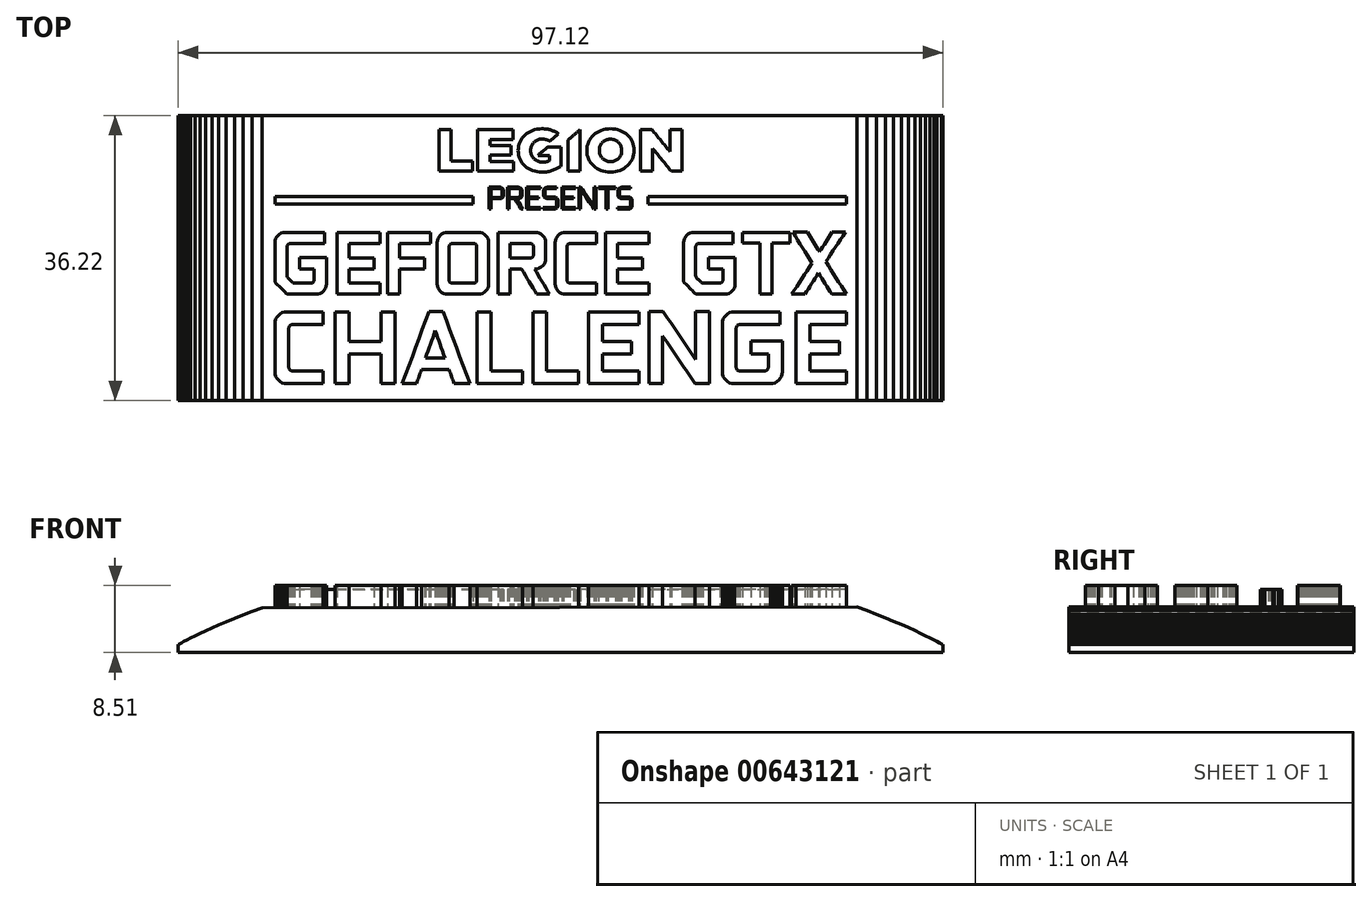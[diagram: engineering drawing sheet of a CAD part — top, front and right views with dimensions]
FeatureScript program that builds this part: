
annotation { "Feature Type Name" : "Feature", "Feature Type Description" : "" }
export const myFeature = defineFeature(function(context is Context, id is Id, definition is map)
    precondition{}
    {
        {
            var Q0;
            Q0=qCreatedBy(makeId("Front.planeOp"),FACE);
            var sketch = newSketch(context, id + "F0", { "sketchPlane" : qUnion([Q0])});
            skLineSegment(sketch, "E0", {"start": v(48.56, -5) * mm, "end": v(48.52, -4.97) * mm});
            skLineSegment(sketch, "E1", {"start": v(48.52, -4.97) * mm, "end": v(48.41, -4.86) * mm});
            skLineSegment(sketch, "E2", {"start": v(48.41, -4.86) * mm, "end": v(48.22, -4.68) * mm});
            skLineSegment(sketch, "E3", {"start": v(48.22, -4.68) * mm, "end": v(47.95, -4.43) * mm});
            skLineSegment(sketch, "E4", {"start": v(47.95, -4.43) * mm, "end": v(47.6, -4.12) * mm});
            skLineSegment(sketch, "E5", {"start": v(47.6, -4.12) * mm, "end": v(47.17, -3.75) * mm});
            skLineSegment(sketch, "E6", {"start": v(47.17, -3.75) * mm, "end": v(46.64, -3.33) * mm});
            skLineSegment(sketch, "E7", {"start": v(46.64, -3.33) * mm, "end": v(46.03, -2.86) * mm});
            skLineSegment(sketch, "E8", {"start": v(46.03, -2.86) * mm, "end": v(45.32, -2.34) * mm});
            skLineSegment(sketch, "E9", {"start": v(45.32, -2.34) * mm, "end": v(44.51, -1.78) * mm});
            skLineSegment(sketch, "E10", {"start": v(44.51, -1.78) * mm, "end": v(43.6, -1.18) * mm});
            skLineSegment(sketch, "E11", {"start": v(43.6, -1.18) * mm, "end": v(42.6, -0.55) * mm});
            skLineSegment(sketch, "E12", {"start": v(42.6, -0.55) * mm, "end": v(41.5, 0.11) * mm});
            skLineSegment(sketch, "E13", {"start": v(41.5, 0.11) * mm, "end": v(40.28, 0.8) * mm});
            skLineSegment(sketch, "E14", {"start": v(40.28, 0.8) * mm, "end": v(38.95, 1.51) * mm});
            skLineSegment(sketch, "E15", {"start": v(38.95, 1.51) * mm, "end": v(37.52, 2.24) * mm});
            skLineSegment(sketch, "E16", {"start": v(37.52, 2.24) * mm, "end": v(36.56, 2.61) * mm});
            skLineSegment(sketch, "E17", {"start": v(36.56, 2.61) * mm, "end": v(35.3, 2.96) * mm});
            skLineSegment(sketch, "E18", {"start": v(35.3, 2.96) * mm, "end": v(33.78, 3.27) * mm});
            skLineSegment(sketch, "E19", {"start": v(33.78, 3.27) * mm, "end": v(32, 3.55) * mm});
            skLineSegment(sketch, "E20", {"start": v(32, 3.55) * mm, "end": v(30, 3.8) * mm});
            skLineSegment(sketch, "E21", {"start": v(30, 3.8) * mm, "end": v(27.78, 4.03) * mm});
            skLineSegment(sketch, "E22", {"start": v(27.78, 4.03) * mm, "end": v(25.4, 4.23) * mm});
            skLineSegment(sketch, "E23", {"start": v(25.4, 4.23) * mm, "end": v(22.87, 4.4) * mm});
            skLineSegment(sketch, "E24", {"start": v(22.87, 4.4) * mm, "end": v(20.2, 4.56) * mm});
            skLineSegment(sketch, "E25", {"start": v(20.2, 4.56) * mm, "end": v(17.44, 4.68) * mm});
            skLineSegment(sketch, "E26", {"start": v(17.44, 4.68) * mm, "end": v(14.6, 4.79) * mm});
            skLineSegment(sketch, "E27", {"start": v(14.6, 4.79) * mm, "end": v(11.7, 4.87) * mm});
            skLineSegment(sketch, "E28", {"start": v(11.7, 4.87) * mm, "end": v(8.79, 4.93) * mm});
            skLineSegment(sketch, "E29", {"start": v(8.79, 4.93) * mm, "end": v(5.86, 4.98) * mm});
            skLineSegment(sketch, "E30", {"start": v(5.86, 4.98) * mm, "end": v(2.96, 5) * mm});
            skLineSegment(sketch, "E31", {"start": v(2.96, 5) * mm, "end": v(0.1, 5) * mm});
            skLineSegment(sketch, "E32", {"start": v(0.1, 5) * mm, "end": v(0.1, 5) * mm});
            skLineSegment(sketch, "E33", {"start": v(0.1, 5) * mm, "end": v(0.08, 5) * mm});
            skLineSegment(sketch, "E34", {"start": v(0.08, 5) * mm, "end": v(0.07, 5) * mm});
            skLineSegment(sketch, "E35", {"start": v(0.07, 5) * mm, "end": v(0.05, 5) * mm});
            skLineSegment(sketch, "E36", {"start": v(0.05, 5) * mm, "end": v(0.04, 5) * mm});
            skLineSegment(sketch, "E37", {"start": v(0.04, 5) * mm, "end": v(0.03, 5) * mm});
            skLineSegment(sketch, "E38", {"start": v(0.03, 5) * mm, "end": v(0.01, 5) * mm});
            skLineSegment(sketch, "E39", {"start": v(0.01, 5) * mm, "end": v(0, 5) * mm});
            skLineSegment(sketch, "E40", {"start": v(0, 5) * mm, "end": v(-0.01, 5) * mm});
            skLineSegment(sketch, "E41", {"start": v(-0.01, 5) * mm, "end": v(-0.03, 5) * mm});
            skLineSegment(sketch, "E42", {"start": v(-0.03, 5) * mm, "end": v(-0.04, 5) * mm});
            skLineSegment(sketch, "E43", {"start": v(-0.04, 5) * mm, "end": v(-0.05, 5) * mm});
            skLineSegment(sketch, "E44", {"start": v(-0.05, 5) * mm, "end": v(-0.07, 5) * mm});
            skLineSegment(sketch, "E45", {"start": v(-0.07, 5) * mm, "end": v(-0.08, 5) * mm});
            skLineSegment(sketch, "E46", {"start": v(-0.08, 5) * mm, "end": v(-0.1, 5) * mm});
            skLineSegment(sketch, "E47", {"start": v(-0.1, 5) * mm, "end": v(-0.1, 5) * mm});
            skLineSegment(sketch, "E48", {"start": v(-0.1, 5) * mm, "end": v(-2.96, 5) * mm});
            skLineSegment(sketch, "E49", {"start": v(-2.96, 5) * mm, "end": v(-5.86, 4.98) * mm});
            skLineSegment(sketch, "E50", {"start": v(-5.86, 4.98) * mm, "end": v(-8.79, 4.93) * mm});
            skLineSegment(sketch, "E51", {"start": v(-8.79, 4.93) * mm, "end": v(-11.7, 4.87) * mm});
            skLineSegment(sketch, "E52", {"start": v(-11.7, 4.87) * mm, "end": v(-14.6, 4.79) * mm});
            skLineSegment(sketch, "E53", {"start": v(-14.6, 4.79) * mm, "end": v(-17.44, 4.68) * mm});
            skLineSegment(sketch, "E54", {"start": v(-17.44, 4.68) * mm, "end": v(-20.2, 4.56) * mm});
            skLineSegment(sketch, "E55", {"start": v(-20.2, 4.56) * mm, "end": v(-22.87, 4.4) * mm});
            skLineSegment(sketch, "E56", {"start": v(-22.87, 4.4) * mm, "end": v(-25.4, 4.23) * mm});
            skLineSegment(sketch, "E57", {"start": v(-25.4, 4.23) * mm, "end": v(-27.79, 4.03) * mm});
            skLineSegment(sketch, "E58", {"start": v(-27.79, 4.03) * mm, "end": v(-30, 3.8) * mm});
            skLineSegment(sketch, "E59", {"start": v(-30, 3.8) * mm, "end": v(-32, 3.55) * mm});
            skLineSegment(sketch, "E60", {"start": v(-32, 3.55) * mm, "end": v(-33.78, 3.27) * mm});
            skLineSegment(sketch, "E61", {"start": v(-33.78, 3.27) * mm, "end": v(-35.3, 2.96) * mm});
            skLineSegment(sketch, "E62", {"start": v(-35.3, 2.96) * mm, "end": v(-36.56, 2.61) * mm});
            skLineSegment(sketch, "E63", {"start": v(-36.56, 2.61) * mm, "end": v(-37.52, 2.24) * mm});
            skLineSegment(sketch, "E64", {"start": v(-37.52, 2.24) * mm, "end": v(-38.95, 1.51) * mm});
            skLineSegment(sketch, "E65", {"start": v(-38.95, 1.51) * mm, "end": v(-40.28, 0.8) * mm});
            skLineSegment(sketch, "E66", {"start": v(-40.28, 0.8) * mm, "end": v(-41.5, 0.11) * mm});
            skLineSegment(sketch, "E67", {"start": v(-41.5, 0.11) * mm, "end": v(-42.6, -0.55) * mm});
            skLineSegment(sketch, "E68", {"start": v(-42.6, -0.55) * mm, "end": v(-43.6, -1.18) * mm});
            skLineSegment(sketch, "E69", {"start": v(-43.6, -1.18) * mm, "end": v(-44.51, -1.78) * mm});
            skLineSegment(sketch, "E70", {"start": v(-44.51, -1.78) * mm, "end": v(-45.32, -2.34) * mm});
            skLineSegment(sketch, "E71", {"start": v(-45.32, -2.34) * mm, "end": v(-46.03, -2.86) * mm});
            skLineSegment(sketch, "E72", {"start": v(-46.03, -2.86) * mm, "end": v(-46.64, -3.33) * mm});
            skLineSegment(sketch, "E73", {"start": v(-46.64, -3.33) * mm, "end": v(-47.17, -3.75) * mm});
            skLineSegment(sketch, "E74", {"start": v(-47.17, -3.75) * mm, "end": v(-47.6, -4.12) * mm});
            skLineSegment(sketch, "E75", {"start": v(-47.6, -4.12) * mm, "end": v(-47.95, -4.43) * mm});
            skLineSegment(sketch, "E76", {"start": v(-47.95, -4.43) * mm, "end": v(-48.22, -4.68) * mm});
            skLineSegment(sketch, "E77", {"start": v(-48.22, -4.68) * mm, "end": v(-48.41, -4.86) * mm});
            skLineSegment(sketch, "E78", {"start": v(-48.41, -4.86) * mm, "end": v(-48.52, -4.97) * mm});
            skLineSegment(sketch, "E79", {"start": v(-48.52, -4.97) * mm, "end": v(-48.56, -5) * mm});
            skLineSegment(sketch, "E80", {"start": v(-48.56, -5) * mm, "end": v(-42.49, -5) * mm});
            skLineSegment(sketch, "E81", {"start": v(-42.49, -5) * mm, "end": v(-36.42, -5) * mm});
            skLineSegment(sketch, "E82", {"start": v(-36.42, -5) * mm, "end": v(-30.35, -5) * mm});
            skLineSegment(sketch, "E83", {"start": v(-30.35, -5) * mm, "end": v(-24.28, -5) * mm});
            skLineSegment(sketch, "E84", {"start": v(-24.28, -5) * mm, "end": v(-18.2, -5) * mm});
            skLineSegment(sketch, "E85", {"start": v(-18.2, -5) * mm, "end": v(-12.14, -5) * mm});
            skLineSegment(sketch, "E86", {"start": v(-12.14, -5) * mm, "end": v(-6.07, -5) * mm});
            skLineSegment(sketch, "E87", {"start": v(-6.07, -5) * mm, "end": v(0, -5) * mm});
            skLineSegment(sketch, "E88", {"start": v(0, -5) * mm, "end": v(6.07, -5) * mm});
            skLineSegment(sketch, "E89", {"start": v(6.07, -5) * mm, "end": v(12.14, -5) * mm});
            skLineSegment(sketch, "E90", {"start": v(12.14, -5) * mm, "end": v(18.2, -5) * mm});
            skLineSegment(sketch, "E91", {"start": v(18.2, -5) * mm, "end": v(24.28, -5) * mm});
            skLineSegment(sketch, "E92", {"start": v(24.28, -5) * mm, "end": v(30.35, -5) * mm});
            skLineSegment(sketch, "E93", {"start": v(30.35, -5) * mm, "end": v(36.42, -5) * mm});
            skLineSegment(sketch, "E94", {"start": v(36.42, -5) * mm, "end": v(42.49, -5) * mm});
            skLineSegment(sketch, "E95", {"start": v(42.49, -5) * mm, "end": v(48.56, -5) * mm});
            skLineSegment(sketch, "E96", {"start": v(48.56, -5) * mm, "end": v(48.51, -4.98) * mm});
            skLineSegment(sketch, "E97", {"start": v(48.51, -4.98) * mm, "end": v(48.38, -4.9) * mm});
            skLineSegment(sketch, "E98", {"start": v(48.38, -4.9) * mm, "end": v(48.15, -4.78) * mm});
            skLineSegment(sketch, "E99", {"start": v(48.15, -4.78) * mm, "end": v(47.84, -4.61) * mm});
            skLineSegment(sketch, "E100", {"start": v(47.84, -4.61) * mm, "end": v(47.44, -4.4) * mm});
            skLineSegment(sketch, "E101", {"start": v(47.44, -4.4) * mm, "end": v(46.95, -4.16) * mm});
            skLineSegment(sketch, "E102", {"start": v(46.95, -4.16) * mm, "end": v(46.38, -3.87) * mm});
            skLineSegment(sketch, "E103", {"start": v(46.38, -3.87) * mm, "end": v(45.73, -3.56) * mm});
            skLineSegment(sketch, "E104", {"start": v(45.73, -3.56) * mm, "end": v(44.99, -3.21) * mm});
            skLineSegment(sketch, "E105", {"start": v(44.99, -3.21) * mm, "end": v(44.17, -2.84) * mm});
            skLineSegment(sketch, "E106", {"start": v(44.17, -2.84) * mm, "end": v(43.28, -2.45) * mm});
            skLineSegment(sketch, "E107", {"start": v(43.28, -2.45) * mm, "end": v(42.3, -2.03) * mm});
            skLineSegment(sketch, "E108", {"start": v(42.3, -2.03) * mm, "end": v(41.25, -1.6) * mm});
            skLineSegment(sketch, "E109", {"start": v(41.25, -1.6) * mm, "end": v(40.13, -1.15) * mm});
            skLineSegment(sketch, "E110", {"start": v(40.13, -1.15) * mm, "end": v(38.93, -0.7) * mm});
            skLineSegment(sketch, "E111", {"start": v(38.93, -0.7) * mm, "end": v(37.66, -0.23) * mm});
            skLineSegment(sketch, "E112", {"start": v(-37.92, -0.32) * mm, "end": v(-39.16, -0.78) * mm});
            skLineSegment(sketch, "E113", {"start": v(-39.16, -0.78) * mm, "end": v(-40.33, -1.23) * mm});
            skLineSegment(sketch, "E114", {"start": v(-40.33, -1.23) * mm, "end": v(-41.43, -1.67) * mm});
            skLineSegment(sketch, "E115", {"start": v(-41.43, -1.67) * mm, "end": v(-42.46, -2.1) * mm});
            skLineSegment(sketch, "E116", {"start": v(-42.46, -2.1) * mm, "end": v(-43.4, -2.5) * mm});
            skLineSegment(sketch, "E117", {"start": v(-43.4, -2.5) * mm, "end": v(-44.28, -2.89) * mm});
            skLineSegment(sketch, "E118", {"start": v(-44.28, -2.89) * mm, "end": v(-45.08, -3.25) * mm});
            skLineSegment(sketch, "E119", {"start": v(-45.08, -3.25) * mm, "end": v(-45.8, -3.6) * mm});
            skLineSegment(sketch, "E120", {"start": v(-45.8, -3.6) * mm, "end": v(-46.43, -3.9) * mm});
            skLineSegment(sketch, "E121", {"start": v(-46.43, -3.9) * mm, "end": v(-46.99, -4.18) * mm});
            skLineSegment(sketch, "E122", {"start": v(-46.99, -4.18) * mm, "end": v(-47.46, -4.42) * mm});
            skLineSegment(sketch, "E123", {"start": v(-47.46, -4.42) * mm, "end": v(-47.85, -4.62) * mm});
            skLineSegment(sketch, "E124", {"start": v(-47.85, -4.62) * mm, "end": v(-48.16, -4.79) * mm});
            skLineSegment(sketch, "E125", {"start": v(-48.16, -4.79) * mm, "end": v(-48.38, -4.9) * mm});
            skLineSegment(sketch, "E126", {"start": v(-48.38, -4.9) * mm, "end": v(-48.51, -4.98) * mm});
            skLineSegment(sketch, "E127", {"start": v(-48.51, -4.98) * mm, "end": v(-48.56, -5) * mm});
            skLineSegment(sketch, "E128", {"start": v(-37.92, -0.32) * mm, "end": v(37.66, -0.23) * mm});
            skSolve(sketch);
        }
        {
            var Q0;
            Q0=makeQuery(id+"F0.imprint","IMPRINT",FACE,{"disambiguationData":[TD([[makeQuery(id+"F0.imprint","IMPRINT",EDGE,{"derivedFrom":sQuery(id+"F0.wireOp",EDGE,"E96")}),1.0]])]});
            extrude(context, id + "F1", {"entities" : qUnion([Q0]), "endBound" : BoundingType.SYMMETRIC, "depth" : 36.2 * mm, "offsetDistance" : 25 * mm});
        }
        {
            var Q0;
            Q0=makeQuery(id+"F1.opExtrude","SWEPT_FACE",FACE,{"disambiguationData":[OSD([sQuery(id+"F0.wireOp",EDGE,"E80"),sQuery(id+"F0.wireOp",EDGE,"E81"),sQuery(id+"F0.wireOp",EDGE,"E82"),sQuery(id+"F0.wireOp",EDGE,"E83"),sQuery(id+"F0.wireOp",EDGE,"E84"),sQuery(id+"F0.wireOp",EDGE,"E85"),sQuery(id+"F0.wireOp",EDGE,"E86"),sQuery(id+"F0.wireOp",EDGE,"E87"),sQuery(id+"F0.wireOp",EDGE,"E88"),sQuery(id+"F0.wireOp",EDGE,"E89"),sQuery(id+"F0.wireOp",EDGE,"E90"),sQuery(id+"F0.wireOp",EDGE,"E91"),sQuery(id+"F0.wireOp",EDGE,"E92"),sQuery(id+"F0.wireOp",EDGE,"E93"),sQuery(id+"F0.wireOp",EDGE,"E94"),sQuery(id+"F0.wireOp",EDGE,"E95")])]});
            extrude(context, id + "F2", {"entities" : qUnion([Q0]), "operationType" : NewBodyOperationType.ADD, "depth" : 1 * mm, "offsetDistance" : 25 * mm});
        }
        {
            var Q0;
            Q0=qCreatedBy(makeId("Top.planeOp"),FACE);
            var sketch = newSketch(context, id + "F3", { "sketchPlane" : qUnion([Q0])});
            skLineSegment(sketch, "E129", {"start": v(-36.3, 1.94) * mm, "end": v(-36.26, 2.2) * mm});
            skLineSegment(sketch, "E130", {"start": v(-36.26, 2.2) * mm, "end": v(-36.19, 2.45) * mm});
            skLineSegment(sketch, "E131", {"start": v(-36.19, 2.45) * mm, "end": v(-36.07, 2.67) * mm});
            skLineSegment(sketch, "E132", {"start": v(-36.07, 2.67) * mm, "end": v(-35.9, 2.87) * mm});
            skLineSegment(sketch, "E133", {"start": v(-35.9, 2.87) * mm, "end": v(-35.71, 3.03) * mm});
            skLineSegment(sketch, "E134", {"start": v(-35.71, 3.03) * mm, "end": v(-35.49, 3.15) * mm});
            skLineSegment(sketch, "E135", {"start": v(-35.49, 3.15) * mm, "end": v(-35.24, 3.22) * mm});
            skLineSegment(sketch, "E136", {"start": v(-35.24, 3.22) * mm, "end": v(-34.98, 3.25) * mm});
            skLineSegment(sketch, "E137", {"start": v(-34.98, 3.25) * mm, "end": v(-34.36, 3.25) * mm});
            skLineSegment(sketch, "E138", {"start": v(-34.36, 3.25) * mm, "end": v(-33.73, 3.25) * mm});
            skLineSegment(sketch, "E139", {"start": v(-33.73, 3.25) * mm, "end": v(-33.11, 3.25) * mm});
            skLineSegment(sketch, "E140", {"start": v(-33.11, 3.25) * mm, "end": v(-32.49, 3.25) * mm});
            skLineSegment(sketch, "E141", {"start": v(-32.49, 3.25) * mm, "end": v(-31.87, 3.25) * mm});
            skLineSegment(sketch, "E142", {"start": v(-31.87, 3.25) * mm, "end": v(-31.25, 3.25) * mm});
            skLineSegment(sketch, "E143", {"start": v(-31.25, 3.25) * mm, "end": v(-30.62, 3.25) * mm});
            skLineSegment(sketch, "E144", {"start": v(-30.62, 3.25) * mm, "end": v(-30, 3.25) * mm});
            skLineSegment(sketch, "E145", {"start": v(-30, 3.25) * mm, "end": v(-30, 3.07) * mm});
            skLineSegment(sketch, "E146", {"start": v(-30, 3.07) * mm, "end": v(-30, 2.9) * mm});
            skLineSegment(sketch, "E147", {"start": v(-30, 2.9) * mm, "end": v(-30, 2.72) * mm});
            skLineSegment(sketch, "E148", {"start": v(-30, 2.72) * mm, "end": v(-30, 2.54) * mm});
            skLineSegment(sketch, "E149", {"start": v(-30, 2.54) * mm, "end": v(-30, 2.37) * mm});
            skLineSegment(sketch, "E150", {"start": v(-30, 2.37) * mm, "end": v(-30, 2.19) * mm});
            skLineSegment(sketch, "E151", {"start": v(-30, 2.19) * mm, "end": v(-30, 2.01) * mm});
            skLineSegment(sketch, "E152", {"start": v(-30, 2.01) * mm, "end": v(-30, 1.83) * mm});
            skLineSegment(sketch, "E153", {"start": v(-30, 1.83) * mm, "end": v(-30.54, 1.83) * mm});
            skLineSegment(sketch, "E154", {"start": v(-30.54, 1.83) * mm, "end": v(-31.09, 1.83) * mm});
            skLineSegment(sketch, "E155", {"start": v(-31.09, 1.83) * mm, "end": v(-31.63, 1.83) * mm});
            skLineSegment(sketch, "E156", {"start": v(-31.63, 1.83) * mm, "end": v(-32.17, 1.83) * mm});
            skLineSegment(sketch, "E157", {"start": v(-32.17, 1.83) * mm, "end": v(-32.72, 1.83) * mm});
            skLineSegment(sketch, "E158", {"start": v(-32.72, 1.83) * mm, "end": v(-33.26, 1.83) * mm});
            skLineSegment(sketch, "E159", {"start": v(-33.26, 1.83) * mm, "end": v(-33.8, 1.83) * mm});
            skLineSegment(sketch, "E160", {"start": v(-33.8, 1.83) * mm, "end": v(-34.34, 1.83) * mm});
            skLineSegment(sketch, "E161", {"start": v(-34.34, 1.83) * mm, "end": v(-34.42, 1.83) * mm});
            skLineSegment(sketch, "E162", {"start": v(-34.42, 1.83) * mm, "end": v(-34.5, 1.8) * mm});
            skLineSegment(sketch, "E163", {"start": v(-34.5, 1.8) * mm, "end": v(-34.57, 1.77) * mm});
            skLineSegment(sketch, "E164", {"start": v(-34.57, 1.77) * mm, "end": v(-34.63, 1.72) * mm});
            skLineSegment(sketch, "E165", {"start": v(-34.63, 1.72) * mm, "end": v(-34.68, 1.66) * mm});
            skLineSegment(sketch, "E166", {"start": v(-34.68, 1.66) * mm, "end": v(-34.72, 1.6) * mm});
            skLineSegment(sketch, "E167", {"start": v(-34.72, 1.6) * mm, "end": v(-34.74, 1.52) * mm});
            skLineSegment(sketch, "E168", {"start": v(-34.74, 1.52) * mm, "end": v(-34.75, 1.44) * mm});
            skLineSegment(sketch, "E169", {"start": v(-34.75, 1.44) * mm, "end": v(-34.75, 0.98) * mm});
            skLineSegment(sketch, "E170", {"start": v(-34.75, 0.98) * mm, "end": v(-34.75, 0.52) * mm});
            skLineSegment(sketch, "E171", {"start": v(-34.75, 0.52) * mm, "end": v(-34.75, 0.06) * mm});
            skLineSegment(sketch, "E172", {"start": v(-34.75, 0.06) * mm, "end": v(-34.75, -0.4) * mm});
            skLineSegment(sketch, "E173", {"start": v(-34.75, -0.4) * mm, "end": v(-34.75, -0.86) * mm});
            skLineSegment(sketch, "E174", {"start": v(-34.75, -0.86) * mm, "end": v(-34.75, -1.32) * mm});
            skLineSegment(sketch, "E175", {"start": v(-34.75, -1.32) * mm, "end": v(-34.75, -1.78) * mm});
            skLineSegment(sketch, "E176", {"start": v(-34.75, -1.78) * mm, "end": v(-34.75, -2.24) * mm});
            skLineSegment(sketch, "E177", {"start": v(-34.75, -2.24) * mm, "end": v(-34.75, -2.28) * mm});
            skLineSegment(sketch, "E178", {"start": v(-34.75, -2.28) * mm, "end": v(-34.74, -2.32) * mm});
            skLineSegment(sketch, "E179", {"start": v(-34.74, -2.32) * mm, "end": v(-34.73, -2.36) * mm});
            skLineSegment(sketch, "E180", {"start": v(-34.73, -2.36) * mm, "end": v(-34.72, -2.4) * mm});
            skLineSegment(sketch, "E181", {"start": v(-34.72, -2.4) * mm, "end": v(-34.7, -2.43) * mm});
            skLineSegment(sketch, "E182", {"start": v(-34.7, -2.43) * mm, "end": v(-34.68, -2.46) * mm});
            skLineSegment(sketch, "E183", {"start": v(-34.68, -2.46) * mm, "end": v(-34.66, -2.5) * mm});
            skLineSegment(sketch, "E184", {"start": v(-34.66, -2.5) * mm, "end": v(-34.63, -2.52) * mm});
            skLineSegment(sketch, "E185", {"start": v(-34.63, -2.52) * mm, "end": v(-34.56, -2.59) * mm});
            skLineSegment(sketch, "E186", {"start": v(-34.56, -2.59) * mm, "end": v(-34.5, -2.66) * mm});
            skLineSegment(sketch, "E187", {"start": v(-34.5, -2.66) * mm, "end": v(-34.42, -2.73) * mm});
            skLineSegment(sketch, "E188", {"start": v(-34.42, -2.73) * mm, "end": v(-34.36, -2.8) * mm});
            skLineSegment(sketch, "E189", {"start": v(-34.36, -2.8) * mm, "end": v(-34.29, -2.86) * mm});
            skLineSegment(sketch, "E190", {"start": v(-34.29, -2.86) * mm, "end": v(-34.22, -2.93) * mm});
            skLineSegment(sketch, "E191", {"start": v(-34.22, -2.93) * mm, "end": v(-34.15, -3) * mm});
            skLineSegment(sketch, "E192", {"start": v(-34.15, -3) * mm, "end": v(-34.08, -3.07) * mm});
            skLineSegment(sketch, "E193", {"start": v(-34.08, -3.07) * mm, "end": v(-34.05, -3.1) * mm});
            skLineSegment(sketch, "E194", {"start": v(-34.05, -3.1) * mm, "end": v(-34.02, -3.12) * mm});
            skLineSegment(sketch, "E195", {"start": v(-34.02, -3.12) * mm, "end": v(-33.98, -3.14) * mm});
            skLineSegment(sketch, "E196", {"start": v(-33.98, -3.14) * mm, "end": v(-33.95, -3.16) * mm});
            skLineSegment(sketch, "E197", {"start": v(-33.95, -3.16) * mm, "end": v(-33.91, -3.17) * mm});
            skLineSegment(sketch, "E198", {"start": v(-33.91, -3.17) * mm, "end": v(-33.87, -3.18) * mm});
            skLineSegment(sketch, "E199", {"start": v(-33.87, -3.18) * mm, "end": v(-33.83, -3.19) * mm});
            skLineSegment(sketch, "E200", {"start": v(-33.83, -3.19) * mm, "end": v(-33.8, -3.19) * mm});
            skLineSegment(sketch, "E201", {"start": v(-33.8, -3.19) * mm, "end": v(-33.53, -3.19) * mm});
            skLineSegment(sketch, "E202", {"start": v(-33.53, -3.19) * mm, "end": v(-33.26, -3.19) * mm});
            skLineSegment(sketch, "E203", {"start": v(-33.26, -3.19) * mm, "end": v(-33, -3.19) * mm});
            skLineSegment(sketch, "E204", {"start": v(-33, -3.19) * mm, "end": v(-32.74, -3.19) * mm});
            skLineSegment(sketch, "E205", {"start": v(-32.74, -3.19) * mm, "end": v(-32.47, -3.19) * mm});
            skLineSegment(sketch, "E206", {"start": v(-32.47, -3.19) * mm, "end": v(-32.21, -3.19) * mm});
            skLineSegment(sketch, "E207", {"start": v(-32.21, -3.19) * mm, "end": v(-31.95, -3.19) * mm});
            skLineSegment(sketch, "E208", {"start": v(-31.95, -3.19) * mm, "end": v(-31.68, -3.19) * mm});
            skLineSegment(sketch, "E209", {"start": v(-31.68, -3.19) * mm, "end": v(-31.6, -3.18) * mm});
            skLineSegment(sketch, "E210", {"start": v(-31.6, -3.18) * mm, "end": v(-31.53, -3.16) * mm});
            skLineSegment(sketch, "E211", {"start": v(-31.53, -3.16) * mm, "end": v(-31.46, -3.12) * mm});
            skLineSegment(sketch, "E212", {"start": v(-31.46, -3.12) * mm, "end": v(-31.4, -3.07) * mm});
            skLineSegment(sketch, "E213", {"start": v(-31.4, -3.07) * mm, "end": v(-31.36, -3.02) * mm});
            skLineSegment(sketch, "E214", {"start": v(-31.36, -3.02) * mm, "end": v(-31.32, -2.95) * mm});
            skLineSegment(sketch, "E215", {"start": v(-31.32, -2.95) * mm, "end": v(-31.3, -2.87) * mm});
            skLineSegment(sketch, "E216", {"start": v(-31.3, -2.87) * mm, "end": v(-31.3, -2.8) * mm});
            skLineSegment(sketch, "E217", {"start": v(-31.3, -2.8) * mm, "end": v(-31.3, -2.62) * mm});
            skLineSegment(sketch, "E218", {"start": v(-31.3, -2.62) * mm, "end": v(-31.3, -2.44) * mm});
            skLineSegment(sketch, "E219", {"start": v(-31.3, -2.44) * mm, "end": v(-31.3, -2.26) * mm});
            skLineSegment(sketch, "E220", {"start": v(-31.3, -2.26) * mm, "end": v(-31.3, -2.09) * mm});
            skLineSegment(sketch, "E221", {"start": v(-31.3, -2.09) * mm, "end": v(-31.3, -1.9) * mm});
            skLineSegment(sketch, "E222", {"start": v(-31.3, -1.9) * mm, "end": v(-31.3, -1.73) * mm});
            skLineSegment(sketch, "E223", {"start": v(-31.3, -1.73) * mm, "end": v(-31.3, -1.56) * mm});
            skLineSegment(sketch, "E224", {"start": v(-31.3, -1.56) * mm, "end": v(-31.3, -1.38) * mm});
            skLineSegment(sketch, "E225", {"start": v(-31.3, -1.38) * mm, "end": v(-31.52, -1.38) * mm});
            skLineSegment(sketch, "E226", {"start": v(-31.52, -1.38) * mm, "end": v(-31.76, -1.38) * mm});
            skLineSegment(sketch, "E227", {"start": v(-31.76, -1.38) * mm, "end": v(-31.99, -1.38) * mm});
            skLineSegment(sketch, "E228", {"start": v(-31.99, -1.38) * mm, "end": v(-32.22, -1.38) * mm});
            skLineSegment(sketch, "E229", {"start": v(-32.22, -1.38) * mm, "end": v(-32.45, -1.38) * mm});
            skLineSegment(sketch, "E230", {"start": v(-32.45, -1.38) * mm, "end": v(-32.68, -1.38) * mm});
            skLineSegment(sketch, "E231", {"start": v(-32.68, -1.38) * mm, "end": v(-32.91, -1.38) * mm});
            skLineSegment(sketch, "E232", {"start": v(-32.91, -1.38) * mm, "end": v(-33.15, -1.38) * mm});
            skLineSegment(sketch, "E233", {"start": v(-33.15, -1.38) * mm, "end": v(-33.15, -1.2) * mm});
            skLineSegment(sketch, "E234", {"start": v(-33.15, -1.2) * mm, "end": v(-33.15, -1.02) * mm});
            skLineSegment(sketch, "E235", {"start": v(-33.15, -1.02) * mm, "end": v(-33.15, -0.85) * mm});
            skLineSegment(sketch, "E236", {"start": v(-33.15, -0.85) * mm, "end": v(-33.15, -0.67) * mm});
            skLineSegment(sketch, "E237", {"start": v(-33.15, -0.67) * mm, "end": v(-33.15, -0.5) * mm});
            skLineSegment(sketch, "E238", {"start": v(-33.15, -0.5) * mm, "end": v(-33.15, -0.32) * mm});
            skLineSegment(sketch, "E239", {"start": v(-33.15, -0.32) * mm, "end": v(-33.15, -0.14) * mm});
            skLineSegment(sketch, "E240", {"start": v(-33.15, -0.14) * mm, "end": v(-33.15, 0.04) * mm});
            skLineSegment(sketch, "E241", {"start": v(-33.15, 0.04) * mm, "end": v(-32.72, 0.04) * mm});
            skLineSegment(sketch, "E242", {"start": v(-32.72, 0.04) * mm, "end": v(-32.3, 0.04) * mm});
            skLineSegment(sketch, "E243", {"start": v(-32.3, 0.04) * mm, "end": v(-31.87, 0.04) * mm});
            skLineSegment(sketch, "E244", {"start": v(-31.87, 0.04) * mm, "end": v(-31.44, 0.04) * mm});
            skLineSegment(sketch, "E245", {"start": v(-31.44, 0.04) * mm, "end": v(-31.02, 0.04) * mm});
            skLineSegment(sketch, "E246", {"start": v(-31.02, 0.04) * mm, "end": v(-30.59, 0.04) * mm});
            skLineSegment(sketch, "E247", {"start": v(-30.59, 0.04) * mm, "end": v(-30.16, 0.04) * mm});
            skLineSegment(sketch, "E248", {"start": v(-30.16, 0.04) * mm, "end": v(-29.74, 0.04) * mm});
            skLineSegment(sketch, "E249", {"start": v(-29.74, 0.04) * mm, "end": v(-29.74, -0.38) * mm});
            skLineSegment(sketch, "E250", {"start": v(-29.74, -0.38) * mm, "end": v(-29.74, -0.8) * mm});
            skLineSegment(sketch, "E251", {"start": v(-29.74, -0.8) * mm, "end": v(-29.74, -1.21) * mm});
            skLineSegment(sketch, "E252", {"start": v(-29.74, -1.21) * mm, "end": v(-29.74, -1.63) * mm});
            skLineSegment(sketch, "E253", {"start": v(-29.74, -1.63) * mm, "end": v(-29.74, -2.05) * mm});
            skLineSegment(sketch, "E254", {"start": v(-29.74, -2.05) * mm, "end": v(-29.74, -2.47) * mm});
            skLineSegment(sketch, "E255", {"start": v(-29.74, -2.47) * mm, "end": v(-29.74, -2.88) * mm});
            skLineSegment(sketch, "E256", {"start": v(-29.74, -2.88) * mm, "end": v(-29.74, -3.3) * mm});
            skLineSegment(sketch, "E257", {"start": v(-29.74, -3.3) * mm, "end": v(-29.76, -3.56) * mm});
            skLineSegment(sketch, "E258", {"start": v(-29.76, -3.56) * mm, "end": v(-29.84, -3.8) * mm});
            skLineSegment(sketch, "E259", {"start": v(-29.84, -3.8) * mm, "end": v(-29.96, -4.03) * mm});
            skLineSegment(sketch, "E260", {"start": v(-29.96, -4.03) * mm, "end": v(-30.12, -4.22) * mm});
            skLineSegment(sketch, "E261", {"start": v(-30.12, -4.22) * mm, "end": v(-30.32, -4.38) * mm});
            skLineSegment(sketch, "E262", {"start": v(-30.32, -4.38) * mm, "end": v(-30.54, -4.5) * mm});
            skLineSegment(sketch, "E263", {"start": v(-30.54, -4.5) * mm, "end": v(-30.79, -4.58) * mm});
            skLineSegment(sketch, "E264", {"start": v(-30.79, -4.58) * mm, "end": v(-31.05, -4.6) * mm});
            skLineSegment(sketch, "E265", {"start": v(-31.05, -4.6) * mm, "end": v(-31.49, -4.6) * mm});
            skLineSegment(sketch, "E266", {"start": v(-31.49, -4.6) * mm, "end": v(-31.93, -4.6) * mm});
            skLineSegment(sketch, "E267", {"start": v(-31.93, -4.6) * mm, "end": v(-32.36, -4.6) * mm});
            skLineSegment(sketch, "E268", {"start": v(-32.36, -4.6) * mm, "end": v(-32.8, -4.6) * mm});
            skLineSegment(sketch, "E269", {"start": v(-32.8, -4.6) * mm, "end": v(-33.24, -4.6) * mm});
            skLineSegment(sketch, "E270", {"start": v(-33.24, -4.6) * mm, "end": v(-33.68, -4.6) * mm});
            skLineSegment(sketch, "E271", {"start": v(-33.68, -4.6) * mm, "end": v(-34.11, -4.6) * mm});
            skLineSegment(sketch, "E272", {"start": v(-34.11, -4.6) * mm, "end": v(-34.55, -4.6) * mm});
            skLineSegment(sketch, "E273", {"start": v(-34.55, -4.6) * mm, "end": v(-34.6, -4.6) * mm});
            skLineSegment(sketch, "E274", {"start": v(-34.6, -4.6) * mm, "end": v(-34.63, -4.6) * mm});
            skLineSegment(sketch, "E275", {"start": v(-34.63, -4.6) * mm, "end": v(-34.67, -4.59) * mm});
            skLineSegment(sketch, "E276", {"start": v(-34.67, -4.59) * mm, "end": v(-34.7, -4.58) * mm});
            skLineSegment(sketch, "E277", {"start": v(-34.7, -4.58) * mm, "end": v(-34.74, -4.56) * mm});
            skLineSegment(sketch, "E278", {"start": v(-34.74, -4.56) * mm, "end": v(-34.77, -4.54) * mm});
            skLineSegment(sketch, "E279", {"start": v(-34.77, -4.54) * mm, "end": v(-34.8, -4.52) * mm});
            skLineSegment(sketch, "E280", {"start": v(-34.8, -4.52) * mm, "end": v(-34.84, -4.49) * mm});
            skLineSegment(sketch, "E281", {"start": v(-34.84, -4.49) * mm, "end": v(-35, -4.32) * mm});
            skLineSegment(sketch, "E282", {"start": v(-35, -4.32) * mm, "end": v(-35.17, -4.15) * mm});
            skLineSegment(sketch, "E283", {"start": v(-35.17, -4.15) * mm, "end": v(-35.34, -3.99) * mm});
            skLineSegment(sketch, "E284", {"start": v(-35.34, -3.99) * mm, "end": v(-35.5, -3.82) * mm});
            skLineSegment(sketch, "E285", {"start": v(-35.5, -3.82) * mm, "end": v(-35.67, -3.65) * mm});
            skLineSegment(sketch, "E286", {"start": v(-35.67, -3.65) * mm, "end": v(-35.84, -3.49) * mm});
            skLineSegment(sketch, "E287", {"start": v(-35.84, -3.49) * mm, "end": v(-36, -3.32) * mm});
            skLineSegment(sketch, "E288", {"start": v(-36, -3.32) * mm, "end": v(-36.18, -3.15) * mm});
            skLineSegment(sketch, "E289", {"start": v(-36.18, -3.15) * mm, "end": v(-36.2, -3.13) * mm});
            skLineSegment(sketch, "E290", {"start": v(-36.2, -3.13) * mm, "end": v(-36.22, -3.1) * mm});
            skLineSegment(sketch, "E291", {"start": v(-36.22, -3.1) * mm, "end": v(-36.24, -3.06) * mm});
            skLineSegment(sketch, "E292", {"start": v(-36.24, -3.06) * mm, "end": v(-36.26, -3.03) * mm});
            skLineSegment(sketch, "E293", {"start": v(-36.26, -3.03) * mm, "end": v(-36.27, -3) * mm});
            skLineSegment(sketch, "E294", {"start": v(-36.27, -3) * mm, "end": v(-36.28, -2.95) * mm});
            skLineSegment(sketch, "E295", {"start": v(-36.28, -2.95) * mm, "end": v(-36.29, -2.92) * mm});
            skLineSegment(sketch, "E296", {"start": v(-36.29, -2.92) * mm, "end": v(-36.3, -2.88) * mm});
            skLineSegment(sketch, "E297", {"start": v(-36.3, -2.88) * mm, "end": v(-36.3, -2.27) * mm});
            skLineSegment(sketch, "E298", {"start": v(-36.3, -2.27) * mm, "end": v(-36.3, -1.67) * mm});
            skLineSegment(sketch, "E299", {"start": v(-36.3, -1.67) * mm, "end": v(-36.3, -1.07) * mm});
            skLineSegment(sketch, "E300", {"start": v(-36.3, -1.07) * mm, "end": v(-36.3, -0.47) * mm});
            skLineSegment(sketch, "E301", {"start": v(-36.3, -0.47) * mm, "end": v(-36.3, 0.13) * mm});
            skLineSegment(sketch, "E302", {"start": v(-36.3, 0.13) * mm, "end": v(-36.3, 0.73) * mm});
            skLineSegment(sketch, "E303", {"start": v(-36.3, 0.73) * mm, "end": v(-36.3, 1.34) * mm});
            skLineSegment(sketch, "E304", {"start": v(-36.3, 1.34) * mm, "end": v(-36.3, 1.94) * mm});
            skLineSegment(sketch, "E305", {"start": v(-26.88, 1.86) * mm, "end": v(-26.88, 1.63) * mm});
            skLineSegment(sketch, "E306", {"start": v(-26.88, 1.63) * mm, "end": v(-26.88, 1.4) * mm});
            skLineSegment(sketch, "E307", {"start": v(-26.88, 1.4) * mm, "end": v(-26.88, 1.17) * mm});
            skLineSegment(sketch, "E308", {"start": v(-26.88, 1.17) * mm, "end": v(-26.88, 0.94) * mm});
            skLineSegment(sketch, "E309", {"start": v(-26.88, 0.94) * mm, "end": v(-26.88, 0.7) * mm});
            skLineSegment(sketch, "E310", {"start": v(-26.88, 0.7) * mm, "end": v(-26.88, 0.48) * mm});
            skLineSegment(sketch, "E311", {"start": v(-26.88, 0.48) * mm, "end": v(-26.88, 0.25) * mm});
            skLineSegment(sketch, "E312", {"start": v(-26.88, 0.25) * mm, "end": v(-26.88, 0.01) * mm});
            skLineSegment(sketch, "E313", {"start": v(-26.88, 0.01) * mm, "end": v(-26.48, 0.01) * mm});
            skLineSegment(sketch, "E314", {"start": v(-26.48, 0.01) * mm, "end": v(-26.08, 0.01) * mm});
            skLineSegment(sketch, "E315", {"start": v(-26.08, 0.01) * mm, "end": v(-25.68, 0.01) * mm});
            skLineSegment(sketch, "E316", {"start": v(-25.68, 0.01) * mm, "end": v(-25.29, 0.01) * mm});
            skLineSegment(sketch, "E317", {"start": v(-25.29, 0.01) * mm, "end": v(-24.89, 0.01) * mm});
            skLineSegment(sketch, "E318", {"start": v(-24.89, 0.01) * mm, "end": v(-24.49, 0.01) * mm});
            skLineSegment(sketch, "E319", {"start": v(-24.49, 0.01) * mm, "end": v(-24.09, 0.01) * mm});
            skLineSegment(sketch, "E320", {"start": v(-24.09, 0.01) * mm, "end": v(-23.7, 0.01) * mm});
            skLineSegment(sketch, "E321", {"start": v(-23.7, 0.01) * mm, "end": v(-23.7, -0.16) * mm});
            skLineSegment(sketch, "E322", {"start": v(-23.7, -0.16) * mm, "end": v(-23.7, -0.33) * mm});
            skLineSegment(sketch, "E323", {"start": v(-23.7, -0.33) * mm, "end": v(-23.7, -0.5) * mm});
            skLineSegment(sketch, "E324", {"start": v(-23.7, -0.5) * mm, "end": v(-23.7, -0.68) * mm});
            skLineSegment(sketch, "E325", {"start": v(-23.7, -0.68) * mm, "end": v(-23.7, -0.86) * mm});
            skLineSegment(sketch, "E326", {"start": v(-23.7, -0.86) * mm, "end": v(-23.7, -1.03) * mm});
            skLineSegment(sketch, "E327", {"start": v(-23.7, -1.03) * mm, "end": v(-23.7, -1.2) * mm});
            skLineSegment(sketch, "E328", {"start": v(-23.7, -1.2) * mm, "end": v(-23.7, -1.38) * mm});
            skLineSegment(sketch, "E329", {"start": v(-23.7, -1.38) * mm, "end": v(-24.09, -1.38) * mm});
            skLineSegment(sketch, "E330", {"start": v(-24.09, -1.38) * mm, "end": v(-24.49, -1.38) * mm});
            skLineSegment(sketch, "E331", {"start": v(-24.49, -1.38) * mm, "end": v(-24.89, -1.38) * mm});
            skLineSegment(sketch, "E332", {"start": v(-24.89, -1.38) * mm, "end": v(-25.29, -1.38) * mm});
            skLineSegment(sketch, "E333", {"start": v(-25.29, -1.38) * mm, "end": v(-25.68, -1.38) * mm});
            skLineSegment(sketch, "E334", {"start": v(-25.68, -1.38) * mm, "end": v(-26.08, -1.38) * mm});
            skLineSegment(sketch, "E335", {"start": v(-26.08, -1.38) * mm, "end": v(-26.48, -1.38) * mm});
            skLineSegment(sketch, "E336", {"start": v(-26.48, -1.38) * mm, "end": v(-26.88, -1.38) * mm});
            skLineSegment(sketch, "E337", {"start": v(-26.88, -1.38) * mm, "end": v(-26.88, -1.6) * mm});
            skLineSegment(sketch, "E338", {"start": v(-26.88, -1.6) * mm, "end": v(-26.88, -1.84) * mm});
            skLineSegment(sketch, "E339", {"start": v(-26.88, -1.84) * mm, "end": v(-26.88, -2.07) * mm});
            skLineSegment(sketch, "E340", {"start": v(-26.88, -2.07) * mm, "end": v(-26.88, -2.3) * mm});
            skLineSegment(sketch, "E341", {"start": v(-26.88, -2.3) * mm, "end": v(-26.88, -2.52) * mm});
            skLineSegment(sketch, "E342", {"start": v(-26.88, -2.52) * mm, "end": v(-26.88, -2.75) * mm});
            skLineSegment(sketch, "E343", {"start": v(-26.88, -2.75) * mm, "end": v(-26.88, -2.98) * mm});
            skLineSegment(sketch, "E344", {"start": v(-26.88, -2.98) * mm, "end": v(-26.88, -3.2) * mm});
            skLineSegment(sketch, "E345", {"start": v(-26.88, -3.2) * mm, "end": v(-26.38, -3.2) * mm});
            skLineSegment(sketch, "E346", {"start": v(-26.38, -3.2) * mm, "end": v(-25.89, -3.2) * mm});
            skLineSegment(sketch, "E347", {"start": v(-25.89, -3.2) * mm, "end": v(-25.4, -3.2) * mm});
            skLineSegment(sketch, "E348", {"start": v(-25.4, -3.2) * mm, "end": v(-24.9, -3.2) * mm});
            skLineSegment(sketch, "E349", {"start": v(-24.9, -3.2) * mm, "end": v(-24.4, -3.2) * mm});
            skLineSegment(sketch, "E350", {"start": v(-24.4, -3.2) * mm, "end": v(-23.9, -3.2) * mm});
            skLineSegment(sketch, "E351", {"start": v(-23.9, -3.2) * mm, "end": v(-23.4, -3.2) * mm});
            skLineSegment(sketch, "E352", {"start": v(-23.4, -3.2) * mm, "end": v(-22.9, -3.2) * mm});
            skLineSegment(sketch, "E353", {"start": v(-22.9, -3.2) * mm, "end": v(-22.9, -3.38) * mm});
            skLineSegment(sketch, "E354", {"start": v(-22.9, -3.38) * mm, "end": v(-22.9, -3.56) * mm});
            skLineSegment(sketch, "E355", {"start": v(-22.9, -3.56) * mm, "end": v(-22.9, -3.73) * mm});
            skLineSegment(sketch, "E356", {"start": v(-22.9, -3.73) * mm, "end": v(-22.9, -3.9) * mm});
            skLineSegment(sketch, "E357", {"start": v(-22.9, -3.9) * mm, "end": v(-22.9, -4.08) * mm});
            skLineSegment(sketch, "E358", {"start": v(-22.9, -4.08) * mm, "end": v(-22.9, -4.26) * mm});
            skLineSegment(sketch, "E359", {"start": v(-22.9, -4.26) * mm, "end": v(-22.9, -4.43) * mm});
            skLineSegment(sketch, "E360", {"start": v(-22.9, -4.43) * mm, "end": v(-22.9, -4.6) * mm});
            skLineSegment(sketch, "E361", {"start": v(-22.9, -4.6) * mm, "end": v(-23.6, -4.6) * mm});
            skLineSegment(sketch, "E362", {"start": v(-23.6, -4.6) * mm, "end": v(-24.28, -4.6) * mm});
            skLineSegment(sketch, "E363", {"start": v(-24.28, -4.6) * mm, "end": v(-24.97, -4.6) * mm});
            skLineSegment(sketch, "E364", {"start": v(-24.97, -4.6) * mm, "end": v(-25.66, -4.6) * mm});
            skLineSegment(sketch, "E365", {"start": v(-25.66, -4.6) * mm, "end": v(-26.35, -4.6) * mm});
            skLineSegment(sketch, "E366", {"start": v(-26.35, -4.6) * mm, "end": v(-27.04, -4.6) * mm});
            skLineSegment(sketch, "E367", {"start": v(-27.04, -4.6) * mm, "end": v(-27.72, -4.6) * mm});
            skLineSegment(sketch, "E368", {"start": v(-27.72, -4.6) * mm, "end": v(-28.41, -4.6) * mm});
            skLineSegment(sketch, "E369", {"start": v(-28.41, -4.6) * mm, "end": v(-28.41, -3.62) * mm});
            skLineSegment(sketch, "E370", {"start": v(-28.41, -3.62) * mm, "end": v(-28.41, -2.64) * mm});
            skLineSegment(sketch, "E371", {"start": v(-28.41, -2.64) * mm, "end": v(-28.41, -1.66) * mm});
            skLineSegment(sketch, "E372", {"start": v(-28.41, -1.66) * mm, "end": v(-28.41, -0.68) * mm});
            skLineSegment(sketch, "E373", {"start": v(-28.41, -0.68) * mm, "end": v(-28.41, 0.3) * mm});
            skLineSegment(sketch, "E374", {"start": v(-28.41, 0.3) * mm, "end": v(-28.41, 1.29) * mm});
            skLineSegment(sketch, "E375", {"start": v(-28.41, 1.29) * mm, "end": v(-28.41, 2.27) * mm});
            skLineSegment(sketch, "E376", {"start": v(-28.41, 2.27) * mm, "end": v(-28.41, 3.25) * mm});
            skLineSegment(sketch, "E377", {"start": v(-28.41, 3.25) * mm, "end": v(-27.72, 3.25) * mm});
            skLineSegment(sketch, "E378", {"start": v(-27.72, 3.25) * mm, "end": v(-27.04, 3.25) * mm});
            skLineSegment(sketch, "E379", {"start": v(-27.04, 3.25) * mm, "end": v(-26.35, 3.25) * mm});
            skLineSegment(sketch, "E380", {"start": v(-26.35, 3.25) * mm, "end": v(-25.66, 3.25) * mm});
            skLineSegment(sketch, "E381", {"start": v(-25.66, 3.25) * mm, "end": v(-24.97, 3.25) * mm});
            skLineSegment(sketch, "E382", {"start": v(-24.97, 3.25) * mm, "end": v(-24.28, 3.25) * mm});
            skLineSegment(sketch, "E383", {"start": v(-24.28, 3.25) * mm, "end": v(-23.6, 3.25) * mm});
            skLineSegment(sketch, "E384", {"start": v(-23.6, 3.25) * mm, "end": v(-22.9, 3.25) * mm});
            skLineSegment(sketch, "E385", {"start": v(-22.9, 3.25) * mm, "end": v(-22.9, 3.08) * mm});
            skLineSegment(sketch, "E386", {"start": v(-22.9, 3.08) * mm, "end": v(-22.9, 2.9) * mm});
            skLineSegment(sketch, "E387", {"start": v(-22.9, 2.9) * mm, "end": v(-22.9, 2.73) * mm});
            skLineSegment(sketch, "E388", {"start": v(-22.9, 2.73) * mm, "end": v(-22.9, 2.55) * mm});
            skLineSegment(sketch, "E389", {"start": v(-22.9, 2.55) * mm, "end": v(-22.9, 2.38) * mm});
            skLineSegment(sketch, "E390", {"start": v(-22.9, 2.38) * mm, "end": v(-22.9, 2.2) * mm});
            skLineSegment(sketch, "E391", {"start": v(-22.9, 2.2) * mm, "end": v(-22.9, 2.03) * mm});
            skLineSegment(sketch, "E392", {"start": v(-22.9, 2.03) * mm, "end": v(-22.9, 1.86) * mm});
            skLineSegment(sketch, "E393", {"start": v(-22.9, 1.86) * mm, "end": v(-23.4, 1.86) * mm});
            skLineSegment(sketch, "E394", {"start": v(-23.4, 1.86) * mm, "end": v(-23.9, 1.86) * mm});
            skLineSegment(sketch, "E395", {"start": v(-23.9, 1.86) * mm, "end": v(-24.4, 1.86) * mm});
            skLineSegment(sketch, "E396", {"start": v(-24.4, 1.86) * mm, "end": v(-24.9, 1.86) * mm});
            skLineSegment(sketch, "E397", {"start": v(-24.9, 1.86) * mm, "end": v(-25.4, 1.86) * mm});
            skLineSegment(sketch, "E398", {"start": v(-25.4, 1.86) * mm, "end": v(-25.89, 1.86) * mm});
            skLineSegment(sketch, "E399", {"start": v(-25.89, 1.86) * mm, "end": v(-26.38, 1.86) * mm});
            skLineSegment(sketch, "E400", {"start": v(-26.38, 1.86) * mm, "end": v(-26.88, 1.86) * mm});
            skLineSegment(sketch, "E401", {"start": v(-20.45, -4.6) * mm, "end": v(-20.65, -4.6) * mm});
            skLineSegment(sketch, "E402", {"start": v(-20.65, -4.6) * mm, "end": v(-20.84, -4.6) * mm});
            skLineSegment(sketch, "E403", {"start": v(-20.84, -4.6) * mm, "end": v(-21.03, -4.6) * mm});
            skLineSegment(sketch, "E404", {"start": v(-21.03, -4.6) * mm, "end": v(-21.22, -4.6) * mm});
            skLineSegment(sketch, "E405", {"start": v(-21.22, -4.6) * mm, "end": v(-21.41, -4.6) * mm});
            skLineSegment(sketch, "E406", {"start": v(-21.41, -4.6) * mm, "end": v(-21.6, -4.6) * mm});
            skLineSegment(sketch, "E407", {"start": v(-21.6, -4.6) * mm, "end": v(-21.8, -4.6) * mm});
            skLineSegment(sketch, "E408", {"start": v(-21.8, -4.6) * mm, "end": v(-21.99, -4.6) * mm});
            skLineSegment(sketch, "E409", {"start": v(-21.99, -4.6) * mm, "end": v(-21.99, -3.62) * mm});
            skLineSegment(sketch, "E410", {"start": v(-21.99, -3.62) * mm, "end": v(-21.99, -2.64) * mm});
            skLineSegment(sketch, "E411", {"start": v(-21.99, -2.64) * mm, "end": v(-21.99, -1.66) * mm});
            skLineSegment(sketch, "E412", {"start": v(-21.99, -1.66) * mm, "end": v(-21.99, -0.68) * mm});
            skLineSegment(sketch, "E413", {"start": v(-21.99, -0.68) * mm, "end": v(-21.99, 0.3) * mm});
            skLineSegment(sketch, "E414", {"start": v(-21.99, 0.3) * mm, "end": v(-21.99, 1.29) * mm});
            skLineSegment(sketch, "E415", {"start": v(-21.99, 1.29) * mm, "end": v(-21.99, 2.27) * mm});
            skLineSegment(sketch, "E416", {"start": v(-21.99, 2.27) * mm, "end": v(-21.99, 3.25) * mm});
            skLineSegment(sketch, "E417", {"start": v(-21.99, 3.25) * mm, "end": v(-21.3, 3.25) * mm});
            skLineSegment(sketch, "E418", {"start": v(-21.3, 3.25) * mm, "end": v(-20.61, 3.25) * mm});
            skLineSegment(sketch, "E419", {"start": v(-20.61, 3.25) * mm, "end": v(-19.92, 3.25) * mm});
            skLineSegment(sketch, "E420", {"start": v(-19.92, 3.25) * mm, "end": v(-19.23, 3.25) * mm});
            skLineSegment(sketch, "E421", {"start": v(-19.23, 3.25) * mm, "end": v(-18.55, 3.25) * mm});
            skLineSegment(sketch, "E422", {"start": v(-18.55, 3.25) * mm, "end": v(-17.86, 3.25) * mm});
            skLineSegment(sketch, "E423", {"start": v(-17.86, 3.25) * mm, "end": v(-17.17, 3.25) * mm});
            skLineSegment(sketch, "E424", {"start": v(-17.17, 3.25) * mm, "end": v(-16.48, 3.25) * mm});
            skLineSegment(sketch, "E425", {"start": v(-16.48, 3.25) * mm, "end": v(-16.48, 3.08) * mm});
            skLineSegment(sketch, "E426", {"start": v(-16.48, 3.08) * mm, "end": v(-16.48, 2.9) * mm});
            skLineSegment(sketch, "E427", {"start": v(-16.48, 2.9) * mm, "end": v(-16.48, 2.73) * mm});
            skLineSegment(sketch, "E428", {"start": v(-16.48, 2.73) * mm, "end": v(-16.48, 2.55) * mm});
            skLineSegment(sketch, "E429", {"start": v(-16.48, 2.55) * mm, "end": v(-16.48, 2.38) * mm});
            skLineSegment(sketch, "E430", {"start": v(-16.48, 2.38) * mm, "end": v(-16.48, 2.2) * mm});
            skLineSegment(sketch, "E431", {"start": v(-16.48, 2.2) * mm, "end": v(-16.48, 2.03) * mm});
            skLineSegment(sketch, "E432", {"start": v(-16.48, 2.03) * mm, "end": v(-16.48, 1.86) * mm});
            skLineSegment(sketch, "E433", {"start": v(-16.48, 1.86) * mm, "end": v(-16.98, 1.86) * mm});
            skLineSegment(sketch, "E434", {"start": v(-16.98, 1.86) * mm, "end": v(-17.47, 1.86) * mm});
            skLineSegment(sketch, "E435", {"start": v(-17.47, 1.86) * mm, "end": v(-17.97, 1.86) * mm});
            skLineSegment(sketch, "E436", {"start": v(-17.97, 1.86) * mm, "end": v(-18.47, 1.86) * mm});
            skLineSegment(sketch, "E437", {"start": v(-18.47, 1.86) * mm, "end": v(-18.96, 1.86) * mm});
            skLineSegment(sketch, "E438", {"start": v(-18.96, 1.86) * mm, "end": v(-19.46, 1.86) * mm});
            skLineSegment(sketch, "E439", {"start": v(-19.46, 1.86) * mm, "end": v(-19.96, 1.86) * mm});
            skLineSegment(sketch, "E440", {"start": v(-19.96, 1.86) * mm, "end": v(-20.45, 1.86) * mm});
            skLineSegment(sketch, "E441", {"start": v(-20.45, 1.86) * mm, "end": v(-20.45, 1.63) * mm});
            skLineSegment(sketch, "E442", {"start": v(-20.45, 1.63) * mm, "end": v(-20.45, 1.4) * mm});
            skLineSegment(sketch, "E443", {"start": v(-20.45, 1.4) * mm, "end": v(-20.45, 1.17) * mm});
            skLineSegment(sketch, "E444", {"start": v(-20.45, 1.17) * mm, "end": v(-20.45, 0.94) * mm});
            skLineSegment(sketch, "E445", {"start": v(-20.45, 0.94) * mm, "end": v(-20.45, 0.7) * mm});
            skLineSegment(sketch, "E446", {"start": v(-20.45, 0.7) * mm, "end": v(-20.45, 0.48) * mm});
            skLineSegment(sketch, "E447", {"start": v(-20.45, 0.48) * mm, "end": v(-20.45, 0.25) * mm});
            skLineSegment(sketch, "E448", {"start": v(-20.45, 0.25) * mm, "end": v(-20.45, 0.01) * mm});
            skLineSegment(sketch, "E449", {"start": v(-20.45, 0.01) * mm, "end": v(-20.06, 0.01) * mm});
            skLineSegment(sketch, "E450", {"start": v(-20.06, 0.01) * mm, "end": v(-19.66, 0.01) * mm});
            skLineSegment(sketch, "E451", {"start": v(-19.66, 0.01) * mm, "end": v(-19.26, 0.01) * mm});
            skLineSegment(sketch, "E452", {"start": v(-19.26, 0.01) * mm, "end": v(-18.86, 0.01) * mm});
            skLineSegment(sketch, "E453", {"start": v(-18.86, 0.01) * mm, "end": v(-18.46, 0.01) * mm});
            skLineSegment(sketch, "E454", {"start": v(-18.46, 0.01) * mm, "end": v(-18.06, 0.01) * mm});
            skLineSegment(sketch, "E455", {"start": v(-18.06, 0.01) * mm, "end": v(-17.66, 0.01) * mm});
            skLineSegment(sketch, "E456", {"start": v(-17.66, 0.01) * mm, "end": v(-17.26, 0.01) * mm});
            skLineSegment(sketch, "E457", {"start": v(-17.26, 0.01) * mm, "end": v(-17.26, -0.16) * mm});
            skLineSegment(sketch, "E458", {"start": v(-17.26, -0.16) * mm, "end": v(-17.26, -0.33) * mm});
            skLineSegment(sketch, "E459", {"start": v(-17.26, -0.33) * mm, "end": v(-17.26, -0.5) * mm});
            skLineSegment(sketch, "E460", {"start": v(-17.26, -0.5) * mm, "end": v(-17.26, -0.68) * mm});
            skLineSegment(sketch, "E461", {"start": v(-17.26, -0.68) * mm, "end": v(-17.26, -0.86) * mm});
            skLineSegment(sketch, "E462", {"start": v(-17.26, -0.86) * mm, "end": v(-17.26, -1.03) * mm});
            skLineSegment(sketch, "E463", {"start": v(-17.26, -1.03) * mm, "end": v(-17.26, -1.2) * mm});
            skLineSegment(sketch, "E464", {"start": v(-17.26, -1.2) * mm, "end": v(-17.26, -1.38) * mm});
            skLineSegment(sketch, "E465", {"start": v(-17.26, -1.38) * mm, "end": v(-17.66, -1.38) * mm});
            skLineSegment(sketch, "E466", {"start": v(-17.66, -1.38) * mm, "end": v(-18.06, -1.38) * mm});
            skLineSegment(sketch, "E467", {"start": v(-18.06, -1.38) * mm, "end": v(-18.46, -1.38) * mm});
            skLineSegment(sketch, "E468", {"start": v(-18.46, -1.38) * mm, "end": v(-18.86, -1.38) * mm});
            skLineSegment(sketch, "E469", {"start": v(-18.86, -1.38) * mm, "end": v(-19.26, -1.38) * mm});
            skLineSegment(sketch, "E470", {"start": v(-19.26, -1.38) * mm, "end": v(-19.66, -1.38) * mm});
            skLineSegment(sketch, "E471", {"start": v(-19.66, -1.38) * mm, "end": v(-20.06, -1.38) * mm});
            skLineSegment(sketch, "E472", {"start": v(-20.06, -1.38) * mm, "end": v(-20.45, -1.38) * mm});
            skLineSegment(sketch, "E473", {"start": v(-20.45, -1.38) * mm, "end": v(-20.45, -1.78) * mm});
            skLineSegment(sketch, "E474", {"start": v(-20.45, -1.78) * mm, "end": v(-20.45, -2.19) * mm});
            skLineSegment(sketch, "E475", {"start": v(-20.45, -2.19) * mm, "end": v(-20.45, -2.59) * mm});
            skLineSegment(sketch, "E476", {"start": v(-20.45, -2.59) * mm, "end": v(-20.45, -3) * mm});
            skLineSegment(sketch, "E477", {"start": v(-20.45, -3) * mm, "end": v(-20.45, -3.4) * mm});
            skLineSegment(sketch, "E478", {"start": v(-20.45, -3.4) * mm, "end": v(-20.45, -3.8) * mm});
            skLineSegment(sketch, "E479", {"start": v(-20.45, -3.8) * mm, "end": v(-20.45, -4.2) * mm});
            skLineSegment(sketch, "E480", {"start": v(-20.45, -4.2) * mm, "end": v(-20.45, -4.6) * mm});
            skLineSegment(sketch, "E481", {"start": v(-15.67, 1.94) * mm, "end": v(-15.65, 2.2) * mm});
            skLineSegment(sketch, "E482", {"start": v(-15.65, 2.2) * mm, "end": v(-15.57, 2.45) * mm});
            skLineSegment(sketch, "E483", {"start": v(-15.57, 2.45) * mm, "end": v(-15.45, 2.67) * mm});
            skLineSegment(sketch, "E484", {"start": v(-15.45, 2.67) * mm, "end": v(-15.3, 2.87) * mm});
            skLineSegment(sketch, "E485", {"start": v(-15.3, 2.87) * mm, "end": v(-15.1, 3.03) * mm});
            skLineSegment(sketch, "E486", {"start": v(-15.1, 3.03) * mm, "end": v(-14.88, 3.15) * mm});
            skLineSegment(sketch, "E487", {"start": v(-14.88, 3.15) * mm, "end": v(-14.63, 3.22) * mm});
            skLineSegment(sketch, "E488", {"start": v(-14.63, 3.22) * mm, "end": v(-14.37, 3.25) * mm});
            skLineSegment(sketch, "E489", {"start": v(-14.37, 3.25) * mm, "end": v(-13.88, 3.25) * mm});
            skLineSegment(sketch, "E490", {"start": v(-13.88, 3.25) * mm, "end": v(-13.39, 3.25) * mm});
            skLineSegment(sketch, "E491", {"start": v(-13.39, 3.25) * mm, "end": v(-12.9, 3.25) * mm});
            skLineSegment(sketch, "E492", {"start": v(-12.9, 3.25) * mm, "end": v(-12.4, 3.25) * mm});
            skLineSegment(sketch, "E493", {"start": v(-12.4, 3.25) * mm, "end": v(-11.91, 3.25) * mm});
            skLineSegment(sketch, "E494", {"start": v(-11.91, 3.25) * mm, "end": v(-11.42, 3.25) * mm});
            skLineSegment(sketch, "E495", {"start": v(-11.42, 3.25) * mm, "end": v(-10.93, 3.25) * mm});
            skLineSegment(sketch, "E496", {"start": v(-10.93, 3.25) * mm, "end": v(-10.43, 3.25) * mm});
            skLineSegment(sketch, "E497", {"start": v(-10.43, 3.25) * mm, "end": v(-10.17, 3.22) * mm});
            skLineSegment(sketch, "E498", {"start": v(-10.17, 3.22) * mm, "end": v(-9.93, 3.15) * mm});
            skLineSegment(sketch, "E499", {"start": v(-9.93, 3.15) * mm, "end": v(-9.7, 3.03) * mm});
            skLineSegment(sketch, "E500", {"start": v(-9.7, 3.03) * mm, "end": v(-9.52, 2.87) * mm});
            skLineSegment(sketch, "E501", {"start": v(-9.52, 2.87) * mm, "end": v(-9.36, 2.67) * mm});
            skLineSegment(sketch, "E502", {"start": v(-9.36, 2.67) * mm, "end": v(-9.24, 2.45) * mm});
            skLineSegment(sketch, "E503", {"start": v(-9.24, 2.45) * mm, "end": v(-9.16, 2.2) * mm});
            skLineSegment(sketch, "E504", {"start": v(-9.16, 2.2) * mm, "end": v(-9.13, 1.94) * mm});
            skLineSegment(sketch, "E505", {"start": v(-9.13, 1.94) * mm, "end": v(-9.13, 1.28) * mm});
            skLineSegment(sketch, "E506", {"start": v(-9.13, 1.28) * mm, "end": v(-9.13, 0.63) * mm});
            skLineSegment(sketch, "E507", {"start": v(-9.13, 0.63) * mm, "end": v(-9.13, -0.03) * mm});
            skLineSegment(sketch, "E508", {"start": v(-9.13, -0.03) * mm, "end": v(-9.13, -0.68) * mm});
            skLineSegment(sketch, "E509", {"start": v(-9.13, -0.68) * mm, "end": v(-9.13, -1.34) * mm});
            skLineSegment(sketch, "E510", {"start": v(-9.13, -1.34) * mm, "end": v(-9.13, -2) * mm});
            skLineSegment(sketch, "E511", {"start": v(-9.13, -2) * mm, "end": v(-9.13, -2.65) * mm});
            skLineSegment(sketch, "E512", {"start": v(-9.13, -2.65) * mm, "end": v(-9.13, -3.3) * mm});
            skLineSegment(sketch, "E513", {"start": v(-9.13, -3.3) * mm, "end": v(-9.16, -3.57) * mm});
            skLineSegment(sketch, "E514", {"start": v(-9.16, -3.57) * mm, "end": v(-9.24, -3.81) * mm});
            skLineSegment(sketch, "E515", {"start": v(-9.24, -3.81) * mm, "end": v(-9.36, -4.03) * mm});
            skLineSegment(sketch, "E516", {"start": v(-9.36, -4.03) * mm, "end": v(-9.52, -4.23) * mm});
            skLineSegment(sketch, "E517", {"start": v(-9.52, -4.23) * mm, "end": v(-9.7, -4.38) * mm});
            skLineSegment(sketch, "E518", {"start": v(-9.7, -4.38) * mm, "end": v(-9.93, -4.5) * mm});
            skLineSegment(sketch, "E519", {"start": v(-9.93, -4.5) * mm, "end": v(-10.17, -4.58) * mm});
            skLineSegment(sketch, "E520", {"start": v(-10.17, -4.58) * mm, "end": v(-10.43, -4.6) * mm});
            skLineSegment(sketch, "E521", {"start": v(-10.43, -4.6) * mm, "end": v(-10.93, -4.6) * mm});
            skLineSegment(sketch, "E522", {"start": v(-10.93, -4.6) * mm, "end": v(-11.42, -4.6) * mm});
            skLineSegment(sketch, "E523", {"start": v(-11.42, -4.6) * mm, "end": v(-11.91, -4.6) * mm});
            skLineSegment(sketch, "E524", {"start": v(-11.91, -4.6) * mm, "end": v(-12.4, -4.6) * mm});
            skLineSegment(sketch, "E525", {"start": v(-12.4, -4.6) * mm, "end": v(-12.9, -4.6) * mm});
            skLineSegment(sketch, "E526", {"start": v(-12.9, -4.6) * mm, "end": v(-13.39, -4.6) * mm});
            skLineSegment(sketch, "E527", {"start": v(-13.39, -4.6) * mm, "end": v(-13.88, -4.6) * mm});
            skLineSegment(sketch, "E528", {"start": v(-13.88, -4.6) * mm, "end": v(-14.37, -4.6) * mm});
            skLineSegment(sketch, "E529", {"start": v(-14.37, -4.6) * mm, "end": v(-14.63, -4.58) * mm});
            skLineSegment(sketch, "E530", {"start": v(-14.63, -4.58) * mm, "end": v(-14.88, -4.5) * mm});
            skLineSegment(sketch, "E531", {"start": v(-14.88, -4.5) * mm, "end": v(-15.1, -4.38) * mm});
            skLineSegment(sketch, "E532", {"start": v(-15.1, -4.38) * mm, "end": v(-15.3, -4.23) * mm});
            skLineSegment(sketch, "E533", {"start": v(-15.3, -4.23) * mm, "end": v(-15.45, -4.03) * mm});
            skLineSegment(sketch, "E534", {"start": v(-15.45, -4.03) * mm, "end": v(-15.57, -3.81) * mm});
            skLineSegment(sketch, "E535", {"start": v(-15.57, -3.81) * mm, "end": v(-15.65, -3.57) * mm});
            skLineSegment(sketch, "E536", {"start": v(-15.65, -3.57) * mm, "end": v(-15.67, -3.3) * mm});
            skLineSegment(sketch, "E537", {"start": v(-15.67, -3.3) * mm, "end": v(-15.67, -2.65) * mm});
            skLineSegment(sketch, "E538", {"start": v(-15.67, -2.65) * mm, "end": v(-15.67, -2) * mm});
            skLineSegment(sketch, "E539", {"start": v(-15.67, -2) * mm, "end": v(-15.67, -1.34) * mm});
            skLineSegment(sketch, "E540", {"start": v(-15.67, -1.34) * mm, "end": v(-15.67, -0.68) * mm});
            skLineSegment(sketch, "E541", {"start": v(-15.67, -0.68) * mm, "end": v(-15.67, -0.03) * mm});
            skLineSegment(sketch, "E542", {"start": v(-15.67, -0.03) * mm, "end": v(-15.67, 0.63) * mm});
            skLineSegment(sketch, "E543", {"start": v(-15.67, 0.63) * mm, "end": v(-15.67, 1.28) * mm});
            skLineSegment(sketch, "E544", {"start": v(-15.67, 1.28) * mm, "end": v(-15.67, 1.94) * mm});
            skLineSegment(sketch, "E545", {"start": v(-11.04, -3.2) * mm, "end": v(-10.97, -3.2) * mm});
            skLineSegment(sketch, "E546", {"start": v(-10.97, -3.2) * mm, "end": v(-10.9, -3.18) * mm});
            skLineSegment(sketch, "E547", {"start": v(-10.9, -3.18) * mm, "end": v(-10.82, -3.14) * mm});
            skLineSegment(sketch, "E548", {"start": v(-10.82, -3.14) * mm, "end": v(-10.77, -3.1) * mm});
            skLineSegment(sketch, "E549", {"start": v(-10.77, -3.1) * mm, "end": v(-10.72, -3.04) * mm});
            skLineSegment(sketch, "E550", {"start": v(-10.72, -3.04) * mm, "end": v(-10.68, -2.97) * mm});
            skLineSegment(sketch, "E551", {"start": v(-10.68, -2.97) * mm, "end": v(-10.66, -2.9) * mm});
            skLineSegment(sketch, "E552", {"start": v(-10.66, -2.9) * mm, "end": v(-10.65, -2.82) * mm});
            skLineSegment(sketch, "E553", {"start": v(-10.65, -2.82) * mm, "end": v(-10.65, -2.28) * mm});
            skLineSegment(sketch, "E554", {"start": v(-10.65, -2.28) * mm, "end": v(-10.65, -1.75) * mm});
            skLineSegment(sketch, "E555", {"start": v(-10.65, -1.75) * mm, "end": v(-10.65, -1.22) * mm});
            skLineSegment(sketch, "E556", {"start": v(-10.65, -1.22) * mm, "end": v(-10.65, -0.68) * mm});
            skLineSegment(sketch, "E557", {"start": v(-10.65, -0.68) * mm, "end": v(-10.65, -0.15) * mm});
            skLineSegment(sketch, "E558", {"start": v(-10.65, -0.15) * mm, "end": v(-10.65, 0.39) * mm});
            skLineSegment(sketch, "E559", {"start": v(-10.65, 0.39) * mm, "end": v(-10.65, 0.92) * mm});
            skLineSegment(sketch, "E560", {"start": v(-10.65, 0.92) * mm, "end": v(-10.65, 1.45) * mm});
            skLineSegment(sketch, "E561", {"start": v(-10.65, 1.45) * mm, "end": v(-10.66, 1.53) * mm});
            skLineSegment(sketch, "E562", {"start": v(-10.66, 1.53) * mm, "end": v(-10.68, 1.6) * mm});
            skLineSegment(sketch, "E563", {"start": v(-10.68, 1.6) * mm, "end": v(-10.72, 1.68) * mm});
            skLineSegment(sketch, "E564", {"start": v(-10.72, 1.68) * mm, "end": v(-10.77, 1.74) * mm});
            skLineSegment(sketch, "E565", {"start": v(-10.77, 1.74) * mm, "end": v(-10.82, 1.79) * mm});
            skLineSegment(sketch, "E566", {"start": v(-10.82, 1.79) * mm, "end": v(-10.9, 1.82) * mm});
            skLineSegment(sketch, "E567", {"start": v(-10.9, 1.82) * mm, "end": v(-10.97, 1.85) * mm});
            skLineSegment(sketch, "E568", {"start": v(-10.97, 1.85) * mm, "end": v(-11.04, 1.86) * mm});
            skLineSegment(sketch, "E569", {"start": v(-11.04, 1.86) * mm, "end": v(-11.38, 1.86) * mm});
            skLineSegment(sketch, "E570", {"start": v(-11.38, 1.86) * mm, "end": v(-11.72, 1.86) * mm});
            skLineSegment(sketch, "E571", {"start": v(-11.72, 1.86) * mm, "end": v(-12.06, 1.86) * mm});
            skLineSegment(sketch, "E572", {"start": v(-12.06, 1.86) * mm, "end": v(-12.4, 1.86) * mm});
            skLineSegment(sketch, "E573", {"start": v(-12.4, 1.86) * mm, "end": v(-12.74, 1.86) * mm});
            skLineSegment(sketch, "E574", {"start": v(-12.74, 1.86) * mm, "end": v(-13.08, 1.86) * mm});
            skLineSegment(sketch, "E575", {"start": v(-13.08, 1.86) * mm, "end": v(-13.42, 1.86) * mm});
            skLineSegment(sketch, "E576", {"start": v(-13.42, 1.86) * mm, "end": v(-13.76, 1.86) * mm});
            skLineSegment(sketch, "E577", {"start": v(-13.76, 1.86) * mm, "end": v(-13.84, 1.85) * mm});
            skLineSegment(sketch, "E578", {"start": v(-13.84, 1.85) * mm, "end": v(-13.92, 1.82) * mm});
            skLineSegment(sketch, "E579", {"start": v(-13.92, 1.82) * mm, "end": v(-13.98, 1.79) * mm});
            skLineSegment(sketch, "E580", {"start": v(-13.98, 1.79) * mm, "end": v(-14.04, 1.74) * mm});
            skLineSegment(sketch, "E581", {"start": v(-14.04, 1.74) * mm, "end": v(-14.09, 1.68) * mm});
            skLineSegment(sketch, "E582", {"start": v(-14.09, 1.68) * mm, "end": v(-14.12, 1.6) * mm});
            skLineSegment(sketch, "E583", {"start": v(-14.12, 1.6) * mm, "end": v(-14.15, 1.53) * mm});
            skLineSegment(sketch, "E584", {"start": v(-14.15, 1.53) * mm, "end": v(-14.15, 1.45) * mm});
            skLineSegment(sketch, "E585", {"start": v(-14.15, 1.45) * mm, "end": v(-14.15, 0.92) * mm});
            skLineSegment(sketch, "E586", {"start": v(-14.15, 0.92) * mm, "end": v(-14.15, 0.39) * mm});
            skLineSegment(sketch, "E587", {"start": v(-14.15, 0.39) * mm, "end": v(-14.15, -0.15) * mm});
            skLineSegment(sketch, "E588", {"start": v(-14.15, -0.15) * mm, "end": v(-14.15, -0.68) * mm});
            skLineSegment(sketch, "E589", {"start": v(-14.15, -0.68) * mm, "end": v(-14.15, -1.22) * mm});
            skLineSegment(sketch, "E590", {"start": v(-14.15, -1.22) * mm, "end": v(-14.15, -1.75) * mm});
            skLineSegment(sketch, "E591", {"start": v(-14.15, -1.75) * mm, "end": v(-14.15, -2.28) * mm});
            skLineSegment(sketch, "E592", {"start": v(-14.15, -2.28) * mm, "end": v(-14.15, -2.82) * mm});
            skLineSegment(sketch, "E593", {"start": v(-14.15, -2.82) * mm, "end": v(-14.15, -2.9) * mm});
            skLineSegment(sketch, "E594", {"start": v(-14.15, -2.9) * mm, "end": v(-14.12, -2.97) * mm});
            skLineSegment(sketch, "E595", {"start": v(-14.12, -2.97) * mm, "end": v(-14.09, -3.04) * mm});
            skLineSegment(sketch, "E596", {"start": v(-14.09, -3.04) * mm, "end": v(-14.04, -3.1) * mm});
            skLineSegment(sketch, "E597", {"start": v(-14.04, -3.1) * mm, "end": v(-13.98, -3.14) * mm});
            skLineSegment(sketch, "E598", {"start": v(-13.98, -3.14) * mm, "end": v(-13.92, -3.18) * mm});
            skLineSegment(sketch, "E599", {"start": v(-13.92, -3.18) * mm, "end": v(-13.84, -3.2) * mm});
            skLineSegment(sketch, "E600", {"start": v(-13.84, -3.2) * mm, "end": v(-13.76, -3.2) * mm});
            skLineSegment(sketch, "E601", {"start": v(-13.76, -3.2) * mm, "end": v(-13.42, -3.2) * mm});
            skLineSegment(sketch, "E602", {"start": v(-13.42, -3.2) * mm, "end": v(-13.08, -3.2) * mm});
            skLineSegment(sketch, "E603", {"start": v(-13.08, -3.2) * mm, "end": v(-12.74, -3.2) * mm});
            skLineSegment(sketch, "E604", {"start": v(-12.74, -3.2) * mm, "end": v(-12.4, -3.2) * mm});
            skLineSegment(sketch, "E605", {"start": v(-12.4, -3.2) * mm, "end": v(-12.06, -3.2) * mm});
            skLineSegment(sketch, "E606", {"start": v(-12.06, -3.2) * mm, "end": v(-11.72, -3.2) * mm});
            skLineSegment(sketch, "E607", {"start": v(-11.72, -3.2) * mm, "end": v(-11.38, -3.2) * mm});
            skLineSegment(sketch, "E608", {"start": v(-11.38, -3.2) * mm, "end": v(-11.04, -3.2) * mm});
            skLineSegment(sketch, "E609", {"start": v(-1.38, -4.6) * mm, "end": v(-1.59, -4.6) * mm});
            skLineSegment(sketch, "E610", {"start": v(-1.59, -4.6) * mm, "end": v(-1.8, -4.6) * mm});
            skLineSegment(sketch, "E611", {"start": v(-1.8, -4.6) * mm, "end": v(-2, -4.6) * mm});
            skLineSegment(sketch, "E612", {"start": v(-2, -4.6) * mm, "end": v(-2.2, -4.6) * mm});
            skLineSegment(sketch, "E613", {"start": v(-2.2, -4.6) * mm, "end": v(-2.41, -4.6) * mm});
            skLineSegment(sketch, "E614", {"start": v(-2.41, -4.6) * mm, "end": v(-2.62, -4.6) * mm});
            skLineSegment(sketch, "E615", {"start": v(-2.62, -4.6) * mm, "end": v(-2.82, -4.6) * mm});
            skLineSegment(sketch, "E616", {"start": v(-2.82, -4.6) * mm, "end": v(-3.03, -4.6) * mm});
            skLineSegment(sketch, "E617", {"start": v(-3.03, -4.6) * mm, "end": v(-3.27, -4.2) * mm});
            skLineSegment(sketch, "E618", {"start": v(-3.27, -4.2) * mm, "end": v(-3.51, -3.8) * mm});
            skLineSegment(sketch, "E619", {"start": v(-3.51, -3.8) * mm, "end": v(-3.75, -3.4) * mm});
            skLineSegment(sketch, "E620", {"start": v(-3.75, -3.4) * mm, "end": v(-4, -3) * mm});
            skLineSegment(sketch, "E621", {"start": v(-4, -3) * mm, "end": v(-4.24, -2.6) * mm});
            skLineSegment(sketch, "E622", {"start": v(-4.24, -2.6) * mm, "end": v(-4.48, -2.2) * mm});
            skLineSegment(sketch, "E623", {"start": v(-4.48, -2.2) * mm, "end": v(-4.72, -1.8) * mm});
            skLineSegment(sketch, "E624", {"start": v(-4.72, -1.8) * mm, "end": v(-4.96, -1.4) * mm});
            skLineSegment(sketch, "E625", {"start": v(-4.96, -1.4) * mm, "end": v(-5.14, -1.4) * mm});
            skLineSegment(sketch, "E626", {"start": v(-5.14, -1.4) * mm, "end": v(-5.32, -1.4) * mm});
            skLineSegment(sketch, "E627", {"start": v(-5.32, -1.4) * mm, "end": v(-5.5, -1.4) * mm});
            skLineSegment(sketch, "E628", {"start": v(-5.5, -1.4) * mm, "end": v(-5.68, -1.4) * mm});
            skLineSegment(sketch, "E629", {"start": v(-5.68, -1.4) * mm, "end": v(-5.86, -1.4) * mm});
            skLineSegment(sketch, "E630", {"start": v(-5.86, -1.4) * mm, "end": v(-6.04, -1.4) * mm});
            skLineSegment(sketch, "E631", {"start": v(-6.04, -1.4) * mm, "end": v(-6.22, -1.4) * mm});
            skLineSegment(sketch, "E632", {"start": v(-6.22, -1.4) * mm, "end": v(-6.4, -1.4) * mm});
            skLineSegment(sketch, "E633", {"start": v(-6.4, -1.4) * mm, "end": v(-6.4, -1.8) * mm});
            skLineSegment(sketch, "E634", {"start": v(-6.4, -1.8) * mm, "end": v(-6.4, -2.2) * mm});
            skLineSegment(sketch, "E635", {"start": v(-6.4, -2.2) * mm, "end": v(-6.4, -2.6) * mm});
            skLineSegment(sketch, "E636", {"start": v(-6.4, -2.6) * mm, "end": v(-6.4, -3) * mm});
            skLineSegment(sketch, "E637", {"start": v(-6.4, -3) * mm, "end": v(-6.4, -3.4) * mm});
            skLineSegment(sketch, "E638", {"start": v(-6.4, -3.4) * mm, "end": v(-6.4, -3.8) * mm});
            skLineSegment(sketch, "E639", {"start": v(-6.4, -3.8) * mm, "end": v(-6.4, -4.2) * mm});
            skLineSegment(sketch, "E640", {"start": v(-6.4, -4.2) * mm, "end": v(-6.4, -4.6) * mm});
            skLineSegment(sketch, "E641", {"start": v(-6.4, -4.6) * mm, "end": v(-6.6, -4.6) * mm});
            skLineSegment(sketch, "E642", {"start": v(-6.6, -4.6) * mm, "end": v(-6.78, -4.6) * mm});
            skLineSegment(sketch, "E643", {"start": v(-6.78, -4.6) * mm, "end": v(-6.97, -4.6) * mm});
            skLineSegment(sketch, "E644", {"start": v(-6.97, -4.6) * mm, "end": v(-7.16, -4.6) * mm});
            skLineSegment(sketch, "E645", {"start": v(-7.16, -4.6) * mm, "end": v(-7.35, -4.6) * mm});
            skLineSegment(sketch, "E646", {"start": v(-7.35, -4.6) * mm, "end": v(-7.54, -4.6) * mm});
            skLineSegment(sketch, "E647", {"start": v(-7.54, -4.6) * mm, "end": v(-7.73, -4.6) * mm});
            skLineSegment(sketch, "E648", {"start": v(-7.73, -4.6) * mm, "end": v(-7.92, -4.6) * mm});
            skLineSegment(sketch, "E649", {"start": v(-7.92, -4.6) * mm, "end": v(-7.92, -3.62) * mm});
            skLineSegment(sketch, "E650", {"start": v(-7.92, -3.62) * mm, "end": v(-7.92, -2.64) * mm});
            skLineSegment(sketch, "E651", {"start": v(-7.92, -2.64) * mm, "end": v(-7.92, -1.66) * mm});
            skLineSegment(sketch, "E652", {"start": v(-7.92, -1.66) * mm, "end": v(-7.92, -0.68) * mm});
            skLineSegment(sketch, "E653", {"start": v(-7.92, -0.68) * mm, "end": v(-7.92, 0.3) * mm});
            skLineSegment(sketch, "E654", {"start": v(-7.92, 0.3) * mm, "end": v(-7.92, 1.29) * mm});
            skLineSegment(sketch, "E655", {"start": v(-7.92, 1.29) * mm, "end": v(-7.92, 2.27) * mm});
            skLineSegment(sketch, "E656", {"start": v(-7.92, 2.27) * mm, "end": v(-7.92, 3.25) * mm});
            skLineSegment(sketch, "E657", {"start": v(-7.92, 3.25) * mm, "end": v(-7.33, 3.25) * mm});
            skLineSegment(sketch, "E658", {"start": v(-7.33, 3.25) * mm, "end": v(-6.75, 3.25) * mm});
            skLineSegment(sketch, "E659", {"start": v(-6.75, 3.25) * mm, "end": v(-6.16, 3.25) * mm});
            skLineSegment(sketch, "E660", {"start": v(-6.16, 3.25) * mm, "end": v(-5.57, 3.25) * mm});
            skLineSegment(sketch, "E661", {"start": v(-5.57, 3.25) * mm, "end": v(-4.98, 3.25) * mm});
            skLineSegment(sketch, "E662", {"start": v(-4.98, 3.25) * mm, "end": v(-4.4, 3.25) * mm});
            skLineSegment(sketch, "E663", {"start": v(-4.4, 3.25) * mm, "end": v(-3.8, 3.25) * mm});
            skLineSegment(sketch, "E664", {"start": v(-3.8, 3.25) * mm, "end": v(-3.21, 3.25) * mm});
            skLineSegment(sketch, "E665", {"start": v(-3.21, 3.25) * mm, "end": v(-2.95, 3.22) * mm});
            skLineSegment(sketch, "E666", {"start": v(-2.95, 3.22) * mm, "end": v(-2.7, 3.15) * mm});
            skLineSegment(sketch, "E667", {"start": v(-2.7, 3.15) * mm, "end": v(-2.48, 3.03) * mm});
            skLineSegment(sketch, "E668", {"start": v(-2.48, 3.03) * mm, "end": v(-2.28, 2.87) * mm});
            skLineSegment(sketch, "E669", {"start": v(-2.28, 2.87) * mm, "end": v(-2.12, 2.67) * mm});
            skLineSegment(sketch, "E670", {"start": v(-2.12, 2.67) * mm, "end": v(-2, 2.45) * mm});
            skLineSegment(sketch, "E671", {"start": v(-2, 2.45) * mm, "end": v(-1.93, 2.2) * mm});
            skLineSegment(sketch, "E672", {"start": v(-1.93, 2.2) * mm, "end": v(-1.9, 1.94) * mm});
            skLineSegment(sketch, "E673", {"start": v(-1.9, 1.94) * mm, "end": v(-1.9, 1.68) * mm});
            skLineSegment(sketch, "E674", {"start": v(-1.9, 1.68) * mm, "end": v(-1.9, 1.43) * mm});
            skLineSegment(sketch, "E675", {"start": v(-1.9, 1.43) * mm, "end": v(-1.9, 1.18) * mm});
            skLineSegment(sketch, "E676", {"start": v(-1.9, 1.18) * mm, "end": v(-1.9, 0.92) * mm});
            skLineSegment(sketch, "E677", {"start": v(-1.9, 0.92) * mm, "end": v(-1.9, 0.67) * mm});
            skLineSegment(sketch, "E678", {"start": v(-1.9, 0.67) * mm, "end": v(-1.9, 0.42) * mm});
            skLineSegment(sketch, "E679", {"start": v(-1.9, 0.42) * mm, "end": v(-1.9, 0.16) * mm});
            skLineSegment(sketch, "E680", {"start": v(-1.9, 0.16) * mm, "end": v(-1.9, -0.09) * mm});
            skLineSegment(sketch, "E681", {"start": v(-1.9, -0.09) * mm, "end": v(-1.93, -0.35) * mm});
            skLineSegment(sketch, "E682", {"start": v(-1.93, -0.35) * mm, "end": v(-2, -0.6) * mm});
            skLineSegment(sketch, "E683", {"start": v(-2, -0.6) * mm, "end": v(-2.12, -0.82) * mm});
            skLineSegment(sketch, "E684", {"start": v(-2.12, -0.82) * mm, "end": v(-2.28, -1.02) * mm});
            skLineSegment(sketch, "E685", {"start": v(-2.28, -1.02) * mm, "end": v(-2.48, -1.18) * mm});
            skLineSegment(sketch, "E686", {"start": v(-2.48, -1.18) * mm, "end": v(-2.7, -1.3) * mm});
            skLineSegment(sketch, "E687", {"start": v(-2.7, -1.3) * mm, "end": v(-2.95, -1.38) * mm});
            skLineSegment(sketch, "E688", {"start": v(-2.95, -1.38) * mm, "end": v(-3.21, -1.4) * mm});
            skLineSegment(sketch, "E689", {"start": v(-3.21, -1.4) * mm, "end": v(-3.22, -1.4) * mm});
            skLineSegment(sketch, "E690", {"start": v(-3.22, -1.4) * mm, "end": v(-3.24, -1.4) * mm});
            skLineSegment(sketch, "E691", {"start": v(-3.24, -1.4) * mm, "end": v(-3.25, -1.4) * mm});
            skLineSegment(sketch, "E692", {"start": v(-3.25, -1.4) * mm, "end": v(-3.26, -1.4) * mm});
            skLineSegment(sketch, "E693", {"start": v(-3.26, -1.4) * mm, "end": v(-3.27, -1.4) * mm});
            skLineSegment(sketch, "E694", {"start": v(-3.27, -1.4) * mm, "end": v(-3.28, -1.4) * mm});
            skLineSegment(sketch, "E695", {"start": v(-3.28, -1.4) * mm, "end": v(-3.3, -1.4) * mm});
            skLineSegment(sketch, "E696", {"start": v(-3.3, -1.4) * mm, "end": v(-3.3, -1.4) * mm});
            skLineSegment(sketch, "E697", {"start": v(-3.3, -1.4) * mm, "end": v(-3.06, -1.8) * mm});
            skLineSegment(sketch, "E698", {"start": v(-3.06, -1.8) * mm, "end": v(-2.82, -2.2) * mm});
            skLineSegment(sketch, "E699", {"start": v(-2.82, -2.2) * mm, "end": v(-2.58, -2.6) * mm});
            skLineSegment(sketch, "E700", {"start": v(-2.58, -2.6) * mm, "end": v(-2.34, -3) * mm});
            skLineSegment(sketch, "E701", {"start": v(-2.34, -3) * mm, "end": v(-2.1, -3.4) * mm});
            skLineSegment(sketch, "E702", {"start": v(-2.1, -3.4) * mm, "end": v(-1.86, -3.8) * mm});
            skLineSegment(sketch, "E703", {"start": v(-1.86, -3.8) * mm, "end": v(-1.62, -4.2) * mm});
            skLineSegment(sketch, "E704", {"start": v(-1.62, -4.2) * mm, "end": v(-1.38, -4.6) * mm});
            skLineSegment(sketch, "E705", {"start": v(-6.4, 0) * mm, "end": v(-6.08, 0) * mm});
            skLineSegment(sketch, "E706", {"start": v(-6.08, 0) * mm, "end": v(-5.76, 0) * mm});
            skLineSegment(sketch, "E707", {"start": v(-5.76, 0) * mm, "end": v(-5.44, 0) * mm});
            skLineSegment(sketch, "E708", {"start": v(-5.44, 0) * mm, "end": v(-5.13, 0) * mm});
            skLineSegment(sketch, "E709", {"start": v(-5.13, 0) * mm, "end": v(-4.8, 0) * mm});
            skLineSegment(sketch, "E710", {"start": v(-4.8, 0) * mm, "end": v(-4.49, 0) * mm});
            skLineSegment(sketch, "E711", {"start": v(-4.49, 0) * mm, "end": v(-4.17, 0) * mm});
            skLineSegment(sketch, "E712", {"start": v(-4.17, 0) * mm, "end": v(-3.85, 0) * mm});
            skLineSegment(sketch, "E713", {"start": v(-3.85, 0) * mm, "end": v(-3.77, 0) * mm});
            skLineSegment(sketch, "E714", {"start": v(-3.77, 0) * mm, "end": v(-3.7, 0.02) * mm});
            skLineSegment(sketch, "E715", {"start": v(-3.7, 0.02) * mm, "end": v(-3.63, 0.06) * mm});
            skLineSegment(sketch, "E716", {"start": v(-3.63, 0.06) * mm, "end": v(-3.57, 0.1) * mm});
            skLineSegment(sketch, "E717", {"start": v(-3.57, 0.1) * mm, "end": v(-3.52, 0.16) * mm});
            skLineSegment(sketch, "E718", {"start": v(-3.52, 0.16) * mm, "end": v(-3.49, 0.23) * mm});
            skLineSegment(sketch, "E719", {"start": v(-3.49, 0.23) * mm, "end": v(-3.46, 0.3) * mm});
            skLineSegment(sketch, "E720", {"start": v(-3.46, 0.3) * mm, "end": v(-3.45, 0.38) * mm});
            skLineSegment(sketch, "E721", {"start": v(-3.45, 0.38) * mm, "end": v(-3.45, 0.52) * mm});
            skLineSegment(sketch, "E722", {"start": v(-3.45, 0.52) * mm, "end": v(-3.45, 0.65) * mm});
            skLineSegment(sketch, "E723", {"start": v(-3.45, 0.65) * mm, "end": v(-3.45, 0.78) * mm});
            skLineSegment(sketch, "E724", {"start": v(-3.45, 0.78) * mm, "end": v(-3.45, 0.92) * mm});
            skLineSegment(sketch, "E725", {"start": v(-3.45, 0.92) * mm, "end": v(-3.45, 1.05) * mm});
            skLineSegment(sketch, "E726", {"start": v(-3.45, 1.05) * mm, "end": v(-3.45, 1.19) * mm});
            skLineSegment(sketch, "E727", {"start": v(-3.45, 1.19) * mm, "end": v(-3.45, 1.32) * mm});
            skLineSegment(sketch, "E728", {"start": v(-3.45, 1.32) * mm, "end": v(-3.45, 1.45) * mm});
            skLineSegment(sketch, "E729", {"start": v(-3.45, 1.45) * mm, "end": v(-3.46, 1.53) * mm});
            skLineSegment(sketch, "E730", {"start": v(-3.46, 1.53) * mm, "end": v(-3.49, 1.6) * mm});
            skLineSegment(sketch, "E731", {"start": v(-3.49, 1.6) * mm, "end": v(-3.52, 1.68) * mm});
            skLineSegment(sketch, "E732", {"start": v(-3.52, 1.68) * mm, "end": v(-3.57, 1.74) * mm});
            skLineSegment(sketch, "E733", {"start": v(-3.57, 1.74) * mm, "end": v(-3.63, 1.79) * mm});
            skLineSegment(sketch, "E734", {"start": v(-3.63, 1.79) * mm, "end": v(-3.7, 1.82) * mm});
            skLineSegment(sketch, "E735", {"start": v(-3.7, 1.82) * mm, "end": v(-3.77, 1.85) * mm});
            skLineSegment(sketch, "E736", {"start": v(-3.77, 1.85) * mm, "end": v(-3.85, 1.86) * mm});
            skLineSegment(sketch, "E737", {"start": v(-3.85, 1.86) * mm, "end": v(-4.17, 1.86) * mm});
            skLineSegment(sketch, "E738", {"start": v(-4.17, 1.86) * mm, "end": v(-4.49, 1.86) * mm});
            skLineSegment(sketch, "E739", {"start": v(-4.49, 1.86) * mm, "end": v(-4.8, 1.86) * mm});
            skLineSegment(sketch, "E740", {"start": v(-4.8, 1.86) * mm, "end": v(-5.13, 1.86) * mm});
            skLineSegment(sketch, "E741", {"start": v(-5.13, 1.86) * mm, "end": v(-5.44, 1.86) * mm});
            skLineSegment(sketch, "E742", {"start": v(-5.44, 1.86) * mm, "end": v(-5.76, 1.86) * mm});
            skLineSegment(sketch, "E743", {"start": v(-5.76, 1.86) * mm, "end": v(-6.08, 1.86) * mm});
            skLineSegment(sketch, "E744", {"start": v(-6.08, 1.86) * mm, "end": v(-6.4, 1.86) * mm});
            skLineSegment(sketch, "E745", {"start": v(-6.4, 1.86) * mm, "end": v(-6.4, 1.62) * mm});
            skLineSegment(sketch, "E746", {"start": v(-6.4, 1.62) * mm, "end": v(-6.4, 1.4) * mm});
            skLineSegment(sketch, "E747", {"start": v(-6.4, 1.4) * mm, "end": v(-6.4, 1.16) * mm});
            skLineSegment(sketch, "E748", {"start": v(-6.4, 1.16) * mm, "end": v(-6.4, 0.92) * mm});
            skLineSegment(sketch, "E749", {"start": v(-6.4, 0.92) * mm, "end": v(-6.4, 0.7) * mm});
            skLineSegment(sketch, "E750", {"start": v(-6.4, 0.7) * mm, "end": v(-6.4, 0.46) * mm});
            skLineSegment(sketch, "E751", {"start": v(-6.4, 0.46) * mm, "end": v(-6.4, 0.22) * mm});
            skLineSegment(sketch, "E752", {"start": v(-6.4, 0.22) * mm, "end": v(-6.4, 0) * mm});
            skLineSegment(sketch, "E753", {"start": v(4.55, 1.86) * mm, "end": v(4.13, 1.86) * mm});
            skLineSegment(sketch, "E754", {"start": v(4.13, 1.86) * mm, "end": v(3.72, 1.86) * mm});
            skLineSegment(sketch, "E755", {"start": v(3.72, 1.86) * mm, "end": v(3.3, 1.86) * mm});
            skLineSegment(sketch, "E756", {"start": v(3.3, 1.86) * mm, "end": v(2.89, 1.86) * mm});
            skLineSegment(sketch, "E757", {"start": v(2.89, 1.86) * mm, "end": v(2.47, 1.86) * mm});
            skLineSegment(sketch, "E758", {"start": v(2.47, 1.86) * mm, "end": v(2.05, 1.86) * mm});
            skLineSegment(sketch, "E759", {"start": v(2.05, 1.86) * mm, "end": v(1.64, 1.86) * mm});
            skLineSegment(sketch, "E760", {"start": v(1.64, 1.86) * mm, "end": v(1.22, 1.86) * mm});
            skLineSegment(sketch, "E761", {"start": v(1.22, 1.86) * mm, "end": v(1.14, 1.85) * mm});
            skLineSegment(sketch, "E762", {"start": v(1.14, 1.85) * mm, "end": v(1.07, 1.83) * mm});
            skLineSegment(sketch, "E763", {"start": v(1.07, 1.83) * mm, "end": v(1, 1.79) * mm});
            skLineSegment(sketch, "E764", {"start": v(1, 1.79) * mm, "end": v(0.94, 1.74) * mm});
            skLineSegment(sketch, "E765", {"start": v(0.94, 1.74) * mm, "end": v(0.9, 1.68) * mm});
            skLineSegment(sketch, "E766", {"start": v(0.9, 1.68) * mm, "end": v(0.86, 1.61) * mm});
            skLineSegment(sketch, "E767", {"start": v(0.86, 1.61) * mm, "end": v(0.84, 1.54) * mm});
            skLineSegment(sketch, "E768", {"start": v(0.84, 1.54) * mm, "end": v(0.83, 1.47) * mm});
            skLineSegment(sketch, "E769", {"start": v(0.83, 1.47) * mm, "end": v(0.83, 0.93) * mm});
            skLineSegment(sketch, "E770", {"start": v(0.83, 0.93) * mm, "end": v(0.83, 0.4) * mm});
            skLineSegment(sketch, "E771", {"start": v(0.83, 0.4) * mm, "end": v(0.83, -0.14) * mm});
            skLineSegment(sketch, "E772", {"start": v(0.83, -0.14) * mm, "end": v(0.83, -0.68) * mm});
            skLineSegment(sketch, "E773", {"start": v(0.83, -0.68) * mm, "end": v(0.83, -1.21) * mm});
            skLineSegment(sketch, "E774", {"start": v(0.83, -1.21) * mm, "end": v(0.83, -1.75) * mm});
            skLineSegment(sketch, "E775", {"start": v(0.83, -1.75) * mm, "end": v(0.83, -2.28) * mm});
            skLineSegment(sketch, "E776", {"start": v(0.83, -2.28) * mm, "end": v(0.83, -2.82) * mm});
            skLineSegment(sketch, "E777", {"start": v(0.83, -2.82) * mm, "end": v(0.84, -2.9) * mm});
            skLineSegment(sketch, "E778", {"start": v(0.84, -2.9) * mm, "end": v(0.86, -2.97) * mm});
            skLineSegment(sketch, "E779", {"start": v(0.86, -2.97) * mm, "end": v(0.9, -3.04) * mm});
            skLineSegment(sketch, "E780", {"start": v(0.9, -3.04) * mm, "end": v(0.94, -3.1) * mm});
            skLineSegment(sketch, "E781", {"start": v(0.94, -3.1) * mm, "end": v(1, -3.14) * mm});
            skLineSegment(sketch, "E782", {"start": v(1, -3.14) * mm, "end": v(1.07, -3.18) * mm});
            skLineSegment(sketch, "E783", {"start": v(1.07, -3.18) * mm, "end": v(1.14, -3.2) * mm});
            skLineSegment(sketch, "E784", {"start": v(1.14, -3.2) * mm, "end": v(1.22, -3.2) * mm});
            skLineSegment(sketch, "E785", {"start": v(1.22, -3.2) * mm, "end": v(1.64, -3.2) * mm});
            skLineSegment(sketch, "E786", {"start": v(1.64, -3.2) * mm, "end": v(2.05, -3.2) * mm});
            skLineSegment(sketch, "E787", {"start": v(2.05, -3.2) * mm, "end": v(2.47, -3.2) * mm});
            skLineSegment(sketch, "E788", {"start": v(2.47, -3.2) * mm, "end": v(2.89, -3.2) * mm});
            skLineSegment(sketch, "E789", {"start": v(2.89, -3.2) * mm, "end": v(3.3, -3.2) * mm});
            skLineSegment(sketch, "E790", {"start": v(3.3, -3.2) * mm, "end": v(3.72, -3.2) * mm});
            skLineSegment(sketch, "E791", {"start": v(3.72, -3.2) * mm, "end": v(4.13, -3.2) * mm});
            skLineSegment(sketch, "E792", {"start": v(4.13, -3.2) * mm, "end": v(4.55, -3.2) * mm});
            skLineSegment(sketch, "E793", {"start": v(4.55, -3.2) * mm, "end": v(4.55, -3.38) * mm});
            skLineSegment(sketch, "E794", {"start": v(4.55, -3.38) * mm, "end": v(4.55, -3.56) * mm});
            skLineSegment(sketch, "E795", {"start": v(4.55, -3.56) * mm, "end": v(4.55, -3.73) * mm});
            skLineSegment(sketch, "E796", {"start": v(4.55, -3.73) * mm, "end": v(4.55, -3.9) * mm});
            skLineSegment(sketch, "E797", {"start": v(4.55, -3.9) * mm, "end": v(4.55, -4.08) * mm});
            skLineSegment(sketch, "E798", {"start": v(4.55, -4.08) * mm, "end": v(4.55, -4.26) * mm});
            skLineSegment(sketch, "E799", {"start": v(4.55, -4.26) * mm, "end": v(4.55, -4.43) * mm});
            skLineSegment(sketch, "E800", {"start": v(4.55, -4.43) * mm, "end": v(4.55, -4.6) * mm});
            skLineSegment(sketch, "E801", {"start": v(4.55, -4.6) * mm, "end": v(4.06, -4.6) * mm});
            skLineSegment(sketch, "E802", {"start": v(4.06, -4.6) * mm, "end": v(3.57, -4.6) * mm});
            skLineSegment(sketch, "E803", {"start": v(3.57, -4.6) * mm, "end": v(3.08, -4.6) * mm});
            skLineSegment(sketch, "E804", {"start": v(3.08, -4.6) * mm, "end": v(2.59, -4.6) * mm});
            skLineSegment(sketch, "E805", {"start": v(2.59, -4.6) * mm, "end": v(2.1, -4.6) * mm});
            skLineSegment(sketch, "E806", {"start": v(2.1, -4.6) * mm, "end": v(1.6, -4.6) * mm});
            skLineSegment(sketch, "E807", {"start": v(1.6, -4.6) * mm, "end": v(1.11, -4.6) * mm});
            skLineSegment(sketch, "E808", {"start": v(1.11, -4.6) * mm, "end": v(0.62, -4.6) * mm});
            skLineSegment(sketch, "E809", {"start": v(0.62, -4.6) * mm, "end": v(0.36, -4.58) * mm});
            skLineSegment(sketch, "E810", {"start": v(0.36, -4.58) * mm, "end": v(0.11, -4.5) * mm});
            skLineSegment(sketch, "E811", {"start": v(0.11, -4.5) * mm, "end": v(-0.11, -4.38) * mm});
            skLineSegment(sketch, "E812", {"start": v(-0.11, -4.38) * mm, "end": v(-0.3, -4.22) * mm});
            skLineSegment(sketch, "E813", {"start": v(-0.3, -4.22) * mm, "end": v(-0.47, -4.03) * mm});
            skLineSegment(sketch, "E814", {"start": v(-0.47, -4.03) * mm, "end": v(-0.59, -3.8) * mm});
            skLineSegment(sketch, "E815", {"start": v(-0.59, -3.8) * mm, "end": v(-0.66, -3.56) * mm});
            skLineSegment(sketch, "E816", {"start": v(-0.66, -3.56) * mm, "end": v(-0.7, -3.3) * mm});
            skLineSegment(sketch, "E817", {"start": v(-0.7, -3.3) * mm, "end": v(-0.7, -2.65) * mm});
            skLineSegment(sketch, "E818", {"start": v(-0.7, -2.65) * mm, "end": v(-0.7, -2) * mm});
            skLineSegment(sketch, "E819", {"start": v(-0.7, -2) * mm, "end": v(-0.7, -1.34) * mm});
            skLineSegment(sketch, "E820", {"start": v(-0.7, -1.34) * mm, "end": v(-0.7, -0.68) * mm});
            skLineSegment(sketch, "E821", {"start": v(-0.7, -0.68) * mm, "end": v(-0.7, -0.03) * mm});
            skLineSegment(sketch, "E822", {"start": v(-0.7, -0.03) * mm, "end": v(-0.7, 0.63) * mm});
            skLineSegment(sketch, "E823", {"start": v(-0.7, 0.63) * mm, "end": v(-0.7, 1.28) * mm});
            skLineSegment(sketch, "E824", {"start": v(-0.7, 1.28) * mm, "end": v(-0.7, 1.94) * mm});
            skLineSegment(sketch, "E825", {"start": v(-0.7, 1.94) * mm, "end": v(-0.66, 2.2) * mm});
            skLineSegment(sketch, "E826", {"start": v(-0.66, 2.2) * mm, "end": v(-0.59, 2.45) * mm});
            skLineSegment(sketch, "E827", {"start": v(-0.59, 2.45) * mm, "end": v(-0.47, 2.67) * mm});
            skLineSegment(sketch, "E828", {"start": v(-0.47, 2.67) * mm, "end": v(-0.3, 2.87) * mm});
            skLineSegment(sketch, "E829", {"start": v(-0.3, 2.87) * mm, "end": v(-0.11, 3.03) * mm});
            skLineSegment(sketch, "E830", {"start": v(-0.11, 3.03) * mm, "end": v(0.11, 3.15) * mm});
            skLineSegment(sketch, "E831", {"start": v(0.11, 3.15) * mm, "end": v(0.36, 3.22) * mm});
            skLineSegment(sketch, "E832", {"start": v(0.36, 3.22) * mm, "end": v(0.62, 3.25) * mm});
            skLineSegment(sketch, "E833", {"start": v(0.62, 3.25) * mm, "end": v(1.11, 3.25) * mm});
            skLineSegment(sketch, "E834", {"start": v(1.11, 3.25) * mm, "end": v(1.6, 3.25) * mm});
            skLineSegment(sketch, "E835", {"start": v(1.6, 3.25) * mm, "end": v(2.1, 3.25) * mm});
            skLineSegment(sketch, "E836", {"start": v(2.1, 3.25) * mm, "end": v(2.59, 3.25) * mm});
            skLineSegment(sketch, "E837", {"start": v(2.59, 3.25) * mm, "end": v(3.08, 3.25) * mm});
            skLineSegment(sketch, "E838", {"start": v(3.08, 3.25) * mm, "end": v(3.57, 3.25) * mm});
            skLineSegment(sketch, "E839", {"start": v(3.57, 3.25) * mm, "end": v(4.06, 3.25) * mm});
            skLineSegment(sketch, "E840", {"start": v(4.06, 3.25) * mm, "end": v(4.55, 3.25) * mm});
            skLineSegment(sketch, "E841", {"start": v(4.55, 3.25) * mm, "end": v(4.55, 3.08) * mm});
            skLineSegment(sketch, "E842", {"start": v(4.55, 3.08) * mm, "end": v(4.55, 2.9) * mm});
            skLineSegment(sketch, "E843", {"start": v(4.55, 2.9) * mm, "end": v(4.55, 2.73) * mm});
            skLineSegment(sketch, "E844", {"start": v(4.55, 2.73) * mm, "end": v(4.55, 2.55) * mm});
            skLineSegment(sketch, "E845", {"start": v(4.55, 2.55) * mm, "end": v(4.55, 2.38) * mm});
            skLineSegment(sketch, "E846", {"start": v(4.55, 2.38) * mm, "end": v(4.55, 2.2) * mm});
            skLineSegment(sketch, "E847", {"start": v(4.55, 2.2) * mm, "end": v(4.55, 2.03) * mm});
            skLineSegment(sketch, "E848", {"start": v(4.55, 2.03) * mm, "end": v(4.55, 1.86) * mm});
            skLineSegment(sketch, "E849", {"start": v(7.23, 1.86) * mm, "end": v(7.23, 1.63) * mm});
            skLineSegment(sketch, "E850", {"start": v(7.23, 1.63) * mm, "end": v(7.23, 1.4) * mm});
            skLineSegment(sketch, "E851", {"start": v(7.23, 1.4) * mm, "end": v(7.23, 1.17) * mm});
            skLineSegment(sketch, "E852", {"start": v(7.23, 1.17) * mm, "end": v(7.23, 0.94) * mm});
            skLineSegment(sketch, "E853", {"start": v(7.23, 0.94) * mm, "end": v(7.23, 0.7) * mm});
            skLineSegment(sketch, "E854", {"start": v(7.23, 0.7) * mm, "end": v(7.23, 0.48) * mm});
            skLineSegment(sketch, "E855", {"start": v(7.23, 0.48) * mm, "end": v(7.23, 0.25) * mm});
            skLineSegment(sketch, "E856", {"start": v(7.23, 0.25) * mm, "end": v(7.23, 0.01) * mm});
            skLineSegment(sketch, "E857", {"start": v(7.23, 0.01) * mm, "end": v(7.63, 0.01) * mm});
            skLineSegment(sketch, "E858", {"start": v(7.63, 0.01) * mm, "end": v(8.03, 0.01) * mm});
            skLineSegment(sketch, "E859", {"start": v(8.03, 0.01) * mm, "end": v(8.43, 0.01) * mm});
            skLineSegment(sketch, "E860", {"start": v(8.43, 0.01) * mm, "end": v(8.83, 0.01) * mm});
            skLineSegment(sketch, "E861", {"start": v(8.83, 0.01) * mm, "end": v(9.23, 0.01) * mm});
            skLineSegment(sketch, "E862", {"start": v(9.23, 0.01) * mm, "end": v(9.63, 0.01) * mm});
            skLineSegment(sketch, "E863", {"start": v(9.63, 0.01) * mm, "end": v(10.02, 0.01) * mm});
            skLineSegment(sketch, "E864", {"start": v(10.02, 0.01) * mm, "end": v(10.42, 0.01) * mm});
            skLineSegment(sketch, "E865", {"start": v(10.42, 0.01) * mm, "end": v(10.42, -0.16) * mm});
            skLineSegment(sketch, "E866", {"start": v(10.42, -0.16) * mm, "end": v(10.42, -0.33) * mm});
            skLineSegment(sketch, "E867", {"start": v(10.42, -0.33) * mm, "end": v(10.42, -0.5) * mm});
            skLineSegment(sketch, "E868", {"start": v(10.42, -0.5) * mm, "end": v(10.42, -0.68) * mm});
            skLineSegment(sketch, "E869", {"start": v(10.42, -0.68) * mm, "end": v(10.42, -0.86) * mm});
            skLineSegment(sketch, "E870", {"start": v(10.42, -0.86) * mm, "end": v(10.42, -1.03) * mm});
            skLineSegment(sketch, "E871", {"start": v(10.42, -1.03) * mm, "end": v(10.42, -1.2) * mm});
            skLineSegment(sketch, "E872", {"start": v(10.42, -1.2) * mm, "end": v(10.42, -1.38) * mm});
            skLineSegment(sketch, "E873", {"start": v(10.42, -1.38) * mm, "end": v(10.02, -1.38) * mm});
            skLineSegment(sketch, "E874", {"start": v(10.02, -1.38) * mm, "end": v(9.63, -1.38) * mm});
            skLineSegment(sketch, "E875", {"start": v(9.63, -1.38) * mm, "end": v(9.23, -1.38) * mm});
            skLineSegment(sketch, "E876", {"start": v(9.23, -1.38) * mm, "end": v(8.83, -1.38) * mm});
            skLineSegment(sketch, "E877", {"start": v(8.83, -1.38) * mm, "end": v(8.43, -1.38) * mm});
            skLineSegment(sketch, "E878", {"start": v(8.43, -1.38) * mm, "end": v(8.03, -1.38) * mm});
            skLineSegment(sketch, "E879", {"start": v(8.03, -1.38) * mm, "end": v(7.63, -1.38) * mm});
            skLineSegment(sketch, "E880", {"start": v(7.63, -1.38) * mm, "end": v(7.23, -1.38) * mm});
            skLineSegment(sketch, "E881", {"start": v(7.23, -1.38) * mm, "end": v(7.23, -1.6) * mm});
            skLineSegment(sketch, "E882", {"start": v(7.23, -1.6) * mm, "end": v(7.23, -1.84) * mm});
            skLineSegment(sketch, "E883", {"start": v(7.23, -1.84) * mm, "end": v(7.23, -2.07) * mm});
            skLineSegment(sketch, "E884", {"start": v(7.23, -2.07) * mm, "end": v(7.23, -2.3) * mm});
            skLineSegment(sketch, "E885", {"start": v(7.23, -2.3) * mm, "end": v(7.23, -2.52) * mm});
            skLineSegment(sketch, "E886", {"start": v(7.23, -2.52) * mm, "end": v(7.23, -2.75) * mm});
            skLineSegment(sketch, "E887", {"start": v(7.23, -2.75) * mm, "end": v(7.23, -2.98) * mm});
            skLineSegment(sketch, "E888", {"start": v(7.23, -2.98) * mm, "end": v(7.23, -3.2) * mm});
            skLineSegment(sketch, "E889", {"start": v(7.23, -3.2) * mm, "end": v(7.73, -3.2) * mm});
            skLineSegment(sketch, "E890", {"start": v(7.73, -3.2) * mm, "end": v(8.23, -3.2) * mm});
            skLineSegment(sketch, "E891", {"start": v(8.23, -3.2) * mm, "end": v(8.72, -3.2) * mm});
            skLineSegment(sketch, "E892", {"start": v(8.72, -3.2) * mm, "end": v(9.22, -3.2) * mm});
            skLineSegment(sketch, "E893", {"start": v(9.22, -3.2) * mm, "end": v(9.72, -3.2) * mm});
            skLineSegment(sketch, "E894", {"start": v(9.72, -3.2) * mm, "end": v(10.21, -3.2) * mm});
            skLineSegment(sketch, "E895", {"start": v(10.21, -3.2) * mm, "end": v(10.7, -3.2) * mm});
            skLineSegment(sketch, "E896", {"start": v(10.7, -3.2) * mm, "end": v(11.2, -3.2) * mm});
            skLineSegment(sketch, "E897", {"start": v(11.2, -3.2) * mm, "end": v(11.2, -3.38) * mm});
            skLineSegment(sketch, "E898", {"start": v(11.2, -3.38) * mm, "end": v(11.2, -3.56) * mm});
            skLineSegment(sketch, "E899", {"start": v(11.2, -3.56) * mm, "end": v(11.2, -3.73) * mm});
            skLineSegment(sketch, "E900", {"start": v(11.2, -3.73) * mm, "end": v(11.2, -3.9) * mm});
            skLineSegment(sketch, "E901", {"start": v(11.2, -3.9) * mm, "end": v(11.2, -4.08) * mm});
            skLineSegment(sketch, "E902", {"start": v(11.2, -4.08) * mm, "end": v(11.2, -4.26) * mm});
            skLineSegment(sketch, "E903", {"start": v(11.2, -4.26) * mm, "end": v(11.2, -4.43) * mm});
            skLineSegment(sketch, "E904", {"start": v(11.2, -4.43) * mm, "end": v(11.2, -4.6) * mm});
            skLineSegment(sketch, "E905", {"start": v(11.2, -4.6) * mm, "end": v(10.52, -4.6) * mm});
            skLineSegment(sketch, "E906", {"start": v(10.52, -4.6) * mm, "end": v(9.83, -4.6) * mm});
            skLineSegment(sketch, "E907", {"start": v(9.83, -4.6) * mm, "end": v(9.14, -4.6) * mm});
            skLineSegment(sketch, "E908", {"start": v(9.14, -4.6) * mm, "end": v(8.45, -4.6) * mm});
            skLineSegment(sketch, "E909", {"start": v(8.45, -4.6) * mm, "end": v(7.77, -4.6) * mm});
            skLineSegment(sketch, "E910", {"start": v(7.77, -4.6) * mm, "end": v(7.08, -4.6) * mm});
            skLineSegment(sketch, "E911", {"start": v(7.08, -4.6) * mm, "end": v(6.39, -4.6) * mm});
            skLineSegment(sketch, "E912", {"start": v(6.39, -4.6) * mm, "end": v(5.7, -4.6) * mm});
            skLineSegment(sketch, "E913", {"start": v(5.7, -4.6) * mm, "end": v(5.7, -3.62) * mm});
            skLineSegment(sketch, "E914", {"start": v(5.7, -3.62) * mm, "end": v(5.7, -2.64) * mm});
            skLineSegment(sketch, "E915", {"start": v(5.7, -2.64) * mm, "end": v(5.7, -1.66) * mm});
            skLineSegment(sketch, "E916", {"start": v(5.7, -1.66) * mm, "end": v(5.7, -0.68) * mm});
            skLineSegment(sketch, "E917", {"start": v(5.7, -0.68) * mm, "end": v(5.7, 0.3) * mm});
            skLineSegment(sketch, "E918", {"start": v(5.7, 0.3) * mm, "end": v(5.7, 1.29) * mm});
            skLineSegment(sketch, "E919", {"start": v(5.7, 1.29) * mm, "end": v(5.7, 2.27) * mm});
            skLineSegment(sketch, "E920", {"start": v(5.7, 2.27) * mm, "end": v(5.7, 3.25) * mm});
            skLineSegment(sketch, "E921", {"start": v(5.7, 3.25) * mm, "end": v(6.39, 3.25) * mm});
            skLineSegment(sketch, "E922", {"start": v(6.39, 3.25) * mm, "end": v(7.08, 3.25) * mm});
            skLineSegment(sketch, "E923", {"start": v(7.08, 3.25) * mm, "end": v(7.77, 3.25) * mm});
            skLineSegment(sketch, "E924", {"start": v(7.77, 3.25) * mm, "end": v(8.45, 3.25) * mm});
            skLineSegment(sketch, "E925", {"start": v(8.45, 3.25) * mm, "end": v(9.14, 3.25) * mm});
            skLineSegment(sketch, "E926", {"start": v(9.14, 3.25) * mm, "end": v(9.83, 3.25) * mm});
            skLineSegment(sketch, "E927", {"start": v(9.83, 3.25) * mm, "end": v(10.52, 3.25) * mm});
            skLineSegment(sketch, "E928", {"start": v(10.52, 3.25) * mm, "end": v(11.2, 3.25) * mm});
            skLineSegment(sketch, "E929", {"start": v(11.2, 3.25) * mm, "end": v(11.2, 3.08) * mm});
            skLineSegment(sketch, "E930", {"start": v(11.2, 3.08) * mm, "end": v(11.2, 2.9) * mm});
            skLineSegment(sketch, "E931", {"start": v(11.2, 2.9) * mm, "end": v(11.2, 2.73) * mm});
            skLineSegment(sketch, "E932", {"start": v(11.2, 2.73) * mm, "end": v(11.2, 2.55) * mm});
            skLineSegment(sketch, "E933", {"start": v(11.2, 2.55) * mm, "end": v(11.2, 2.38) * mm});
            skLineSegment(sketch, "E934", {"start": v(11.2, 2.38) * mm, "end": v(11.2, 2.2) * mm});
            skLineSegment(sketch, "E935", {"start": v(11.2, 2.2) * mm, "end": v(11.2, 2.03) * mm});
            skLineSegment(sketch, "E936", {"start": v(11.2, 2.03) * mm, "end": v(11.2, 1.86) * mm});
            skLineSegment(sketch, "E937", {"start": v(11.2, 1.86) * mm, "end": v(10.7, 1.86) * mm});
            skLineSegment(sketch, "E938", {"start": v(10.7, 1.86) * mm, "end": v(10.21, 1.86) * mm});
            skLineSegment(sketch, "E939", {"start": v(10.21, 1.86) * mm, "end": v(9.72, 1.86) * mm});
            skLineSegment(sketch, "E940", {"start": v(9.72, 1.86) * mm, "end": v(9.22, 1.86) * mm});
            skLineSegment(sketch, "E941", {"start": v(9.22, 1.86) * mm, "end": v(8.72, 1.86) * mm});
            skLineSegment(sketch, "E942", {"start": v(8.72, 1.86) * mm, "end": v(8.23, 1.86) * mm});
            skLineSegment(sketch, "E943", {"start": v(8.23, 1.86) * mm, "end": v(7.73, 1.86) * mm});
            skLineSegment(sketch, "E944", {"start": v(7.73, 1.86) * mm, "end": v(7.23, 1.86) * mm});
            skLineSegment(sketch, "E945", {"start": v(12.34, 3.25) * mm, "end": v(12.48, 3.24) * mm});
            skLineSegment(sketch, "E946", {"start": v(12.48, 3.24) * mm, "end": v(12.61, 3.2) * mm});
            skLineSegment(sketch, "E947", {"start": v(12.61, 3.2) * mm, "end": v(12.73, 3.13) * mm});
            skLineSegment(sketch, "E948", {"start": v(12.73, 3.13) * mm, "end": v(12.83, 3.05) * mm});
            skLineSegment(sketch, "E949", {"start": v(12.83, 3.05) * mm, "end": v(12.91, 2.95) * mm});
            skLineSegment(sketch, "E950", {"start": v(12.91, 2.95) * mm, "end": v(12.98, 2.83) * mm});
            skLineSegment(sketch, "E951", {"start": v(12.98, 2.83) * mm, "end": v(13.02, 2.7) * mm});
            skLineSegment(sketch, "E952", {"start": v(13.02, 2.7) * mm, "end": v(13.03, 2.56) * mm});
            skLineSegment(sketch, "E953", {"start": v(13.03, 2.56) * mm, "end": v(13.02, 2.42) * mm});
            skLineSegment(sketch, "E954", {"start": v(13.02, 2.42) * mm, "end": v(12.98, 2.3) * mm});
            skLineSegment(sketch, "E955", {"start": v(12.98, 2.3) * mm, "end": v(12.91, 2.18) * mm});
            skLineSegment(sketch, "E956", {"start": v(12.91, 2.18) * mm, "end": v(12.83, 2.08) * mm});
            skLineSegment(sketch, "E957", {"start": v(12.83, 2.08) * mm, "end": v(12.73, 2) * mm});
            skLineSegment(sketch, "E958", {"start": v(12.73, 2) * mm, "end": v(12.61, 1.93) * mm});
            skLineSegment(sketch, "E959", {"start": v(12.61, 1.93) * mm, "end": v(12.48, 1.89) * mm});
            skLineSegment(sketch, "E960", {"start": v(12.48, 1.89) * mm, "end": v(12.34, 1.87) * mm});
            skLineSegment(sketch, "E961", {"start": v(12.34, 1.87) * mm, "end": v(12.2, 1.89) * mm});
            skLineSegment(sketch, "E962", {"start": v(12.2, 1.89) * mm, "end": v(12.08, 1.93) * mm});
            skLineSegment(sketch, "E963", {"start": v(12.08, 1.93) * mm, "end": v(11.96, 2) * mm});
            skLineSegment(sketch, "E964", {"start": v(11.96, 2) * mm, "end": v(11.86, 2.08) * mm});
            skLineSegment(sketch, "E965", {"start": v(11.86, 2.08) * mm, "end": v(11.77, 2.18) * mm});
            skLineSegment(sketch, "E966", {"start": v(11.77, 2.18) * mm, "end": v(11.71, 2.3) * mm});
            skLineSegment(sketch, "E967", {"start": v(11.71, 2.3) * mm, "end": v(11.67, 2.42) * mm});
            skLineSegment(sketch, "E968", {"start": v(11.67, 2.42) * mm, "end": v(11.66, 2.56) * mm});
            skLineSegment(sketch, "E969", {"start": v(11.66, 2.56) * mm, "end": v(11.67, 2.7) * mm});
            skLineSegment(sketch, "E970", {"start": v(11.67, 2.7) * mm, "end": v(11.71, 2.83) * mm});
            skLineSegment(sketch, "E971", {"start": v(11.71, 2.83) * mm, "end": v(11.77, 2.95) * mm});
            skLineSegment(sketch, "E972", {"start": v(11.77, 2.95) * mm, "end": v(11.86, 3.05) * mm});
            skLineSegment(sketch, "E973", {"start": v(11.86, 3.05) * mm, "end": v(11.96, 3.13) * mm});
            skLineSegment(sketch, "E974", {"start": v(11.96, 3.13) * mm, "end": v(12.08, 3.2) * mm});
            skLineSegment(sketch, "E975", {"start": v(12.08, 3.2) * mm, "end": v(12.2, 3.24) * mm});
            skLineSegment(sketch, "E976", {"start": v(12.2, 3.24) * mm, "end": v(12.34, 3.25) * mm});
            skLineSegment(sketch, "E977", {"start": v(15.62, 1.94) * mm, "end": v(15.65, 2.2) * mm});
            skLineSegment(sketch, "E978", {"start": v(15.65, 2.2) * mm, "end": v(15.73, 2.45) * mm});
            skLineSegment(sketch, "E979", {"start": v(15.73, 2.45) * mm, "end": v(15.85, 2.67) * mm});
            skLineSegment(sketch, "E980", {"start": v(15.85, 2.67) * mm, "end": v(16, 2.87) * mm});
            skLineSegment(sketch, "E981", {"start": v(16, 2.87) * mm, "end": v(16.2, 3.03) * mm});
            skLineSegment(sketch, "E982", {"start": v(16.2, 3.03) * mm, "end": v(16.43, 3.15) * mm});
            skLineSegment(sketch, "E983", {"start": v(16.43, 3.15) * mm, "end": v(16.67, 3.22) * mm});
            skLineSegment(sketch, "E984", {"start": v(16.67, 3.22) * mm, "end": v(16.94, 3.25) * mm});
            skLineSegment(sketch, "E985", {"start": v(16.94, 3.25) * mm, "end": v(17.56, 3.25) * mm});
            skLineSegment(sketch, "E986", {"start": v(17.56, 3.25) * mm, "end": v(18.18, 3.25) * mm});
            skLineSegment(sketch, "E987", {"start": v(18.18, 3.25) * mm, "end": v(18.8, 3.25) * mm});
            skLineSegment(sketch, "E988", {"start": v(18.8, 3.25) * mm, "end": v(19.43, 3.25) * mm});
            skLineSegment(sketch, "E989", {"start": v(19.43, 3.25) * mm, "end": v(20.05, 3.25) * mm});
            skLineSegment(sketch, "E990", {"start": v(20.05, 3.25) * mm, "end": v(20.67, 3.25) * mm});
            skLineSegment(sketch, "E991", {"start": v(20.67, 3.25) * mm, "end": v(21.3, 3.25) * mm});
            skLineSegment(sketch, "E992", {"start": v(21.3, 3.25) * mm, "end": v(21.91, 3.25) * mm});
            skLineSegment(sketch, "E993", {"start": v(21.91, 3.25) * mm, "end": v(21.91, 3.07) * mm});
            skLineSegment(sketch, "E994", {"start": v(21.91, 3.07) * mm, "end": v(21.91, 2.9) * mm});
            skLineSegment(sketch, "E995", {"start": v(21.91, 2.9) * mm, "end": v(21.91, 2.72) * mm});
            skLineSegment(sketch, "E996", {"start": v(21.91, 2.72) * mm, "end": v(21.91, 2.54) * mm});
            skLineSegment(sketch, "E997", {"start": v(21.91, 2.54) * mm, "end": v(21.91, 2.37) * mm});
            skLineSegment(sketch, "E998", {"start": v(21.91, 2.37) * mm, "end": v(21.91, 2.19) * mm});
            skLineSegment(sketch, "E999", {"start": v(21.91, 2.19) * mm, "end": v(21.91, 2.01) * mm});
            skLineSegment(sketch, "E1000", {"start": v(21.91, 2.01) * mm, "end": v(21.91, 1.83) * mm});
            skLineSegment(sketch, "E1001", {"start": v(21.91, 1.83) * mm, "end": v(21.37, 1.83) * mm});
            skLineSegment(sketch, "E1002", {"start": v(21.37, 1.83) * mm, "end": v(20.83, 1.83) * mm});
            skLineSegment(sketch, "E1003", {"start": v(20.83, 1.83) * mm, "end": v(20.28, 1.83) * mm});
            skLineSegment(sketch, "E1004", {"start": v(20.28, 1.83) * mm, "end": v(19.74, 1.83) * mm});
            skLineSegment(sketch, "E1005", {"start": v(19.74, 1.83) * mm, "end": v(19.2, 1.83) * mm});
            skLineSegment(sketch, "E1006", {"start": v(19.2, 1.83) * mm, "end": v(18.66, 1.83) * mm});
            skLineSegment(sketch, "E1007", {"start": v(18.66, 1.83) * mm, "end": v(18.11, 1.83) * mm});
            skLineSegment(sketch, "E1008", {"start": v(18.11, 1.83) * mm, "end": v(17.57, 1.83) * mm});
            skLineSegment(sketch, "E1009", {"start": v(17.57, 1.83) * mm, "end": v(17.5, 1.83) * mm});
            skLineSegment(sketch, "E1010", {"start": v(17.5, 1.83) * mm, "end": v(17.42, 1.8) * mm});
            skLineSegment(sketch, "E1011", {"start": v(17.42, 1.8) * mm, "end": v(17.35, 1.77) * mm});
            skLineSegment(sketch, "E1012", {"start": v(17.35, 1.77) * mm, "end": v(17.29, 1.72) * mm});
            skLineSegment(sketch, "E1013", {"start": v(17.29, 1.72) * mm, "end": v(17.24, 1.66) * mm});
            skLineSegment(sketch, "E1014", {"start": v(17.24, 1.66) * mm, "end": v(17.2, 1.6) * mm});
            skLineSegment(sketch, "E1015", {"start": v(17.2, 1.6) * mm, "end": v(17.18, 1.52) * mm});
            skLineSegment(sketch, "E1016", {"start": v(17.18, 1.52) * mm, "end": v(17.17, 1.44) * mm});
            skLineSegment(sketch, "E1017", {"start": v(17.17, 1.44) * mm, "end": v(17.17, 0.98) * mm});
            skLineSegment(sketch, "E1018", {"start": v(17.17, 0.98) * mm, "end": v(17.17, 0.52) * mm});
            skLineSegment(sketch, "E1019", {"start": v(17.17, 0.52) * mm, "end": v(17.17, 0.06) * mm});
            skLineSegment(sketch, "E1020", {"start": v(17.17, 0.06) * mm, "end": v(17.17, -0.4) * mm});
            skLineSegment(sketch, "E1021", {"start": v(17.17, -0.4) * mm, "end": v(17.17, -0.86) * mm});
            skLineSegment(sketch, "E1022", {"start": v(17.17, -0.86) * mm, "end": v(17.17, -1.32) * mm});
            skLineSegment(sketch, "E1023", {"start": v(17.17, -1.32) * mm, "end": v(17.17, -1.78) * mm});
            skLineSegment(sketch, "E1024", {"start": v(17.17, -1.78) * mm, "end": v(17.17, -2.24) * mm});
            skLineSegment(sketch, "E1025", {"start": v(17.17, -2.24) * mm, "end": v(17.17, -2.28) * mm});
            skLineSegment(sketch, "E1026", {"start": v(17.17, -2.28) * mm, "end": v(17.18, -2.32) * mm});
            skLineSegment(sketch, "E1027", {"start": v(17.18, -2.32) * mm, "end": v(17.19, -2.36) * mm});
            skLineSegment(sketch, "E1028", {"start": v(17.19, -2.36) * mm, "end": v(17.2, -2.4) * mm});
            skLineSegment(sketch, "E1029", {"start": v(17.2, -2.4) * mm, "end": v(17.22, -2.43) * mm});
            skLineSegment(sketch, "E1030", {"start": v(17.22, -2.43) * mm, "end": v(17.24, -2.46) * mm});
            skLineSegment(sketch, "E1031", {"start": v(17.24, -2.46) * mm, "end": v(17.26, -2.5) * mm});
            skLineSegment(sketch, "E1032", {"start": v(17.26, -2.5) * mm, "end": v(17.28, -2.52) * mm});
            skLineSegment(sketch, "E1033", {"start": v(17.28, -2.52) * mm, "end": v(17.35, -2.59) * mm});
            skLineSegment(sketch, "E1034", {"start": v(17.35, -2.59) * mm, "end": v(17.42, -2.66) * mm});
            skLineSegment(sketch, "E1035", {"start": v(17.42, -2.66) * mm, "end": v(17.5, -2.73) * mm});
            skLineSegment(sketch, "E1036", {"start": v(17.5, -2.73) * mm, "end": v(17.56, -2.8) * mm});
            skLineSegment(sketch, "E1037", {"start": v(17.56, -2.8) * mm, "end": v(17.63, -2.86) * mm});
            skLineSegment(sketch, "E1038", {"start": v(17.63, -2.86) * mm, "end": v(17.7, -2.93) * mm});
            skLineSegment(sketch, "E1039", {"start": v(17.7, -2.93) * mm, "end": v(17.77, -3) * mm});
            skLineSegment(sketch, "E1040", {"start": v(17.77, -3) * mm, "end": v(17.84, -3.07) * mm});
            skLineSegment(sketch, "E1041", {"start": v(17.84, -3.07) * mm, "end": v(17.87, -3.1) * mm});
            skLineSegment(sketch, "E1042", {"start": v(17.87, -3.1) * mm, "end": v(17.9, -3.12) * mm});
            skLineSegment(sketch, "E1043", {"start": v(17.9, -3.12) * mm, "end": v(17.93, -3.14) * mm});
            skLineSegment(sketch, "E1044", {"start": v(17.93, -3.14) * mm, "end": v(17.97, -3.16) * mm});
            skLineSegment(sketch, "E1045", {"start": v(17.97, -3.16) * mm, "end": v(18, -3.17) * mm});
            skLineSegment(sketch, "E1046", {"start": v(18, -3.17) * mm, "end": v(18.04, -3.18) * mm});
            skLineSegment(sketch, "E1047", {"start": v(18.04, -3.18) * mm, "end": v(18.08, -3.19) * mm});
            skLineSegment(sketch, "E1048", {"start": v(18.08, -3.19) * mm, "end": v(18.12, -3.19) * mm});
            skLineSegment(sketch, "E1049", {"start": v(18.12, -3.19) * mm, "end": v(18.39, -3.19) * mm});
            skLineSegment(sketch, "E1050", {"start": v(18.39, -3.19) * mm, "end": v(18.65, -3.19) * mm});
            skLineSegment(sketch, "E1051", {"start": v(18.65, -3.19) * mm, "end": v(18.91, -3.19) * mm});
            skLineSegment(sketch, "E1052", {"start": v(18.91, -3.19) * mm, "end": v(19.18, -3.19) * mm});
            skLineSegment(sketch, "E1053", {"start": v(19.18, -3.19) * mm, "end": v(19.44, -3.19) * mm});
            skLineSegment(sketch, "E1054", {"start": v(19.44, -3.19) * mm, "end": v(19.7, -3.19) * mm});
            skLineSegment(sketch, "E1055", {"start": v(19.7, -3.19) * mm, "end": v(19.97, -3.19) * mm});
            skLineSegment(sketch, "E1056", {"start": v(19.97, -3.19) * mm, "end": v(20.23, -3.19) * mm});
            skLineSegment(sketch, "E1057", {"start": v(20.23, -3.19) * mm, "end": v(20.31, -3.18) * mm});
            skLineSegment(sketch, "E1058", {"start": v(20.31, -3.18) * mm, "end": v(20.38, -3.16) * mm});
            skLineSegment(sketch, "E1059", {"start": v(20.38, -3.16) * mm, "end": v(20.45, -3.12) * mm});
            skLineSegment(sketch, "E1060", {"start": v(20.45, -3.12) * mm, "end": v(20.5, -3.07) * mm});
            skLineSegment(sketch, "E1061", {"start": v(20.5, -3.07) * mm, "end": v(20.56, -3.02) * mm});
            skLineSegment(sketch, "E1062", {"start": v(20.56, -3.02) * mm, "end": v(20.6, -2.95) * mm});
            skLineSegment(sketch, "E1063", {"start": v(20.6, -2.95) * mm, "end": v(20.62, -2.87) * mm});
            skLineSegment(sketch, "E1064", {"start": v(20.62, -2.87) * mm, "end": v(20.62, -2.8) * mm});
            skLineSegment(sketch, "E1065", {"start": v(20.62, -2.8) * mm, "end": v(20.62, -2.62) * mm});
            skLineSegment(sketch, "E1066", {"start": v(20.62, -2.62) * mm, "end": v(20.62, -2.44) * mm});
            skLineSegment(sketch, "E1067", {"start": v(20.62, -2.44) * mm, "end": v(20.62, -2.26) * mm});
            skLineSegment(sketch, "E1068", {"start": v(20.62, -2.26) * mm, "end": v(20.62, -2.09) * mm});
            skLineSegment(sketch, "E1069", {"start": v(20.62, -2.09) * mm, "end": v(20.62, -1.9) * mm});
            skLineSegment(sketch, "E1070", {"start": v(20.62, -1.9) * mm, "end": v(20.62, -1.73) * mm});
            skLineSegment(sketch, "E1071", {"start": v(20.62, -1.73) * mm, "end": v(20.62, -1.56) * mm});
            skLineSegment(sketch, "E1072", {"start": v(20.62, -1.56) * mm, "end": v(20.62, -1.38) * mm});
            skLineSegment(sketch, "E1073", {"start": v(20.62, -1.38) * mm, "end": v(20.4, -1.38) * mm});
            skLineSegment(sketch, "E1074", {"start": v(20.4, -1.38) * mm, "end": v(20.16, -1.38) * mm});
            skLineSegment(sketch, "E1075", {"start": v(20.16, -1.38) * mm, "end": v(19.93, -1.38) * mm});
            skLineSegment(sketch, "E1076", {"start": v(19.93, -1.38) * mm, "end": v(19.7, -1.38) * mm});
            skLineSegment(sketch, "E1077", {"start": v(19.7, -1.38) * mm, "end": v(19.46, -1.38) * mm});
            skLineSegment(sketch, "E1078", {"start": v(19.46, -1.38) * mm, "end": v(19.23, -1.38) * mm});
            skLineSegment(sketch, "E1079", {"start": v(19.23, -1.38) * mm, "end": v(19, -1.38) * mm});
            skLineSegment(sketch, "E1080", {"start": v(19, -1.38) * mm, "end": v(18.77, -1.38) * mm});
            skLineSegment(sketch, "E1081", {"start": v(18.77, -1.38) * mm, "end": v(18.77, -1.2) * mm});
            skLineSegment(sketch, "E1082", {"start": v(18.77, -1.2) * mm, "end": v(18.77, -1.02) * mm});
            skLineSegment(sketch, "E1083", {"start": v(18.77, -1.02) * mm, "end": v(18.77, -0.85) * mm});
            skLineSegment(sketch, "E1084", {"start": v(18.77, -0.85) * mm, "end": v(18.77, -0.67) * mm});
            skLineSegment(sketch, "E1085", {"start": v(18.77, -0.67) * mm, "end": v(18.77, -0.5) * mm});
            skLineSegment(sketch, "E1086", {"start": v(18.77, -0.5) * mm, "end": v(18.77, -0.32) * mm});
            skLineSegment(sketch, "E1087", {"start": v(18.77, -0.32) * mm, "end": v(18.77, -0.14) * mm});
            skLineSegment(sketch, "E1088", {"start": v(18.77, -0.14) * mm, "end": v(18.77, 0.04) * mm});
            skLineSegment(sketch, "E1089", {"start": v(18.77, 0.04) * mm, "end": v(19.2, 0.04) * mm});
            skLineSegment(sketch, "E1090", {"start": v(19.2, 0.04) * mm, "end": v(19.62, 0.04) * mm});
            skLineSegment(sketch, "E1091", {"start": v(19.62, 0.04) * mm, "end": v(20.05, 0.04) * mm});
            skLineSegment(sketch, "E1092", {"start": v(20.05, 0.04) * mm, "end": v(20.47, 0.04) * mm});
            skLineSegment(sketch, "E1093", {"start": v(20.47, 0.04) * mm, "end": v(20.9, 0.04) * mm});
            skLineSegment(sketch, "E1094", {"start": v(20.9, 0.04) * mm, "end": v(21.33, 0.04) * mm});
            skLineSegment(sketch, "E1095", {"start": v(21.33, 0.04) * mm, "end": v(21.75, 0.04) * mm});
            skLineSegment(sketch, "E1096", {"start": v(21.75, 0.04) * mm, "end": v(22.18, 0.04) * mm});
            skLineSegment(sketch, "E1097", {"start": v(22.18, 0.04) * mm, "end": v(22.18, -0.38) * mm});
            skLineSegment(sketch, "E1098", {"start": v(22.18, -0.38) * mm, "end": v(22.18, -0.8) * mm});
            skLineSegment(sketch, "E1099", {"start": v(22.18, -0.8) * mm, "end": v(22.18, -1.21) * mm});
            skLineSegment(sketch, "E1100", {"start": v(22.18, -1.21) * mm, "end": v(22.18, -1.63) * mm});
            skLineSegment(sketch, "E1101", {"start": v(22.18, -1.63) * mm, "end": v(22.18, -2.05) * mm});
            skLineSegment(sketch, "E1102", {"start": v(22.18, -2.05) * mm, "end": v(22.18, -2.47) * mm});
            skLineSegment(sketch, "E1103", {"start": v(22.18, -2.47) * mm, "end": v(22.18, -2.88) * mm});
            skLineSegment(sketch, "E1104", {"start": v(22.18, -2.88) * mm, "end": v(22.18, -3.3) * mm});
            skLineSegment(sketch, "E1105", {"start": v(22.18, -3.3) * mm, "end": v(22.15, -3.56) * mm});
            skLineSegment(sketch, "E1106", {"start": v(22.15, -3.56) * mm, "end": v(22.07, -3.8) * mm});
            skLineSegment(sketch, "E1107", {"start": v(22.07, -3.8) * mm, "end": v(21.95, -4.03) * mm});
            skLineSegment(sketch, "E1108", {"start": v(21.95, -4.03) * mm, "end": v(21.8, -4.22) * mm});
            skLineSegment(sketch, "E1109", {"start": v(21.8, -4.22) * mm, "end": v(21.6, -4.38) * mm});
            skLineSegment(sketch, "E1110", {"start": v(21.6, -4.38) * mm, "end": v(21.38, -4.5) * mm});
            skLineSegment(sketch, "E1111", {"start": v(21.38, -4.5) * mm, "end": v(21.13, -4.58) * mm});
            skLineSegment(sketch, "E1112", {"start": v(21.13, -4.58) * mm, "end": v(20.87, -4.6) * mm});
            skLineSegment(sketch, "E1113", {"start": v(20.87, -4.6) * mm, "end": v(20.43, -4.6) * mm});
            skLineSegment(sketch, "E1114", {"start": v(20.43, -4.6) * mm, "end": v(19.99, -4.6) * mm});
            skLineSegment(sketch, "E1115", {"start": v(19.99, -4.6) * mm, "end": v(19.55, -4.6) * mm});
            skLineSegment(sketch, "E1116", {"start": v(19.55, -4.6) * mm, "end": v(19.11, -4.6) * mm});
            skLineSegment(sketch, "E1117", {"start": v(19.11, -4.6) * mm, "end": v(18.68, -4.6) * mm});
            skLineSegment(sketch, "E1118", {"start": v(18.68, -4.6) * mm, "end": v(18.24, -4.6) * mm});
            skLineSegment(sketch, "E1119", {"start": v(18.24, -4.6) * mm, "end": v(17.8, -4.6) * mm});
            skLineSegment(sketch, "E1120", {"start": v(17.8, -4.6) * mm, "end": v(17.36, -4.6) * mm});
            skLineSegment(sketch, "E1121", {"start": v(17.36, -4.6) * mm, "end": v(17.33, -4.6) * mm});
            skLineSegment(sketch, "E1122", {"start": v(17.33, -4.6) * mm, "end": v(17.29, -4.6) * mm});
            skLineSegment(sketch, "E1123", {"start": v(17.29, -4.6) * mm, "end": v(17.25, -4.59) * mm});
            skLineSegment(sketch, "E1124", {"start": v(17.25, -4.59) * mm, "end": v(17.21, -4.58) * mm});
            skLineSegment(sketch, "E1125", {"start": v(17.21, -4.58) * mm, "end": v(17.18, -4.56) * mm});
            skLineSegment(sketch, "E1126", {"start": v(17.18, -4.56) * mm, "end": v(17.14, -4.54) * mm});
            skLineSegment(sketch, "E1127", {"start": v(17.14, -4.54) * mm, "end": v(17.1, -4.52) * mm});
            skLineSegment(sketch, "E1128", {"start": v(17.1, -4.52) * mm, "end": v(17.08, -4.49) * mm});
            skLineSegment(sketch, "E1129", {"start": v(17.08, -4.49) * mm, "end": v(16.9, -4.32) * mm});
            skLineSegment(sketch, "E1130", {"start": v(16.9, -4.32) * mm, "end": v(16.74, -4.15) * mm});
            skLineSegment(sketch, "E1131", {"start": v(16.74, -4.15) * mm, "end": v(16.57, -3.99) * mm});
            skLineSegment(sketch, "E1132", {"start": v(16.57, -3.99) * mm, "end": v(16.4, -3.82) * mm});
            skLineSegment(sketch, "E1133", {"start": v(16.4, -3.82) * mm, "end": v(16.24, -3.65) * mm});
            skLineSegment(sketch, "E1134", {"start": v(16.24, -3.65) * mm, "end": v(16.07, -3.49) * mm});
            skLineSegment(sketch, "E1135", {"start": v(16.07, -3.49) * mm, "end": v(15.9, -3.32) * mm});
            skLineSegment(sketch, "E1136", {"start": v(15.9, -3.32) * mm, "end": v(15.74, -3.15) * mm});
            skLineSegment(sketch, "E1137", {"start": v(15.74, -3.15) * mm, "end": v(15.71, -3.13) * mm});
            skLineSegment(sketch, "E1138", {"start": v(15.71, -3.13) * mm, "end": v(15.7, -3.1) * mm});
            skLineSegment(sketch, "E1139", {"start": v(15.7, -3.1) * mm, "end": v(15.67, -3.06) * mm});
            skLineSegment(sketch, "E1140", {"start": v(15.67, -3.06) * mm, "end": v(15.66, -3.03) * mm});
            skLineSegment(sketch, "E1141", {"start": v(15.66, -3.03) * mm, "end": v(15.64, -3) * mm});
            skLineSegment(sketch, "E1142", {"start": v(15.64, -3) * mm, "end": v(15.63, -2.95) * mm});
            skLineSegment(sketch, "E1143", {"start": v(15.63, -2.95) * mm, "end": v(15.63, -2.92) * mm});
            skLineSegment(sketch, "E1144", {"start": v(15.63, -2.92) * mm, "end": v(15.62, -2.88) * mm});
            skLineSegment(sketch, "E1145", {"start": v(15.62, -2.88) * mm, "end": v(15.62, -2.27) * mm});
            skLineSegment(sketch, "E1146", {"start": v(15.62, -2.27) * mm, "end": v(15.62, -1.67) * mm});
            skLineSegment(sketch, "E1147", {"start": v(15.62, -1.67) * mm, "end": v(15.62, -1.07) * mm});
            skLineSegment(sketch, "E1148", {"start": v(15.62, -1.07) * mm, "end": v(15.62, -0.47) * mm});
            skLineSegment(sketch, "E1149", {"start": v(15.62, -0.47) * mm, "end": v(15.62, 0.13) * mm});
            skLineSegment(sketch, "E1150", {"start": v(15.62, 0.13) * mm, "end": v(15.62, 0.73) * mm});
            skLineSegment(sketch, "E1151", {"start": v(15.62, 0.73) * mm, "end": v(15.62, 1.34) * mm});
            skLineSegment(sketch, "E1152", {"start": v(15.62, 1.34) * mm, "end": v(15.62, 1.94) * mm});
            skLineSegment(sketch, "E1153", {"start": v(29.12, 3.25) * mm, "end": v(29.12, 3.08) * mm});
            skLineSegment(sketch, "E1154", {"start": v(29.12, 3.08) * mm, "end": v(29.12, 2.9) * mm});
            skLineSegment(sketch, "E1155", {"start": v(29.12, 2.9) * mm, "end": v(29.12, 2.74) * mm});
            skLineSegment(sketch, "E1156", {"start": v(29.12, 2.74) * mm, "end": v(29.12, 2.57) * mm});
            skLineSegment(sketch, "E1157", {"start": v(29.12, 2.57) * mm, "end": v(29.12, 2.4) * mm});
            skLineSegment(sketch, "E1158", {"start": v(29.12, 2.4) * mm, "end": v(29.12, 2.22) * mm});
            skLineSegment(sketch, "E1159", {"start": v(29.12, 2.22) * mm, "end": v(29.12, 2.05) * mm});
            skLineSegment(sketch, "E1160", {"start": v(29.12, 2.05) * mm, "end": v(29.12, 1.88) * mm});
            skLineSegment(sketch, "E1161", {"start": v(29.12, 1.88) * mm, "end": v(28.84, 1.88) * mm});
            skLineSegment(sketch, "E1162", {"start": v(28.84, 1.88) * mm, "end": v(28.56, 1.88) * mm});
            skLineSegment(sketch, "E1163", {"start": v(28.56, 1.88) * mm, "end": v(28.28, 1.88) * mm});
            skLineSegment(sketch, "E1164", {"start": v(28.28, 1.88) * mm, "end": v(28, 1.88) * mm});
            skLineSegment(sketch, "E1165", {"start": v(28, 1.88) * mm, "end": v(27.72, 1.88) * mm});
            skLineSegment(sketch, "E1166", {"start": v(27.72, 1.88) * mm, "end": v(27.44, 1.88) * mm});
            skLineSegment(sketch, "E1167", {"start": v(27.44, 1.88) * mm, "end": v(27.16, 1.88) * mm});
            skLineSegment(sketch, "E1168", {"start": v(27.16, 1.88) * mm, "end": v(26.88, 1.88) * mm});
            skLineSegment(sketch, "E1169", {"start": v(26.88, 1.88) * mm, "end": v(26.88, 1.07) * mm});
            skLineSegment(sketch, "E1170", {"start": v(26.88, 1.07) * mm, "end": v(26.88, 0.26) * mm});
            skLineSegment(sketch, "E1171", {"start": v(26.88, 0.26) * mm, "end": v(26.88, -0.55) * mm});
            skLineSegment(sketch, "E1172", {"start": v(26.88, -0.55) * mm, "end": v(26.88, -1.36) * mm});
            skLineSegment(sketch, "E1173", {"start": v(26.88, -1.36) * mm, "end": v(26.88, -2.17) * mm});
            skLineSegment(sketch, "E1174", {"start": v(26.88, -2.17) * mm, "end": v(26.88, -2.98) * mm});
            skLineSegment(sketch, "E1175", {"start": v(26.88, -2.98) * mm, "end": v(26.88, -3.8) * mm});
            skLineSegment(sketch, "E1176", {"start": v(26.88, -3.8) * mm, "end": v(26.88, -4.6) * mm});
            skLineSegment(sketch, "E1177", {"start": v(26.88, -4.6) * mm, "end": v(26.69, -4.6) * mm});
            skLineSegment(sketch, "E1178", {"start": v(26.69, -4.6) * mm, "end": v(26.5, -4.6) * mm});
            skLineSegment(sketch, "E1179", {"start": v(26.5, -4.6) * mm, "end": v(26.3, -4.6) * mm});
            skLineSegment(sketch, "E1180", {"start": v(26.3, -4.6) * mm, "end": v(26.11, -4.6) * mm});
            skLineSegment(sketch, "E1181", {"start": v(26.11, -4.6) * mm, "end": v(25.92, -4.6) * mm});
            skLineSegment(sketch, "E1182", {"start": v(25.92, -4.6) * mm, "end": v(25.73, -4.6) * mm});
            skLineSegment(sketch, "E1183", {"start": v(25.73, -4.6) * mm, "end": v(25.54, -4.6) * mm});
            skLineSegment(sketch, "E1184", {"start": v(25.54, -4.6) * mm, "end": v(25.35, -4.6) * mm});
            skLineSegment(sketch, "E1185", {"start": v(25.35, -4.6) * mm, "end": v(25.35, -3.8) * mm});
            skLineSegment(sketch, "E1186", {"start": v(25.35, -3.8) * mm, "end": v(25.35, -2.98) * mm});
            skLineSegment(sketch, "E1187", {"start": v(25.35, -2.98) * mm, "end": v(25.35, -2.17) * mm});
            skLineSegment(sketch, "E1188", {"start": v(25.35, -2.17) * mm, "end": v(25.35, -1.36) * mm});
            skLineSegment(sketch, "E1189", {"start": v(25.35, -1.36) * mm, "end": v(25.35, -0.55) * mm});
            skLineSegment(sketch, "E1190", {"start": v(25.35, -0.55) * mm, "end": v(25.35, 0.26) * mm});
            skLineSegment(sketch, "E1191", {"start": v(25.35, 0.26) * mm, "end": v(25.35, 1.07) * mm});
            skLineSegment(sketch, "E1192", {"start": v(25.35, 1.07) * mm, "end": v(25.35, 1.88) * mm});
            skLineSegment(sketch, "E1193", {"start": v(25.35, 1.88) * mm, "end": v(25.06, 1.88) * mm});
            skLineSegment(sketch, "E1194", {"start": v(25.06, 1.88) * mm, "end": v(24.78, 1.88) * mm});
            skLineSegment(sketch, "E1195", {"start": v(24.78, 1.88) * mm, "end": v(24.5, 1.88) * mm});
            skLineSegment(sketch, "E1196", {"start": v(24.5, 1.88) * mm, "end": v(24.22, 1.88) * mm});
            skLineSegment(sketch, "E1197", {"start": v(24.22, 1.88) * mm, "end": v(23.94, 1.88) * mm});
            skLineSegment(sketch, "E1198", {"start": v(23.94, 1.88) * mm, "end": v(23.66, 1.88) * mm});
            skLineSegment(sketch, "E1199", {"start": v(23.66, 1.88) * mm, "end": v(23.38, 1.88) * mm});
            skLineSegment(sketch, "E1200", {"start": v(23.38, 1.88) * mm, "end": v(23.1, 1.88) * mm});
            skLineSegment(sketch, "E1201", {"start": v(23.1, 1.88) * mm, "end": v(23.1, 2.05) * mm});
            skLineSegment(sketch, "E1202", {"start": v(23.1, 2.05) * mm, "end": v(23.1, 2.22) * mm});
            skLineSegment(sketch, "E1203", {"start": v(23.1, 2.22) * mm, "end": v(23.1, 2.4) * mm});
            skLineSegment(sketch, "E1204", {"start": v(23.1, 2.4) * mm, "end": v(23.1, 2.57) * mm});
            skLineSegment(sketch, "E1205", {"start": v(23.1, 2.57) * mm, "end": v(23.1, 2.74) * mm});
            skLineSegment(sketch, "E1206", {"start": v(23.1, 2.74) * mm, "end": v(23.1, 2.9) * mm});
            skLineSegment(sketch, "E1207", {"start": v(23.1, 2.9) * mm, "end": v(23.1, 3.08) * mm});
            skLineSegment(sketch, "E1208", {"start": v(23.1, 3.08) * mm, "end": v(23.1, 3.25) * mm});
            skLineSegment(sketch, "E1209", {"start": v(23.1, 3.25) * mm, "end": v(23.85, 3.25) * mm});
            skLineSegment(sketch, "E1210", {"start": v(23.85, 3.25) * mm, "end": v(24.6, 3.25) * mm});
            skLineSegment(sketch, "E1211", {"start": v(24.6, 3.25) * mm, "end": v(25.36, 3.25) * mm});
            skLineSegment(sketch, "E1212", {"start": v(25.36, 3.25) * mm, "end": v(26.11, 3.25) * mm});
            skLineSegment(sketch, "E1213", {"start": v(26.11, 3.25) * mm, "end": v(26.86, 3.25) * mm});
            skLineSegment(sketch, "E1214", {"start": v(26.86, 3.25) * mm, "end": v(27.62, 3.25) * mm});
            skLineSegment(sketch, "E1215", {"start": v(27.62, 3.25) * mm, "end": v(28.37, 3.25) * mm});
            skLineSegment(sketch, "E1216", {"start": v(28.37, 3.25) * mm, "end": v(29.12, 3.25) * mm});
            skLineSegment(sketch, "E1217", {"start": v(34.48, 3.26) * mm, "end": v(34.69, 3.26) * mm});
            skLineSegment(sketch, "E1218", {"start": v(34.69, 3.26) * mm, "end": v(34.9, 3.26) * mm});
            skLineSegment(sketch, "E1219", {"start": v(34.9, 3.26) * mm, "end": v(35.11, 3.26) * mm});
            skLineSegment(sketch, "E1220", {"start": v(35.11, 3.26) * mm, "end": v(35.32, 3.26) * mm});
            skLineSegment(sketch, "E1221", {"start": v(35.32, 3.26) * mm, "end": v(35.54, 3.26) * mm});
            skLineSegment(sketch, "E1222", {"start": v(35.54, 3.26) * mm, "end": v(35.75, 3.26) * mm});
            skLineSegment(sketch, "E1223", {"start": v(35.75, 3.26) * mm, "end": v(35.96, 3.26) * mm});
            skLineSegment(sketch, "E1224", {"start": v(35.96, 3.26) * mm, "end": v(36.17, 3.26) * mm});
            skLineSegment(sketch, "E1225", {"start": v(36.17, 3.26) * mm, "end": v(35.86, 2.8) * mm});
            skLineSegment(sketch, "E1226", {"start": v(35.86, 2.8) * mm, "end": v(35.55, 2.33) * mm});
            skLineSegment(sketch, "E1227", {"start": v(35.55, 2.33) * mm, "end": v(35.24, 1.86) * mm});
            skLineSegment(sketch, "E1228", {"start": v(35.24, 1.86) * mm, "end": v(34.93, 1.4) * mm});
            skLineSegment(sketch, "E1229", {"start": v(34.93, 1.4) * mm, "end": v(34.62, 0.93) * mm});
            skLineSegment(sketch, "E1230", {"start": v(34.62, 0.93) * mm, "end": v(34.31, 0.46) * mm});
            skLineSegment(sketch, "E1231", {"start": v(34.31, 0.46) * mm, "end": v(34, 0) * mm});
            skLineSegment(sketch, "E1232", {"start": v(34, 0) * mm, "end": v(33.7, -0.47) * mm});
            skLineSegment(sketch, "E1233", {"start": v(33.7, -0.47) * mm, "end": v(34.02, -0.99) * mm});
            skLineSegment(sketch, "E1234", {"start": v(34.02, -0.99) * mm, "end": v(34.35, -1.5) * mm});
            skLineSegment(sketch, "E1235", {"start": v(34.35, -1.5) * mm, "end": v(34.68, -2.02) * mm});
            skLineSegment(sketch, "E1236", {"start": v(34.68, -2.02) * mm, "end": v(35, -2.54) * mm});
            skLineSegment(sketch, "E1237", {"start": v(35, -2.54) * mm, "end": v(35.33, -3.05) * mm});
            skLineSegment(sketch, "E1238", {"start": v(35.33, -3.05) * mm, "end": v(35.66, -3.57) * mm});
            skLineSegment(sketch, "E1239", {"start": v(35.66, -3.57) * mm, "end": v(35.98, -4.09) * mm});
            skLineSegment(sketch, "E1240", {"start": v(35.98, -4.09) * mm, "end": v(36.3, -4.6) * mm});
            skLineSegment(sketch, "E1241", {"start": v(36.3, -4.6) * mm, "end": v(36.08, -4.6) * mm});
            skLineSegment(sketch, "E1242", {"start": v(36.08, -4.6) * mm, "end": v(35.85, -4.6) * mm});
            skLineSegment(sketch, "E1243", {"start": v(35.85, -4.6) * mm, "end": v(35.62, -4.6) * mm});
            skLineSegment(sketch, "E1244", {"start": v(35.62, -4.6) * mm, "end": v(35.39, -4.6) * mm});
            skLineSegment(sketch, "E1245", {"start": v(35.39, -4.6) * mm, "end": v(35.16, -4.6) * mm});
            skLineSegment(sketch, "E1246", {"start": v(35.16, -4.6) * mm, "end": v(34.93, -4.6) * mm});
            skLineSegment(sketch, "E1247", {"start": v(34.93, -4.6) * mm, "end": v(34.7, -4.6) * mm});
            skLineSegment(sketch, "E1248", {"start": v(34.7, -4.6) * mm, "end": v(34.47, -4.6) * mm});
            skLineSegment(sketch, "E1249", {"start": v(34.47, -4.6) * mm, "end": v(34.25, -4.27) * mm});
            skLineSegment(sketch, "E1250", {"start": v(34.25, -4.27) * mm, "end": v(34.04, -3.93) * mm});
            skLineSegment(sketch, "E1251", {"start": v(34.04, -3.93) * mm, "end": v(33.83, -3.6) * mm});
            skLineSegment(sketch, "E1252", {"start": v(33.83, -3.6) * mm, "end": v(33.61, -3.26) * mm});
            skLineSegment(sketch, "E1253", {"start": v(33.61, -3.26) * mm, "end": v(33.4, -2.93) * mm});
            skLineSegment(sketch, "E1254", {"start": v(33.4, -2.93) * mm, "end": v(33.19, -2.6) * mm});
            skLineSegment(sketch, "E1255", {"start": v(33.19, -2.6) * mm, "end": v(32.97, -2.26) * mm});
            skLineSegment(sketch, "E1256", {"start": v(32.97, -2.26) * mm, "end": v(32.76, -1.92) * mm});
            skLineSegment(sketch, "E1257", {"start": v(32.76, -1.92) * mm, "end": v(32.55, -2.26) * mm});
            skLineSegment(sketch, "E1258", {"start": v(32.55, -2.26) * mm, "end": v(32.33, -2.6) * mm});
            skLineSegment(sketch, "E1259", {"start": v(32.33, -2.6) * mm, "end": v(32.11, -2.93) * mm});
            skLineSegment(sketch, "E1260", {"start": v(32.11, -2.93) * mm, "end": v(31.9, -3.26) * mm});
            skLineSegment(sketch, "E1261", {"start": v(31.9, -3.26) * mm, "end": v(31.68, -3.6) * mm});
            skLineSegment(sketch, "E1262", {"start": v(31.68, -3.6) * mm, "end": v(31.47, -3.93) * mm});
            skLineSegment(sketch, "E1263", {"start": v(31.47, -3.93) * mm, "end": v(31.25, -4.27) * mm});
            skLineSegment(sketch, "E1264", {"start": v(31.25, -4.27) * mm, "end": v(31.03, -4.6) * mm});
            skLineSegment(sketch, "E1265", {"start": v(31.03, -4.6) * mm, "end": v(30.82, -4.6) * mm});
            skLineSegment(sketch, "E1266", {"start": v(30.82, -4.6) * mm, "end": v(30.61, -4.6) * mm});
            skLineSegment(sketch, "E1267", {"start": v(30.61, -4.6) * mm, "end": v(30.4, -4.6) * mm});
            skLineSegment(sketch, "E1268", {"start": v(30.4, -4.6) * mm, "end": v(30.2, -4.6) * mm});
            skLineSegment(sketch, "E1269", {"start": v(30.2, -4.6) * mm, "end": v(29.98, -4.6) * mm});
            skLineSegment(sketch, "E1270", {"start": v(29.98, -4.6) * mm, "end": v(29.77, -4.6) * mm});
            skLineSegment(sketch, "E1271", {"start": v(29.77, -4.6) * mm, "end": v(29.56, -4.6) * mm});
            skLineSegment(sketch, "E1272", {"start": v(29.56, -4.6) * mm, "end": v(29.35, -4.6) * mm});
            skLineSegment(sketch, "E1273", {"start": v(29.35, -4.6) * mm, "end": v(29.68, -4.1) * mm});
            skLineSegment(sketch, "E1274", {"start": v(29.68, -4.1) * mm, "end": v(30, -3.61) * mm});
            skLineSegment(sketch, "E1275", {"start": v(30, -3.61) * mm, "end": v(30.33, -3.12) * mm});
            skLineSegment(sketch, "E1276", {"start": v(30.33, -3.12) * mm, "end": v(30.65, -2.62) * mm});
            skLineSegment(sketch, "E1277", {"start": v(30.65, -2.62) * mm, "end": v(30.98, -2.13) * mm});
            skLineSegment(sketch, "E1278", {"start": v(30.98, -2.13) * mm, "end": v(31.3, -1.63) * mm});
            skLineSegment(sketch, "E1279", {"start": v(31.3, -1.63) * mm, "end": v(31.63, -1.14) * mm});
            skLineSegment(sketch, "E1280", {"start": v(31.63, -1.14) * mm, "end": v(31.96, -0.64) * mm});
            skLineSegment(sketch, "E1281", {"start": v(31.96, -0.64) * mm, "end": v(31.65, -0.15) * mm});
            skLineSegment(sketch, "E1282", {"start": v(31.65, -0.15) * mm, "end": v(31.34, 0.33) * mm});
            skLineSegment(sketch, "E1283", {"start": v(31.34, 0.33) * mm, "end": v(31.04, 0.82) * mm});
            skLineSegment(sketch, "E1284", {"start": v(31.04, 0.82) * mm, "end": v(30.73, 1.31) * mm});
            skLineSegment(sketch, "E1285", {"start": v(30.73, 1.31) * mm, "end": v(30.42, 1.8) * mm});
            skLineSegment(sketch, "E1286", {"start": v(30.42, 1.8) * mm, "end": v(30.12, 2.29) * mm});
            skLineSegment(sketch, "E1287", {"start": v(30.12, 2.29) * mm, "end": v(29.8, 2.77) * mm});
            skLineSegment(sketch, "E1288", {"start": v(29.8, 2.77) * mm, "end": v(29.5, 3.26) * mm});
            skLineSegment(sketch, "E1289", {"start": v(29.5, 3.26) * mm, "end": v(29.73, 3.26) * mm});
            skLineSegment(sketch, "E1290", {"start": v(29.73, 3.26) * mm, "end": v(29.96, 3.26) * mm});
            skLineSegment(sketch, "E1291", {"start": v(29.96, 3.26) * mm, "end": v(30.2, 3.26) * mm});
            skLineSegment(sketch, "E1292", {"start": v(30.2, 3.26) * mm, "end": v(30.42, 3.26) * mm});
            skLineSegment(sketch, "E1293", {"start": v(30.42, 3.26) * mm, "end": v(30.65, 3.26) * mm});
            skLineSegment(sketch, "E1294", {"start": v(30.65, 3.26) * mm, "end": v(30.88, 3.26) * mm});
            skLineSegment(sketch, "E1295", {"start": v(30.88, 3.26) * mm, "end": v(31.12, 3.26) * mm});
            skLineSegment(sketch, "E1296", {"start": v(31.12, 3.26) * mm, "end": v(31.35, 3.26) * mm});
            skLineSegment(sketch, "E1297", {"start": v(31.35, 3.26) * mm, "end": v(31.54, 2.95) * mm});
            skLineSegment(sketch, "E1298", {"start": v(31.54, 2.95) * mm, "end": v(31.73, 2.64) * mm});
            skLineSegment(sketch, "E1299", {"start": v(31.73, 2.64) * mm, "end": v(31.93, 2.33) * mm});
            skLineSegment(sketch, "E1300", {"start": v(31.93, 2.33) * mm, "end": v(32.12, 2.02) * mm});
            skLineSegment(sketch, "E1301", {"start": v(32.12, 2.02) * mm, "end": v(32.32, 1.71) * mm});
            skLineSegment(sketch, "E1302", {"start": v(32.32, 1.71) * mm, "end": v(32.51, 1.4) * mm});
            skLineSegment(sketch, "E1303", {"start": v(32.51, 1.4) * mm, "end": v(32.7, 1.1) * mm});
            skLineSegment(sketch, "E1304", {"start": v(32.7, 1.1) * mm, "end": v(32.9, 0.79) * mm});
            skLineSegment(sketch, "E1305", {"start": v(32.9, 0.79) * mm, "end": v(33.1, 1.1) * mm});
            skLineSegment(sketch, "E1306", {"start": v(33.1, 1.1) * mm, "end": v(33.3, 1.4) * mm});
            skLineSegment(sketch, "E1307", {"start": v(33.3, 1.4) * mm, "end": v(33.5, 1.71) * mm});
            skLineSegment(sketch, "E1308", {"start": v(33.5, 1.71) * mm, "end": v(33.69, 2.02) * mm});
            skLineSegment(sketch, "E1309", {"start": v(33.69, 2.02) * mm, "end": v(33.89, 2.33) * mm});
            skLineSegment(sketch, "E1310", {"start": v(33.89, 2.33) * mm, "end": v(34.08, 2.64) * mm});
            skLineSegment(sketch, "E1311", {"start": v(34.08, 2.64) * mm, "end": v(34.28, 2.95) * mm});
            skLineSegment(sketch, "E1312", {"start": v(34.28, 2.95) * mm, "end": v(34.48, 3.26) * mm});
            skLineSegment(sketch, "E1313", {"start": v(-30.2, -8.46) * mm, "end": v(-30.68, -8.46) * mm});
            skLineSegment(sketch, "E1314", {"start": v(-30.68, -8.46) * mm, "end": v(-31.16, -8.46) * mm});
            skLineSegment(sketch, "E1315", {"start": v(-31.16, -8.46) * mm, "end": v(-31.65, -8.46) * mm});
            skLineSegment(sketch, "E1316", {"start": v(-31.65, -8.46) * mm, "end": v(-32.13, -8.46) * mm});
            skLineSegment(sketch, "E1317", {"start": v(-32.13, -8.46) * mm, "end": v(-32.61, -8.46) * mm});
            skLineSegment(sketch, "E1318", {"start": v(-32.61, -8.46) * mm, "end": v(-33.1, -8.46) * mm});
            skLineSegment(sketch, "E1319", {"start": v(-33.1, -8.46) * mm, "end": v(-33.58, -8.46) * mm});
            skLineSegment(sketch, "E1320", {"start": v(-33.58, -8.46) * mm, "end": v(-34.07, -8.46) * mm});
            skLineSegment(sketch, "E1321", {"start": v(-34.07, -8.46) * mm, "end": v(-34.16, -8.47) * mm});
            skLineSegment(sketch, "E1322", {"start": v(-34.16, -8.47) * mm, "end": v(-34.24, -8.5) * mm});
            skLineSegment(sketch, "E1323", {"start": v(-34.24, -8.5) * mm, "end": v(-34.32, -8.54) * mm});
            skLineSegment(sketch, "E1324", {"start": v(-34.32, -8.54) * mm, "end": v(-34.39, -8.6) * mm});
            skLineSegment(sketch, "E1325", {"start": v(-34.39, -8.6) * mm, "end": v(-34.44, -8.67) * mm});
            skLineSegment(sketch, "E1326", {"start": v(-34.44, -8.67) * mm, "end": v(-34.49, -8.74) * mm});
            skLineSegment(sketch, "E1327", {"start": v(-34.49, -8.74) * mm, "end": v(-34.51, -8.83) * mm});
            skLineSegment(sketch, "E1328", {"start": v(-34.51, -8.83) * mm, "end": v(-34.52, -8.92) * mm});
            skLineSegment(sketch, "E1329", {"start": v(-34.52, -8.92) * mm, "end": v(-34.52, -9.54) * mm});
            skLineSegment(sketch, "E1330", {"start": v(-34.52, -9.54) * mm, "end": v(-34.52, -10.16) * mm});
            skLineSegment(sketch, "E1331", {"start": v(-34.52, -10.16) * mm, "end": v(-34.52, -10.79) * mm});
            skLineSegment(sketch, "E1332", {"start": v(-34.52, -10.79) * mm, "end": v(-34.52, -11.4) * mm});
            skLineSegment(sketch, "E1333", {"start": v(-34.52, -11.4) * mm, "end": v(-34.52, -12.03) * mm});
            skLineSegment(sketch, "E1334", {"start": v(-34.52, -12.03) * mm, "end": v(-34.52, -12.65) * mm});
            skLineSegment(sketch, "E1335", {"start": v(-34.52, -12.65) * mm, "end": v(-34.52, -13.28) * mm});
            skLineSegment(sketch, "E1336", {"start": v(-34.52, -13.28) * mm, "end": v(-34.52, -13.9) * mm});
            skLineSegment(sketch, "E1337", {"start": v(-34.52, -13.9) * mm, "end": v(-34.51, -14) * mm});
            skLineSegment(sketch, "E1338", {"start": v(-34.51, -14) * mm, "end": v(-34.49, -14.08) * mm});
            skLineSegment(sketch, "E1339", {"start": v(-34.49, -14.08) * mm, "end": v(-34.44, -14.16) * mm});
            skLineSegment(sketch, "E1340", {"start": v(-34.44, -14.16) * mm, "end": v(-34.39, -14.22) * mm});
            skLineSegment(sketch, "E1341", {"start": v(-34.39, -14.22) * mm, "end": v(-34.32, -14.28) * mm});
            skLineSegment(sketch, "E1342", {"start": v(-34.32, -14.28) * mm, "end": v(-34.24, -14.32) * mm});
            skLineSegment(sketch, "E1343", {"start": v(-34.24, -14.32) * mm, "end": v(-34.16, -14.35) * mm});
            skLineSegment(sketch, "E1344", {"start": v(-34.16, -14.35) * mm, "end": v(-34.07, -14.36) * mm});
            skLineSegment(sketch, "E1345", {"start": v(-34.07, -14.36) * mm, "end": v(-33.58, -14.36) * mm});
            skLineSegment(sketch, "E1346", {"start": v(-33.58, -14.36) * mm, "end": v(-33.1, -14.36) * mm});
            skLineSegment(sketch, "E1347", {"start": v(-33.1, -14.36) * mm, "end": v(-32.61, -14.36) * mm});
            skLineSegment(sketch, "E1348", {"start": v(-32.61, -14.36) * mm, "end": v(-32.13, -14.36) * mm});
            skLineSegment(sketch, "E1349", {"start": v(-32.13, -14.36) * mm, "end": v(-31.65, -14.36) * mm});
            skLineSegment(sketch, "E1350", {"start": v(-31.65, -14.36) * mm, "end": v(-31.16, -14.36) * mm});
            skLineSegment(sketch, "E1351", {"start": v(-31.16, -14.36) * mm, "end": v(-30.68, -14.36) * mm});
            skLineSegment(sketch, "E1352", {"start": v(-30.68, -14.36) * mm, "end": v(-30.2, -14.36) * mm});
            skLineSegment(sketch, "E1353", {"start": v(-30.2, -14.36) * mm, "end": v(-30.2, -14.56) * mm});
            skLineSegment(sketch, "E1354", {"start": v(-30.2, -14.56) * mm, "end": v(-30.2, -14.76) * mm});
            skLineSegment(sketch, "E1355", {"start": v(-30.2, -14.76) * mm, "end": v(-30.2, -14.96) * mm});
            skLineSegment(sketch, "E1356", {"start": v(-30.2, -14.96) * mm, "end": v(-30.2, -15.17) * mm});
            skLineSegment(sketch, "E1357", {"start": v(-30.2, -15.17) * mm, "end": v(-30.2, -15.37) * mm});
            skLineSegment(sketch, "E1358", {"start": v(-30.2, -15.37) * mm, "end": v(-30.2, -15.57) * mm});
            skLineSegment(sketch, "E1359", {"start": v(-30.2, -15.57) * mm, "end": v(-30.2, -15.77) * mm});
            skLineSegment(sketch, "E1360", {"start": v(-30.2, -15.77) * mm, "end": v(-30.2, -15.98) * mm});
            skLineSegment(sketch, "E1361", {"start": v(-30.2, -15.98) * mm, "end": v(-30.77, -15.98) * mm});
            skLineSegment(sketch, "E1362", {"start": v(-30.77, -15.98) * mm, "end": v(-31.34, -15.98) * mm});
            skLineSegment(sketch, "E1363", {"start": v(-31.34, -15.98) * mm, "end": v(-31.9, -15.98) * mm});
            skLineSegment(sketch, "E1364", {"start": v(-31.9, -15.98) * mm, "end": v(-32.48, -15.98) * mm});
            skLineSegment(sketch, "E1365", {"start": v(-32.48, -15.98) * mm, "end": v(-33.05, -15.98) * mm});
            skLineSegment(sketch, "E1366", {"start": v(-33.05, -15.98) * mm, "end": v(-33.62, -15.98) * mm});
            skLineSegment(sketch, "E1367", {"start": v(-33.62, -15.98) * mm, "end": v(-34.2, -15.98) * mm});
            skLineSegment(sketch, "E1368", {"start": v(-34.2, -15.98) * mm, "end": v(-34.76, -15.98) * mm});
            skLineSegment(sketch, "E1369", {"start": v(-34.76, -15.98) * mm, "end": v(-35.07, -15.95) * mm});
            skLineSegment(sketch, "E1370", {"start": v(-35.07, -15.95) * mm, "end": v(-35.36, -15.86) * mm});
            skLineSegment(sketch, "E1371", {"start": v(-35.36, -15.86) * mm, "end": v(-35.62, -15.72) * mm});
            skLineSegment(sketch, "E1372", {"start": v(-35.62, -15.72) * mm, "end": v(-35.84, -15.53) * mm});
            skLineSegment(sketch, "E1373", {"start": v(-35.84, -15.53) * mm, "end": v(-36.03, -15.3) * mm});
            skLineSegment(sketch, "E1374", {"start": v(-36.03, -15.3) * mm, "end": v(-36.17, -15.05) * mm});
            skLineSegment(sketch, "E1375", {"start": v(-36.17, -15.05) * mm, "end": v(-36.26, -14.77) * mm});
            skLineSegment(sketch, "E1376", {"start": v(-36.26, -14.77) * mm, "end": v(-36.3, -14.46) * mm});
            skLineSegment(sketch, "E1377", {"start": v(-36.3, -14.46) * mm, "end": v(-36.3, -13.7) * mm});
            skLineSegment(sketch, "E1378", {"start": v(-36.3, -13.7) * mm, "end": v(-36.3, -12.94) * mm});
            skLineSegment(sketch, "E1379", {"start": v(-36.3, -12.94) * mm, "end": v(-36.3, -12.18) * mm});
            skLineSegment(sketch, "E1380", {"start": v(-36.3, -12.18) * mm, "end": v(-36.3, -11.41) * mm});
            skLineSegment(sketch, "E1381", {"start": v(-36.3, -11.41) * mm, "end": v(-36.3, -10.65) * mm});
            skLineSegment(sketch, "E1382", {"start": v(-36.3, -10.65) * mm, "end": v(-36.3, -9.9) * mm});
            skLineSegment(sketch, "E1383", {"start": v(-36.3, -9.9) * mm, "end": v(-36.3, -9.13) * mm});
            skLineSegment(sketch, "E1384", {"start": v(-36.3, -9.13) * mm, "end": v(-36.3, -8.37) * mm});
            skLineSegment(sketch, "E1385", {"start": v(-36.3, -8.37) * mm, "end": v(-36.26, -8.06) * mm});
            skLineSegment(sketch, "E1386", {"start": v(-36.26, -8.06) * mm, "end": v(-36.17, -7.77) * mm});
            skLineSegment(sketch, "E1387", {"start": v(-36.17, -7.77) * mm, "end": v(-36.03, -7.51) * mm});
            skLineSegment(sketch, "E1388", {"start": v(-36.03, -7.51) * mm, "end": v(-35.84, -7.29) * mm});
            skLineSegment(sketch, "E1389", {"start": v(-35.84, -7.29) * mm, "end": v(-35.62, -7.1) * mm});
            skLineSegment(sketch, "E1390", {"start": v(-35.62, -7.1) * mm, "end": v(-35.36, -6.96) * mm});
            skLineSegment(sketch, "E1391", {"start": v(-35.36, -6.96) * mm, "end": v(-35.07, -6.87) * mm});
            skLineSegment(sketch, "E1392", {"start": v(-35.07, -6.87) * mm, "end": v(-34.76, -6.84) * mm});
            skLineSegment(sketch, "E1393", {"start": v(-34.76, -6.84) * mm, "end": v(-34.2, -6.84) * mm});
            skLineSegment(sketch, "E1394", {"start": v(-34.2, -6.84) * mm, "end": v(-33.62, -6.84) * mm});
            skLineSegment(sketch, "E1395", {"start": v(-33.62, -6.84) * mm, "end": v(-33.05, -6.84) * mm});
            skLineSegment(sketch, "E1396", {"start": v(-33.05, -6.84) * mm, "end": v(-32.48, -6.84) * mm});
            skLineSegment(sketch, "E1397", {"start": v(-32.48, -6.84) * mm, "end": v(-31.9, -6.84) * mm});
            skLineSegment(sketch, "E1398", {"start": v(-31.9, -6.84) * mm, "end": v(-31.34, -6.84) * mm});
            skLineSegment(sketch, "E1399", {"start": v(-31.34, -6.84) * mm, "end": v(-30.77, -6.84) * mm});
            skLineSegment(sketch, "E1400", {"start": v(-30.77, -6.84) * mm, "end": v(-30.2, -6.84) * mm});
            skLineSegment(sketch, "E1401", {"start": v(-30.2, -6.84) * mm, "end": v(-30.2, -7.04) * mm});
            skLineSegment(sketch, "E1402", {"start": v(-30.2, -7.04) * mm, "end": v(-30.2, -7.24) * mm});
            skLineSegment(sketch, "E1403", {"start": v(-30.2, -7.24) * mm, "end": v(-30.2, -7.45) * mm});
            skLineSegment(sketch, "E1404", {"start": v(-30.2, -7.45) * mm, "end": v(-30.2, -7.65) * mm});
            skLineSegment(sketch, "E1405", {"start": v(-30.2, -7.65) * mm, "end": v(-30.2, -7.85) * mm});
            skLineSegment(sketch, "E1406", {"start": v(-30.2, -7.85) * mm, "end": v(-30.2, -8.06) * mm});
            skLineSegment(sketch, "E1407", {"start": v(-30.2, -8.06) * mm, "end": v(-30.2, -8.26) * mm});
            skLineSegment(sketch, "E1408", {"start": v(-30.2, -8.26) * mm, "end": v(-30.2, -8.46) * mm});
            skLineSegment(sketch, "E1409", {"start": v(-28.65, -6.84) * mm, "end": v(-28.43, -6.84) * mm});
            skLineSegment(sketch, "E1410", {"start": v(-28.43, -6.84) * mm, "end": v(-28.21, -6.84) * mm});
            skLineSegment(sketch, "E1411", {"start": v(-28.21, -6.84) * mm, "end": v(-27.99, -6.84) * mm});
            skLineSegment(sketch, "E1412", {"start": v(-27.99, -6.84) * mm, "end": v(-27.77, -6.84) * mm});
            skLineSegment(sketch, "E1413", {"start": v(-27.77, -6.84) * mm, "end": v(-27.55, -6.84) * mm});
            skLineSegment(sketch, "E1414", {"start": v(-27.55, -6.84) * mm, "end": v(-27.33, -6.84) * mm});
            skLineSegment(sketch, "E1415", {"start": v(-27.33, -6.84) * mm, "end": v(-27.1, -6.84) * mm});
            skLineSegment(sketch, "E1416", {"start": v(-27.1, -6.84) * mm, "end": v(-26.88, -6.84) * mm});
            skLineSegment(sketch, "E1417", {"start": v(-26.88, -6.84) * mm, "end": v(-26.88, -7.3) * mm});
            skLineSegment(sketch, "E1418", {"start": v(-26.88, -7.3) * mm, "end": v(-26.88, -7.78) * mm});
            skLineSegment(sketch, "E1419", {"start": v(-26.88, -7.78) * mm, "end": v(-26.88, -8.25) * mm});
            skLineSegment(sketch, "E1420", {"start": v(-26.88, -8.25) * mm, "end": v(-26.88, -8.72) * mm});
            skLineSegment(sketch, "E1421", {"start": v(-26.88, -8.72) * mm, "end": v(-26.88, -9.2) * mm});
            skLineSegment(sketch, "E1422", {"start": v(-26.88, -9.2) * mm, "end": v(-26.88, -9.66) * mm});
            skLineSegment(sketch, "E1423", {"start": v(-26.88, -9.66) * mm, "end": v(-26.88, -10.13) * mm});
            skLineSegment(sketch, "E1424", {"start": v(-26.88, -10.13) * mm, "end": v(-26.88, -10.6) * mm});
            skLineSegment(sketch, "E1425", {"start": v(-26.88, -10.6) * mm, "end": v(-26.37, -10.6) * mm});
            skLineSegment(sketch, "E1426", {"start": v(-26.37, -10.6) * mm, "end": v(-25.87, -10.6) * mm});
            skLineSegment(sketch, "E1427", {"start": v(-25.87, -10.6) * mm, "end": v(-25.36, -10.6) * mm});
            skLineSegment(sketch, "E1428", {"start": v(-25.36, -10.6) * mm, "end": v(-24.85, -10.6) * mm});
            skLineSegment(sketch, "E1429", {"start": v(-24.85, -10.6) * mm, "end": v(-24.34, -10.6) * mm});
            skLineSegment(sketch, "E1430", {"start": v(-24.34, -10.6) * mm, "end": v(-23.83, -10.6) * mm});
            skLineSegment(sketch, "E1431", {"start": v(-23.83, -10.6) * mm, "end": v(-23.32, -10.6) * mm});
            skLineSegment(sketch, "E1432", {"start": v(-23.32, -10.6) * mm, "end": v(-22.81, -10.6) * mm});
            skLineSegment(sketch, "E1433", {"start": v(-22.81, -10.6) * mm, "end": v(-22.81, -10.13) * mm});
            skLineSegment(sketch, "E1434", {"start": v(-22.81, -10.13) * mm, "end": v(-22.81, -9.66) * mm});
            skLineSegment(sketch, "E1435", {"start": v(-22.81, -9.66) * mm, "end": v(-22.81, -9.2) * mm});
            skLineSegment(sketch, "E1436", {"start": v(-22.81, -9.2) * mm, "end": v(-22.81, -8.72) * mm});
            skLineSegment(sketch, "E1437", {"start": v(-22.81, -8.72) * mm, "end": v(-22.81, -8.25) * mm});
            skLineSegment(sketch, "E1438", {"start": v(-22.81, -8.25) * mm, "end": v(-22.81, -7.78) * mm});
            skLineSegment(sketch, "E1439", {"start": v(-22.81, -7.78) * mm, "end": v(-22.81, -7.3) * mm});
            skLineSegment(sketch, "E1440", {"start": v(-22.81, -7.3) * mm, "end": v(-22.81, -6.84) * mm});
            skLineSegment(sketch, "E1441", {"start": v(-22.81, -6.84) * mm, "end": v(-22.59, -6.84) * mm});
            skLineSegment(sketch, "E1442", {"start": v(-22.59, -6.84) * mm, "end": v(-22.37, -6.84) * mm});
            skLineSegment(sketch, "E1443", {"start": v(-22.37, -6.84) * mm, "end": v(-22.15, -6.84) * mm});
            skLineSegment(sketch, "E1444", {"start": v(-22.15, -6.84) * mm, "end": v(-21.93, -6.84) * mm});
            skLineSegment(sketch, "E1445", {"start": v(-21.93, -6.84) * mm, "end": v(-21.7, -6.84) * mm});
            skLineSegment(sketch, "E1446", {"start": v(-21.7, -6.84) * mm, "end": v(-21.48, -6.84) * mm});
            skLineSegment(sketch, "E1447", {"start": v(-21.48, -6.84) * mm, "end": v(-21.26, -6.84) * mm});
            skLineSegment(sketch, "E1448", {"start": v(-21.26, -6.84) * mm, "end": v(-21.04, -6.84) * mm});
            skLineSegment(sketch, "E1449", {"start": v(-21.04, -6.84) * mm, "end": v(-21.04, -7.98) * mm});
            skLineSegment(sketch, "E1450", {"start": v(-21.04, -7.98) * mm, "end": v(-21.04, -9.12) * mm});
            skLineSegment(sketch, "E1451", {"start": v(-21.04, -9.12) * mm, "end": v(-21.04, -10.27) * mm});
            skLineSegment(sketch, "E1452", {"start": v(-21.04, -10.27) * mm, "end": v(-21.04, -11.4) * mm});
            skLineSegment(sketch, "E1453", {"start": v(-21.04, -11.4) * mm, "end": v(-21.04, -12.55) * mm});
            skLineSegment(sketch, "E1454", {"start": v(-21.04, -12.55) * mm, "end": v(-21.04, -13.7) * mm});
            skLineSegment(sketch, "E1455", {"start": v(-21.04, -13.7) * mm, "end": v(-21.04, -14.83) * mm});
            skLineSegment(sketch, "E1456", {"start": v(-21.04, -14.83) * mm, "end": v(-21.04, -15.98) * mm});
            skLineSegment(sketch, "E1457", {"start": v(-21.04, -15.98) * mm, "end": v(-21.26, -15.98) * mm});
            skLineSegment(sketch, "E1458", {"start": v(-21.26, -15.98) * mm, "end": v(-21.48, -15.98) * mm});
            skLineSegment(sketch, "E1459", {"start": v(-21.48, -15.98) * mm, "end": v(-21.7, -15.98) * mm});
            skLineSegment(sketch, "E1460", {"start": v(-21.7, -15.98) * mm, "end": v(-21.93, -15.98) * mm});
            skLineSegment(sketch, "E1461", {"start": v(-21.93, -15.98) * mm, "end": v(-22.15, -15.98) * mm});
            skLineSegment(sketch, "E1462", {"start": v(-22.15, -15.98) * mm, "end": v(-22.37, -15.98) * mm});
            skLineSegment(sketch, "E1463", {"start": v(-22.37, -15.98) * mm, "end": v(-22.59, -15.98) * mm});
            skLineSegment(sketch, "E1464", {"start": v(-22.59, -15.98) * mm, "end": v(-22.81, -15.98) * mm});
            skLineSegment(sketch, "E1465", {"start": v(-22.81, -15.98) * mm, "end": v(-22.81, -15.5) * mm});
            skLineSegment(sketch, "E1466", {"start": v(-22.81, -15.5) * mm, "end": v(-22.81, -15.04) * mm});
            skLineSegment(sketch, "E1467", {"start": v(-22.81, -15.04) * mm, "end": v(-22.81, -14.57) * mm});
            skLineSegment(sketch, "E1468", {"start": v(-22.81, -14.57) * mm, "end": v(-22.81, -14.1) * mm});
            skLineSegment(sketch, "E1469", {"start": v(-22.81, -14.1) * mm, "end": v(-22.81, -13.63) * mm});
            skLineSegment(sketch, "E1470", {"start": v(-22.81, -13.63) * mm, "end": v(-22.81, -13.16) * mm});
            skLineSegment(sketch, "E1471", {"start": v(-22.81, -13.16) * mm, "end": v(-22.81, -12.7) * mm});
            skLineSegment(sketch, "E1472", {"start": v(-22.81, -12.7) * mm, "end": v(-22.81, -12.23) * mm});
            skLineSegment(sketch, "E1473", {"start": v(-22.81, -12.23) * mm, "end": v(-23.32, -12.23) * mm});
            skLineSegment(sketch, "E1474", {"start": v(-23.32, -12.23) * mm, "end": v(-23.83, -12.23) * mm});
            skLineSegment(sketch, "E1475", {"start": v(-23.83, -12.23) * mm, "end": v(-24.34, -12.23) * mm});
            skLineSegment(sketch, "E1476", {"start": v(-24.34, -12.23) * mm, "end": v(-24.85, -12.23) * mm});
            skLineSegment(sketch, "E1477", {"start": v(-24.85, -12.23) * mm, "end": v(-25.36, -12.23) * mm});
            skLineSegment(sketch, "E1478", {"start": v(-25.36, -12.23) * mm, "end": v(-25.87, -12.23) * mm});
            skLineSegment(sketch, "E1479", {"start": v(-25.87, -12.23) * mm, "end": v(-26.37, -12.23) * mm});
            skLineSegment(sketch, "E1480", {"start": v(-26.37, -12.23) * mm, "end": v(-26.88, -12.23) * mm});
            skLineSegment(sketch, "E1481", {"start": v(-26.88, -12.23) * mm, "end": v(-26.88, -12.7) * mm});
            skLineSegment(sketch, "E1482", {"start": v(-26.88, -12.7) * mm, "end": v(-26.88, -13.16) * mm});
            skLineSegment(sketch, "E1483", {"start": v(-26.88, -13.16) * mm, "end": v(-26.88, -13.63) * mm});
            skLineSegment(sketch, "E1484", {"start": v(-26.88, -13.63) * mm, "end": v(-26.88, -14.1) * mm});
            skLineSegment(sketch, "E1485", {"start": v(-26.88, -14.1) * mm, "end": v(-26.88, -14.57) * mm});
            skLineSegment(sketch, "E1486", {"start": v(-26.88, -14.57) * mm, "end": v(-26.88, -15.04) * mm});
            skLineSegment(sketch, "E1487", {"start": v(-26.88, -15.04) * mm, "end": v(-26.88, -15.5) * mm});
            skLineSegment(sketch, "E1488", {"start": v(-26.88, -15.5) * mm, "end": v(-26.88, -15.98) * mm});
            skLineSegment(sketch, "E1489", {"start": v(-26.88, -15.98) * mm, "end": v(-27.1, -15.98) * mm});
            skLineSegment(sketch, "E1490", {"start": v(-27.1, -15.98) * mm, "end": v(-27.33, -15.98) * mm});
            skLineSegment(sketch, "E1491", {"start": v(-27.33, -15.98) * mm, "end": v(-27.55, -15.98) * mm});
            skLineSegment(sketch, "E1492", {"start": v(-27.55, -15.98) * mm, "end": v(-27.77, -15.98) * mm});
            skLineSegment(sketch, "E1493", {"start": v(-27.77, -15.98) * mm, "end": v(-27.99, -15.98) * mm});
            skLineSegment(sketch, "E1494", {"start": v(-27.99, -15.98) * mm, "end": v(-28.21, -15.98) * mm});
            skLineSegment(sketch, "E1495", {"start": v(-28.21, -15.98) * mm, "end": v(-28.43, -15.98) * mm});
            skLineSegment(sketch, "E1496", {"start": v(-28.43, -15.98) * mm, "end": v(-28.65, -15.98) * mm});
            skLineSegment(sketch, "E1497", {"start": v(-28.65, -15.98) * mm, "end": v(-28.65, -14.83) * mm});
            skLineSegment(sketch, "E1498", {"start": v(-28.65, -14.83) * mm, "end": v(-28.65, -13.7) * mm});
            skLineSegment(sketch, "E1499", {"start": v(-28.65, -13.7) * mm, "end": v(-28.65, -12.55) * mm});
            skLineSegment(sketch, "E1500", {"start": v(-28.65, -12.55) * mm, "end": v(-28.65, -11.4) * mm});
            skLineSegment(sketch, "E1501", {"start": v(-28.65, -11.4) * mm, "end": v(-28.65, -10.27) * mm});
            skLineSegment(sketch, "E1502", {"start": v(-28.65, -10.27) * mm, "end": v(-28.65, -9.12) * mm});
            skLineSegment(sketch, "E1503", {"start": v(-28.65, -9.12) * mm, "end": v(-28.65, -7.98) * mm});
            skLineSegment(sketch, "E1504", {"start": v(-28.65, -7.98) * mm, "end": v(-28.65, -6.84) * mm});
            skLineSegment(sketch, "E1505", {"start": v(-16.71, -6.83) * mm, "end": v(-16.49, -6.83) * mm});
            skLineSegment(sketch, "E1506", {"start": v(-16.49, -6.83) * mm, "end": v(-16.26, -6.83) * mm});
            skLineSegment(sketch, "E1507", {"start": v(-16.26, -6.83) * mm, "end": v(-16.04, -6.83) * mm});
            skLineSegment(sketch, "E1508", {"start": v(-16.04, -6.83) * mm, "end": v(-15.82, -6.83) * mm});
            skLineSegment(sketch, "E1509", {"start": v(-15.82, -6.83) * mm, "end": v(-15.6, -6.83) * mm});
            skLineSegment(sketch, "E1510", {"start": v(-15.6, -6.83) * mm, "end": v(-15.37, -6.83) * mm});
            skLineSegment(sketch, "E1511", {"start": v(-15.37, -6.83) * mm, "end": v(-15.14, -6.83) * mm});
            skLineSegment(sketch, "E1512", {"start": v(-15.14, -6.83) * mm, "end": v(-14.92, -6.83) * mm});
            skLineSegment(sketch, "E1513", {"start": v(-14.92, -6.83) * mm, "end": v(-14.5, -7.97) * mm});
            skLineSegment(sketch, "E1514", {"start": v(-14.5, -7.97) * mm, "end": v(-14.07, -9.11) * mm});
            skLineSegment(sketch, "E1515", {"start": v(-14.07, -9.11) * mm, "end": v(-13.65, -10.26) * mm});
            skLineSegment(sketch, "E1516", {"start": v(-13.65, -10.26) * mm, "end": v(-13.22, -11.4) * mm});
            skLineSegment(sketch, "E1517", {"start": v(-13.22, -11.4) * mm, "end": v(-12.8, -12.55) * mm});
            skLineSegment(sketch, "E1518", {"start": v(-12.8, -12.55) * mm, "end": v(-12.38, -13.69) * mm});
            skLineSegment(sketch, "E1519", {"start": v(-12.38, -13.69) * mm, "end": v(-11.95, -14.83) * mm});
            skLineSegment(sketch, "E1520", {"start": v(-11.95, -14.83) * mm, "end": v(-11.53, -15.98) * mm});
            skLineSegment(sketch, "E1521", {"start": v(-11.53, -15.98) * mm, "end": v(-11.78, -15.98) * mm});
            skLineSegment(sketch, "E1522", {"start": v(-11.78, -15.98) * mm, "end": v(-12.02, -15.98) * mm});
            skLineSegment(sketch, "E1523", {"start": v(-12.02, -15.98) * mm, "end": v(-12.27, -15.98) * mm});
            skLineSegment(sketch, "E1524", {"start": v(-12.27, -15.98) * mm, "end": v(-12.52, -15.98) * mm});
            skLineSegment(sketch, "E1525", {"start": v(-12.52, -15.98) * mm, "end": v(-12.77, -15.98) * mm});
            skLineSegment(sketch, "E1526", {"start": v(-12.77, -15.98) * mm, "end": v(-13.02, -15.98) * mm});
            skLineSegment(sketch, "E1527", {"start": v(-13.02, -15.98) * mm, "end": v(-13.26, -15.98) * mm});
            skLineSegment(sketch, "E1528", {"start": v(-13.26, -15.98) * mm, "end": v(-13.51, -15.98) * mm});
            skLineSegment(sketch, "E1529", {"start": v(-13.51, -15.98) * mm, "end": v(-13.6, -15.75) * mm});
            skLineSegment(sketch, "E1530", {"start": v(-13.6, -15.75) * mm, "end": v(-13.67, -15.52) * mm});
            skLineSegment(sketch, "E1531", {"start": v(-13.67, -15.52) * mm, "end": v(-13.75, -15.3) * mm});
            skLineSegment(sketch, "E1532", {"start": v(-13.75, -15.3) * mm, "end": v(-13.83, -15.07) * mm});
            skLineSegment(sketch, "E1533", {"start": v(-13.83, -15.07) * mm, "end": v(-13.91, -14.85) * mm});
            skLineSegment(sketch, "E1534", {"start": v(-13.91, -14.85) * mm, "end": v(-14, -14.62) * mm});
            skLineSegment(sketch, "E1535", {"start": v(-14, -14.62) * mm, "end": v(-14.07, -14.4) * mm});
            skLineSegment(sketch, "E1536", {"start": v(-14.07, -14.4) * mm, "end": v(-14.15, -14.17) * mm});
            skLineSegment(sketch, "E1537", {"start": v(-14.15, -14.17) * mm, "end": v(-14.6, -14.17) * mm});
            skLineSegment(sketch, "E1538", {"start": v(-14.6, -14.17) * mm, "end": v(-15.03, -14.17) * mm});
            skLineSegment(sketch, "E1539", {"start": v(-15.03, -14.17) * mm, "end": v(-15.47, -14.17) * mm});
            skLineSegment(sketch, "E1540", {"start": v(-15.47, -14.17) * mm, "end": v(-15.9, -14.17) * mm});
            skLineSegment(sketch, "E1541", {"start": v(-15.9, -14.17) * mm, "end": v(-16.35, -14.17) * mm});
            skLineSegment(sketch, "E1542", {"start": v(-16.35, -14.17) * mm, "end": v(-16.79, -14.17) * mm});
            skLineSegment(sketch, "E1543", {"start": v(-16.79, -14.17) * mm, "end": v(-17.23, -14.17) * mm});
            skLineSegment(sketch, "E1544", {"start": v(-17.23, -14.17) * mm, "end": v(-17.66, -14.17) * mm});
            skLineSegment(sketch, "E1545", {"start": v(-17.66, -14.17) * mm, "end": v(-17.75, -14.4) * mm});
            skLineSegment(sketch, "E1546", {"start": v(-17.75, -14.4) * mm, "end": v(-17.83, -14.62) * mm});
            skLineSegment(sketch, "E1547", {"start": v(-17.83, -14.62) * mm, "end": v(-17.9, -14.85) * mm});
            skLineSegment(sketch, "E1548", {"start": v(-17.9, -14.85) * mm, "end": v(-17.99, -15.07) * mm});
            skLineSegment(sketch, "E1549", {"start": v(-17.99, -15.07) * mm, "end": v(-18.07, -15.3) * mm});
            skLineSegment(sketch, "E1550", {"start": v(-18.07, -15.3) * mm, "end": v(-18.15, -15.52) * mm});
            skLineSegment(sketch, "E1551", {"start": v(-18.15, -15.52) * mm, "end": v(-18.23, -15.75) * mm});
            skLineSegment(sketch, "E1552", {"start": v(-18.23, -15.75) * mm, "end": v(-18.3, -15.98) * mm});
            skLineSegment(sketch, "E1553", {"start": v(-18.3, -15.98) * mm, "end": v(-18.53, -15.98) * mm});
            skLineSegment(sketch, "E1554", {"start": v(-18.53, -15.98) * mm, "end": v(-18.76, -15.98) * mm});
            skLineSegment(sketch, "E1555", {"start": v(-18.76, -15.98) * mm, "end": v(-18.98, -15.98) * mm});
            skLineSegment(sketch, "E1556", {"start": v(-18.98, -15.98) * mm, "end": v(-19.2, -15.98) * mm});
            skLineSegment(sketch, "E1557", {"start": v(-19.2, -15.98) * mm, "end": v(-19.43, -15.98) * mm});
            skLineSegment(sketch, "E1558", {"start": v(-19.43, -15.98) * mm, "end": v(-19.65, -15.98) * mm});
            skLineSegment(sketch, "E1559", {"start": v(-19.65, -15.98) * mm, "end": v(-19.88, -15.98) * mm});
            skLineSegment(sketch, "E1560", {"start": v(-19.88, -15.98) * mm, "end": v(-20.1, -15.98) * mm});
            skLineSegment(sketch, "E1561", {"start": v(-20.1, -15.98) * mm, "end": v(-19.68, -14.83) * mm});
            skLineSegment(sketch, "E1562", {"start": v(-19.68, -14.83) * mm, "end": v(-19.26, -13.69) * mm});
            skLineSegment(sketch, "E1563", {"start": v(-19.26, -13.69) * mm, "end": v(-18.83, -12.55) * mm});
            skLineSegment(sketch, "E1564", {"start": v(-18.83, -12.55) * mm, "end": v(-18.4, -11.4) * mm});
            skLineSegment(sketch, "E1565", {"start": v(-18.4, -11.4) * mm, "end": v(-17.98, -10.26) * mm});
            skLineSegment(sketch, "E1566", {"start": v(-17.98, -10.26) * mm, "end": v(-17.56, -9.11) * mm});
            skLineSegment(sketch, "E1567", {"start": v(-17.56, -9.11) * mm, "end": v(-17.14, -7.97) * mm});
            skLineSegment(sketch, "E1568", {"start": v(-17.14, -7.97) * mm, "end": v(-16.71, -6.83) * mm});
            skLineSegment(sketch, "E1569", {"start": v(-17.14, -12.68) * mm, "end": v(-16.84, -12.68) * mm});
            skLineSegment(sketch, "E1570", {"start": v(-16.84, -12.68) * mm, "end": v(-16.53, -12.68) * mm});
            skLineSegment(sketch, "E1571", {"start": v(-16.53, -12.68) * mm, "end": v(-16.22, -12.68) * mm});
            skLineSegment(sketch, "E1572", {"start": v(-16.22, -12.68) * mm, "end": v(-15.92, -12.68) * mm});
            skLineSegment(sketch, "E1573", {"start": v(-15.92, -12.68) * mm, "end": v(-15.61, -12.68) * mm});
            skLineSegment(sketch, "E1574", {"start": v(-15.61, -12.68) * mm, "end": v(-15.3, -12.68) * mm});
            skLineSegment(sketch, "E1575", {"start": v(-15.3, -12.68) * mm, "end": v(-15, -12.68) * mm});
            skLineSegment(sketch, "E1576", {"start": v(-15, -12.68) * mm, "end": v(-14.7, -12.68) * mm});
            skLineSegment(sketch, "E1577", {"start": v(-14.7, -12.68) * mm, "end": v(-14.84, -12.25) * mm});
            skLineSegment(sketch, "E1578", {"start": v(-14.84, -12.25) * mm, "end": v(-15, -11.82) * mm});
            skLineSegment(sketch, "E1579", {"start": v(-15, -11.82) * mm, "end": v(-15.15, -11.39) * mm});
            skLineSegment(sketch, "E1580", {"start": v(-15.15, -11.39) * mm, "end": v(-15.3, -10.95) * mm});
            skLineSegment(sketch, "E1581", {"start": v(-15.3, -10.95) * mm, "end": v(-15.46, -10.52) * mm});
            skLineSegment(sketch, "E1582", {"start": v(-15.46, -10.52) * mm, "end": v(-15.61, -10.09) * mm});
            skLineSegment(sketch, "E1583", {"start": v(-15.61, -10.09) * mm, "end": v(-15.77, -9.66) * mm});
            skLineSegment(sketch, "E1584", {"start": v(-15.77, -9.66) * mm, "end": v(-15.92, -9.22) * mm});
            skLineSegment(sketch, "E1585", {"start": v(-15.92, -9.22) * mm, "end": v(-16.08, -9.66) * mm});
            skLineSegment(sketch, "E1586", {"start": v(-16.08, -9.66) * mm, "end": v(-16.23, -10.09) * mm});
            skLineSegment(sketch, "E1587", {"start": v(-16.23, -10.09) * mm, "end": v(-16.38, -10.52) * mm});
            skLineSegment(sketch, "E1588", {"start": v(-16.38, -10.52) * mm, "end": v(-16.53, -10.95) * mm});
            skLineSegment(sketch, "E1589", {"start": v(-16.53, -10.95) * mm, "end": v(-16.69, -11.39) * mm});
            skLineSegment(sketch, "E1590", {"start": v(-16.69, -11.39) * mm, "end": v(-16.84, -11.82) * mm});
            skLineSegment(sketch, "E1591", {"start": v(-16.84, -11.82) * mm, "end": v(-17, -12.25) * mm});
            skLineSegment(sketch, "E1592", {"start": v(-17, -12.25) * mm, "end": v(-17.14, -12.68) * mm});
            skLineSegment(sketch, "E1593", {"start": v(-8.82, -14.36) * mm, "end": v(-8.32, -14.36) * mm});
            skLineSegment(sketch, "E1594", {"start": v(-8.32, -14.36) * mm, "end": v(-7.82, -14.36) * mm});
            skLineSegment(sketch, "E1595", {"start": v(-7.82, -14.36) * mm, "end": v(-7.31, -14.36) * mm});
            skLineSegment(sketch, "E1596", {"start": v(-7.31, -14.36) * mm, "end": v(-6.81, -14.36) * mm});
            skLineSegment(sketch, "E1597", {"start": v(-6.81, -14.36) * mm, "end": v(-6.3, -14.36) * mm});
            skLineSegment(sketch, "E1598", {"start": v(-6.3, -14.36) * mm, "end": v(-5.8, -14.36) * mm});
            skLineSegment(sketch, "E1599", {"start": v(-5.8, -14.36) * mm, "end": v(-5.3, -14.36) * mm});
            skLineSegment(sketch, "E1600", {"start": v(-5.3, -14.36) * mm, "end": v(-4.8, -14.36) * mm});
            skLineSegment(sketch, "E1601", {"start": v(-4.8, -14.36) * mm, "end": v(-4.8, -14.56) * mm});
            skLineSegment(sketch, "E1602", {"start": v(-4.8, -14.56) * mm, "end": v(-4.8, -14.76) * mm});
            skLineSegment(sketch, "E1603", {"start": v(-4.8, -14.76) * mm, "end": v(-4.8, -14.96) * mm});
            skLineSegment(sketch, "E1604", {"start": v(-4.8, -14.96) * mm, "end": v(-4.8, -15.17) * mm});
            skLineSegment(sketch, "E1605", {"start": v(-4.8, -15.17) * mm, "end": v(-4.8, -15.37) * mm});
            skLineSegment(sketch, "E1606", {"start": v(-4.8, -15.37) * mm, "end": v(-4.8, -15.57) * mm});
            skLineSegment(sketch, "E1607", {"start": v(-4.8, -15.57) * mm, "end": v(-4.8, -15.77) * mm});
            skLineSegment(sketch, "E1608", {"start": v(-4.8, -15.77) * mm, "end": v(-4.8, -15.98) * mm});
            skLineSegment(sketch, "E1609", {"start": v(-4.8, -15.98) * mm, "end": v(-5.52, -15.98) * mm});
            skLineSegment(sketch, "E1610", {"start": v(-5.52, -15.98) * mm, "end": v(-6.25, -15.98) * mm});
            skLineSegment(sketch, "E1611", {"start": v(-6.25, -15.98) * mm, "end": v(-6.97, -15.98) * mm});
            skLineSegment(sketch, "E1612", {"start": v(-6.97, -15.98) * mm, "end": v(-7.7, -15.98) * mm});
            skLineSegment(sketch, "E1613", {"start": v(-7.7, -15.98) * mm, "end": v(-8.42, -15.98) * mm});
            skLineSegment(sketch, "E1614", {"start": v(-8.42, -15.98) * mm, "end": v(-9.14, -15.98) * mm});
            skLineSegment(sketch, "E1615", {"start": v(-9.14, -15.98) * mm, "end": v(-9.87, -15.98) * mm});
            skLineSegment(sketch, "E1616", {"start": v(-9.87, -15.98) * mm, "end": v(-10.59, -15.98) * mm});
            skLineSegment(sketch, "E1617", {"start": v(-10.59, -15.98) * mm, "end": v(-10.59, -14.83) * mm});
            skLineSegment(sketch, "E1618", {"start": v(-10.59, -14.83) * mm, "end": v(-10.59, -13.7) * mm});
            skLineSegment(sketch, "E1619", {"start": v(-10.59, -13.7) * mm, "end": v(-10.59, -12.55) * mm});
            skLineSegment(sketch, "E1620", {"start": v(-10.59, -12.55) * mm, "end": v(-10.59, -11.4) * mm});
            skLineSegment(sketch, "E1621", {"start": v(-10.59, -11.4) * mm, "end": v(-10.59, -10.27) * mm});
            skLineSegment(sketch, "E1622", {"start": v(-10.59, -10.27) * mm, "end": v(-10.59, -9.12) * mm});
            skLineSegment(sketch, "E1623", {"start": v(-10.59, -9.12) * mm, "end": v(-10.59, -7.98) * mm});
            skLineSegment(sketch, "E1624", {"start": v(-10.59, -7.98) * mm, "end": v(-10.59, -6.84) * mm});
            skLineSegment(sketch, "E1625", {"start": v(-10.59, -6.84) * mm, "end": v(-10.37, -6.84) * mm});
            skLineSegment(sketch, "E1626", {"start": v(-10.37, -6.84) * mm, "end": v(-10.15, -6.84) * mm});
            skLineSegment(sketch, "E1627", {"start": v(-10.15, -6.84) * mm, "end": v(-9.93, -6.84) * mm});
            skLineSegment(sketch, "E1628", {"start": v(-9.93, -6.84) * mm, "end": v(-9.7, -6.84) * mm});
            skLineSegment(sketch, "E1629", {"start": v(-9.7, -6.84) * mm, "end": v(-9.48, -6.84) * mm});
            skLineSegment(sketch, "E1630", {"start": v(-9.48, -6.84) * mm, "end": v(-9.26, -6.84) * mm});
            skLineSegment(sketch, "E1631", {"start": v(-9.26, -6.84) * mm, "end": v(-9.04, -6.84) * mm});
            skLineSegment(sketch, "E1632", {"start": v(-9.04, -6.84) * mm, "end": v(-8.82, -6.84) * mm});
            skLineSegment(sketch, "E1633", {"start": v(-8.82, -6.84) * mm, "end": v(-8.82, -7.78) * mm});
            skLineSegment(sketch, "E1634", {"start": v(-8.82, -7.78) * mm, "end": v(-8.82, -8.72) * mm});
            skLineSegment(sketch, "E1635", {"start": v(-8.82, -8.72) * mm, "end": v(-8.82, -9.66) * mm});
            skLineSegment(sketch, "E1636", {"start": v(-8.82, -9.66) * mm, "end": v(-8.82, -10.6) * mm});
            skLineSegment(sketch, "E1637", {"start": v(-8.82, -10.6) * mm, "end": v(-8.82, -11.54) * mm});
            skLineSegment(sketch, "E1638", {"start": v(-8.82, -11.54) * mm, "end": v(-8.82, -12.48) * mm});
            skLineSegment(sketch, "E1639", {"start": v(-8.82, -12.48) * mm, "end": v(-8.82, -13.42) * mm});
            skLineSegment(sketch, "E1640", {"start": v(-8.82, -13.42) * mm, "end": v(-8.82, -14.36) * mm});
            skLineSegment(sketch, "E1641", {"start": v(-1.76, -14.36) * mm, "end": v(-1.26, -14.36) * mm});
            skLineSegment(sketch, "E1642", {"start": v(-1.26, -14.36) * mm, "end": v(-0.75, -14.36) * mm});
            skLineSegment(sketch, "E1643", {"start": v(-0.75, -14.36) * mm, "end": v(-0.25, -14.36) * mm});
            skLineSegment(sketch, "E1644", {"start": v(-0.25, -14.36) * mm, "end": v(0.25, -14.36) * mm});
            skLineSegment(sketch, "E1645", {"start": v(0.25, -14.36) * mm, "end": v(0.75, -14.36) * mm});
            skLineSegment(sketch, "E1646", {"start": v(0.75, -14.36) * mm, "end": v(1.26, -14.36) * mm});
            skLineSegment(sketch, "E1647", {"start": v(1.26, -14.36) * mm, "end": v(1.76, -14.36) * mm});
            skLineSegment(sketch, "E1648", {"start": v(1.76, -14.36) * mm, "end": v(2.26, -14.36) * mm});
            skLineSegment(sketch, "E1649", {"start": v(2.26, -14.36) * mm, "end": v(2.26, -14.56) * mm});
            skLineSegment(sketch, "E1650", {"start": v(2.26, -14.56) * mm, "end": v(2.26, -14.76) * mm});
            skLineSegment(sketch, "E1651", {"start": v(2.26, -14.76) * mm, "end": v(2.26, -14.96) * mm});
            skLineSegment(sketch, "E1652", {"start": v(2.26, -14.96) * mm, "end": v(2.26, -15.17) * mm});
            skLineSegment(sketch, "E1653", {"start": v(2.26, -15.17) * mm, "end": v(2.26, -15.37) * mm});
            skLineSegment(sketch, "E1654", {"start": v(2.26, -15.37) * mm, "end": v(2.26, -15.57) * mm});
            skLineSegment(sketch, "E1655", {"start": v(2.26, -15.57) * mm, "end": v(2.26, -15.77) * mm});
            skLineSegment(sketch, "E1656", {"start": v(2.26, -15.77) * mm, "end": v(2.26, -15.98) * mm});
            skLineSegment(sketch, "E1657", {"start": v(2.26, -15.98) * mm, "end": v(1.54, -15.98) * mm});
            skLineSegment(sketch, "E1658", {"start": v(1.54, -15.98) * mm, "end": v(0.81, -15.98) * mm});
            skLineSegment(sketch, "E1659", {"start": v(0.81, -15.98) * mm, "end": v(0.09, -15.98) * mm});
            skLineSegment(sketch, "E1660", {"start": v(0.09, -15.98) * mm, "end": v(-0.63, -15.98) * mm});
            skLineSegment(sketch, "E1661", {"start": v(-0.63, -15.98) * mm, "end": v(-1.36, -15.98) * mm});
            skLineSegment(sketch, "E1662", {"start": v(-1.36, -15.98) * mm, "end": v(-2.08, -15.98) * mm});
            skLineSegment(sketch, "E1663", {"start": v(-2.08, -15.98) * mm, "end": v(-2.8, -15.98) * mm});
            skLineSegment(sketch, "E1664", {"start": v(-2.8, -15.98) * mm, "end": v(-3.53, -15.98) * mm});
            skLineSegment(sketch, "E1665", {"start": v(-3.53, -15.98) * mm, "end": v(-3.53, -14.83) * mm});
            skLineSegment(sketch, "E1666", {"start": v(-3.53, -14.83) * mm, "end": v(-3.53, -13.7) * mm});
            skLineSegment(sketch, "E1667", {"start": v(-3.53, -13.7) * mm, "end": v(-3.53, -12.55) * mm});
            skLineSegment(sketch, "E1668", {"start": v(-3.53, -12.55) * mm, "end": v(-3.53, -11.4) * mm});
            skLineSegment(sketch, "E1669", {"start": v(-3.53, -11.4) * mm, "end": v(-3.53, -10.27) * mm});
            skLineSegment(sketch, "E1670", {"start": v(-3.53, -10.27) * mm, "end": v(-3.53, -9.12) * mm});
            skLineSegment(sketch, "E1671", {"start": v(-3.53, -9.12) * mm, "end": v(-3.53, -7.98) * mm});
            skLineSegment(sketch, "E1672", {"start": v(-3.53, -7.98) * mm, "end": v(-3.53, -6.84) * mm});
            skLineSegment(sketch, "E1673", {"start": v(-3.53, -6.84) * mm, "end": v(-3.3, -6.84) * mm});
            skLineSegment(sketch, "E1674", {"start": v(-3.3, -6.84) * mm, "end": v(-3.09, -6.84) * mm});
            skLineSegment(sketch, "E1675", {"start": v(-3.09, -6.84) * mm, "end": v(-2.86, -6.84) * mm});
            skLineSegment(sketch, "E1676", {"start": v(-2.86, -6.84) * mm, "end": v(-2.64, -6.84) * mm});
            skLineSegment(sketch, "E1677", {"start": v(-2.64, -6.84) * mm, "end": v(-2.42, -6.84) * mm});
            skLineSegment(sketch, "E1678", {"start": v(-2.42, -6.84) * mm, "end": v(-2.2, -6.84) * mm});
            skLineSegment(sketch, "E1679", {"start": v(-2.2, -6.84) * mm, "end": v(-1.98, -6.84) * mm});
            skLineSegment(sketch, "E1680", {"start": v(-1.98, -6.84) * mm, "end": v(-1.76, -6.84) * mm});
            skLineSegment(sketch, "E1681", {"start": v(-1.76, -6.84) * mm, "end": v(-1.76, -7.78) * mm});
            skLineSegment(sketch, "E1682", {"start": v(-1.76, -7.78) * mm, "end": v(-1.76, -8.72) * mm});
            skLineSegment(sketch, "E1683", {"start": v(-1.76, -8.72) * mm, "end": v(-1.76, -9.66) * mm});
            skLineSegment(sketch, "E1684", {"start": v(-1.76, -9.66) * mm, "end": v(-1.76, -10.6) * mm});
            skLineSegment(sketch, "E1685", {"start": v(-1.76, -10.6) * mm, "end": v(-1.76, -11.54) * mm});
            skLineSegment(sketch, "E1686", {"start": v(-1.76, -11.54) * mm, "end": v(-1.76, -12.48) * mm});
            skLineSegment(sketch, "E1687", {"start": v(-1.76, -12.48) * mm, "end": v(-1.76, -13.42) * mm});
            skLineSegment(sketch, "E1688", {"start": v(-1.76, -13.42) * mm, "end": v(-1.76, -14.36) * mm});
            skLineSegment(sketch, "E1689", {"start": v(5.32, -8.46) * mm, "end": v(5.32, -8.73) * mm});
            skLineSegment(sketch, "E1690", {"start": v(5.32, -8.73) * mm, "end": v(5.32, -9) * mm});
            skLineSegment(sketch, "E1691", {"start": v(5.32, -9) * mm, "end": v(5.32, -9.26) * mm});
            skLineSegment(sketch, "E1692", {"start": v(5.32, -9.26) * mm, "end": v(5.32, -9.53) * mm});
            skLineSegment(sketch, "E1693", {"start": v(5.32, -9.53) * mm, "end": v(5.32, -9.8) * mm});
            skLineSegment(sketch, "E1694", {"start": v(5.32, -9.8) * mm, "end": v(5.32, -10.07) * mm});
            skLineSegment(sketch, "E1695", {"start": v(5.32, -10.07) * mm, "end": v(5.32, -10.34) * mm});
            skLineSegment(sketch, "E1696", {"start": v(5.32, -10.34) * mm, "end": v(5.32, -10.6) * mm});
            skLineSegment(sketch, "E1697", {"start": v(5.32, -10.6) * mm, "end": v(5.78, -10.6) * mm});
            skLineSegment(sketch, "E1698", {"start": v(5.78, -10.6) * mm, "end": v(6.24, -10.6) * mm});
            skLineSegment(sketch, "E1699", {"start": v(6.24, -10.6) * mm, "end": v(6.7, -10.6) * mm});
            skLineSegment(sketch, "E1700", {"start": v(6.7, -10.6) * mm, "end": v(7.17, -10.6) * mm});
            skLineSegment(sketch, "E1701", {"start": v(7.17, -10.6) * mm, "end": v(7.64, -10.6) * mm});
            skLineSegment(sketch, "E1702", {"start": v(7.64, -10.6) * mm, "end": v(8.1, -10.6) * mm});
            skLineSegment(sketch, "E1703", {"start": v(8.1, -10.6) * mm, "end": v(8.56, -10.6) * mm});
            skLineSegment(sketch, "E1704", {"start": v(8.56, -10.6) * mm, "end": v(9.03, -10.6) * mm});
            skLineSegment(sketch, "E1705", {"start": v(9.03, -10.6) * mm, "end": v(9.03, -10.8) * mm});
            skLineSegment(sketch, "E1706", {"start": v(9.03, -10.8) * mm, "end": v(9.03, -11) * mm});
            skLineSegment(sketch, "E1707", {"start": v(9.03, -11) * mm, "end": v(9.03, -11.21) * mm});
            skLineSegment(sketch, "E1708", {"start": v(9.03, -11.21) * mm, "end": v(9.03, -11.41) * mm});
            skLineSegment(sketch, "E1709", {"start": v(9.03, -11.41) * mm, "end": v(9.03, -11.62) * mm});
            skLineSegment(sketch, "E1710", {"start": v(9.03, -11.62) * mm, "end": v(9.03, -11.82) * mm});
            skLineSegment(sketch, "E1711", {"start": v(9.03, -11.82) * mm, "end": v(9.03, -12.02) * mm});
            skLineSegment(sketch, "E1712", {"start": v(9.03, -12.02) * mm, "end": v(9.03, -12.23) * mm});
            skLineSegment(sketch, "E1713", {"start": v(9.03, -12.23) * mm, "end": v(8.56, -12.23) * mm});
            skLineSegment(sketch, "E1714", {"start": v(8.56, -12.23) * mm, "end": v(8.1, -12.23) * mm});
            skLineSegment(sketch, "E1715", {"start": v(8.1, -12.23) * mm, "end": v(7.64, -12.23) * mm});
            skLineSegment(sketch, "E1716", {"start": v(7.64, -12.23) * mm, "end": v(7.17, -12.23) * mm});
            skLineSegment(sketch, "E1717", {"start": v(7.17, -12.23) * mm, "end": v(6.7, -12.23) * mm});
            skLineSegment(sketch, "E1718", {"start": v(6.7, -12.23) * mm, "end": v(6.24, -12.23) * mm});
            skLineSegment(sketch, "E1719", {"start": v(6.24, -12.23) * mm, "end": v(5.78, -12.23) * mm});
            skLineSegment(sketch, "E1720", {"start": v(5.78, -12.23) * mm, "end": v(5.32, -12.23) * mm});
            skLineSegment(sketch, "E1721", {"start": v(5.32, -12.23) * mm, "end": v(5.32, -12.5) * mm});
            skLineSegment(sketch, "E1722", {"start": v(5.32, -12.5) * mm, "end": v(5.32, -12.76) * mm});
            skLineSegment(sketch, "E1723", {"start": v(5.32, -12.76) * mm, "end": v(5.32, -13.02) * mm});
            skLineSegment(sketch, "E1724", {"start": v(5.32, -13.02) * mm, "end": v(5.32, -13.3) * mm});
            skLineSegment(sketch, "E1725", {"start": v(5.32, -13.3) * mm, "end": v(5.32, -13.56) * mm});
            skLineSegment(sketch, "E1726", {"start": v(5.32, -13.56) * mm, "end": v(5.32, -13.82) * mm});
            skLineSegment(sketch, "E1727", {"start": v(5.32, -13.82) * mm, "end": v(5.32, -14.1) * mm});
            skLineSegment(sketch, "E1728", {"start": v(5.32, -14.1) * mm, "end": v(5.32, -14.36) * mm});
            skLineSegment(sketch, "E1729", {"start": v(5.32, -14.36) * mm, "end": v(5.9, -14.36) * mm});
            skLineSegment(sketch, "E1730", {"start": v(5.9, -14.36) * mm, "end": v(6.47, -14.36) * mm});
            skLineSegment(sketch, "E1731", {"start": v(6.47, -14.36) * mm, "end": v(7.05, -14.36) * mm});
            skLineSegment(sketch, "E1732", {"start": v(7.05, -14.36) * mm, "end": v(7.63, -14.36) * mm});
            skLineSegment(sketch, "E1733", {"start": v(7.63, -14.36) * mm, "end": v(8.2, -14.36) * mm});
            skLineSegment(sketch, "E1734", {"start": v(8.2, -14.36) * mm, "end": v(8.78, -14.36) * mm});
            skLineSegment(sketch, "E1735", {"start": v(8.78, -14.36) * mm, "end": v(9.36, -14.36) * mm});
            skLineSegment(sketch, "E1736", {"start": v(9.36, -14.36) * mm, "end": v(9.94, -14.36) * mm});
            skLineSegment(sketch, "E1737", {"start": v(9.94, -14.36) * mm, "end": v(9.94, -14.56) * mm});
            skLineSegment(sketch, "E1738", {"start": v(9.94, -14.56) * mm, "end": v(9.94, -14.76) * mm});
            skLineSegment(sketch, "E1739", {"start": v(9.94, -14.76) * mm, "end": v(9.94, -14.96) * mm});
            skLineSegment(sketch, "E1740", {"start": v(9.94, -14.96) * mm, "end": v(9.94, -15.17) * mm});
            skLineSegment(sketch, "E1741", {"start": v(9.94, -15.17) * mm, "end": v(9.94, -15.37) * mm});
            skLineSegment(sketch, "E1742", {"start": v(9.94, -15.37) * mm, "end": v(9.94, -15.57) * mm});
            skLineSegment(sketch, "E1743", {"start": v(9.94, -15.57) * mm, "end": v(9.94, -15.77) * mm});
            skLineSegment(sketch, "E1744", {"start": v(9.94, -15.77) * mm, "end": v(9.94, -15.98) * mm});
            skLineSegment(sketch, "E1745", {"start": v(9.94, -15.98) * mm, "end": v(9.14, -15.98) * mm});
            skLineSegment(sketch, "E1746", {"start": v(9.14, -15.98) * mm, "end": v(8.34, -15.98) * mm});
            skLineSegment(sketch, "E1747", {"start": v(8.34, -15.98) * mm, "end": v(7.54, -15.98) * mm});
            skLineSegment(sketch, "E1748", {"start": v(7.54, -15.98) * mm, "end": v(6.74, -15.98) * mm});
            skLineSegment(sketch, "E1749", {"start": v(6.74, -15.98) * mm, "end": v(5.94, -15.98) * mm});
            skLineSegment(sketch, "E1750", {"start": v(5.94, -15.98) * mm, "end": v(5.14, -15.98) * mm});
            skLineSegment(sketch, "E1751", {"start": v(5.14, -15.98) * mm, "end": v(4.33, -15.98) * mm});
            skLineSegment(sketch, "E1752", {"start": v(4.33, -15.98) * mm, "end": v(3.53, -15.98) * mm});
            skLineSegment(sketch, "E1753", {"start": v(3.53, -15.98) * mm, "end": v(3.53, -14.83) * mm});
            skLineSegment(sketch, "E1754", {"start": v(3.53, -14.83) * mm, "end": v(3.53, -13.7) * mm});
            skLineSegment(sketch, "E1755", {"start": v(3.53, -13.7) * mm, "end": v(3.53, -12.55) * mm});
            skLineSegment(sketch, "E1756", {"start": v(3.53, -12.55) * mm, "end": v(3.53, -11.4) * mm});
            skLineSegment(sketch, "E1757", {"start": v(3.53, -11.4) * mm, "end": v(3.53, -10.27) * mm});
            skLineSegment(sketch, "E1758", {"start": v(3.53, -10.27) * mm, "end": v(3.53, -9.12) * mm});
            skLineSegment(sketch, "E1759", {"start": v(3.53, -9.12) * mm, "end": v(3.53, -7.98) * mm});
            skLineSegment(sketch, "E1760", {"start": v(3.53, -7.98) * mm, "end": v(3.53, -6.84) * mm});
            skLineSegment(sketch, "E1761", {"start": v(3.53, -6.84) * mm, "end": v(4.33, -6.84) * mm});
            skLineSegment(sketch, "E1762", {"start": v(4.33, -6.84) * mm, "end": v(5.14, -6.84) * mm});
            skLineSegment(sketch, "E1763", {"start": v(5.14, -6.84) * mm, "end": v(5.94, -6.84) * mm});
            skLineSegment(sketch, "E1764", {"start": v(5.94, -6.84) * mm, "end": v(6.74, -6.84) * mm});
            skLineSegment(sketch, "E1765", {"start": v(6.74, -6.84) * mm, "end": v(7.54, -6.84) * mm});
            skLineSegment(sketch, "E1766", {"start": v(7.54, -6.84) * mm, "end": v(8.34, -6.84) * mm});
            skLineSegment(sketch, "E1767", {"start": v(8.34, -6.84) * mm, "end": v(9.14, -6.84) * mm});
            skLineSegment(sketch, "E1768", {"start": v(9.14, -6.84) * mm, "end": v(9.94, -6.84) * mm});
            skLineSegment(sketch, "E1769", {"start": v(9.94, -6.84) * mm, "end": v(9.94, -7.04) * mm});
            skLineSegment(sketch, "E1770", {"start": v(9.94, -7.04) * mm, "end": v(9.94, -7.24) * mm});
            skLineSegment(sketch, "E1771", {"start": v(9.94, -7.24) * mm, "end": v(9.94, -7.45) * mm});
            skLineSegment(sketch, "E1772", {"start": v(9.94, -7.45) * mm, "end": v(9.94, -7.65) * mm});
            skLineSegment(sketch, "E1773", {"start": v(9.94, -7.65) * mm, "end": v(9.94, -7.85) * mm});
            skLineSegment(sketch, "E1774", {"start": v(9.94, -7.85) * mm, "end": v(9.94, -8.06) * mm});
            skLineSegment(sketch, "E1775", {"start": v(9.94, -8.06) * mm, "end": v(9.94, -8.26) * mm});
            skLineSegment(sketch, "E1776", {"start": v(9.94, -8.26) * mm, "end": v(9.94, -8.46) * mm});
            skLineSegment(sketch, "E1777", {"start": v(9.94, -8.46) * mm, "end": v(9.36, -8.46) * mm});
            skLineSegment(sketch, "E1778", {"start": v(9.36, -8.46) * mm, "end": v(8.78, -8.46) * mm});
            skLineSegment(sketch, "E1779", {"start": v(8.78, -8.46) * mm, "end": v(8.2, -8.46) * mm});
            skLineSegment(sketch, "E1780", {"start": v(8.2, -8.46) * mm, "end": v(7.63, -8.46) * mm});
            skLineSegment(sketch, "E1781", {"start": v(7.63, -8.46) * mm, "end": v(7.05, -8.46) * mm});
            skLineSegment(sketch, "E1782", {"start": v(7.05, -8.46) * mm, "end": v(6.47, -8.46) * mm});
            skLineSegment(sketch, "E1783", {"start": v(6.47, -8.46) * mm, "end": v(5.9, -8.46) * mm});
            skLineSegment(sketch, "E1784", {"start": v(5.9, -8.46) * mm, "end": v(5.32, -8.46) * mm});
            skLineSegment(sketch, "E1785", {"start": v(13.03, -6.83) * mm, "end": v(13.55, -7.58) * mm});
            skLineSegment(sketch, "E1786", {"start": v(13.55, -7.58) * mm, "end": v(14.07, -8.34) * mm});
            skLineSegment(sketch, "E1787", {"start": v(14.07, -8.34) * mm, "end": v(14.58, -9.1) * mm});
            skLineSegment(sketch, "E1788", {"start": v(14.58, -9.1) * mm, "end": v(15.1, -9.86) * mm});
            skLineSegment(sketch, "E1789", {"start": v(15.1, -9.86) * mm, "end": v(15.61, -10.62) * mm});
            skLineSegment(sketch, "E1790", {"start": v(15.61, -10.62) * mm, "end": v(16.13, -11.38) * mm});
            skLineSegment(sketch, "E1791", {"start": v(16.13, -11.38) * mm, "end": v(16.65, -12.14) * mm});
            skLineSegment(sketch, "E1792", {"start": v(16.65, -12.14) * mm, "end": v(17.16, -12.9) * mm});
            skLineSegment(sketch, "E1793", {"start": v(17.16, -12.9) * mm, "end": v(17.16, -12.14) * mm});
            skLineSegment(sketch, "E1794", {"start": v(17.16, -12.14) * mm, "end": v(17.16, -11.38) * mm});
            skLineSegment(sketch, "E1795", {"start": v(17.16, -11.38) * mm, "end": v(17.16, -10.62) * mm});
            skLineSegment(sketch, "E1796", {"start": v(17.16, -10.62) * mm, "end": v(17.16, -9.86) * mm});
            skLineSegment(sketch, "E1797", {"start": v(17.16, -9.86) * mm, "end": v(17.16, -9.1) * mm});
            skLineSegment(sketch, "E1798", {"start": v(17.16, -9.1) * mm, "end": v(17.16, -8.34) * mm});
            skLineSegment(sketch, "E1799", {"start": v(17.16, -8.34) * mm, "end": v(17.16, -7.58) * mm});
            skLineSegment(sketch, "E1800", {"start": v(17.16, -7.58) * mm, "end": v(17.16, -6.83) * mm});
            skLineSegment(sketch, "E1801", {"start": v(17.16, -6.83) * mm, "end": v(17.38, -6.83) * mm});
            skLineSegment(sketch, "E1802", {"start": v(17.38, -6.83) * mm, "end": v(17.6, -6.83) * mm});
            skLineSegment(sketch, "E1803", {"start": v(17.6, -6.83) * mm, "end": v(17.82, -6.83) * mm});
            skLineSegment(sketch, "E1804", {"start": v(17.82, -6.83) * mm, "end": v(18.05, -6.83) * mm});
            skLineSegment(sketch, "E1805", {"start": v(18.05, -6.83) * mm, "end": v(18.27, -6.83) * mm});
            skLineSegment(sketch, "E1806", {"start": v(18.27, -6.83) * mm, "end": v(18.49, -6.83) * mm});
            skLineSegment(sketch, "E1807", {"start": v(18.49, -6.83) * mm, "end": v(18.7, -6.83) * mm});
            skLineSegment(sketch, "E1808", {"start": v(18.7, -6.83) * mm, "end": v(18.93, -6.83) * mm});
            skLineSegment(sketch, "E1809", {"start": v(18.93, -6.83) * mm, "end": v(18.93, -7.97) * mm});
            skLineSegment(sketch, "E1810", {"start": v(18.93, -7.97) * mm, "end": v(18.93, -9.11) * mm});
            skLineSegment(sketch, "E1811", {"start": v(18.93, -9.11) * mm, "end": v(18.93, -10.25) * mm});
            skLineSegment(sketch, "E1812", {"start": v(18.93, -10.25) * mm, "end": v(18.93, -11.4) * mm});
            skLineSegment(sketch, "E1813", {"start": v(18.93, -11.4) * mm, "end": v(18.93, -12.54) * mm});
            skLineSegment(sketch, "E1814", {"start": v(18.93, -12.54) * mm, "end": v(18.93, -13.68) * mm});
            skLineSegment(sketch, "E1815", {"start": v(18.93, -13.68) * mm, "end": v(18.93, -14.82) * mm});
            skLineSegment(sketch, "E1816", {"start": v(18.93, -14.82) * mm, "end": v(18.93, -15.96) * mm});
            skLineSegment(sketch, "E1817", {"start": v(18.93, -15.96) * mm, "end": v(18.7, -15.96) * mm});
            skLineSegment(sketch, "E1818", {"start": v(18.7, -15.96) * mm, "end": v(18.47, -15.96) * mm});
            skLineSegment(sketch, "E1819", {"start": v(18.47, -15.96) * mm, "end": v(18.25, -15.96) * mm});
            skLineSegment(sketch, "E1820", {"start": v(18.25, -15.96) * mm, "end": v(18.02, -15.96) * mm});
            skLineSegment(sketch, "E1821", {"start": v(18.02, -15.96) * mm, "end": v(17.8, -15.96) * mm});
            skLineSegment(sketch, "E1822", {"start": v(17.8, -15.96) * mm, "end": v(17.56, -15.96) * mm});
            skLineSegment(sketch, "E1823", {"start": v(17.56, -15.96) * mm, "end": v(17.34, -15.96) * mm});
            skLineSegment(sketch, "E1824", {"start": v(17.34, -15.96) * mm, "end": v(17.1, -15.96) * mm});
            skLineSegment(sketch, "E1825", {"start": v(17.1, -15.96) * mm, "end": v(16.6, -15.2) * mm});
            skLineSegment(sketch, "E1826", {"start": v(16.6, -15.2) * mm, "end": v(16.08, -14.45) * mm});
            skLineSegment(sketch, "E1827", {"start": v(16.08, -14.45) * mm, "end": v(15.56, -13.7) * mm});
            skLineSegment(sketch, "E1828", {"start": v(15.56, -13.7) * mm, "end": v(15.04, -12.94) * mm});
            skLineSegment(sketch, "E1829", {"start": v(15.04, -12.94) * mm, "end": v(14.53, -12.18) * mm});
            skLineSegment(sketch, "E1830", {"start": v(14.53, -12.18) * mm, "end": v(14.01, -11.42) * mm});
            skLineSegment(sketch, "E1831", {"start": v(14.01, -11.42) * mm, "end": v(13.5, -10.66) * mm});
            skLineSegment(sketch, "E1832", {"start": v(13.5, -10.66) * mm, "end": v(12.98, -9.9) * mm});
            skLineSegment(sketch, "E1833", {"start": v(12.98, -9.9) * mm, "end": v(12.98, -10.66) * mm});
            skLineSegment(sketch, "E1834", {"start": v(12.98, -10.66) * mm, "end": v(12.98, -11.42) * mm});
            skLineSegment(sketch, "E1835", {"start": v(12.98, -11.42) * mm, "end": v(12.98, -12.18) * mm});
            skLineSegment(sketch, "E1836", {"start": v(12.98, -12.18) * mm, "end": v(12.98, -12.94) * mm});
            skLineSegment(sketch, "E1837", {"start": v(12.98, -12.94) * mm, "end": v(12.98, -13.7) * mm});
            skLineSegment(sketch, "E1838", {"start": v(12.98, -13.7) * mm, "end": v(12.98, -14.45) * mm});
            skLineSegment(sketch, "E1839", {"start": v(12.98, -14.45) * mm, "end": v(12.98, -15.2) * mm});
            skLineSegment(sketch, "E1840", {"start": v(12.98, -15.2) * mm, "end": v(12.98, -15.96) * mm});
            skLineSegment(sketch, "E1841", {"start": v(12.98, -15.96) * mm, "end": v(12.76, -15.96) * mm});
            skLineSegment(sketch, "E1842", {"start": v(12.76, -15.96) * mm, "end": v(12.54, -15.96) * mm});
            skLineSegment(sketch, "E1843", {"start": v(12.54, -15.96) * mm, "end": v(12.32, -15.96) * mm});
            skLineSegment(sketch, "E1844", {"start": v(12.32, -15.96) * mm, "end": v(12.1, -15.96) * mm});
            skLineSegment(sketch, "E1845", {"start": v(12.1, -15.96) * mm, "end": v(11.88, -15.96) * mm});
            skLineSegment(sketch, "E1846", {"start": v(11.88, -15.96) * mm, "end": v(11.65, -15.96) * mm});
            skLineSegment(sketch, "E1847", {"start": v(11.65, -15.96) * mm, "end": v(11.43, -15.96) * mm});
            skLineSegment(sketch, "E1848", {"start": v(11.43, -15.96) * mm, "end": v(11.21, -15.96) * mm});
            skLineSegment(sketch, "E1849", {"start": v(11.21, -15.96) * mm, "end": v(11.21, -14.82) * mm});
            skLineSegment(sketch, "E1850", {"start": v(11.21, -14.82) * mm, "end": v(11.21, -13.68) * mm});
            skLineSegment(sketch, "E1851", {"start": v(11.21, -13.68) * mm, "end": v(11.21, -12.54) * mm});
            skLineSegment(sketch, "E1852", {"start": v(11.21, -12.54) * mm, "end": v(11.21, -11.4) * mm});
            skLineSegment(sketch, "E1853", {"start": v(11.21, -11.4) * mm, "end": v(11.21, -10.25) * mm});
            skLineSegment(sketch, "E1854", {"start": v(11.21, -10.25) * mm, "end": v(11.21, -9.11) * mm});
            skLineSegment(sketch, "E1855", {"start": v(11.21, -9.11) * mm, "end": v(11.21, -7.97) * mm});
            skLineSegment(sketch, "E1856", {"start": v(11.21, -7.97) * mm, "end": v(11.21, -6.83) * mm});
            skLineSegment(sketch, "E1857", {"start": v(11.21, -6.83) * mm, "end": v(11.44, -6.83) * mm});
            skLineSegment(sketch, "E1858", {"start": v(11.44, -6.83) * mm, "end": v(11.67, -6.83) * mm});
            skLineSegment(sketch, "E1859", {"start": v(11.67, -6.83) * mm, "end": v(11.9, -6.83) * mm});
            skLineSegment(sketch, "E1860", {"start": v(11.9, -6.83) * mm, "end": v(12.12, -6.83) * mm});
            skLineSegment(sketch, "E1861", {"start": v(12.12, -6.83) * mm, "end": v(12.35, -6.83) * mm});
            skLineSegment(sketch, "E1862", {"start": v(12.35, -6.83) * mm, "end": v(12.58, -6.83) * mm});
            skLineSegment(sketch, "E1863", {"start": v(12.58, -6.83) * mm, "end": v(12.8, -6.83) * mm});
            skLineSegment(sketch, "E1864", {"start": v(12.8, -6.83) * mm, "end": v(13.03, -6.83) * mm});
            skLineSegment(sketch, "E1865", {"start": v(22.07, -15.98) * mm, "end": v(21.76, -15.95) * mm});
            skLineSegment(sketch, "E1866", {"start": v(21.76, -15.95) * mm, "end": v(21.47, -15.86) * mm});
            skLineSegment(sketch, "E1867", {"start": v(21.47, -15.86) * mm, "end": v(21.21, -15.72) * mm});
            skLineSegment(sketch, "E1868", {"start": v(21.21, -15.72) * mm, "end": v(20.99, -15.53) * mm});
            skLineSegment(sketch, "E1869", {"start": v(20.99, -15.53) * mm, "end": v(20.8, -15.3) * mm});
            skLineSegment(sketch, "E1870", {"start": v(20.8, -15.3) * mm, "end": v(20.66, -15.05) * mm});
            skLineSegment(sketch, "E1871", {"start": v(20.66, -15.05) * mm, "end": v(20.57, -14.77) * mm});
            skLineSegment(sketch, "E1872", {"start": v(20.57, -14.77) * mm, "end": v(20.54, -14.46) * mm});
            skLineSegment(sketch, "E1873", {"start": v(20.54, -14.46) * mm, "end": v(20.54, -13.7) * mm});
            skLineSegment(sketch, "E1874", {"start": v(20.54, -13.7) * mm, "end": v(20.54, -12.94) * mm});
            skLineSegment(sketch, "E1875", {"start": v(20.54, -12.94) * mm, "end": v(20.54, -12.18) * mm});
            skLineSegment(sketch, "E1876", {"start": v(20.54, -12.18) * mm, "end": v(20.54, -11.41) * mm});
            skLineSegment(sketch, "E1877", {"start": v(20.54, -11.41) * mm, "end": v(20.54, -10.65) * mm});
            skLineSegment(sketch, "E1878", {"start": v(20.54, -10.65) * mm, "end": v(20.54, -9.9) * mm});
            skLineSegment(sketch, "E1879", {"start": v(20.54, -9.9) * mm, "end": v(20.54, -9.13) * mm});
            skLineSegment(sketch, "E1880", {"start": v(20.54, -9.13) * mm, "end": v(20.54, -8.37) * mm});
            skLineSegment(sketch, "E1881", {"start": v(20.54, -8.37) * mm, "end": v(20.57, -8.06) * mm});
            skLineSegment(sketch, "E1882", {"start": v(20.57, -8.06) * mm, "end": v(20.66, -7.77) * mm});
            skLineSegment(sketch, "E1883", {"start": v(20.66, -7.77) * mm, "end": v(20.8, -7.51) * mm});
            skLineSegment(sketch, "E1884", {"start": v(20.8, -7.51) * mm, "end": v(20.99, -7.29) * mm});
            skLineSegment(sketch, "E1885", {"start": v(20.99, -7.29) * mm, "end": v(21.21, -7.1) * mm});
            skLineSegment(sketch, "E1886", {"start": v(21.21, -7.1) * mm, "end": v(21.47, -6.96) * mm});
            skLineSegment(sketch, "E1887", {"start": v(21.47, -6.96) * mm, "end": v(21.76, -6.87) * mm});
            skLineSegment(sketch, "E1888", {"start": v(21.76, -6.87) * mm, "end": v(22.07, -6.84) * mm});
            skLineSegment(sketch, "E1889", {"start": v(22.07, -6.84) * mm, "end": v(22.79, -6.84) * mm});
            skLineSegment(sketch, "E1890", {"start": v(22.79, -6.84) * mm, "end": v(23.51, -6.84) * mm});
            skLineSegment(sketch, "E1891", {"start": v(23.51, -6.84) * mm, "end": v(24.24, -6.84) * mm});
            skLineSegment(sketch, "E1892", {"start": v(24.24, -6.84) * mm, "end": v(24.96, -6.84) * mm});
            skLineSegment(sketch, "E1893", {"start": v(24.96, -6.84) * mm, "end": v(25.68, -6.84) * mm});
            skLineSegment(sketch, "E1894", {"start": v(25.68, -6.84) * mm, "end": v(26.4, -6.84) * mm});
            skLineSegment(sketch, "E1895", {"start": v(26.4, -6.84) * mm, "end": v(27.13, -6.84) * mm});
            skLineSegment(sketch, "E1896", {"start": v(27.13, -6.84) * mm, "end": v(27.85, -6.84) * mm});
            skLineSegment(sketch, "E1897", {"start": v(27.85, -6.84) * mm, "end": v(27.85, -7.04) * mm});
            skLineSegment(sketch, "E1898", {"start": v(27.85, -7.04) * mm, "end": v(27.85, -7.24) * mm});
            skLineSegment(sketch, "E1899", {"start": v(27.85, -7.24) * mm, "end": v(27.85, -7.45) * mm});
            skLineSegment(sketch, "E1900", {"start": v(27.85, -7.45) * mm, "end": v(27.85, -7.65) * mm});
            skLineSegment(sketch, "E1901", {"start": v(27.85, -7.65) * mm, "end": v(27.85, -7.85) * mm});
            skLineSegment(sketch, "E1902", {"start": v(27.85, -7.85) * mm, "end": v(27.85, -8.06) * mm});
            skLineSegment(sketch, "E1903", {"start": v(27.85, -8.06) * mm, "end": v(27.85, -8.26) * mm});
            skLineSegment(sketch, "E1904", {"start": v(27.85, -8.26) * mm, "end": v(27.85, -8.46) * mm});
            skLineSegment(sketch, "E1905", {"start": v(27.85, -8.46) * mm, "end": v(27.22, -8.46) * mm});
            skLineSegment(sketch, "E1906", {"start": v(27.22, -8.46) * mm, "end": v(26.58, -8.46) * mm});
            skLineSegment(sketch, "E1907", {"start": v(26.58, -8.46) * mm, "end": v(25.94, -8.46) * mm});
            skLineSegment(sketch, "E1908", {"start": v(25.94, -8.46) * mm, "end": v(25.3, -8.46) * mm});
            skLineSegment(sketch, "E1909", {"start": v(25.3, -8.46) * mm, "end": v(24.67, -8.46) * mm});
            skLineSegment(sketch, "E1910", {"start": v(24.67, -8.46) * mm, "end": v(24.04, -8.46) * mm});
            skLineSegment(sketch, "E1911", {"start": v(24.04, -8.46) * mm, "end": v(23.4, -8.46) * mm});
            skLineSegment(sketch, "E1912", {"start": v(23.4, -8.46) * mm, "end": v(22.76, -8.46) * mm});
            skLineSegment(sketch, "E1913", {"start": v(22.76, -8.46) * mm, "end": v(22.67, -8.47) * mm});
            skLineSegment(sketch, "E1914", {"start": v(22.67, -8.47) * mm, "end": v(22.58, -8.5) * mm});
            skLineSegment(sketch, "E1915", {"start": v(22.58, -8.5) * mm, "end": v(22.5, -8.54) * mm});
            skLineSegment(sketch, "E1916", {"start": v(22.5, -8.54) * mm, "end": v(22.44, -8.6) * mm});
            skLineSegment(sketch, "E1917", {"start": v(22.44, -8.6) * mm, "end": v(22.38, -8.67) * mm});
            skLineSegment(sketch, "E1918", {"start": v(22.38, -8.67) * mm, "end": v(22.34, -8.74) * mm});
            skLineSegment(sketch, "E1919", {"start": v(22.34, -8.74) * mm, "end": v(22.32, -8.83) * mm});
            skLineSegment(sketch, "E1920", {"start": v(22.32, -8.83) * mm, "end": v(22.3, -8.92) * mm});
            skLineSegment(sketch, "E1921", {"start": v(22.3, -8.92) * mm, "end": v(22.3, -9.54) * mm});
            skLineSegment(sketch, "E1922", {"start": v(22.3, -9.54) * mm, "end": v(22.3, -10.16) * mm});
            skLineSegment(sketch, "E1923", {"start": v(22.3, -10.16) * mm, "end": v(22.3, -10.79) * mm});
            skLineSegment(sketch, "E1924", {"start": v(22.3, -10.79) * mm, "end": v(22.3, -11.4) * mm});
            skLineSegment(sketch, "E1925", {"start": v(22.3, -11.4) * mm, "end": v(22.3, -12.03) * mm});
            skLineSegment(sketch, "E1926", {"start": v(22.3, -12.03) * mm, "end": v(22.3, -12.65) * mm});
            skLineSegment(sketch, "E1927", {"start": v(22.3, -12.65) * mm, "end": v(22.3, -13.28) * mm});
            skLineSegment(sketch, "E1928", {"start": v(22.3, -13.28) * mm, "end": v(22.3, -13.9) * mm});
            skLineSegment(sketch, "E1929", {"start": v(22.3, -13.9) * mm, "end": v(22.32, -14) * mm});
            skLineSegment(sketch, "E1930", {"start": v(22.32, -14) * mm, "end": v(22.34, -14.08) * mm});
            skLineSegment(sketch, "E1931", {"start": v(22.34, -14.08) * mm, "end": v(22.38, -14.16) * mm});
            skLineSegment(sketch, "E1932", {"start": v(22.38, -14.16) * mm, "end": v(22.44, -14.22) * mm});
            skLineSegment(sketch, "E1933", {"start": v(22.44, -14.22) * mm, "end": v(22.5, -14.28) * mm});
            skLineSegment(sketch, "E1934", {"start": v(22.5, -14.28) * mm, "end": v(22.58, -14.32) * mm});
            skLineSegment(sketch, "E1935", {"start": v(22.58, -14.32) * mm, "end": v(22.67, -14.35) * mm});
            skLineSegment(sketch, "E1936", {"start": v(22.67, -14.35) * mm, "end": v(22.76, -14.36) * mm});
            skLineSegment(sketch, "E1937", {"start": v(22.76, -14.36) * mm, "end": v(23.16, -14.36) * mm});
            skLineSegment(sketch, "E1938", {"start": v(23.16, -14.36) * mm, "end": v(23.55, -14.36) * mm});
            skLineSegment(sketch, "E1939", {"start": v(23.55, -14.36) * mm, "end": v(23.95, -14.36) * mm});
            skLineSegment(sketch, "E1940", {"start": v(23.95, -14.36) * mm, "end": v(24.34, -14.36) * mm});
            skLineSegment(sketch, "E1941", {"start": v(24.34, -14.36) * mm, "end": v(24.74, -14.36) * mm});
            skLineSegment(sketch, "E1942", {"start": v(24.74, -14.36) * mm, "end": v(25.13, -14.36) * mm});
            skLineSegment(sketch, "E1943", {"start": v(25.13, -14.36) * mm, "end": v(25.53, -14.36) * mm});
            skLineSegment(sketch, "E1944", {"start": v(25.53, -14.36) * mm, "end": v(25.92, -14.36) * mm});
            skLineSegment(sketch, "E1945", {"start": v(25.92, -14.36) * mm, "end": v(26.02, -14.35) * mm});
            skLineSegment(sketch, "E1946", {"start": v(26.02, -14.35) * mm, "end": v(26.1, -14.32) * mm});
            skLineSegment(sketch, "E1947", {"start": v(26.1, -14.32) * mm, "end": v(26.18, -14.28) * mm});
            skLineSegment(sketch, "E1948", {"start": v(26.18, -14.28) * mm, "end": v(26.25, -14.22) * mm});
            skLineSegment(sketch, "E1949", {"start": v(26.25, -14.22) * mm, "end": v(26.3, -14.16) * mm});
            skLineSegment(sketch, "E1950", {"start": v(26.3, -14.16) * mm, "end": v(26.34, -14.08) * mm});
            skLineSegment(sketch, "E1951", {"start": v(26.34, -14.08) * mm, "end": v(26.37, -14) * mm});
            skLineSegment(sketch, "E1952", {"start": v(26.37, -14) * mm, "end": v(26.38, -13.9) * mm});
            skLineSegment(sketch, "E1953", {"start": v(26.38, -13.9) * mm, "end": v(26.38, -13.69) * mm});
            skLineSegment(sketch, "E1954", {"start": v(26.38, -13.69) * mm, "end": v(26.38, -13.47) * mm});
            skLineSegment(sketch, "E1955", {"start": v(26.38, -13.47) * mm, "end": v(26.38, -13.26) * mm});
            skLineSegment(sketch, "E1956", {"start": v(26.38, -13.26) * mm, "end": v(26.38, -13.05) * mm});
            skLineSegment(sketch, "E1957", {"start": v(26.38, -13.05) * mm, "end": v(26.38, -12.84) * mm});
            skLineSegment(sketch, "E1958", {"start": v(26.38, -12.84) * mm, "end": v(26.38, -12.62) * mm});
            skLineSegment(sketch, "E1959", {"start": v(26.38, -12.62) * mm, "end": v(26.38, -12.41) * mm});
            skLineSegment(sketch, "E1960", {"start": v(26.38, -12.41) * mm, "end": v(26.38, -12.2) * mm});
            skLineSegment(sketch, "E1961", {"start": v(26.38, -12.2) * mm, "end": v(26.1, -12.2) * mm});
            skLineSegment(sketch, "E1962", {"start": v(26.1, -12.2) * mm, "end": v(25.83, -12.2) * mm});
            skLineSegment(sketch, "E1963", {"start": v(25.83, -12.2) * mm, "end": v(25.56, -12.2) * mm});
            skLineSegment(sketch, "E1964", {"start": v(25.56, -12.2) * mm, "end": v(25.29, -12.2) * mm});
            skLineSegment(sketch, "E1965", {"start": v(25.29, -12.2) * mm, "end": v(25.01, -12.2) * mm});
            skLineSegment(sketch, "E1966", {"start": v(25.01, -12.2) * mm, "end": v(24.74, -12.2) * mm});
            skLineSegment(sketch, "E1967", {"start": v(24.74, -12.2) * mm, "end": v(24.47, -12.2) * mm});
            skLineSegment(sketch, "E1968", {"start": v(24.47, -12.2) * mm, "end": v(24.2, -12.2) * mm});
            skLineSegment(sketch, "E1969", {"start": v(24.2, -12.2) * mm, "end": v(24.2, -12) * mm});
            skLineSegment(sketch, "E1970", {"start": v(24.2, -12) * mm, "end": v(24.2, -11.8) * mm});
            skLineSegment(sketch, "E1971", {"start": v(24.2, -11.8) * mm, "end": v(24.2, -11.6) * mm});
            skLineSegment(sketch, "E1972", {"start": v(24.2, -11.6) * mm, "end": v(24.2, -11.39) * mm});
            skLineSegment(sketch, "E1973", {"start": v(24.2, -11.39) * mm, "end": v(24.2, -11.19) * mm});
            skLineSegment(sketch, "E1974", {"start": v(24.2, -11.19) * mm, "end": v(24.2, -10.98) * mm});
            skLineSegment(sketch, "E1975", {"start": v(24.2, -10.98) * mm, "end": v(24.2, -10.78) * mm});
            skLineSegment(sketch, "E1976", {"start": v(24.2, -10.78) * mm, "end": v(24.2, -10.58) * mm});
            skLineSegment(sketch, "E1977", {"start": v(24.2, -10.58) * mm, "end": v(24.7, -10.58) * mm});
            skLineSegment(sketch, "E1978", {"start": v(24.7, -10.58) * mm, "end": v(25.19, -10.58) * mm});
            skLineSegment(sketch, "E1979", {"start": v(25.19, -10.58) * mm, "end": v(25.68, -10.58) * mm});
            skLineSegment(sketch, "E1980", {"start": v(25.68, -10.58) * mm, "end": v(26.18, -10.58) * mm});
            skLineSegment(sketch, "E1981", {"start": v(26.18, -10.58) * mm, "end": v(26.68, -10.58) * mm});
            skLineSegment(sketch, "E1982", {"start": v(26.68, -10.58) * mm, "end": v(27.17, -10.58) * mm});
            skLineSegment(sketch, "E1983", {"start": v(27.17, -10.58) * mm, "end": v(27.67, -10.58) * mm});
            skLineSegment(sketch, "E1984", {"start": v(27.67, -10.58) * mm, "end": v(28.16, -10.58) * mm});
            skLineSegment(sketch, "E1985", {"start": v(28.16, -10.58) * mm, "end": v(28.16, -11.06) * mm});
            skLineSegment(sketch, "E1986", {"start": v(28.16, -11.06) * mm, "end": v(28.16, -11.55) * mm});
            skLineSegment(sketch, "E1987", {"start": v(28.16, -11.55) * mm, "end": v(28.16, -12.03) * mm});
            skLineSegment(sketch, "E1988", {"start": v(28.16, -12.03) * mm, "end": v(28.16, -12.52) * mm});
            skLineSegment(sketch, "E1989", {"start": v(28.16, -12.52) * mm, "end": v(28.16, -13) * mm});
            skLineSegment(sketch, "E1990", {"start": v(28.16, -13) * mm, "end": v(28.16, -13.5) * mm});
            skLineSegment(sketch, "E1991", {"start": v(28.16, -13.5) * mm, "end": v(28.16, -13.98) * mm});
            skLineSegment(sketch, "E1992", {"start": v(28.16, -13.98) * mm, "end": v(28.16, -14.46) * mm});
            skLineSegment(sketch, "E1993", {"start": v(28.16, -14.46) * mm, "end": v(28.13, -14.77) * mm});
            skLineSegment(sketch, "E1994", {"start": v(28.13, -14.77) * mm, "end": v(28.04, -15.05) * mm});
            skLineSegment(sketch, "E1995", {"start": v(28.04, -15.05) * mm, "end": v(27.9, -15.3) * mm});
            skLineSegment(sketch, "E1996", {"start": v(27.9, -15.3) * mm, "end": v(27.72, -15.53) * mm});
            skLineSegment(sketch, "E1997", {"start": v(27.72, -15.53) * mm, "end": v(27.49, -15.72) * mm});
            skLineSegment(sketch, "E1998", {"start": v(27.49, -15.72) * mm, "end": v(27.23, -15.86) * mm});
            skLineSegment(sketch, "E1999", {"start": v(27.23, -15.86) * mm, "end": v(26.94, -15.95) * mm});
            skLineSegment(sketch, "E2000", {"start": v(26.94, -15.95) * mm, "end": v(26.63, -15.98) * mm});
            skLineSegment(sketch, "E2001", {"start": v(26.63, -15.98) * mm, "end": v(26.06, -15.98) * mm});
            skLineSegment(sketch, "E2002", {"start": v(26.06, -15.98) * mm, "end": v(25.5, -15.98) * mm});
            skLineSegment(sketch, "E2003", {"start": v(25.5, -15.98) * mm, "end": v(24.92, -15.98) * mm});
            skLineSegment(sketch, "E2004", {"start": v(24.92, -15.98) * mm, "end": v(24.35, -15.98) * mm});
            skLineSegment(sketch, "E2005", {"start": v(24.35, -15.98) * mm, "end": v(23.78, -15.98) * mm});
            skLineSegment(sketch, "E2006", {"start": v(23.78, -15.98) * mm, "end": v(23.2, -15.98) * mm});
            skLineSegment(sketch, "E2007", {"start": v(23.2, -15.98) * mm, "end": v(22.64, -15.98) * mm});
            skLineSegment(sketch, "E2008", {"start": v(22.64, -15.98) * mm, "end": v(22.07, -15.98) * mm});
            skLineSegment(sketch, "E2009", {"start": v(31.69, -8.46) * mm, "end": v(31.69, -8.73) * mm});
            skLineSegment(sketch, "E2010", {"start": v(31.69, -8.73) * mm, "end": v(31.69, -9) * mm});
            skLineSegment(sketch, "E2011", {"start": v(31.69, -9) * mm, "end": v(31.69, -9.26) * mm});
            skLineSegment(sketch, "E2012", {"start": v(31.69, -9.26) * mm, "end": v(31.69, -9.53) * mm});
            skLineSegment(sketch, "E2013", {"start": v(31.69, -9.53) * mm, "end": v(31.69, -9.8) * mm});
            skLineSegment(sketch, "E2014", {"start": v(31.69, -9.8) * mm, "end": v(31.69, -10.07) * mm});
            skLineSegment(sketch, "E2015", {"start": v(31.69, -10.07) * mm, "end": v(31.69, -10.34) * mm});
            skLineSegment(sketch, "E2016", {"start": v(31.69, -10.34) * mm, "end": v(31.69, -10.6) * mm});
            skLineSegment(sketch, "E2017", {"start": v(31.69, -10.6) * mm, "end": v(32.15, -10.6) * mm});
            skLineSegment(sketch, "E2018", {"start": v(32.15, -10.6) * mm, "end": v(32.62, -10.6) * mm});
            skLineSegment(sketch, "E2019", {"start": v(32.62, -10.6) * mm, "end": v(33.08, -10.6) * mm});
            skLineSegment(sketch, "E2020", {"start": v(33.08, -10.6) * mm, "end": v(33.54, -10.6) * mm});
            skLineSegment(sketch, "E2021", {"start": v(33.54, -10.6) * mm, "end": v(34, -10.6) * mm});
            skLineSegment(sketch, "E2022", {"start": v(34, -10.6) * mm, "end": v(34.47, -10.6) * mm});
            skLineSegment(sketch, "E2023", {"start": v(34.47, -10.6) * mm, "end": v(34.93, -10.6) * mm});
            skLineSegment(sketch, "E2024", {"start": v(34.93, -10.6) * mm, "end": v(35.4, -10.6) * mm});
            skLineSegment(sketch, "E2025", {"start": v(35.4, -10.6) * mm, "end": v(35.4, -10.8) * mm});
            skLineSegment(sketch, "E2026", {"start": v(35.4, -10.8) * mm, "end": v(35.4, -11) * mm});
            skLineSegment(sketch, "E2027", {"start": v(35.4, -11) * mm, "end": v(35.4, -11.21) * mm});
            skLineSegment(sketch, "E2028", {"start": v(35.4, -11.21) * mm, "end": v(35.4, -11.41) * mm});
            skLineSegment(sketch, "E2029", {"start": v(35.4, -11.41) * mm, "end": v(35.4, -11.62) * mm});
            skLineSegment(sketch, "E2030", {"start": v(35.4, -11.62) * mm, "end": v(35.4, -11.82) * mm});
            skLineSegment(sketch, "E2031", {"start": v(35.4, -11.82) * mm, "end": v(35.4, -12.02) * mm});
            skLineSegment(sketch, "E2032", {"start": v(35.4, -12.02) * mm, "end": v(35.4, -12.23) * mm});
            skLineSegment(sketch, "E2033", {"start": v(35.4, -12.23) * mm, "end": v(34.93, -12.23) * mm});
            skLineSegment(sketch, "E2034", {"start": v(34.93, -12.23) * mm, "end": v(34.47, -12.23) * mm});
            skLineSegment(sketch, "E2035", {"start": v(34.47, -12.23) * mm, "end": v(34, -12.23) * mm});
            skLineSegment(sketch, "E2036", {"start": v(34, -12.23) * mm, "end": v(33.54, -12.23) * mm});
            skLineSegment(sketch, "E2037", {"start": v(33.54, -12.23) * mm, "end": v(33.08, -12.23) * mm});
            skLineSegment(sketch, "E2038", {"start": v(33.08, -12.23) * mm, "end": v(32.62, -12.23) * mm});
            skLineSegment(sketch, "E2039", {"start": v(32.62, -12.23) * mm, "end": v(32.15, -12.23) * mm});
            skLineSegment(sketch, "E2040", {"start": v(32.15, -12.23) * mm, "end": v(31.69, -12.23) * mm});
            skLineSegment(sketch, "E2041", {"start": v(31.69, -12.23) * mm, "end": v(31.69, -12.5) * mm});
            skLineSegment(sketch, "E2042", {"start": v(31.69, -12.5) * mm, "end": v(31.69, -12.76) * mm});
            skLineSegment(sketch, "E2043", {"start": v(31.69, -12.76) * mm, "end": v(31.69, -13.02) * mm});
            skLineSegment(sketch, "E2044", {"start": v(31.69, -13.02) * mm, "end": v(31.69, -13.3) * mm});
            skLineSegment(sketch, "E2045", {"start": v(31.69, -13.3) * mm, "end": v(31.69, -13.56) * mm});
            skLineSegment(sketch, "E2046", {"start": v(31.69, -13.56) * mm, "end": v(31.69, -13.82) * mm});
            skLineSegment(sketch, "E2047", {"start": v(31.69, -13.82) * mm, "end": v(31.69, -14.1) * mm});
            skLineSegment(sketch, "E2048", {"start": v(31.69, -14.1) * mm, "end": v(31.69, -14.36) * mm});
            skLineSegment(sketch, "E2049", {"start": v(31.69, -14.36) * mm, "end": v(32.27, -14.36) * mm});
            skLineSegment(sketch, "E2050", {"start": v(32.27, -14.36) * mm, "end": v(32.84, -14.36) * mm});
            skLineSegment(sketch, "E2051", {"start": v(32.84, -14.36) * mm, "end": v(33.42, -14.36) * mm});
            skLineSegment(sketch, "E2052", {"start": v(33.42, -14.36) * mm, "end": v(34, -14.36) * mm});
            skLineSegment(sketch, "E2053", {"start": v(34, -14.36) * mm, "end": v(34.58, -14.36) * mm});
            skLineSegment(sketch, "E2054", {"start": v(34.58, -14.36) * mm, "end": v(35.15, -14.36) * mm});
            skLineSegment(sketch, "E2055", {"start": v(35.15, -14.36) * mm, "end": v(35.73, -14.36) * mm});
            skLineSegment(sketch, "E2056", {"start": v(35.73, -14.36) * mm, "end": v(36.3, -14.36) * mm});
            skLineSegment(sketch, "E2057", {"start": v(36.3, -14.36) * mm, "end": v(36.3, -14.56) * mm});
            skLineSegment(sketch, "E2058", {"start": v(36.3, -14.56) * mm, "end": v(36.3, -14.76) * mm});
            skLineSegment(sketch, "E2059", {"start": v(36.3, -14.76) * mm, "end": v(36.3, -14.96) * mm});
            skLineSegment(sketch, "E2060", {"start": v(36.3, -14.96) * mm, "end": v(36.3, -15.17) * mm});
            skLineSegment(sketch, "E2061", {"start": v(36.3, -15.17) * mm, "end": v(36.3, -15.37) * mm});
            skLineSegment(sketch, "E2062", {"start": v(36.3, -15.37) * mm, "end": v(36.3, -15.57) * mm});
            skLineSegment(sketch, "E2063", {"start": v(36.3, -15.57) * mm, "end": v(36.3, -15.77) * mm});
            skLineSegment(sketch, "E2064", {"start": v(36.3, -15.77) * mm, "end": v(36.3, -15.98) * mm});
            skLineSegment(sketch, "E2065", {"start": v(36.3, -15.98) * mm, "end": v(35.5, -15.98) * mm});
            skLineSegment(sketch, "E2066", {"start": v(35.5, -15.98) * mm, "end": v(34.7, -15.98) * mm});
            skLineSegment(sketch, "E2067", {"start": v(34.7, -15.98) * mm, "end": v(33.9, -15.98) * mm});
            skLineSegment(sketch, "E2068", {"start": v(33.9, -15.98) * mm, "end": v(33.1, -15.98) * mm});
            skLineSegment(sketch, "E2069", {"start": v(33.1, -15.98) * mm, "end": v(32.3, -15.98) * mm});
            skLineSegment(sketch, "E2070", {"start": v(32.3, -15.98) * mm, "end": v(31.5, -15.98) * mm});
            skLineSegment(sketch, "E2071", {"start": v(31.5, -15.98) * mm, "end": v(30.7, -15.98) * mm});
            skLineSegment(sketch, "E2072", {"start": v(30.7, -15.98) * mm, "end": v(29.9, -15.98) * mm});
            skLineSegment(sketch, "E2073", {"start": v(29.9, -15.98) * mm, "end": v(29.9, -14.83) * mm});
            skLineSegment(sketch, "E2074", {"start": v(29.9, -14.83) * mm, "end": v(29.9, -13.7) * mm});
            skLineSegment(sketch, "E2075", {"start": v(29.9, -13.7) * mm, "end": v(29.9, -12.55) * mm});
            skLineSegment(sketch, "E2076", {"start": v(29.9, -12.55) * mm, "end": v(29.9, -11.4) * mm});
            skLineSegment(sketch, "E2077", {"start": v(29.9, -11.4) * mm, "end": v(29.9, -10.27) * mm});
            skLineSegment(sketch, "E2078", {"start": v(29.9, -10.27) * mm, "end": v(29.9, -9.12) * mm});
            skLineSegment(sketch, "E2079", {"start": v(29.9, -9.12) * mm, "end": v(29.9, -7.98) * mm});
            skLineSegment(sketch, "E2080", {"start": v(29.9, -7.98) * mm, "end": v(29.9, -6.84) * mm});
            skLineSegment(sketch, "E2081", {"start": v(29.9, -6.84) * mm, "end": v(30.7, -6.84) * mm});
            skLineSegment(sketch, "E2082", {"start": v(30.7, -6.84) * mm, "end": v(31.5, -6.84) * mm});
            skLineSegment(sketch, "E2083", {"start": v(31.5, -6.84) * mm, "end": v(32.3, -6.84) * mm});
            skLineSegment(sketch, "E2084", {"start": v(32.3, -6.84) * mm, "end": v(33.1, -6.84) * mm});
            skLineSegment(sketch, "E2085", {"start": v(33.1, -6.84) * mm, "end": v(33.9, -6.84) * mm});
            skLineSegment(sketch, "E2086", {"start": v(33.9, -6.84) * mm, "end": v(34.7, -6.84) * mm});
            skLineSegment(sketch, "E2087", {"start": v(34.7, -6.84) * mm, "end": v(35.5, -6.84) * mm});
            skLineSegment(sketch, "E2088", {"start": v(35.5, -6.84) * mm, "end": v(36.3, -6.84) * mm});
            skLineSegment(sketch, "E2089", {"start": v(36.3, -6.84) * mm, "end": v(36.3, -7.04) * mm});
            skLineSegment(sketch, "E2090", {"start": v(36.3, -7.04) * mm, "end": v(36.3, -7.24) * mm});
            skLineSegment(sketch, "E2091", {"start": v(36.3, -7.24) * mm, "end": v(36.3, -7.45) * mm});
            skLineSegment(sketch, "E2092", {"start": v(36.3, -7.45) * mm, "end": v(36.3, -7.65) * mm});
            skLineSegment(sketch, "E2093", {"start": v(36.3, -7.65) * mm, "end": v(36.3, -7.85) * mm});
            skLineSegment(sketch, "E2094", {"start": v(36.3, -7.85) * mm, "end": v(36.3, -8.06) * mm});
            skLineSegment(sketch, "E2095", {"start": v(36.3, -8.06) * mm, "end": v(36.3, -8.26) * mm});
            skLineSegment(sketch, "E2096", {"start": v(36.3, -8.26) * mm, "end": v(36.3, -8.46) * mm});
            skLineSegment(sketch, "E2097", {"start": v(36.3, -8.46) * mm, "end": v(35.73, -8.46) * mm});
            skLineSegment(sketch, "E2098", {"start": v(35.73, -8.46) * mm, "end": v(35.15, -8.46) * mm});
            skLineSegment(sketch, "E2099", {"start": v(35.15, -8.46) * mm, "end": v(34.58, -8.46) * mm});
            skLineSegment(sketch, "E2100", {"start": v(34.58, -8.46) * mm, "end": v(34, -8.46) * mm});
            skLineSegment(sketch, "E2101", {"start": v(34, -8.46) * mm, "end": v(33.42, -8.46) * mm});
            skLineSegment(sketch, "E2102", {"start": v(33.42, -8.46) * mm, "end": v(32.84, -8.46) * mm});
            skLineSegment(sketch, "E2103", {"start": v(32.84, -8.46) * mm, "end": v(32.27, -8.46) * mm});
            skLineSegment(sketch, "E2104", {"start": v(32.27, -8.46) * mm, "end": v(31.69, -8.46) * mm});
            skLineSegment(sketch, "E2105", {"start": v(-7.69, 8.98) * mm, "end": v(-7.6, 8.97) * mm});
            skLineSegment(sketch, "E2106", {"start": v(-7.6, 8.97) * mm, "end": v(-7.5, 8.95) * mm});
            skLineSegment(sketch, "E2107", {"start": v(-7.5, 8.95) * mm, "end": v(-7.43, 8.9) * mm});
            skLineSegment(sketch, "E2108", {"start": v(-7.43, 8.9) * mm, "end": v(-7.36, 8.85) * mm});
            skLineSegment(sketch, "E2109", {"start": v(-7.36, 8.85) * mm, "end": v(-7.3, 8.78) * mm});
            skLineSegment(sketch, "E2110", {"start": v(-7.3, 8.78) * mm, "end": v(-7.26, 8.7) * mm});
            skLineSegment(sketch, "E2111", {"start": v(-7.26, 8.7) * mm, "end": v(-7.23, 8.61) * mm});
            skLineSegment(sketch, "E2112", {"start": v(-7.23, 8.61) * mm, "end": v(-7.22, 8.52) * mm});
            skLineSegment(sketch, "E2113", {"start": v(-7.22, 8.52) * mm, "end": v(-7.22, 8.45) * mm});
            skLineSegment(sketch, "E2114", {"start": v(-7.22, 8.45) * mm, "end": v(-7.22, 8.38) * mm});
            skLineSegment(sketch, "E2115", {"start": v(-7.22, 8.38) * mm, "end": v(-7.22, 8.32) * mm});
            skLineSegment(sketch, "E2116", {"start": v(-7.22, 8.32) * mm, "end": v(-7.22, 8.25) * mm});
            skLineSegment(sketch, "E2117", {"start": v(-7.22, 8.25) * mm, "end": v(-7.22, 8.19) * mm});
            skLineSegment(sketch, "E2118", {"start": v(-7.22, 8.19) * mm, "end": v(-7.22, 8.12) * mm});
            skLineSegment(sketch, "E2119", {"start": v(-7.22, 8.12) * mm, "end": v(-7.22, 8.05) * mm});
            skLineSegment(sketch, "E2120", {"start": v(-7.22, 8.05) * mm, "end": v(-7.22, 7.99) * mm});
            skLineSegment(sketch, "E2121", {"start": v(-7.22, 7.99) * mm, "end": v(-7.23, 7.9) * mm});
            skLineSegment(sketch, "E2122", {"start": v(-7.23, 7.9) * mm, "end": v(-7.26, 7.8) * mm});
            skLineSegment(sketch, "E2123", {"start": v(-7.26, 7.8) * mm, "end": v(-7.3, 7.73) * mm});
            skLineSegment(sketch, "E2124", {"start": v(-7.3, 7.73) * mm, "end": v(-7.36, 7.66) * mm});
            skLineSegment(sketch, "E2125", {"start": v(-7.36, 7.66) * mm, "end": v(-7.43, 7.6) * mm});
            skLineSegment(sketch, "E2126", {"start": v(-7.43, 7.6) * mm, "end": v(-7.5, 7.56) * mm});
            skLineSegment(sketch, "E2127", {"start": v(-7.5, 7.56) * mm, "end": v(-7.6, 7.53) * mm});
            skLineSegment(sketch, "E2128", {"start": v(-7.6, 7.53) * mm, "end": v(-7.69, 7.52) * mm});
            skLineSegment(sketch, "E2129", {"start": v(-7.69, 7.52) * mm, "end": v(-7.83, 7.52) * mm});
            skLineSegment(sketch, "E2130", {"start": v(-7.83, 7.52) * mm, "end": v(-7.98, 7.52) * mm});
            skLineSegment(sketch, "E2131", {"start": v(-7.98, 7.52) * mm, "end": v(-8.13, 7.52) * mm});
            skLineSegment(sketch, "E2132", {"start": v(-8.13, 7.52) * mm, "end": v(-8.27, 7.52) * mm});
            skLineSegment(sketch, "E2133", {"start": v(-8.27, 7.52) * mm, "end": v(-8.42, 7.52) * mm});
            skLineSegment(sketch, "E2134", {"start": v(-8.42, 7.52) * mm, "end": v(-8.57, 7.52) * mm});
            skLineSegment(sketch, "E2135", {"start": v(-8.57, 7.52) * mm, "end": v(-8.72, 7.52) * mm});
            skLineSegment(sketch, "E2136", {"start": v(-8.72, 7.52) * mm, "end": v(-8.86, 7.52) * mm});
            skLineSegment(sketch, "E2137", {"start": v(-8.86, 7.52) * mm, "end": v(-8.86, 7.36) * mm});
            skLineSegment(sketch, "E2138", {"start": v(-8.86, 7.36) * mm, "end": v(-8.86, 7.2) * mm});
            skLineSegment(sketch, "E2139", {"start": v(-8.86, 7.2) * mm, "end": v(-8.86, 7.03) * mm});
            skLineSegment(sketch, "E2140", {"start": v(-8.86, 7.03) * mm, "end": v(-8.86, 6.86) * mm});
            skLineSegment(sketch, "E2141", {"start": v(-8.86, 6.86) * mm, "end": v(-8.86, 6.7) * mm});
            skLineSegment(sketch, "E2142", {"start": v(-8.86, 6.7) * mm, "end": v(-8.86, 6.53) * mm});
            skLineSegment(sketch, "E2143", {"start": v(-8.86, 6.53) * mm, "end": v(-8.86, 6.37) * mm});
            skLineSegment(sketch, "E2144", {"start": v(-8.86, 6.37) * mm, "end": v(-8.86, 6.2) * mm});
            skLineSegment(sketch, "E2145", {"start": v(-8.86, 6.2) * mm, "end": v(-8.89, 6.2) * mm});
            skLineSegment(sketch, "E2146", {"start": v(-8.89, 6.2) * mm, "end": v(-8.91, 6.2) * mm});
            skLineSegment(sketch, "E2147", {"start": v(-8.91, 6.2) * mm, "end": v(-8.94, 6.2) * mm});
            skLineSegment(sketch, "E2148", {"start": v(-8.94, 6.2) * mm, "end": v(-8.97, 6.2) * mm});
            skLineSegment(sketch, "E2149", {"start": v(-8.97, 6.2) * mm, "end": v(-9, 6.2) * mm});
            skLineSegment(sketch, "E2150", {"start": v(-9, 6.2) * mm, "end": v(-9.02, 6.2) * mm});
            skLineSegment(sketch, "E2151", {"start": v(-9.02, 6.2) * mm, "end": v(-9.04, 6.2) * mm});
            skLineSegment(sketch, "E2152", {"start": v(-9.04, 6.2) * mm, "end": v(-9.07, 6.2) * mm});
            skLineSegment(sketch, "E2153", {"start": v(-9.07, 6.2) * mm, "end": v(-9.07, 6.55) * mm});
            skLineSegment(sketch, "E2154", {"start": v(-9.07, 6.55) * mm, "end": v(-9.07, 6.9) * mm});
            skLineSegment(sketch, "E2155", {"start": v(-9.07, 6.9) * mm, "end": v(-9.07, 7.24) * mm});
            skLineSegment(sketch, "E2156", {"start": v(-9.07, 7.24) * mm, "end": v(-9.07, 7.6) * mm});
            skLineSegment(sketch, "E2157", {"start": v(-9.07, 7.6) * mm, "end": v(-9.07, 7.94) * mm});
            skLineSegment(sketch, "E2158", {"start": v(-9.07, 7.94) * mm, "end": v(-9.07, 8.29) * mm});
            skLineSegment(sketch, "E2159", {"start": v(-9.07, 8.29) * mm, "end": v(-9.07, 8.63) * mm});
            skLineSegment(sketch, "E2160", {"start": v(-9.07, 8.63) * mm, "end": v(-9.07, 8.98) * mm});
            skLineSegment(sketch, "E2161", {"start": v(-9.07, 8.98) * mm, "end": v(-8.9, 8.98) * mm});
            skLineSegment(sketch, "E2162", {"start": v(-8.9, 8.98) * mm, "end": v(-8.72, 8.98) * mm});
            skLineSegment(sketch, "E2163", {"start": v(-8.72, 8.98) * mm, "end": v(-8.55, 8.98) * mm});
            skLineSegment(sketch, "E2164", {"start": v(-8.55, 8.98) * mm, "end": v(-8.38, 8.98) * mm});
            skLineSegment(sketch, "E2165", {"start": v(-8.38, 8.98) * mm, "end": v(-8.2, 8.98) * mm});
            skLineSegment(sketch, "E2166", {"start": v(-8.2, 8.98) * mm, "end": v(-8.03, 8.98) * mm});
            skLineSegment(sketch, "E2167", {"start": v(-8.03, 8.98) * mm, "end": v(-7.86, 8.98) * mm});
            skLineSegment(sketch, "E2168", {"start": v(-7.86, 8.98) * mm, "end": v(-7.69, 8.98) * mm});
            skLineSegment(sketch, "E2169", {"start": v(-7.43, 8.52) * mm, "end": v(-7.43, 8.57) * mm});
            skLineSegment(sketch, "E2170", {"start": v(-7.43, 8.57) * mm, "end": v(-7.45, 8.63) * mm});
            skLineSegment(sketch, "E2171", {"start": v(-7.45, 8.63) * mm, "end": v(-7.48, 8.67) * mm});
            skLineSegment(sketch, "E2172", {"start": v(-7.48, 8.67) * mm, "end": v(-7.51, 8.71) * mm});
            skLineSegment(sketch, "E2173", {"start": v(-7.51, 8.71) * mm, "end": v(-7.55, 8.75) * mm});
            skLineSegment(sketch, "E2174", {"start": v(-7.55, 8.75) * mm, "end": v(-7.6, 8.77) * mm});
            skLineSegment(sketch, "E2175", {"start": v(-7.6, 8.77) * mm, "end": v(-7.65, 8.79) * mm});
            skLineSegment(sketch, "E2176", {"start": v(-7.65, 8.79) * mm, "end": v(-7.7, 8.8) * mm});
            skLineSegment(sketch, "E2177", {"start": v(-7.7, 8.8) * mm, "end": v(-7.85, 8.8) * mm});
            skLineSegment(sketch, "E2178", {"start": v(-7.85, 8.8) * mm, "end": v(-8, 8.8) * mm});
            skLineSegment(sketch, "E2179", {"start": v(-8, 8.8) * mm, "end": v(-8.14, 8.8) * mm});
            skLineSegment(sketch, "E2180", {"start": v(-8.14, 8.8) * mm, "end": v(-8.28, 8.8) * mm});
            skLineSegment(sketch, "E2181", {"start": v(-8.28, 8.8) * mm, "end": v(-8.43, 8.8) * mm});
            skLineSegment(sketch, "E2182", {"start": v(-8.43, 8.8) * mm, "end": v(-8.57, 8.8) * mm});
            skLineSegment(sketch, "E2183", {"start": v(-8.57, 8.8) * mm, "end": v(-8.72, 8.8) * mm});
            skLineSegment(sketch, "E2184", {"start": v(-8.72, 8.8) * mm, "end": v(-8.86, 8.8) * mm});
            skLineSegment(sketch, "E2185", {"start": v(-8.86, 8.8) * mm, "end": v(-8.86, 8.66) * mm});
            skLineSegment(sketch, "E2186", {"start": v(-8.86, 8.66) * mm, "end": v(-8.86, 8.52) * mm});
            skLineSegment(sketch, "E2187", {"start": v(-8.86, 8.52) * mm, "end": v(-8.86, 8.39) * mm});
            skLineSegment(sketch, "E2188", {"start": v(-8.86, 8.39) * mm, "end": v(-8.86, 8.25) * mm});
            skLineSegment(sketch, "E2189", {"start": v(-8.86, 8.25) * mm, "end": v(-8.86, 8.11) * mm});
            skLineSegment(sketch, "E2190", {"start": v(-8.86, 8.11) * mm, "end": v(-8.86, 7.98) * mm});
            skLineSegment(sketch, "E2191", {"start": v(-8.86, 7.98) * mm, "end": v(-8.86, 7.84) * mm});
            skLineSegment(sketch, "E2192", {"start": v(-8.86, 7.84) * mm, "end": v(-8.86, 7.7) * mm});
            skLineSegment(sketch, "E2193", {"start": v(-8.86, 7.7) * mm, "end": v(-8.72, 7.7) * mm});
            skLineSegment(sketch, "E2194", {"start": v(-8.72, 7.7) * mm, "end": v(-8.57, 7.7) * mm});
            skLineSegment(sketch, "E2195", {"start": v(-8.57, 7.7) * mm, "end": v(-8.43, 7.7) * mm});
            skLineSegment(sketch, "E2196", {"start": v(-8.43, 7.7) * mm, "end": v(-8.28, 7.7) * mm});
            skLineSegment(sketch, "E2197", {"start": v(-8.28, 7.7) * mm, "end": v(-8.14, 7.7) * mm});
            skLineSegment(sketch, "E2198", {"start": v(-8.14, 7.7) * mm, "end": v(-8, 7.7) * mm});
            skLineSegment(sketch, "E2199", {"start": v(-8, 7.7) * mm, "end": v(-7.85, 7.7) * mm});
            skLineSegment(sketch, "E2200", {"start": v(-7.85, 7.7) * mm, "end": v(-7.7, 7.7) * mm});
            skLineSegment(sketch, "E2201", {"start": v(-7.7, 7.7) * mm, "end": v(-7.65, 7.71) * mm});
            skLineSegment(sketch, "E2202", {"start": v(-7.65, 7.71) * mm, "end": v(-7.6, 7.73) * mm});
            skLineSegment(sketch, "E2203", {"start": v(-7.6, 7.73) * mm, "end": v(-7.55, 7.75) * mm});
            skLineSegment(sketch, "E2204", {"start": v(-7.55, 7.75) * mm, "end": v(-7.51, 7.79) * mm});
            skLineSegment(sketch, "E2205", {"start": v(-7.51, 7.79) * mm, "end": v(-7.48, 7.83) * mm});
            skLineSegment(sketch, "E2206", {"start": v(-7.48, 7.83) * mm, "end": v(-7.45, 7.88) * mm});
            skLineSegment(sketch, "E2207", {"start": v(-7.45, 7.88) * mm, "end": v(-7.43, 7.93) * mm});
            skLineSegment(sketch, "E2208", {"start": v(-7.43, 7.93) * mm, "end": v(-7.43, 7.99) * mm});
            skLineSegment(sketch, "E2209", {"start": v(-7.43, 7.99) * mm, "end": v(-7.43, 8.05) * mm});
            skLineSegment(sketch, "E2210", {"start": v(-7.43, 8.05) * mm, "end": v(-7.43, 8.12) * mm});
            skLineSegment(sketch, "E2211", {"start": v(-7.43, 8.12) * mm, "end": v(-7.43, 8.19) * mm});
            skLineSegment(sketch, "E2212", {"start": v(-7.43, 8.19) * mm, "end": v(-7.43, 8.25) * mm});
            skLineSegment(sketch, "E2213", {"start": v(-7.43, 8.25) * mm, "end": v(-7.43, 8.32) * mm});
            skLineSegment(sketch, "E2214", {"start": v(-7.43, 8.32) * mm, "end": v(-7.43, 8.38) * mm});
            skLineSegment(sketch, "E2215", {"start": v(-7.43, 8.38) * mm, "end": v(-7.43, 8.45) * mm});
            skLineSegment(sketch, "E2216", {"start": v(-7.43, 8.45) * mm, "end": v(-7.43, 8.52) * mm});
            skLineSegment(sketch, "E2217", {"start": v(-4.79, 6.2) * mm, "end": v(-4.82, 6.2) * mm});
            skLineSegment(sketch, "E2218", {"start": v(-4.82, 6.2) * mm, "end": v(-4.85, 6.2) * mm});
            skLineSegment(sketch, "E2219", {"start": v(-4.85, 6.2) * mm, "end": v(-4.88, 6.2) * mm});
            skLineSegment(sketch, "E2220", {"start": v(-4.88, 6.2) * mm, "end": v(-4.9, 6.2) * mm});
            skLineSegment(sketch, "E2221", {"start": v(-4.9, 6.2) * mm, "end": v(-4.94, 6.2) * mm});
            skLineSegment(sketch, "E2222", {"start": v(-4.94, 6.2) * mm, "end": v(-4.97, 6.2) * mm});
            skLineSegment(sketch, "E2223", {"start": v(-4.97, 6.2) * mm, "end": v(-5, 6.2) * mm});
            skLineSegment(sketch, "E2224", {"start": v(-5, 6.2) * mm, "end": v(-5.03, 6.2) * mm});
            skLineSegment(sketch, "E2225", {"start": v(-5.03, 6.2) * mm, "end": v(-5.13, 6.37) * mm});
            skLineSegment(sketch, "E2226", {"start": v(-5.13, 6.37) * mm, "end": v(-5.23, 6.53) * mm});
            skLineSegment(sketch, "E2227", {"start": v(-5.23, 6.53) * mm, "end": v(-5.33, 6.7) * mm});
            skLineSegment(sketch, "E2228", {"start": v(-5.33, 6.7) * mm, "end": v(-5.43, 6.86) * mm});
            skLineSegment(sketch, "E2229", {"start": v(-5.43, 6.86) * mm, "end": v(-5.53, 7.03) * mm});
            skLineSegment(sketch, "E2230", {"start": v(-5.53, 7.03) * mm, "end": v(-5.62, 7.2) * mm});
            skLineSegment(sketch, "E2231", {"start": v(-5.62, 7.2) * mm, "end": v(-5.72, 7.36) * mm});
            skLineSegment(sketch, "E2232", {"start": v(-5.72, 7.36) * mm, "end": v(-5.82, 7.52) * mm});
            skLineSegment(sketch, "E2233", {"start": v(-5.82, 7.52) * mm, "end": v(-5.91, 7.52) * mm});
            skLineSegment(sketch, "E2234", {"start": v(-5.91, 7.52) * mm, "end": v(-6, 7.52) * mm});
            skLineSegment(sketch, "E2235", {"start": v(-6, 7.52) * mm, "end": v(-6.09, 7.52) * mm});
            skLineSegment(sketch, "E2236", {"start": v(-6.09, 7.52) * mm, "end": v(-6.17, 7.52) * mm});
            skLineSegment(sketch, "E2237", {"start": v(-6.17, 7.52) * mm, "end": v(-6.26, 7.52) * mm});
            skLineSegment(sketch, "E2238", {"start": v(-6.26, 7.52) * mm, "end": v(-6.35, 7.52) * mm});
            skLineSegment(sketch, "E2239", {"start": v(-6.35, 7.52) * mm, "end": v(-6.44, 7.52) * mm});
            skLineSegment(sketch, "E2240", {"start": v(-6.44, 7.52) * mm, "end": v(-6.52, 7.52) * mm});
            skLineSegment(sketch, "E2241", {"start": v(-6.52, 7.52) * mm, "end": v(-6.52, 7.36) * mm});
            skLineSegment(sketch, "E2242", {"start": v(-6.52, 7.36) * mm, "end": v(-6.52, 7.2) * mm});
            skLineSegment(sketch, "E2243", {"start": v(-6.52, 7.2) * mm, "end": v(-6.52, 7.03) * mm});
            skLineSegment(sketch, "E2244", {"start": v(-6.52, 7.03) * mm, "end": v(-6.52, 6.86) * mm});
            skLineSegment(sketch, "E2245", {"start": v(-6.52, 6.86) * mm, "end": v(-6.52, 6.7) * mm});
            skLineSegment(sketch, "E2246", {"start": v(-6.52, 6.7) * mm, "end": v(-6.52, 6.53) * mm});
            skLineSegment(sketch, "E2247", {"start": v(-6.52, 6.53) * mm, "end": v(-6.52, 6.37) * mm});
            skLineSegment(sketch, "E2248", {"start": v(-6.52, 6.37) * mm, "end": v(-6.52, 6.2) * mm});
            skLineSegment(sketch, "E2249", {"start": v(-6.52, 6.2) * mm, "end": v(-6.55, 6.2) * mm});
            skLineSegment(sketch, "E2250", {"start": v(-6.55, 6.2) * mm, "end": v(-6.58, 6.2) * mm});
            skLineSegment(sketch, "E2251", {"start": v(-6.58, 6.2) * mm, "end": v(-6.6, 6.2) * mm});
            skLineSegment(sketch, "E2252", {"start": v(-6.6, 6.2) * mm, "end": v(-6.63, 6.2) * mm});
            skLineSegment(sketch, "E2253", {"start": v(-6.63, 6.2) * mm, "end": v(-6.65, 6.2) * mm});
            skLineSegment(sketch, "E2254", {"start": v(-6.65, 6.2) * mm, "end": v(-6.68, 6.2) * mm});
            skLineSegment(sketch, "E2255", {"start": v(-6.68, 6.2) * mm, "end": v(-6.7, 6.2) * mm});
            skLineSegment(sketch, "E2256", {"start": v(-6.7, 6.2) * mm, "end": v(-6.73, 6.2) * mm});
            skLineSegment(sketch, "E2257", {"start": v(-6.73, 6.2) * mm, "end": v(-6.73, 6.55) * mm});
            skLineSegment(sketch, "E2258", {"start": v(-6.73, 6.55) * mm, "end": v(-6.73, 6.9) * mm});
            skLineSegment(sketch, "E2259", {"start": v(-6.73, 6.9) * mm, "end": v(-6.73, 7.24) * mm});
            skLineSegment(sketch, "E2260", {"start": v(-6.73, 7.24) * mm, "end": v(-6.73, 7.6) * mm});
            skLineSegment(sketch, "E2261", {"start": v(-6.73, 7.6) * mm, "end": v(-6.73, 7.94) * mm});
            skLineSegment(sketch, "E2262", {"start": v(-6.73, 7.94) * mm, "end": v(-6.73, 8.28) * mm});
            skLineSegment(sketch, "E2263", {"start": v(-6.73, 8.28) * mm, "end": v(-6.73, 8.63) * mm});
            skLineSegment(sketch, "E2264", {"start": v(-6.73, 8.63) * mm, "end": v(-6.73, 8.98) * mm});
            skLineSegment(sketch, "E2265", {"start": v(-6.73, 8.98) * mm, "end": v(-6.56, 8.98) * mm});
            skLineSegment(sketch, "E2266", {"start": v(-6.56, 8.98) * mm, "end": v(-6.38, 8.98) * mm});
            skLineSegment(sketch, "E2267", {"start": v(-6.38, 8.98) * mm, "end": v(-6.21, 8.98) * mm});
            skLineSegment(sketch, "E2268", {"start": v(-6.21, 8.98) * mm, "end": v(-6.04, 8.98) * mm});
            skLineSegment(sketch, "E2269", {"start": v(-6.04, 8.98) * mm, "end": v(-5.86, 8.98) * mm});
            skLineSegment(sketch, "E2270", {"start": v(-5.86, 8.98) * mm, "end": v(-5.69, 8.98) * mm});
            skLineSegment(sketch, "E2271", {"start": v(-5.69, 8.98) * mm, "end": v(-5.52, 8.98) * mm});
            skLineSegment(sketch, "E2272", {"start": v(-5.52, 8.98) * mm, "end": v(-5.34, 8.98) * mm});
            skLineSegment(sketch, "E2273", {"start": v(-5.34, 8.98) * mm, "end": v(-5.25, 8.97) * mm});
            skLineSegment(sketch, "E2274", {"start": v(-5.25, 8.97) * mm, "end": v(-5.16, 8.94) * mm});
            skLineSegment(sketch, "E2275", {"start": v(-5.16, 8.94) * mm, "end": v(-5.08, 8.9) * mm});
            skLineSegment(sketch, "E2276", {"start": v(-5.08, 8.9) * mm, "end": v(-5.01, 8.84) * mm});
            skLineSegment(sketch, "E2277", {"start": v(-5.01, 8.84) * mm, "end": v(-4.96, 8.77) * mm});
            skLineSegment(sketch, "E2278", {"start": v(-4.96, 8.77) * mm, "end": v(-4.91, 8.7) * mm});
            skLineSegment(sketch, "E2279", {"start": v(-4.91, 8.7) * mm, "end": v(-4.89, 8.6) * mm});
            skLineSegment(sketch, "E2280", {"start": v(-4.89, 8.6) * mm, "end": v(-4.88, 8.52) * mm});
            skLineSegment(sketch, "E2281", {"start": v(-4.88, 8.52) * mm, "end": v(-4.88, 8.45) * mm});
            skLineSegment(sketch, "E2282", {"start": v(-4.88, 8.45) * mm, "end": v(-4.88, 8.38) * mm});
            skLineSegment(sketch, "E2283", {"start": v(-4.88, 8.38) * mm, "end": v(-4.88, 8.32) * mm});
            skLineSegment(sketch, "E2284", {"start": v(-4.88, 8.32) * mm, "end": v(-4.88, 8.25) * mm});
            skLineSegment(sketch, "E2285", {"start": v(-4.88, 8.25) * mm, "end": v(-4.88, 8.18) * mm});
            skLineSegment(sketch, "E2286", {"start": v(-4.88, 8.18) * mm, "end": v(-4.88, 8.12) * mm});
            skLineSegment(sketch, "E2287", {"start": v(-4.88, 8.12) * mm, "end": v(-4.88, 8.05) * mm});
            skLineSegment(sketch, "E2288", {"start": v(-4.88, 8.05) * mm, "end": v(-4.88, 7.98) * mm});
            skLineSegment(sketch, "E2289", {"start": v(-4.88, 7.98) * mm, "end": v(-4.89, 7.89) * mm});
            skLineSegment(sketch, "E2290", {"start": v(-4.89, 7.89) * mm, "end": v(-4.91, 7.8) * mm});
            skLineSegment(sketch, "E2291", {"start": v(-4.91, 7.8) * mm, "end": v(-4.96, 7.72) * mm});
            skLineSegment(sketch, "E2292", {"start": v(-4.96, 7.72) * mm, "end": v(-5.01, 7.66) * mm});
            skLineSegment(sketch, "E2293", {"start": v(-5.01, 7.66) * mm, "end": v(-5.08, 7.6) * mm});
            skLineSegment(sketch, "E2294", {"start": v(-5.08, 7.6) * mm, "end": v(-5.16, 7.56) * mm});
            skLineSegment(sketch, "E2295", {"start": v(-5.16, 7.56) * mm, "end": v(-5.25, 7.53) * mm});
            skLineSegment(sketch, "E2296", {"start": v(-5.25, 7.53) * mm, "end": v(-5.34, 7.52) * mm});
            skLineSegment(sketch, "E2297", {"start": v(-5.34, 7.52) * mm, "end": v(-5.37, 7.52) * mm});
            skLineSegment(sketch, "E2298", {"start": v(-5.37, 7.52) * mm, "end": v(-5.4, 7.52) * mm});
            skLineSegment(sketch, "E2299", {"start": v(-5.4, 7.52) * mm, "end": v(-5.43, 7.52) * mm});
            skLineSegment(sketch, "E2300", {"start": v(-5.43, 7.52) * mm, "end": v(-5.46, 7.52) * mm});
            skLineSegment(sketch, "E2301", {"start": v(-5.46, 7.52) * mm, "end": v(-5.5, 7.52) * mm});
            skLineSegment(sketch, "E2302", {"start": v(-5.5, 7.52) * mm, "end": v(-5.52, 7.52) * mm});
            skLineSegment(sketch, "E2303", {"start": v(-5.52, 7.52) * mm, "end": v(-5.55, 7.52) * mm});
            skLineSegment(sketch, "E2304", {"start": v(-5.55, 7.52) * mm, "end": v(-5.58, 7.52) * mm});
            skLineSegment(sketch, "E2305", {"start": v(-5.58, 7.52) * mm, "end": v(-5.48, 7.36) * mm});
            skLineSegment(sketch, "E2306", {"start": v(-5.48, 7.36) * mm, "end": v(-5.38, 7.2) * mm});
            skLineSegment(sketch, "E2307", {"start": v(-5.38, 7.2) * mm, "end": v(-5.28, 7.03) * mm});
            skLineSegment(sketch, "E2308", {"start": v(-5.28, 7.03) * mm, "end": v(-5.18, 6.86) * mm});
            skLineSegment(sketch, "E2309", {"start": v(-5.18, 6.86) * mm, "end": v(-5.08, 6.7) * mm});
            skLineSegment(sketch, "E2310", {"start": v(-5.08, 6.7) * mm, "end": v(-4.99, 6.53) * mm});
            skLineSegment(sketch, "E2311", {"start": v(-4.99, 6.53) * mm, "end": v(-4.89, 6.37) * mm});
            skLineSegment(sketch, "E2312", {"start": v(-4.89, 6.37) * mm, "end": v(-4.79, 6.2) * mm});
            skLineSegment(sketch, "E2313", {"start": v(-5.37, 7.7) * mm, "end": v(-5.31, 7.71) * mm});
            skLineSegment(sketch, "E2314", {"start": v(-5.31, 7.71) * mm, "end": v(-5.26, 7.73) * mm});
            skLineSegment(sketch, "E2315", {"start": v(-5.26, 7.73) * mm, "end": v(-5.21, 7.75) * mm});
            skLineSegment(sketch, "E2316", {"start": v(-5.21, 7.75) * mm, "end": v(-5.17, 7.79) * mm});
            skLineSegment(sketch, "E2317", {"start": v(-5.17, 7.79) * mm, "end": v(-5.14, 7.83) * mm});
            skLineSegment(sketch, "E2318", {"start": v(-5.14, 7.83) * mm, "end": v(-5.11, 7.87) * mm});
            skLineSegment(sketch, "E2319", {"start": v(-5.11, 7.87) * mm, "end": v(-5.1, 7.93) * mm});
            skLineSegment(sketch, "E2320", {"start": v(-5.1, 7.93) * mm, "end": v(-5.1, 7.98) * mm});
            skLineSegment(sketch, "E2321", {"start": v(-5.1, 7.98) * mm, "end": v(-5.1, 8.05) * mm});
            skLineSegment(sketch, "E2322", {"start": v(-5.1, 8.05) * mm, "end": v(-5.1, 8.12) * mm});
            skLineSegment(sketch, "E2323", {"start": v(-5.1, 8.12) * mm, "end": v(-5.1, 8.18) * mm});
            skLineSegment(sketch, "E2324", {"start": v(-5.1, 8.18) * mm, "end": v(-5.1, 8.25) * mm});
            skLineSegment(sketch, "E2325", {"start": v(-5.1, 8.25) * mm, "end": v(-5.1, 8.32) * mm});
            skLineSegment(sketch, "E2326", {"start": v(-5.1, 8.32) * mm, "end": v(-5.1, 8.38) * mm});
            skLineSegment(sketch, "E2327", {"start": v(-5.1, 8.38) * mm, "end": v(-5.1, 8.45) * mm});
            skLineSegment(sketch, "E2328", {"start": v(-5.1, 8.45) * mm, "end": v(-5.1, 8.52) * mm});
            skLineSegment(sketch, "E2329", {"start": v(-5.1, 8.52) * mm, "end": v(-5.1, 8.57) * mm});
            skLineSegment(sketch, "E2330", {"start": v(-5.1, 8.57) * mm, "end": v(-5.11, 8.62) * mm});
            skLineSegment(sketch, "E2331", {"start": v(-5.11, 8.62) * mm, "end": v(-5.14, 8.67) * mm});
            skLineSegment(sketch, "E2332", {"start": v(-5.14, 8.67) * mm, "end": v(-5.17, 8.71) * mm});
            skLineSegment(sketch, "E2333", {"start": v(-5.17, 8.71) * mm, "end": v(-5.21, 8.75) * mm});
            skLineSegment(sketch, "E2334", {"start": v(-5.21, 8.75) * mm, "end": v(-5.26, 8.77) * mm});
            skLineSegment(sketch, "E2335", {"start": v(-5.26, 8.77) * mm, "end": v(-5.31, 8.79) * mm});
            skLineSegment(sketch, "E2336", {"start": v(-5.31, 8.79) * mm, "end": v(-5.37, 8.8) * mm});
            skLineSegment(sketch, "E2337", {"start": v(-5.37, 8.8) * mm, "end": v(-5.51, 8.8) * mm});
            skLineSegment(sketch, "E2338", {"start": v(-5.51, 8.8) * mm, "end": v(-5.66, 8.8) * mm});
            skLineSegment(sketch, "E2339", {"start": v(-5.66, 8.8) * mm, "end": v(-5.8, 8.8) * mm});
            skLineSegment(sketch, "E2340", {"start": v(-5.8, 8.8) * mm, "end": v(-5.95, 8.8) * mm});
            skLineSegment(sketch, "E2341", {"start": v(-5.95, 8.8) * mm, "end": v(-6.1, 8.8) * mm});
            skLineSegment(sketch, "E2342", {"start": v(-6.1, 8.8) * mm, "end": v(-6.24, 8.8) * mm});
            skLineSegment(sketch, "E2343", {"start": v(-6.24, 8.8) * mm, "end": v(-6.38, 8.8) * mm});
            skLineSegment(sketch, "E2344", {"start": v(-6.38, 8.8) * mm, "end": v(-6.52, 8.8) * mm});
            skLineSegment(sketch, "E2345", {"start": v(-6.52, 8.8) * mm, "end": v(-6.52, 8.66) * mm});
            skLineSegment(sketch, "E2346", {"start": v(-6.52, 8.66) * mm, "end": v(-6.52, 8.52) * mm});
            skLineSegment(sketch, "E2347", {"start": v(-6.52, 8.52) * mm, "end": v(-6.52, 8.39) * mm});
            skLineSegment(sketch, "E2348", {"start": v(-6.52, 8.39) * mm, "end": v(-6.52, 8.25) * mm});
            skLineSegment(sketch, "E2349", {"start": v(-6.52, 8.25) * mm, "end": v(-6.52, 8.11) * mm});
            skLineSegment(sketch, "E2350", {"start": v(-6.52, 8.11) * mm, "end": v(-6.52, 7.98) * mm});
            skLineSegment(sketch, "E2351", {"start": v(-6.52, 7.98) * mm, "end": v(-6.52, 7.84) * mm});
            skLineSegment(sketch, "E2352", {"start": v(-6.52, 7.84) * mm, "end": v(-6.52, 7.7) * mm});
            skLineSegment(sketch, "E2353", {"start": v(-6.52, 7.7) * mm, "end": v(-6.38, 7.7) * mm});
            skLineSegment(sketch, "E2354", {"start": v(-6.38, 7.7) * mm, "end": v(-6.24, 7.7) * mm});
            skLineSegment(sketch, "E2355", {"start": v(-6.24, 7.7) * mm, "end": v(-6.1, 7.7) * mm});
            skLineSegment(sketch, "E2356", {"start": v(-6.1, 7.7) * mm, "end": v(-5.95, 7.7) * mm});
            skLineSegment(sketch, "E2357", {"start": v(-5.95, 7.7) * mm, "end": v(-5.8, 7.7) * mm});
            skLineSegment(sketch, "E2358", {"start": v(-5.8, 7.7) * mm, "end": v(-5.66, 7.7) * mm});
            skLineSegment(sketch, "E2359", {"start": v(-5.66, 7.7) * mm, "end": v(-5.51, 7.7) * mm});
            skLineSegment(sketch, "E2360", {"start": v(-5.51, 7.7) * mm, "end": v(-5.37, 7.7) * mm});
            skLineSegment(sketch, "E2361", {"start": v(-4.1, 7.75) * mm, "end": v(-3.93, 7.75) * mm});
            skLineSegment(sketch, "E2362", {"start": v(-3.93, 7.75) * mm, "end": v(-3.77, 7.75) * mm});
            skLineSegment(sketch, "E2363", {"start": v(-3.77, 7.75) * mm, "end": v(-3.61, 7.75) * mm});
            skLineSegment(sketch, "E2364", {"start": v(-3.61, 7.75) * mm, "end": v(-3.45, 7.75) * mm});
            skLineSegment(sketch, "E2365", {"start": v(-3.45, 7.75) * mm, "end": v(-3.3, 7.75) * mm});
            skLineSegment(sketch, "E2366", {"start": v(-3.3, 7.75) * mm, "end": v(-3.14, 7.75) * mm});
            skLineSegment(sketch, "E2367", {"start": v(-3.14, 7.75) * mm, "end": v(-2.98, 7.75) * mm});
            skLineSegment(sketch, "E2368", {"start": v(-2.98, 7.75) * mm, "end": v(-2.82, 7.75) * mm});
            skLineSegment(sketch, "E2369", {"start": v(-2.82, 7.75) * mm, "end": v(-2.82, 7.72) * mm});
            skLineSegment(sketch, "E2370", {"start": v(-2.82, 7.72) * mm, "end": v(-2.82, 7.7) * mm});
            skLineSegment(sketch, "E2371", {"start": v(-2.82, 7.7) * mm, "end": v(-2.82, 7.68) * mm});
            skLineSegment(sketch, "E2372", {"start": v(-2.82, 7.68) * mm, "end": v(-2.82, 7.66) * mm});
            skLineSegment(sketch, "E2373", {"start": v(-2.82, 7.66) * mm, "end": v(-2.82, 7.63) * mm});
            skLineSegment(sketch, "E2374", {"start": v(-2.82, 7.63) * mm, "end": v(-2.82, 7.6) * mm});
            skLineSegment(sketch, "E2375", {"start": v(-2.82, 7.6) * mm, "end": v(-2.82, 7.59) * mm});
            skLineSegment(sketch, "E2376", {"start": v(-2.82, 7.59) * mm, "end": v(-2.82, 7.56) * mm});
            skLineSegment(sketch, "E2377", {"start": v(-2.82, 7.56) * mm, "end": v(-2.98, 7.56) * mm});
            skLineSegment(sketch, "E2378", {"start": v(-2.98, 7.56) * mm, "end": v(-3.14, 7.56) * mm});
            skLineSegment(sketch, "E2379", {"start": v(-3.14, 7.56) * mm, "end": v(-3.3, 7.56) * mm});
            skLineSegment(sketch, "E2380", {"start": v(-3.3, 7.56) * mm, "end": v(-3.45, 7.56) * mm});
            skLineSegment(sketch, "E2381", {"start": v(-3.45, 7.56) * mm, "end": v(-3.61, 7.56) * mm});
            skLineSegment(sketch, "E2382", {"start": v(-3.61, 7.56) * mm, "end": v(-3.77, 7.56) * mm});
            skLineSegment(sketch, "E2383", {"start": v(-3.77, 7.56) * mm, "end": v(-3.93, 7.56) * mm});
            skLineSegment(sketch, "E2384", {"start": v(-3.93, 7.56) * mm, "end": v(-4.1, 7.56) * mm});
            skLineSegment(sketch, "E2385", {"start": v(-4.1, 7.56) * mm, "end": v(-4.1, 7.42) * mm});
            skLineSegment(sketch, "E2386", {"start": v(-4.1, 7.42) * mm, "end": v(-4.1, 7.27) * mm});
            skLineSegment(sketch, "E2387", {"start": v(-4.1, 7.27) * mm, "end": v(-4.1, 7.12) * mm});
            skLineSegment(sketch, "E2388", {"start": v(-4.1, 7.12) * mm, "end": v(-4.1, 6.98) * mm});
            skLineSegment(sketch, "E2389", {"start": v(-4.1, 6.98) * mm, "end": v(-4.1, 6.83) * mm});
            skLineSegment(sketch, "E2390", {"start": v(-4.1, 6.83) * mm, "end": v(-4.1, 6.68) * mm});
            skLineSegment(sketch, "E2391", {"start": v(-4.1, 6.68) * mm, "end": v(-4.1, 6.53) * mm});
            skLineSegment(sketch, "E2392", {"start": v(-4.1, 6.53) * mm, "end": v(-4.1, 6.39) * mm});
            skLineSegment(sketch, "E2393", {"start": v(-4.1, 6.39) * mm, "end": v(-3.9, 6.39) * mm});
            skLineSegment(sketch, "E2394", {"start": v(-3.9, 6.39) * mm, "end": v(-3.7, 6.39) * mm});
            skLineSegment(sketch, "E2395", {"start": v(-3.7, 6.39) * mm, "end": v(-3.5, 6.39) * mm});
            skLineSegment(sketch, "E2396", {"start": v(-3.5, 6.39) * mm, "end": v(-3.32, 6.39) * mm});
            skLineSegment(sketch, "E2397", {"start": v(-3.32, 6.39) * mm, "end": v(-3.12, 6.39) * mm});
            skLineSegment(sketch, "E2398", {"start": v(-3.12, 6.39) * mm, "end": v(-2.93, 6.39) * mm});
            skLineSegment(sketch, "E2399", {"start": v(-2.93, 6.39) * mm, "end": v(-2.73, 6.39) * mm});
            skLineSegment(sketch, "E2400", {"start": v(-2.73, 6.39) * mm, "end": v(-2.54, 6.39) * mm});
            skLineSegment(sketch, "E2401", {"start": v(-2.54, 6.39) * mm, "end": v(-2.54, 6.36) * mm});
            skLineSegment(sketch, "E2402", {"start": v(-2.54, 6.36) * mm, "end": v(-2.54, 6.34) * mm});
            skLineSegment(sketch, "E2403", {"start": v(-2.54, 6.34) * mm, "end": v(-2.54, 6.32) * mm});
            skLineSegment(sketch, "E2404", {"start": v(-2.54, 6.32) * mm, "end": v(-2.54, 6.3) * mm});
            skLineSegment(sketch, "E2405", {"start": v(-2.54, 6.3) * mm, "end": v(-2.54, 6.27) * mm});
            skLineSegment(sketch, "E2406", {"start": v(-2.54, 6.27) * mm, "end": v(-2.54, 6.25) * mm});
            skLineSegment(sketch, "E2407", {"start": v(-2.54, 6.25) * mm, "end": v(-2.54, 6.23) * mm});
            skLineSegment(sketch, "E2408", {"start": v(-2.54, 6.23) * mm, "end": v(-2.54, 6.2) * mm});
            skLineSegment(sketch, "E2409", {"start": v(-2.54, 6.2) * mm, "end": v(-2.76, 6.2) * mm});
            skLineSegment(sketch, "E2410", {"start": v(-2.76, 6.2) * mm, "end": v(-2.98, 6.2) * mm});
            skLineSegment(sketch, "E2411", {"start": v(-2.98, 6.2) * mm, "end": v(-3.2, 6.2) * mm});
            skLineSegment(sketch, "E2412", {"start": v(-3.2, 6.2) * mm, "end": v(-3.42, 6.2) * mm});
            skLineSegment(sketch, "E2413", {"start": v(-3.42, 6.2) * mm, "end": v(-3.64, 6.2) * mm});
            skLineSegment(sketch, "E2414", {"start": v(-3.64, 6.2) * mm, "end": v(-3.86, 6.2) * mm});
            skLineSegment(sketch, "E2415", {"start": v(-3.86, 6.2) * mm, "end": v(-4.08, 6.2) * mm});
            skLineSegment(sketch, "E2416", {"start": v(-4.08, 6.2) * mm, "end": v(-4.3, 6.2) * mm});
            skLineSegment(sketch, "E2417", {"start": v(-4.3, 6.2) * mm, "end": v(-4.3, 6.55) * mm});
            skLineSegment(sketch, "E2418", {"start": v(-4.3, 6.55) * mm, "end": v(-4.3, 6.9) * mm});
            skLineSegment(sketch, "E2419", {"start": v(-4.3, 6.9) * mm, "end": v(-4.3, 7.25) * mm});
            skLineSegment(sketch, "E2420", {"start": v(-4.3, 7.25) * mm, "end": v(-4.3, 7.6) * mm});
            skLineSegment(sketch, "E2421", {"start": v(-4.3, 7.6) * mm, "end": v(-4.3, 7.94) * mm});
            skLineSegment(sketch, "E2422", {"start": v(-4.3, 7.94) * mm, "end": v(-4.3, 8.29) * mm});
            skLineSegment(sketch, "E2423", {"start": v(-4.3, 8.29) * mm, "end": v(-4.3, 8.63) * mm});
            skLineSegment(sketch, "E2424", {"start": v(-4.3, 8.63) * mm, "end": v(-4.3, 8.98) * mm});
            skLineSegment(sketch, "E2425", {"start": v(-4.3, 8.98) * mm, "end": v(-4.08, 8.98) * mm});
            skLineSegment(sketch, "E2426", {"start": v(-4.08, 8.98) * mm, "end": v(-3.86, 8.98) * mm});
            skLineSegment(sketch, "E2427", {"start": v(-3.86, 8.98) * mm, "end": v(-3.64, 8.98) * mm});
            skLineSegment(sketch, "E2428", {"start": v(-3.64, 8.98) * mm, "end": v(-3.42, 8.98) * mm});
            skLineSegment(sketch, "E2429", {"start": v(-3.42, 8.98) * mm, "end": v(-3.2, 8.98) * mm});
            skLineSegment(sketch, "E2430", {"start": v(-3.2, 8.98) * mm, "end": v(-2.98, 8.98) * mm});
            skLineSegment(sketch, "E2431", {"start": v(-2.98, 8.98) * mm, "end": v(-2.76, 8.98) * mm});
            skLineSegment(sketch, "E2432", {"start": v(-2.76, 8.98) * mm, "end": v(-2.54, 8.98) * mm});
            skLineSegment(sketch, "E2433", {"start": v(-2.54, 8.98) * mm, "end": v(-2.54, 8.96) * mm});
            skLineSegment(sketch, "E2434", {"start": v(-2.54, 8.96) * mm, "end": v(-2.54, 8.93) * mm});
            skLineSegment(sketch, "E2435", {"start": v(-2.54, 8.93) * mm, "end": v(-2.54, 8.91) * mm});
            skLineSegment(sketch, "E2436", {"start": v(-2.54, 8.91) * mm, "end": v(-2.54, 8.89) * mm});
            skLineSegment(sketch, "E2437", {"start": v(-2.54, 8.89) * mm, "end": v(-2.54, 8.86) * mm});
            skLineSegment(sketch, "E2438", {"start": v(-2.54, 8.86) * mm, "end": v(-2.54, 8.84) * mm});
            skLineSegment(sketch, "E2439", {"start": v(-2.54, 8.84) * mm, "end": v(-2.54, 8.82) * mm});
            skLineSegment(sketch, "E2440", {"start": v(-2.54, 8.82) * mm, "end": v(-2.54, 8.8) * mm});
            skLineSegment(sketch, "E2441", {"start": v(-2.54, 8.8) * mm, "end": v(-2.73, 8.8) * mm});
            skLineSegment(sketch, "E2442", {"start": v(-2.73, 8.8) * mm, "end": v(-2.93, 8.8) * mm});
            skLineSegment(sketch, "E2443", {"start": v(-2.93, 8.8) * mm, "end": v(-3.12, 8.8) * mm});
            skLineSegment(sketch, "E2444", {"start": v(-3.12, 8.8) * mm, "end": v(-3.32, 8.8) * mm});
            skLineSegment(sketch, "E2445", {"start": v(-3.32, 8.8) * mm, "end": v(-3.5, 8.8) * mm});
            skLineSegment(sketch, "E2446", {"start": v(-3.5, 8.8) * mm, "end": v(-3.7, 8.8) * mm});
            skLineSegment(sketch, "E2447", {"start": v(-3.7, 8.8) * mm, "end": v(-3.9, 8.8) * mm});
            skLineSegment(sketch, "E2448", {"start": v(-3.9, 8.8) * mm, "end": v(-4.1, 8.8) * mm});
            skLineSegment(sketch, "E2449", {"start": v(-4.1, 8.8) * mm, "end": v(-4.1, 8.66) * mm});
            skLineSegment(sketch, "E2450", {"start": v(-4.1, 8.66) * mm, "end": v(-4.1, 8.53) * mm});
            skLineSegment(sketch, "E2451", {"start": v(-4.1, 8.53) * mm, "end": v(-4.1, 8.4) * mm});
            skLineSegment(sketch, "E2452", {"start": v(-4.1, 8.4) * mm, "end": v(-4.1, 8.27) * mm});
            skLineSegment(sketch, "E2453", {"start": v(-4.1, 8.27) * mm, "end": v(-4.1, 8.14) * mm});
            skLineSegment(sketch, "E2454", {"start": v(-4.1, 8.14) * mm, "end": v(-4.1, 8) * mm});
            skLineSegment(sketch, "E2455", {"start": v(-4.1, 8) * mm, "end": v(-4.1, 7.88) * mm});
            skLineSegment(sketch, "E2456", {"start": v(-4.1, 7.88) * mm, "end": v(-4.1, 7.75) * mm});
            skLineSegment(sketch, "E2457", {"start": v(-1.69, 7.55) * mm, "end": v(-1.78, 7.56) * mm});
            skLineSegment(sketch, "E2458", {"start": v(-1.78, 7.56) * mm, "end": v(-1.87, 7.59) * mm});
            skLineSegment(sketch, "E2459", {"start": v(-1.87, 7.59) * mm, "end": v(-1.95, 7.63) * mm});
            skLineSegment(sketch, "E2460", {"start": v(-1.95, 7.63) * mm, "end": v(-2.02, 7.69) * mm});
            skLineSegment(sketch, "E2461", {"start": v(-2.02, 7.69) * mm, "end": v(-2.07, 7.75) * mm});
            skLineSegment(sketch, "E2462", {"start": v(-2.07, 7.75) * mm, "end": v(-2.12, 7.83) * mm});
            skLineSegment(sketch, "E2463", {"start": v(-2.12, 7.83) * mm, "end": v(-2.14, 7.92) * mm});
            skLineSegment(sketch, "E2464", {"start": v(-2.14, 7.92) * mm, "end": v(-2.15, 8.01) * mm});
            skLineSegment(sketch, "E2465", {"start": v(-2.15, 8.01) * mm, "end": v(-2.15, 8.08) * mm});
            skLineSegment(sketch, "E2466", {"start": v(-2.15, 8.08) * mm, "end": v(-2.15, 8.14) * mm});
            skLineSegment(sketch, "E2467", {"start": v(-2.15, 8.14) * mm, "end": v(-2.15, 8.2) * mm});
            skLineSegment(sketch, "E2468", {"start": v(-2.15, 8.2) * mm, "end": v(-2.15, 8.26) * mm});
            skLineSegment(sketch, "E2469", {"start": v(-2.15, 8.26) * mm, "end": v(-2.15, 8.33) * mm});
            skLineSegment(sketch, "E2470", {"start": v(-2.15, 8.33) * mm, "end": v(-2.15, 8.4) * mm});
            skLineSegment(sketch, "E2471", {"start": v(-2.15, 8.4) * mm, "end": v(-2.15, 8.45) * mm});
            skLineSegment(sketch, "E2472", {"start": v(-2.15, 8.45) * mm, "end": v(-2.15, 8.52) * mm});
            skLineSegment(sketch, "E2473", {"start": v(-2.15, 8.52) * mm, "end": v(-2.14, 8.6) * mm});
            skLineSegment(sketch, "E2474", {"start": v(-2.14, 8.6) * mm, "end": v(-2.12, 8.7) * mm});
            skLineSegment(sketch, "E2475", {"start": v(-2.12, 8.7) * mm, "end": v(-2.07, 8.77) * mm});
            skLineSegment(sketch, "E2476", {"start": v(-2.07, 8.77) * mm, "end": v(-2.02, 8.84) * mm});
            skLineSegment(sketch, "E2477", {"start": v(-2.02, 8.84) * mm, "end": v(-1.95, 8.9) * mm});
            skLineSegment(sketch, "E2478", {"start": v(-1.95, 8.9) * mm, "end": v(-1.87, 8.94) * mm});
            skLineSegment(sketch, "E2479", {"start": v(-1.87, 8.94) * mm, "end": v(-1.78, 8.97) * mm});
            skLineSegment(sketch, "E2480", {"start": v(-1.78, 8.97) * mm, "end": v(-1.69, 8.98) * mm});
            skLineSegment(sketch, "E2481", {"start": v(-1.69, 8.98) * mm, "end": v(-1.54, 8.98) * mm});
            skLineSegment(sketch, "E2482", {"start": v(-1.54, 8.98) * mm, "end": v(-1.4, 8.98) * mm});
            skLineSegment(sketch, "E2483", {"start": v(-1.4, 8.98) * mm, "end": v(-1.25, 8.98) * mm});
            skLineSegment(sketch, "E2484", {"start": v(-1.25, 8.98) * mm, "end": v(-1.1, 8.98) * mm});
            skLineSegment(sketch, "E2485", {"start": v(-1.1, 8.98) * mm, "end": v(-0.96, 8.98) * mm});
            skLineSegment(sketch, "E2486", {"start": v(-0.96, 8.98) * mm, "end": v(-0.82, 8.98) * mm});
            skLineSegment(sketch, "E2487", {"start": v(-0.82, 8.98) * mm, "end": v(-0.67, 8.98) * mm});
            skLineSegment(sketch, "E2488", {"start": v(-0.67, 8.98) * mm, "end": v(-0.53, 8.98) * mm});
            skLineSegment(sketch, "E2489", {"start": v(-0.53, 8.98) * mm, "end": v(-0.53, 8.95) * mm});
            skLineSegment(sketch, "E2490", {"start": v(-0.53, 8.95) * mm, "end": v(-0.53, 8.93) * mm});
            skLineSegment(sketch, "E2491", {"start": v(-0.53, 8.93) * mm, "end": v(-0.53, 8.9) * mm});
            skLineSegment(sketch, "E2492", {"start": v(-0.53, 8.9) * mm, "end": v(-0.53, 8.89) * mm});
            skLineSegment(sketch, "E2493", {"start": v(-0.53, 8.89) * mm, "end": v(-0.53, 8.86) * mm});
            skLineSegment(sketch, "E2494", {"start": v(-0.53, 8.86) * mm, "end": v(-0.53, 8.84) * mm});
            skLineSegment(sketch, "E2495", {"start": v(-0.53, 8.84) * mm, "end": v(-0.53, 8.82) * mm});
            skLineSegment(sketch, "E2496", {"start": v(-0.53, 8.82) * mm, "end": v(-0.53, 8.8) * mm});
            skLineSegment(sketch, "E2497", {"start": v(-0.53, 8.8) * mm, "end": v(-0.67, 8.8) * mm});
            skLineSegment(sketch, "E2498", {"start": v(-0.67, 8.8) * mm, "end": v(-0.82, 8.8) * mm});
            skLineSegment(sketch, "E2499", {"start": v(-0.82, 8.8) * mm, "end": v(-0.96, 8.8) * mm});
            skLineSegment(sketch, "E2500", {"start": v(-0.96, 8.8) * mm, "end": v(-1.1, 8.8) * mm});
            skLineSegment(sketch, "E2501", {"start": v(-1.1, 8.8) * mm, "end": v(-1.25, 8.8) * mm});
            skLineSegment(sketch, "E2502", {"start": v(-1.25, 8.8) * mm, "end": v(-1.4, 8.8) * mm});
            skLineSegment(sketch, "E2503", {"start": v(-1.4, 8.8) * mm, "end": v(-1.54, 8.8) * mm});
            skLineSegment(sketch, "E2504", {"start": v(-1.54, 8.8) * mm, "end": v(-1.68, 8.8) * mm});
            skLineSegment(sketch, "E2505", {"start": v(-1.68, 8.8) * mm, "end": v(-1.74, 8.79) * mm});
            skLineSegment(sketch, "E2506", {"start": v(-1.74, 8.79) * mm, "end": v(-1.8, 8.77) * mm});
            skLineSegment(sketch, "E2507", {"start": v(-1.8, 8.77) * mm, "end": v(-1.84, 8.75) * mm});
            skLineSegment(sketch, "E2508", {"start": v(-1.84, 8.75) * mm, "end": v(-1.88, 8.71) * mm});
            skLineSegment(sketch, "E2509", {"start": v(-1.88, 8.71) * mm, "end": v(-1.91, 8.67) * mm});
            skLineSegment(sketch, "E2510", {"start": v(-1.91, 8.67) * mm, "end": v(-1.94, 8.62) * mm});
            skLineSegment(sketch, "E2511", {"start": v(-1.94, 8.62) * mm, "end": v(-1.96, 8.57) * mm});
            skLineSegment(sketch, "E2512", {"start": v(-1.96, 8.57) * mm, "end": v(-1.96, 8.52) * mm});
            skLineSegment(sketch, "E2513", {"start": v(-1.96, 8.52) * mm, "end": v(-1.96, 8.46) * mm});
            skLineSegment(sketch, "E2514", {"start": v(-1.96, 8.46) * mm, "end": v(-1.96, 8.4) * mm});
            skLineSegment(sketch, "E2515", {"start": v(-1.96, 8.4) * mm, "end": v(-1.96, 8.33) * mm});
            skLineSegment(sketch, "E2516", {"start": v(-1.96, 8.33) * mm, "end": v(-1.96, 8.27) * mm});
            skLineSegment(sketch, "E2517", {"start": v(-1.96, 8.27) * mm, "end": v(-1.96, 8.21) * mm});
            skLineSegment(sketch, "E2518", {"start": v(-1.96, 8.21) * mm, "end": v(-1.96, 8.15) * mm});
            skLineSegment(sketch, "E2519", {"start": v(-1.96, 8.15) * mm, "end": v(-1.96, 8.09) * mm});
            skLineSegment(sketch, "E2520", {"start": v(-1.96, 8.09) * mm, "end": v(-1.96, 8.03) * mm});
            skLineSegment(sketch, "E2521", {"start": v(-1.96, 8.03) * mm, "end": v(-1.96, 7.97) * mm});
            skLineSegment(sketch, "E2522", {"start": v(-1.96, 7.97) * mm, "end": v(-1.94, 7.92) * mm});
            skLineSegment(sketch, "E2523", {"start": v(-1.94, 7.92) * mm, "end": v(-1.91, 7.87) * mm});
            skLineSegment(sketch, "E2524", {"start": v(-1.91, 7.87) * mm, "end": v(-1.88, 7.83) * mm});
            skLineSegment(sketch, "E2525", {"start": v(-1.88, 7.83) * mm, "end": v(-1.84, 7.8) * mm});
            skLineSegment(sketch, "E2526", {"start": v(-1.84, 7.8) * mm, "end": v(-1.8, 7.77) * mm});
            skLineSegment(sketch, "E2527", {"start": v(-1.8, 7.77) * mm, "end": v(-1.74, 7.76) * mm});
            skLineSegment(sketch, "E2528", {"start": v(-1.74, 7.76) * mm, "end": v(-1.68, 7.75) * mm});
            skLineSegment(sketch, "E2529", {"start": v(-1.68, 7.75) * mm, "end": v(-1.57, 7.75) * mm});
            skLineSegment(sketch, "E2530", {"start": v(-1.57, 7.75) * mm, "end": v(-1.46, 7.75) * mm});
            skLineSegment(sketch, "E2531", {"start": v(-1.46, 7.75) * mm, "end": v(-1.35, 7.75) * mm});
            skLineSegment(sketch, "E2532", {"start": v(-1.35, 7.75) * mm, "end": v(-1.24, 7.75) * mm});
            skLineSegment(sketch, "E2533", {"start": v(-1.24, 7.75) * mm, "end": v(-1.13, 7.75) * mm});
            skLineSegment(sketch, "E2534", {"start": v(-1.13, 7.75) * mm, "end": v(-1.02, 7.75) * mm});
            skLineSegment(sketch, "E2535", {"start": v(-1.02, 7.75) * mm, "end": v(-0.91, 7.75) * mm});
            skLineSegment(sketch, "E2536", {"start": v(-0.91, 7.75) * mm, "end": v(-0.8, 7.75) * mm});
            skLineSegment(sketch, "E2537", {"start": v(-0.8, 7.75) * mm, "end": v(-0.71, 7.74) * mm});
            skLineSegment(sketch, "E2538", {"start": v(-0.71, 7.74) * mm, "end": v(-0.62, 7.71) * mm});
            skLineSegment(sketch, "E2539", {"start": v(-0.62, 7.71) * mm, "end": v(-0.55, 7.67) * mm});
            skLineSegment(sketch, "E2540", {"start": v(-0.55, 7.67) * mm, "end": v(-0.48, 7.62) * mm});
            skLineSegment(sketch, "E2541", {"start": v(-0.48, 7.62) * mm, "end": v(-0.42, 7.55) * mm});
            skLineSegment(sketch, "E2542", {"start": v(-0.42, 7.55) * mm, "end": v(-0.38, 7.47) * mm});
            skLineSegment(sketch, "E2543", {"start": v(-0.38, 7.47) * mm, "end": v(-0.35, 7.38) * mm});
            skLineSegment(sketch, "E2544", {"start": v(-0.35, 7.38) * mm, "end": v(-0.34, 7.29) * mm});
            skLineSegment(sketch, "E2545", {"start": v(-0.34, 7.29) * mm, "end": v(-0.34, 7.2) * mm});
            skLineSegment(sketch, "E2546", {"start": v(-0.34, 7.2) * mm, "end": v(-0.34, 7.13) * mm});
            skLineSegment(sketch, "E2547", {"start": v(-0.34, 7.13) * mm, "end": v(-0.34, 7.05) * mm});
            skLineSegment(sketch, "E2548", {"start": v(-0.34, 7.05) * mm, "end": v(-0.34, 6.97) * mm});
            skLineSegment(sketch, "E2549", {"start": v(-0.34, 6.97) * mm, "end": v(-0.34, 6.9) * mm});
            skLineSegment(sketch, "E2550", {"start": v(-0.34, 6.9) * mm, "end": v(-0.34, 6.82) * mm});
            skLineSegment(sketch, "E2551", {"start": v(-0.34, 6.82) * mm, "end": v(-0.34, 6.74) * mm});
            skLineSegment(sketch, "E2552", {"start": v(-0.34, 6.74) * mm, "end": v(-0.34, 6.66) * mm});
            skLineSegment(sketch, "E2553", {"start": v(-0.34, 6.66) * mm, "end": v(-0.35, 6.57) * mm});
            skLineSegment(sketch, "E2554", {"start": v(-0.35, 6.57) * mm, "end": v(-0.38, 6.48) * mm});
            skLineSegment(sketch, "E2555", {"start": v(-0.38, 6.48) * mm, "end": v(-0.42, 6.4) * mm});
            skLineSegment(sketch, "E2556", {"start": v(-0.42, 6.4) * mm, "end": v(-0.48, 6.34) * mm});
            skLineSegment(sketch, "E2557", {"start": v(-0.48, 6.34) * mm, "end": v(-0.55, 6.28) * mm});
            skLineSegment(sketch, "E2558", {"start": v(-0.55, 6.28) * mm, "end": v(-0.62, 6.24) * mm});
            skLineSegment(sketch, "E2559", {"start": v(-0.62, 6.24) * mm, "end": v(-0.71, 6.21) * mm});
            skLineSegment(sketch, "E2560", {"start": v(-0.71, 6.21) * mm, "end": v(-0.8, 6.2) * mm});
            skLineSegment(sketch, "E2561", {"start": v(-0.8, 6.2) * mm, "end": v(-0.98, 6.2) * mm});
            skLineSegment(sketch, "E2562", {"start": v(-0.98, 6.2) * mm, "end": v(-1.15, 6.2) * mm});
            skLineSegment(sketch, "E2563", {"start": v(-1.15, 6.2) * mm, "end": v(-1.32, 6.2) * mm});
            skLineSegment(sketch, "E2564", {"start": v(-1.32, 6.2) * mm, "end": v(-1.5, 6.2) * mm});
            skLineSegment(sketch, "E2565", {"start": v(-1.5, 6.2) * mm, "end": v(-1.67, 6.2) * mm});
            skLineSegment(sketch, "E2566", {"start": v(-1.67, 6.2) * mm, "end": v(-1.85, 6.2) * mm});
            skLineSegment(sketch, "E2567", {"start": v(-1.85, 6.2) * mm, "end": v(-2.02, 6.2) * mm});
            skLineSegment(sketch, "E2568", {"start": v(-2.02, 6.2) * mm, "end": v(-2.2, 6.2) * mm});
            skLineSegment(sketch, "E2569", {"start": v(-2.2, 6.2) * mm, "end": v(-2.2, 6.23) * mm});
            skLineSegment(sketch, "E2570", {"start": v(-2.2, 6.23) * mm, "end": v(-2.2, 6.25) * mm});
            skLineSegment(sketch, "E2571", {"start": v(-2.2, 6.25) * mm, "end": v(-2.2, 6.27) * mm});
            skLineSegment(sketch, "E2572", {"start": v(-2.2, 6.27) * mm, "end": v(-2.2, 6.3) * mm});
            skLineSegment(sketch, "E2573", {"start": v(-2.2, 6.3) * mm, "end": v(-2.2, 6.32) * mm});
            skLineSegment(sketch, "E2574", {"start": v(-2.2, 6.32) * mm, "end": v(-2.2, 6.34) * mm});
            skLineSegment(sketch, "E2575", {"start": v(-2.2, 6.34) * mm, "end": v(-2.2, 6.36) * mm});
            skLineSegment(sketch, "E2576", {"start": v(-2.2, 6.36) * mm, "end": v(-2.2, 6.39) * mm});
            skLineSegment(sketch, "E2577", {"start": v(-2.2, 6.39) * mm, "end": v(-2.02, 6.39) * mm});
            skLineSegment(sketch, "E2578", {"start": v(-2.02, 6.39) * mm, "end": v(-1.85, 6.39) * mm});
            skLineSegment(sketch, "E2579", {"start": v(-1.85, 6.39) * mm, "end": v(-1.67, 6.39) * mm});
            skLineSegment(sketch, "E2580", {"start": v(-1.67, 6.39) * mm, "end": v(-1.5, 6.39) * mm});
            skLineSegment(sketch, "E2581", {"start": v(-1.5, 6.39) * mm, "end": v(-1.33, 6.39) * mm});
            skLineSegment(sketch, "E2582", {"start": v(-1.33, 6.39) * mm, "end": v(-1.16, 6.39) * mm});
            skLineSegment(sketch, "E2583", {"start": v(-1.16, 6.39) * mm, "end": v(-0.98, 6.39) * mm});
            skLineSegment(sketch, "E2584", {"start": v(-0.98, 6.39) * mm, "end": v(-0.81, 6.39) * mm});
            skLineSegment(sketch, "E2585", {"start": v(-0.81, 6.39) * mm, "end": v(-0.76, 6.4) * mm});
            skLineSegment(sketch, "E2586", {"start": v(-0.76, 6.4) * mm, "end": v(-0.7, 6.4) * mm});
            skLineSegment(sketch, "E2587", {"start": v(-0.7, 6.4) * mm, "end": v(-0.66, 6.43) * mm});
            skLineSegment(sketch, "E2588", {"start": v(-0.66, 6.43) * mm, "end": v(-0.62, 6.47) * mm});
            skLineSegment(sketch, "E2589", {"start": v(-0.62, 6.47) * mm, "end": v(-0.58, 6.5) * mm});
            skLineSegment(sketch, "E2590", {"start": v(-0.58, 6.5) * mm, "end": v(-0.56, 6.56) * mm});
            skLineSegment(sketch, "E2591", {"start": v(-0.56, 6.56) * mm, "end": v(-0.54, 6.6) * mm});
            skLineSegment(sketch, "E2592", {"start": v(-0.54, 6.6) * mm, "end": v(-0.53, 6.66) * mm});
            skLineSegment(sketch, "E2593", {"start": v(-0.53, 6.66) * mm, "end": v(-0.53, 6.74) * mm});
            skLineSegment(sketch, "E2594", {"start": v(-0.53, 6.74) * mm, "end": v(-0.53, 6.81) * mm});
            skLineSegment(sketch, "E2595", {"start": v(-0.53, 6.81) * mm, "end": v(-0.53, 6.9) * mm});
            skLineSegment(sketch, "E2596", {"start": v(-0.53, 6.9) * mm, "end": v(-0.53, 6.97) * mm});
            skLineSegment(sketch, "E2597", {"start": v(-0.53, 6.97) * mm, "end": v(-0.53, 7.04) * mm});
            skLineSegment(sketch, "E2598", {"start": v(-0.53, 7.04) * mm, "end": v(-0.53, 7.12) * mm});
            skLineSegment(sketch, "E2599", {"start": v(-0.53, 7.12) * mm, "end": v(-0.53, 7.2) * mm});
            skLineSegment(sketch, "E2600", {"start": v(-0.53, 7.2) * mm, "end": v(-0.53, 7.27) * mm});
            skLineSegment(sketch, "E2601", {"start": v(-0.53, 7.27) * mm, "end": v(-0.54, 7.33) * mm});
            skLineSegment(sketch, "E2602", {"start": v(-0.54, 7.33) * mm, "end": v(-0.56, 7.38) * mm});
            skLineSegment(sketch, "E2603", {"start": v(-0.56, 7.38) * mm, "end": v(-0.58, 7.43) * mm});
            skLineSegment(sketch, "E2604", {"start": v(-0.58, 7.43) * mm, "end": v(-0.62, 7.47) * mm});
            skLineSegment(sketch, "E2605", {"start": v(-0.62, 7.47) * mm, "end": v(-0.66, 7.5) * mm});
            skLineSegment(sketch, "E2606", {"start": v(-0.66, 7.5) * mm, "end": v(-0.7, 7.53) * mm});
            skLineSegment(sketch, "E2607", {"start": v(-0.7, 7.53) * mm, "end": v(-0.76, 7.55) * mm});
            skLineSegment(sketch, "E2608", {"start": v(-0.76, 7.55) * mm, "end": v(-0.81, 7.55) * mm});
            skLineSegment(sketch, "E2609", {"start": v(-0.81, 7.55) * mm, "end": v(-0.92, 7.55) * mm});
            skLineSegment(sketch, "E2610", {"start": v(-0.92, 7.55) * mm, "end": v(-1.03, 7.55) * mm});
            skLineSegment(sketch, "E2611", {"start": v(-1.03, 7.55) * mm, "end": v(-1.14, 7.55) * mm});
            skLineSegment(sketch, "E2612", {"start": v(-1.14, 7.55) * mm, "end": v(-1.25, 7.55) * mm});
            skLineSegment(sketch, "E2613", {"start": v(-1.25, 7.55) * mm, "end": v(-1.36, 7.55) * mm});
            skLineSegment(sketch, "E2614", {"start": v(-1.36, 7.55) * mm, "end": v(-1.47, 7.55) * mm});
            skLineSegment(sketch, "E2615", {"start": v(-1.47, 7.55) * mm, "end": v(-1.58, 7.55) * mm});
            skLineSegment(sketch, "E2616", {"start": v(-1.58, 7.55) * mm, "end": v(-1.69, 7.55) * mm});
            skLineSegment(sketch, "E2617", {"start": v(0.37, 7.75) * mm, "end": v(0.53, 7.75) * mm});
            skLineSegment(sketch, "E2618", {"start": v(0.53, 7.75) * mm, "end": v(0.7, 7.75) * mm});
            skLineSegment(sketch, "E2619", {"start": v(0.7, 7.75) * mm, "end": v(0.85, 7.75) * mm});
            skLineSegment(sketch, "E2620", {"start": v(0.85, 7.75) * mm, "end": v(1.01, 7.75) * mm});
            skLineSegment(sketch, "E2621", {"start": v(1.01, 7.75) * mm, "end": v(1.17, 7.75) * mm});
            skLineSegment(sketch, "E2622", {"start": v(1.17, 7.75) * mm, "end": v(1.33, 7.75) * mm});
            skLineSegment(sketch, "E2623", {"start": v(1.33, 7.75) * mm, "end": v(1.49, 7.75) * mm});
            skLineSegment(sketch, "E2624", {"start": v(1.49, 7.75) * mm, "end": v(1.65, 7.75) * mm});
            skLineSegment(sketch, "E2625", {"start": v(1.65, 7.75) * mm, "end": v(1.65, 7.72) * mm});
            skLineSegment(sketch, "E2626", {"start": v(1.65, 7.72) * mm, "end": v(1.65, 7.7) * mm});
            skLineSegment(sketch, "E2627", {"start": v(1.65, 7.7) * mm, "end": v(1.65, 7.68) * mm});
            skLineSegment(sketch, "E2628", {"start": v(1.65, 7.68) * mm, "end": v(1.65, 7.66) * mm});
            skLineSegment(sketch, "E2629", {"start": v(1.65, 7.66) * mm, "end": v(1.65, 7.63) * mm});
            skLineSegment(sketch, "E2630", {"start": v(1.65, 7.63) * mm, "end": v(1.65, 7.6) * mm});
            skLineSegment(sketch, "E2631", {"start": v(1.65, 7.6) * mm, "end": v(1.65, 7.59) * mm});
            skLineSegment(sketch, "E2632", {"start": v(1.65, 7.59) * mm, "end": v(1.65, 7.56) * mm});
            skLineSegment(sketch, "E2633", {"start": v(1.65, 7.56) * mm, "end": v(1.49, 7.56) * mm});
            skLineSegment(sketch, "E2634", {"start": v(1.49, 7.56) * mm, "end": v(1.33, 7.56) * mm});
            skLineSegment(sketch, "E2635", {"start": v(1.33, 7.56) * mm, "end": v(1.17, 7.56) * mm});
            skLineSegment(sketch, "E2636", {"start": v(1.17, 7.56) * mm, "end": v(1.01, 7.56) * mm});
            skLineSegment(sketch, "E2637", {"start": v(1.01, 7.56) * mm, "end": v(0.85, 7.56) * mm});
            skLineSegment(sketch, "E2638", {"start": v(0.85, 7.56) * mm, "end": v(0.7, 7.56) * mm});
            skLineSegment(sketch, "E2639", {"start": v(0.7, 7.56) * mm, "end": v(0.53, 7.56) * mm});
            skLineSegment(sketch, "E2640", {"start": v(0.53, 7.56) * mm, "end": v(0.37, 7.56) * mm});
            skLineSegment(sketch, "E2641", {"start": v(0.37, 7.56) * mm, "end": v(0.37, 7.42) * mm});
            skLineSegment(sketch, "E2642", {"start": v(0.37, 7.42) * mm, "end": v(0.37, 7.27) * mm});
            skLineSegment(sketch, "E2643", {"start": v(0.37, 7.27) * mm, "end": v(0.37, 7.12) * mm});
            skLineSegment(sketch, "E2644", {"start": v(0.37, 7.12) * mm, "end": v(0.37, 6.98) * mm});
            skLineSegment(sketch, "E2645", {"start": v(0.37, 6.98) * mm, "end": v(0.37, 6.83) * mm});
            skLineSegment(sketch, "E2646", {"start": v(0.37, 6.83) * mm, "end": v(0.37, 6.68) * mm});
            skLineSegment(sketch, "E2647", {"start": v(0.37, 6.68) * mm, "end": v(0.37, 6.53) * mm});
            skLineSegment(sketch, "E2648", {"start": v(0.37, 6.53) * mm, "end": v(0.37, 6.39) * mm});
            skLineSegment(sketch, "E2649", {"start": v(0.37, 6.39) * mm, "end": v(0.57, 6.39) * mm});
            skLineSegment(sketch, "E2650", {"start": v(0.57, 6.39) * mm, "end": v(0.76, 6.39) * mm});
            skLineSegment(sketch, "E2651", {"start": v(0.76, 6.39) * mm, "end": v(0.96, 6.39) * mm});
            skLineSegment(sketch, "E2652", {"start": v(0.96, 6.39) * mm, "end": v(1.15, 6.39) * mm});
            skLineSegment(sketch, "E2653", {"start": v(1.15, 6.39) * mm, "end": v(1.34, 6.39) * mm});
            skLineSegment(sketch, "E2654", {"start": v(1.34, 6.39) * mm, "end": v(1.54, 6.39) * mm});
            skLineSegment(sketch, "E2655", {"start": v(1.54, 6.39) * mm, "end": v(1.73, 6.39) * mm});
            skLineSegment(sketch, "E2656", {"start": v(1.73, 6.39) * mm, "end": v(1.93, 6.39) * mm});
            skLineSegment(sketch, "E2657", {"start": v(1.93, 6.39) * mm, "end": v(1.93, 6.36) * mm});
            skLineSegment(sketch, "E2658", {"start": v(1.93, 6.36) * mm, "end": v(1.93, 6.34) * mm});
            skLineSegment(sketch, "E2659", {"start": v(1.93, 6.34) * mm, "end": v(1.93, 6.32) * mm});
            skLineSegment(sketch, "E2660", {"start": v(1.93, 6.32) * mm, "end": v(1.93, 6.3) * mm});
            skLineSegment(sketch, "E2661", {"start": v(1.93, 6.3) * mm, "end": v(1.93, 6.27) * mm});
            skLineSegment(sketch, "E2662", {"start": v(1.93, 6.27) * mm, "end": v(1.93, 6.25) * mm});
            skLineSegment(sketch, "E2663", {"start": v(1.93, 6.25) * mm, "end": v(1.93, 6.23) * mm});
            skLineSegment(sketch, "E2664", {"start": v(1.93, 6.23) * mm, "end": v(1.93, 6.2) * mm});
            skLineSegment(sketch, "E2665", {"start": v(1.93, 6.2) * mm, "end": v(1.7, 6.2) * mm});
            skLineSegment(sketch, "E2666", {"start": v(1.7, 6.2) * mm, "end": v(1.49, 6.2) * mm});
            skLineSegment(sketch, "E2667", {"start": v(1.49, 6.2) * mm, "end": v(1.27, 6.2) * mm});
            skLineSegment(sketch, "E2668", {"start": v(1.27, 6.2) * mm, "end": v(1.05, 6.2) * mm});
            skLineSegment(sketch, "E2669", {"start": v(1.05, 6.2) * mm, "end": v(0.83, 6.2) * mm});
            skLineSegment(sketch, "E2670", {"start": v(0.83, 6.2) * mm, "end": v(0.6, 6.2) * mm});
            skLineSegment(sketch, "E2671", {"start": v(0.6, 6.2) * mm, "end": v(0.39, 6.2) * mm});
            skLineSegment(sketch, "E2672", {"start": v(0.39, 6.2) * mm, "end": v(0.17, 6.2) * mm});
            skLineSegment(sketch, "E2673", {"start": v(0.17, 6.2) * mm, "end": v(0.17, 6.55) * mm});
            skLineSegment(sketch, "E2674", {"start": v(0.17, 6.55) * mm, "end": v(0.17, 6.9) * mm});
            skLineSegment(sketch, "E2675", {"start": v(0.17, 6.9) * mm, "end": v(0.17, 7.25) * mm});
            skLineSegment(sketch, "E2676", {"start": v(0.17, 7.25) * mm, "end": v(0.17, 7.6) * mm});
            skLineSegment(sketch, "E2677", {"start": v(0.17, 7.6) * mm, "end": v(0.17, 7.94) * mm});
            skLineSegment(sketch, "E2678", {"start": v(0.17, 7.94) * mm, "end": v(0.17, 8.29) * mm});
            skLineSegment(sketch, "E2679", {"start": v(0.17, 8.29) * mm, "end": v(0.17, 8.63) * mm});
            skLineSegment(sketch, "E2680", {"start": v(0.17, 8.63) * mm, "end": v(0.17, 8.98) * mm});
            skLineSegment(sketch, "E2681", {"start": v(0.17, 8.98) * mm, "end": v(0.39, 8.98) * mm});
            skLineSegment(sketch, "E2682", {"start": v(0.39, 8.98) * mm, "end": v(0.6, 8.98) * mm});
            skLineSegment(sketch, "E2683", {"start": v(0.6, 8.98) * mm, "end": v(0.83, 8.98) * mm});
            skLineSegment(sketch, "E2684", {"start": v(0.83, 8.98) * mm, "end": v(1.05, 8.98) * mm});
            skLineSegment(sketch, "E2685", {"start": v(1.05, 8.98) * mm, "end": v(1.27, 8.98) * mm});
            skLineSegment(sketch, "E2686", {"start": v(1.27, 8.98) * mm, "end": v(1.49, 8.98) * mm});
            skLineSegment(sketch, "E2687", {"start": v(1.49, 8.98) * mm, "end": v(1.7, 8.98) * mm});
            skLineSegment(sketch, "E2688", {"start": v(1.7, 8.98) * mm, "end": v(1.93, 8.98) * mm});
            skLineSegment(sketch, "E2689", {"start": v(1.93, 8.98) * mm, "end": v(1.93, 8.96) * mm});
            skLineSegment(sketch, "E2690", {"start": v(1.93, 8.96) * mm, "end": v(1.93, 8.93) * mm});
            skLineSegment(sketch, "E2691", {"start": v(1.93, 8.93) * mm, "end": v(1.93, 8.91) * mm});
            skLineSegment(sketch, "E2692", {"start": v(1.93, 8.91) * mm, "end": v(1.93, 8.89) * mm});
            skLineSegment(sketch, "E2693", {"start": v(1.93, 8.89) * mm, "end": v(1.93, 8.86) * mm});
            skLineSegment(sketch, "E2694", {"start": v(1.93, 8.86) * mm, "end": v(1.93, 8.84) * mm});
            skLineSegment(sketch, "E2695", {"start": v(1.93, 8.84) * mm, "end": v(1.93, 8.82) * mm});
            skLineSegment(sketch, "E2696", {"start": v(1.93, 8.82) * mm, "end": v(1.93, 8.8) * mm});
            skLineSegment(sketch, "E2697", {"start": v(1.93, 8.8) * mm, "end": v(1.73, 8.8) * mm});
            skLineSegment(sketch, "E2698", {"start": v(1.73, 8.8) * mm, "end": v(1.54, 8.8) * mm});
            skLineSegment(sketch, "E2699", {"start": v(1.54, 8.8) * mm, "end": v(1.34, 8.8) * mm});
            skLineSegment(sketch, "E2700", {"start": v(1.34, 8.8) * mm, "end": v(1.15, 8.8) * mm});
            skLineSegment(sketch, "E2701", {"start": v(1.15, 8.8) * mm, "end": v(0.96, 8.8) * mm});
            skLineSegment(sketch, "E2702", {"start": v(0.96, 8.8) * mm, "end": v(0.76, 8.8) * mm});
            skLineSegment(sketch, "E2703", {"start": v(0.76, 8.8) * mm, "end": v(0.57, 8.8) * mm});
            skLineSegment(sketch, "E2704", {"start": v(0.57, 8.8) * mm, "end": v(0.37, 8.8) * mm});
            skLineSegment(sketch, "E2705", {"start": v(0.37, 8.8) * mm, "end": v(0.37, 8.66) * mm});
            skLineSegment(sketch, "E2706", {"start": v(0.37, 8.66) * mm, "end": v(0.37, 8.53) * mm});
            skLineSegment(sketch, "E2707", {"start": v(0.37, 8.53) * mm, "end": v(0.37, 8.4) * mm});
            skLineSegment(sketch, "E2708", {"start": v(0.37, 8.4) * mm, "end": v(0.37, 8.27) * mm});
            skLineSegment(sketch, "E2709", {"start": v(0.37, 8.27) * mm, "end": v(0.37, 8.14) * mm});
            skLineSegment(sketch, "E2710", {"start": v(0.37, 8.14) * mm, "end": v(0.37, 8) * mm});
            skLineSegment(sketch, "E2711", {"start": v(0.37, 8) * mm, "end": v(0.37, 7.88) * mm});
            skLineSegment(sketch, "E2712", {"start": v(0.37, 7.88) * mm, "end": v(0.37, 7.75) * mm});
            skLineSegment(sketch, "E2713", {"start": v(2.56, 8.64) * mm, "end": v(2.56, 8.33) * mm});
            skLineSegment(sketch, "E2714", {"start": v(2.56, 8.33) * mm, "end": v(2.56, 8.03) * mm});
            skLineSegment(sketch, "E2715", {"start": v(2.56, 8.03) * mm, "end": v(2.56, 7.73) * mm});
            skLineSegment(sketch, "E2716", {"start": v(2.56, 7.73) * mm, "end": v(2.56, 7.42) * mm});
            skLineSegment(sketch, "E2717", {"start": v(2.56, 7.42) * mm, "end": v(2.56, 7.12) * mm});
            skLineSegment(sketch, "E2718", {"start": v(2.56, 7.12) * mm, "end": v(2.56, 6.81) * mm});
            skLineSegment(sketch, "E2719", {"start": v(2.56, 6.81) * mm, "end": v(2.56, 6.5) * mm});
            skLineSegment(sketch, "E2720", {"start": v(2.56, 6.5) * mm, "end": v(2.56, 6.2) * mm});
            skLineSegment(sketch, "E2721", {"start": v(2.56, 6.2) * mm, "end": v(2.54, 6.2) * mm});
            skLineSegment(sketch, "E2722", {"start": v(2.54, 6.2) * mm, "end": v(2.5, 6.2) * mm});
            skLineSegment(sketch, "E2723", {"start": v(2.5, 6.2) * mm, "end": v(2.48, 6.2) * mm});
            skLineSegment(sketch, "E2724", {"start": v(2.48, 6.2) * mm, "end": v(2.46, 6.2) * mm});
            skLineSegment(sketch, "E2725", {"start": v(2.46, 6.2) * mm, "end": v(2.43, 6.2) * mm});
            skLineSegment(sketch, "E2726", {"start": v(2.43, 6.2) * mm, "end": v(2.4, 6.2) * mm});
            skLineSegment(sketch, "E2727", {"start": v(2.4, 6.2) * mm, "end": v(2.38, 6.2) * mm});
            skLineSegment(sketch, "E2728", {"start": v(2.38, 6.2) * mm, "end": v(2.35, 6.2) * mm});
            skLineSegment(sketch, "E2729", {"start": v(2.35, 6.2) * mm, "end": v(2.35, 6.55) * mm});
            skLineSegment(sketch, "E2730", {"start": v(2.35, 6.55) * mm, "end": v(2.35, 6.9) * mm});
            skLineSegment(sketch, "E2731", {"start": v(2.35, 6.9) * mm, "end": v(2.35, 7.24) * mm});
            skLineSegment(sketch, "E2732", {"start": v(2.35, 7.24) * mm, "end": v(2.35, 7.6) * mm});
            skLineSegment(sketch, "E2733", {"start": v(2.35, 7.6) * mm, "end": v(2.35, 7.94) * mm});
            skLineSegment(sketch, "E2734", {"start": v(2.35, 7.94) * mm, "end": v(2.35, 8.29) * mm});
            skLineSegment(sketch, "E2735", {"start": v(2.35, 8.29) * mm, "end": v(2.35, 8.63) * mm});
            skLineSegment(sketch, "E2736", {"start": v(2.35, 8.63) * mm, "end": v(2.35, 8.98) * mm});
            skLineSegment(sketch, "E2737", {"start": v(2.35, 8.98) * mm, "end": v(2.38, 8.98) * mm});
            skLineSegment(sketch, "E2738", {"start": v(2.38, 8.98) * mm, "end": v(2.4, 8.98) * mm});
            skLineSegment(sketch, "E2739", {"start": v(2.4, 8.98) * mm, "end": v(2.43, 8.98) * mm});
            skLineSegment(sketch, "E2740", {"start": v(2.43, 8.98) * mm, "end": v(2.46, 8.98) * mm});
            skLineSegment(sketch, "E2741", {"start": v(2.46, 8.98) * mm, "end": v(2.48, 8.98) * mm});
            skLineSegment(sketch, "E2742", {"start": v(2.48, 8.98) * mm, "end": v(2.5, 8.98) * mm});
            skLineSegment(sketch, "E2743", {"start": v(2.5, 8.98) * mm, "end": v(2.54, 8.98) * mm});
            skLineSegment(sketch, "E2744", {"start": v(2.54, 8.98) * mm, "end": v(2.56, 8.98) * mm});
            skLineSegment(sketch, "E2745", {"start": v(2.56, 8.98) * mm, "end": v(2.78, 8.68) * mm});
            skLineSegment(sketch, "E2746", {"start": v(2.78, 8.68) * mm, "end": v(2.99, 8.37) * mm});
            skLineSegment(sketch, "E2747", {"start": v(2.99, 8.37) * mm, "end": v(3.2, 8.07) * mm});
            skLineSegment(sketch, "E2748", {"start": v(3.2, 8.07) * mm, "end": v(3.42, 7.76) * mm});
            skLineSegment(sketch, "E2749", {"start": v(3.42, 7.76) * mm, "end": v(3.63, 7.46) * mm});
            skLineSegment(sketch, "E2750", {"start": v(3.63, 7.46) * mm, "end": v(3.85, 7.15) * mm});
            skLineSegment(sketch, "E2751", {"start": v(3.85, 7.15) * mm, "end": v(4.06, 6.85) * mm});
            skLineSegment(sketch, "E2752", {"start": v(4.06, 6.85) * mm, "end": v(4.27, 6.54) * mm});
            skLineSegment(sketch, "E2753", {"start": v(4.27, 6.54) * mm, "end": v(4.27, 6.85) * mm});
            skLineSegment(sketch, "E2754", {"start": v(4.27, 6.85) * mm, "end": v(4.27, 7.15) * mm});
            skLineSegment(sketch, "E2755", {"start": v(4.27, 7.15) * mm, "end": v(4.27, 7.46) * mm});
            skLineSegment(sketch, "E2756", {"start": v(4.27, 7.46) * mm, "end": v(4.27, 7.76) * mm});
            skLineSegment(sketch, "E2757", {"start": v(4.27, 7.76) * mm, "end": v(4.27, 8.07) * mm});
            skLineSegment(sketch, "E2758", {"start": v(4.27, 8.07) * mm, "end": v(4.27, 8.37) * mm});
            skLineSegment(sketch, "E2759", {"start": v(4.27, 8.37) * mm, "end": v(4.27, 8.68) * mm});
            skLineSegment(sketch, "E2760", {"start": v(4.27, 8.68) * mm, "end": v(4.27, 8.98) * mm});
            skLineSegment(sketch, "E2761", {"start": v(4.27, 8.98) * mm, "end": v(4.3, 8.98) * mm});
            skLineSegment(sketch, "E2762", {"start": v(4.3, 8.98) * mm, "end": v(4.33, 8.98) * mm});
            skLineSegment(sketch, "E2763", {"start": v(4.33, 8.98) * mm, "end": v(4.35, 8.98) * mm});
            skLineSegment(sketch, "E2764", {"start": v(4.35, 8.98) * mm, "end": v(4.38, 8.98) * mm});
            skLineSegment(sketch, "E2765", {"start": v(4.38, 8.98) * mm, "end": v(4.4, 8.98) * mm});
            skLineSegment(sketch, "E2766", {"start": v(4.4, 8.98) * mm, "end": v(4.43, 8.98) * mm});
            skLineSegment(sketch, "E2767", {"start": v(4.43, 8.98) * mm, "end": v(4.46, 8.98) * mm});
            skLineSegment(sketch, "E2768", {"start": v(4.46, 8.98) * mm, "end": v(4.48, 8.98) * mm});
            skLineSegment(sketch, "E2769", {"start": v(4.48, 8.98) * mm, "end": v(4.48, 8.63) * mm});
            skLineSegment(sketch, "E2770", {"start": v(4.48, 8.63) * mm, "end": v(4.48, 8.29) * mm});
            skLineSegment(sketch, "E2771", {"start": v(4.48, 8.29) * mm, "end": v(4.48, 7.94) * mm});
            skLineSegment(sketch, "E2772", {"start": v(4.48, 7.94) * mm, "end": v(4.48, 7.6) * mm});
            skLineSegment(sketch, "E2773", {"start": v(4.48, 7.6) * mm, "end": v(4.48, 7.24) * mm});
            skLineSegment(sketch, "E2774", {"start": v(4.48, 7.24) * mm, "end": v(4.48, 6.9) * mm});
            skLineSegment(sketch, "E2775", {"start": v(4.48, 6.9) * mm, "end": v(4.48, 6.55) * mm});
            skLineSegment(sketch, "E2776", {"start": v(4.48, 6.55) * mm, "end": v(4.48, 6.2) * mm});
            skLineSegment(sketch, "E2777", {"start": v(4.48, 6.2) * mm, "end": v(4.46, 6.2) * mm});
            skLineSegment(sketch, "E2778", {"start": v(4.46, 6.2) * mm, "end": v(4.43, 6.2) * mm});
            skLineSegment(sketch, "E2779", {"start": v(4.43, 6.2) * mm, "end": v(4.4, 6.2) * mm});
            skLineSegment(sketch, "E2780", {"start": v(4.4, 6.2) * mm, "end": v(4.38, 6.2) * mm});
            skLineSegment(sketch, "E2781", {"start": v(4.38, 6.2) * mm, "end": v(4.35, 6.2) * mm});
            skLineSegment(sketch, "E2782", {"start": v(4.35, 6.2) * mm, "end": v(4.33, 6.2) * mm});
            skLineSegment(sketch, "E2783", {"start": v(4.33, 6.2) * mm, "end": v(4.3, 6.2) * mm});
            skLineSegment(sketch, "E2784", {"start": v(4.3, 6.2) * mm, "end": v(4.27, 6.2) * mm});
            skLineSegment(sketch, "E2785", {"start": v(4.27, 6.2) * mm, "end": v(4.06, 6.5) * mm});
            skLineSegment(sketch, "E2786", {"start": v(4.06, 6.5) * mm, "end": v(3.85, 6.81) * mm});
            skLineSegment(sketch, "E2787", {"start": v(3.85, 6.81) * mm, "end": v(3.63, 7.12) * mm});
            skLineSegment(sketch, "E2788", {"start": v(3.63, 7.12) * mm, "end": v(3.42, 7.42) * mm});
            skLineSegment(sketch, "E2789", {"start": v(3.42, 7.42) * mm, "end": v(3.2, 7.73) * mm});
            skLineSegment(sketch, "E2790", {"start": v(3.2, 7.73) * mm, "end": v(2.99, 8.03) * mm});
            skLineSegment(sketch, "E2791", {"start": v(2.99, 8.03) * mm, "end": v(2.78, 8.33) * mm});
            skLineSegment(sketch, "E2792", {"start": v(2.78, 8.33) * mm, "end": v(2.56, 8.64) * mm});
            skLineSegment(sketch, "E2793", {"start": v(6.95, 8.98) * mm, "end": v(6.95, 8.95) * mm});
            skLineSegment(sketch, "E2794", {"start": v(6.95, 8.95) * mm, "end": v(6.95, 8.93) * mm});
            skLineSegment(sketch, "E2795", {"start": v(6.95, 8.93) * mm, "end": v(6.95, 8.9) * mm});
            skLineSegment(sketch, "E2796", {"start": v(6.95, 8.9) * mm, "end": v(6.95, 8.89) * mm});
            skLineSegment(sketch, "E2797", {"start": v(6.95, 8.89) * mm, "end": v(6.95, 8.86) * mm});
            skLineSegment(sketch, "E2798", {"start": v(6.95, 8.86) * mm, "end": v(6.95, 8.84) * mm});
            skLineSegment(sketch, "E2799", {"start": v(6.95, 8.84) * mm, "end": v(6.95, 8.82) * mm});
            skLineSegment(sketch, "E2800", {"start": v(6.95, 8.82) * mm, "end": v(6.95, 8.8) * mm});
            skLineSegment(sketch, "E2801", {"start": v(6.95, 8.8) * mm, "end": v(6.84, 8.8) * mm});
            skLineSegment(sketch, "E2802", {"start": v(6.84, 8.8) * mm, "end": v(6.72, 8.8) * mm});
            skLineSegment(sketch, "E2803", {"start": v(6.72, 8.8) * mm, "end": v(6.6, 8.8) * mm});
            skLineSegment(sketch, "E2804", {"start": v(6.6, 8.8) * mm, "end": v(6.48, 8.8) * mm});
            skLineSegment(sketch, "E2805", {"start": v(6.48, 8.8) * mm, "end": v(6.36, 8.8) * mm});
            skLineSegment(sketch, "E2806", {"start": v(6.36, 8.8) * mm, "end": v(6.24, 8.8) * mm});
            skLineSegment(sketch, "E2807", {"start": v(6.24, 8.8) * mm, "end": v(6.12, 8.8) * mm});
            skLineSegment(sketch, "E2808", {"start": v(6.12, 8.8) * mm, "end": v(6, 8.8) * mm});
            skLineSegment(sketch, "E2809", {"start": v(6, 8.8) * mm, "end": v(6, 8.47) * mm});
            skLineSegment(sketch, "E2810", {"start": v(6, 8.47) * mm, "end": v(6, 8.15) * mm});
            skLineSegment(sketch, "E2811", {"start": v(6, 8.15) * mm, "end": v(6, 7.82) * mm});
            skLineSegment(sketch, "E2812", {"start": v(6, 7.82) * mm, "end": v(6, 7.5) * mm});
            skLineSegment(sketch, "E2813", {"start": v(6, 7.5) * mm, "end": v(6, 7.17) * mm});
            skLineSegment(sketch, "E2814", {"start": v(6, 7.17) * mm, "end": v(6, 6.85) * mm});
            skLineSegment(sketch, "E2815", {"start": v(6, 6.85) * mm, "end": v(6, 6.53) * mm});
            skLineSegment(sketch, "E2816", {"start": v(6, 6.53) * mm, "end": v(6, 6.2) * mm});
            skLineSegment(sketch, "E2817", {"start": v(6, 6.2) * mm, "end": v(5.98, 6.2) * mm});
            skLineSegment(sketch, "E2818", {"start": v(5.98, 6.2) * mm, "end": v(5.95, 6.2) * mm});
            skLineSegment(sketch, "E2819", {"start": v(5.95, 6.2) * mm, "end": v(5.93, 6.2) * mm});
            skLineSegment(sketch, "E2820", {"start": v(5.93, 6.2) * mm, "end": v(5.9, 6.2) * mm});
            skLineSegment(sketch, "E2821", {"start": v(5.9, 6.2) * mm, "end": v(5.87, 6.2) * mm});
            skLineSegment(sketch, "E2822", {"start": v(5.87, 6.2) * mm, "end": v(5.85, 6.2) * mm});
            skLineSegment(sketch, "E2823", {"start": v(5.85, 6.2) * mm, "end": v(5.82, 6.2) * mm});
            skLineSegment(sketch, "E2824", {"start": v(5.82, 6.2) * mm, "end": v(5.8, 6.2) * mm});
            skLineSegment(sketch, "E2825", {"start": v(5.8, 6.2) * mm, "end": v(5.8, 6.53) * mm});
            skLineSegment(sketch, "E2826", {"start": v(5.8, 6.53) * mm, "end": v(5.8, 6.85) * mm});
            skLineSegment(sketch, "E2827", {"start": v(5.8, 6.85) * mm, "end": v(5.8, 7.17) * mm});
            skLineSegment(sketch, "E2828", {"start": v(5.8, 7.17) * mm, "end": v(5.8, 7.5) * mm});
            skLineSegment(sketch, "E2829", {"start": v(5.8, 7.5) * mm, "end": v(5.8, 7.82) * mm});
            skLineSegment(sketch, "E2830", {"start": v(5.8, 7.82) * mm, "end": v(5.8, 8.15) * mm});
            skLineSegment(sketch, "E2831", {"start": v(5.8, 8.15) * mm, "end": v(5.8, 8.47) * mm});
            skLineSegment(sketch, "E2832", {"start": v(5.8, 8.47) * mm, "end": v(5.8, 8.8) * mm});
            skLineSegment(sketch, "E2833", {"start": v(5.8, 8.8) * mm, "end": v(5.68, 8.8) * mm});
            skLineSegment(sketch, "E2834", {"start": v(5.68, 8.8) * mm, "end": v(5.56, 8.8) * mm});
            skLineSegment(sketch, "E2835", {"start": v(5.56, 8.8) * mm, "end": v(5.44, 8.8) * mm});
            skLineSegment(sketch, "E2836", {"start": v(5.44, 8.8) * mm, "end": v(5.32, 8.8) * mm});
            skLineSegment(sketch, "E2837", {"start": v(5.32, 8.8) * mm, "end": v(5.2, 8.8) * mm});
            skLineSegment(sketch, "E2838", {"start": v(5.2, 8.8) * mm, "end": v(5.09, 8.8) * mm});
            skLineSegment(sketch, "E2839", {"start": v(5.09, 8.8) * mm, "end": v(4.97, 8.8) * mm});
            skLineSegment(sketch, "E2840", {"start": v(4.97, 8.8) * mm, "end": v(4.85, 8.8) * mm});
            skLineSegment(sketch, "E2841", {"start": v(4.85, 8.8) * mm, "end": v(4.85, 8.82) * mm});
            skLineSegment(sketch, "E2842", {"start": v(4.85, 8.82) * mm, "end": v(4.85, 8.84) * mm});
            skLineSegment(sketch, "E2843", {"start": v(4.85, 8.84) * mm, "end": v(4.85, 8.86) * mm});
            skLineSegment(sketch, "E2844", {"start": v(4.85, 8.86) * mm, "end": v(4.85, 8.89) * mm});
            skLineSegment(sketch, "E2845", {"start": v(4.85, 8.89) * mm, "end": v(4.85, 8.9) * mm});
            skLineSegment(sketch, "E2846", {"start": v(4.85, 8.9) * mm, "end": v(4.85, 8.93) * mm});
            skLineSegment(sketch, "E2847", {"start": v(4.85, 8.93) * mm, "end": v(4.85, 8.95) * mm});
            skLineSegment(sketch, "E2848", {"start": v(4.85, 8.95) * mm, "end": v(4.85, 8.98) * mm});
            skLineSegment(sketch, "E2849", {"start": v(4.85, 8.98) * mm, "end": v(5.11, 8.98) * mm});
            skLineSegment(sketch, "E2850", {"start": v(5.11, 8.98) * mm, "end": v(5.37, 8.98) * mm});
            skLineSegment(sketch, "E2851", {"start": v(5.37, 8.98) * mm, "end": v(5.64, 8.98) * mm});
            skLineSegment(sketch, "E2852", {"start": v(5.64, 8.98) * mm, "end": v(5.9, 8.98) * mm});
            skLineSegment(sketch, "E2853", {"start": v(5.9, 8.98) * mm, "end": v(6.16, 8.98) * mm});
            skLineSegment(sketch, "E2854", {"start": v(6.16, 8.98) * mm, "end": v(6.43, 8.98) * mm});
            skLineSegment(sketch, "E2855", {"start": v(6.43, 8.98) * mm, "end": v(6.7, 8.98) * mm});
            skLineSegment(sketch, "E2856", {"start": v(6.7, 8.98) * mm, "end": v(6.95, 8.98) * mm});
            skLineSegment(sketch, "E2857", {"start": v(7.74, 7.55) * mm, "end": v(7.65, 7.56) * mm});
            skLineSegment(sketch, "E2858", {"start": v(7.65, 7.56) * mm, "end": v(7.56, 7.59) * mm});
            skLineSegment(sketch, "E2859", {"start": v(7.56, 7.59) * mm, "end": v(7.48, 7.63) * mm});
            skLineSegment(sketch, "E2860", {"start": v(7.48, 7.63) * mm, "end": v(7.42, 7.69) * mm});
            skLineSegment(sketch, "E2861", {"start": v(7.42, 7.69) * mm, "end": v(7.36, 7.75) * mm});
            skLineSegment(sketch, "E2862", {"start": v(7.36, 7.75) * mm, "end": v(7.32, 7.83) * mm});
            skLineSegment(sketch, "E2863", {"start": v(7.32, 7.83) * mm, "end": v(7.29, 7.92) * mm});
            skLineSegment(sketch, "E2864", {"start": v(7.29, 7.92) * mm, "end": v(7.28, 8.01) * mm});
            skLineSegment(sketch, "E2865", {"start": v(7.28, 8.01) * mm, "end": v(7.28, 8.08) * mm});
            skLineSegment(sketch, "E2866", {"start": v(7.28, 8.08) * mm, "end": v(7.28, 8.14) * mm});
            skLineSegment(sketch, "E2867", {"start": v(7.28, 8.14) * mm, "end": v(7.28, 8.2) * mm});
            skLineSegment(sketch, "E2868", {"start": v(7.28, 8.2) * mm, "end": v(7.28, 8.26) * mm});
            skLineSegment(sketch, "E2869", {"start": v(7.28, 8.26) * mm, "end": v(7.28, 8.33) * mm});
            skLineSegment(sketch, "E2870", {"start": v(7.28, 8.33) * mm, "end": v(7.28, 8.4) * mm});
            skLineSegment(sketch, "E2871", {"start": v(7.28, 8.4) * mm, "end": v(7.28, 8.45) * mm});
            skLineSegment(sketch, "E2872", {"start": v(7.28, 8.45) * mm, "end": v(7.28, 8.52) * mm});
            skLineSegment(sketch, "E2873", {"start": v(7.28, 8.52) * mm, "end": v(7.29, 8.6) * mm});
            skLineSegment(sketch, "E2874", {"start": v(7.29, 8.6) * mm, "end": v(7.32, 8.7) * mm});
            skLineSegment(sketch, "E2875", {"start": v(7.32, 8.7) * mm, "end": v(7.36, 8.77) * mm});
            skLineSegment(sketch, "E2876", {"start": v(7.36, 8.77) * mm, "end": v(7.42, 8.84) * mm});
            skLineSegment(sketch, "E2877", {"start": v(7.42, 8.84) * mm, "end": v(7.48, 8.9) * mm});
            skLineSegment(sketch, "E2878", {"start": v(7.48, 8.9) * mm, "end": v(7.56, 8.94) * mm});
            skLineSegment(sketch, "E2879", {"start": v(7.56, 8.94) * mm, "end": v(7.65, 8.97) * mm});
            skLineSegment(sketch, "E2880", {"start": v(7.65, 8.97) * mm, "end": v(7.74, 8.98) * mm});
            skLineSegment(sketch, "E2881", {"start": v(7.74, 8.98) * mm, "end": v(7.89, 8.98) * mm});
            skLineSegment(sketch, "E2882", {"start": v(7.89, 8.98) * mm, "end": v(8.03, 8.98) * mm});
            skLineSegment(sketch, "E2883", {"start": v(8.03, 8.98) * mm, "end": v(8.18, 8.98) * mm});
            skLineSegment(sketch, "E2884", {"start": v(8.18, 8.98) * mm, "end": v(8.32, 8.98) * mm});
            skLineSegment(sketch, "E2885", {"start": v(8.32, 8.98) * mm, "end": v(8.47, 8.98) * mm});
            skLineSegment(sketch, "E2886", {"start": v(8.47, 8.98) * mm, "end": v(8.61, 8.98) * mm});
            skLineSegment(sketch, "E2887", {"start": v(8.61, 8.98) * mm, "end": v(8.76, 8.98) * mm});
            skLineSegment(sketch, "E2888", {"start": v(8.76, 8.98) * mm, "end": v(8.9, 8.98) * mm});
            skLineSegment(sketch, "E2889", {"start": v(8.9, 8.98) * mm, "end": v(8.9, 8.95) * mm});
            skLineSegment(sketch, "E2890", {"start": v(8.9, 8.95) * mm, "end": v(8.9, 8.93) * mm});
            skLineSegment(sketch, "E2891", {"start": v(8.9, 8.93) * mm, "end": v(8.9, 8.9) * mm});
            skLineSegment(sketch, "E2892", {"start": v(8.9, 8.9) * mm, "end": v(8.9, 8.89) * mm});
            skLineSegment(sketch, "E2893", {"start": v(8.9, 8.89) * mm, "end": v(8.9, 8.86) * mm});
            skLineSegment(sketch, "E2894", {"start": v(8.9, 8.86) * mm, "end": v(8.9, 8.84) * mm});
            skLineSegment(sketch, "E2895", {"start": v(8.9, 8.84) * mm, "end": v(8.9, 8.82) * mm});
            skLineSegment(sketch, "E2896", {"start": v(8.9, 8.82) * mm, "end": v(8.9, 8.8) * mm});
            skLineSegment(sketch, "E2897", {"start": v(8.9, 8.8) * mm, "end": v(8.76, 8.8) * mm});
            skLineSegment(sketch, "E2898", {"start": v(8.76, 8.8) * mm, "end": v(8.61, 8.8) * mm});
            skLineSegment(sketch, "E2899", {"start": v(8.61, 8.8) * mm, "end": v(8.47, 8.8) * mm});
            skLineSegment(sketch, "E2900", {"start": v(8.47, 8.8) * mm, "end": v(8.33, 8.8) * mm});
            skLineSegment(sketch, "E2901", {"start": v(8.33, 8.8) * mm, "end": v(8.18, 8.8) * mm});
            skLineSegment(sketch, "E2902", {"start": v(8.18, 8.8) * mm, "end": v(8.04, 8.8) * mm});
            skLineSegment(sketch, "E2903", {"start": v(8.04, 8.8) * mm, "end": v(7.9, 8.8) * mm});
            skLineSegment(sketch, "E2904", {"start": v(7.9, 8.8) * mm, "end": v(7.75, 8.8) * mm});
            skLineSegment(sketch, "E2905", {"start": v(7.75, 8.8) * mm, "end": v(7.7, 8.79) * mm});
            skLineSegment(sketch, "E2906", {"start": v(7.7, 8.79) * mm, "end": v(7.64, 8.77) * mm});
            skLineSegment(sketch, "E2907", {"start": v(7.64, 8.77) * mm, "end": v(7.6, 8.75) * mm});
            skLineSegment(sketch, "E2908", {"start": v(7.6, 8.75) * mm, "end": v(7.55, 8.71) * mm});
            skLineSegment(sketch, "E2909", {"start": v(7.55, 8.71) * mm, "end": v(7.52, 8.67) * mm});
            skLineSegment(sketch, "E2910", {"start": v(7.52, 8.67) * mm, "end": v(7.5, 8.62) * mm});
            skLineSegment(sketch, "E2911", {"start": v(7.5, 8.62) * mm, "end": v(7.48, 8.57) * mm});
            skLineSegment(sketch, "E2912", {"start": v(7.48, 8.57) * mm, "end": v(7.47, 8.52) * mm});
            skLineSegment(sketch, "E2913", {"start": v(7.47, 8.52) * mm, "end": v(7.47, 8.46) * mm});
            skLineSegment(sketch, "E2914", {"start": v(7.47, 8.46) * mm, "end": v(7.47, 8.4) * mm});
            skLineSegment(sketch, "E2915", {"start": v(7.47, 8.4) * mm, "end": v(7.47, 8.33) * mm});
            skLineSegment(sketch, "E2916", {"start": v(7.47, 8.33) * mm, "end": v(7.47, 8.27) * mm});
            skLineSegment(sketch, "E2917", {"start": v(7.47, 8.27) * mm, "end": v(7.47, 8.21) * mm});
            skLineSegment(sketch, "E2918", {"start": v(7.47, 8.21) * mm, "end": v(7.47, 8.15) * mm});
            skLineSegment(sketch, "E2919", {"start": v(7.47, 8.15) * mm, "end": v(7.47, 8.09) * mm});
            skLineSegment(sketch, "E2920", {"start": v(7.47, 8.09) * mm, "end": v(7.47, 8.03) * mm});
            skLineSegment(sketch, "E2921", {"start": v(7.47, 8.03) * mm, "end": v(7.48, 7.97) * mm});
            skLineSegment(sketch, "E2922", {"start": v(7.48, 7.97) * mm, "end": v(7.5, 7.92) * mm});
            skLineSegment(sketch, "E2923", {"start": v(7.5, 7.92) * mm, "end": v(7.52, 7.87) * mm});
            skLineSegment(sketch, "E2924", {"start": v(7.52, 7.87) * mm, "end": v(7.55, 7.83) * mm});
            skLineSegment(sketch, "E2925", {"start": v(7.55, 7.83) * mm, "end": v(7.6, 7.8) * mm});
            skLineSegment(sketch, "E2926", {"start": v(7.6, 7.8) * mm, "end": v(7.64, 7.77) * mm});
            skLineSegment(sketch, "E2927", {"start": v(7.64, 7.77) * mm, "end": v(7.7, 7.76) * mm});
            skLineSegment(sketch, "E2928", {"start": v(7.7, 7.76) * mm, "end": v(7.75, 7.75) * mm});
            skLineSegment(sketch, "E2929", {"start": v(7.75, 7.75) * mm, "end": v(7.86, 7.75) * mm});
            skLineSegment(sketch, "E2930", {"start": v(7.86, 7.75) * mm, "end": v(7.97, 7.75) * mm});
            skLineSegment(sketch, "E2931", {"start": v(7.97, 7.75) * mm, "end": v(8.08, 7.75) * mm});
            skLineSegment(sketch, "E2932", {"start": v(8.08, 7.75) * mm, "end": v(8.19, 7.75) * mm});
            skLineSegment(sketch, "E2933", {"start": v(8.19, 7.75) * mm, "end": v(8.3, 7.75) * mm});
            skLineSegment(sketch, "E2934", {"start": v(8.3, 7.75) * mm, "end": v(8.4, 7.75) * mm});
            skLineSegment(sketch, "E2935", {"start": v(8.4, 7.75) * mm, "end": v(8.52, 7.75) * mm});
            skLineSegment(sketch, "E2936", {"start": v(8.52, 7.75) * mm, "end": v(8.63, 7.75) * mm});
            skLineSegment(sketch, "E2937", {"start": v(8.63, 7.75) * mm, "end": v(8.72, 7.74) * mm});
            skLineSegment(sketch, "E2938", {"start": v(8.72, 7.74) * mm, "end": v(8.8, 7.71) * mm});
            skLineSegment(sketch, "E2939", {"start": v(8.8, 7.71) * mm, "end": v(8.89, 7.67) * mm});
            skLineSegment(sketch, "E2940", {"start": v(8.89, 7.67) * mm, "end": v(8.95, 7.62) * mm});
            skLineSegment(sketch, "E2941", {"start": v(8.95, 7.62) * mm, "end": v(9.01, 7.55) * mm});
            skLineSegment(sketch, "E2942", {"start": v(9.01, 7.55) * mm, "end": v(9.05, 7.47) * mm});
            skLineSegment(sketch, "E2943", {"start": v(9.05, 7.47) * mm, "end": v(9.08, 7.38) * mm});
            skLineSegment(sketch, "E2944", {"start": v(9.08, 7.38) * mm, "end": v(9.09, 7.29) * mm});
            skLineSegment(sketch, "E2945", {"start": v(9.09, 7.29) * mm, "end": v(9.09, 7.2) * mm});
            skLineSegment(sketch, "E2946", {"start": v(9.09, 7.2) * mm, "end": v(9.09, 7.13) * mm});
            skLineSegment(sketch, "E2947", {"start": v(9.09, 7.13) * mm, "end": v(9.09, 7.05) * mm});
            skLineSegment(sketch, "E2948", {"start": v(9.09, 7.05) * mm, "end": v(9.09, 6.97) * mm});
            skLineSegment(sketch, "E2949", {"start": v(9.09, 6.97) * mm, "end": v(9.09, 6.9) * mm});
            skLineSegment(sketch, "E2950", {"start": v(9.09, 6.9) * mm, "end": v(9.09, 6.82) * mm});
            skLineSegment(sketch, "E2951", {"start": v(9.09, 6.82) * mm, "end": v(9.09, 6.74) * mm});
            skLineSegment(sketch, "E2952", {"start": v(9.09, 6.74) * mm, "end": v(9.09, 6.66) * mm});
            skLineSegment(sketch, "E2953", {"start": v(9.09, 6.66) * mm, "end": v(9.08, 6.57) * mm});
            skLineSegment(sketch, "E2954", {"start": v(9.08, 6.57) * mm, "end": v(9.05, 6.48) * mm});
            skLineSegment(sketch, "E2955", {"start": v(9.05, 6.48) * mm, "end": v(9.01, 6.4) * mm});
            skLineSegment(sketch, "E2956", {"start": v(9.01, 6.4) * mm, "end": v(8.95, 6.34) * mm});
            skLineSegment(sketch, "E2957", {"start": v(8.95, 6.34) * mm, "end": v(8.89, 6.28) * mm});
            skLineSegment(sketch, "E2958", {"start": v(8.89, 6.28) * mm, "end": v(8.8, 6.24) * mm});
            skLineSegment(sketch, "E2959", {"start": v(8.8, 6.24) * mm, "end": v(8.72, 6.21) * mm});
            skLineSegment(sketch, "E2960", {"start": v(8.72, 6.21) * mm, "end": v(8.63, 6.2) * mm});
            skLineSegment(sketch, "E2961", {"start": v(8.63, 6.2) * mm, "end": v(8.46, 6.2) * mm});
            skLineSegment(sketch, "E2962", {"start": v(8.46, 6.2) * mm, "end": v(8.28, 6.2) * mm});
            skLineSegment(sketch, "E2963", {"start": v(8.28, 6.2) * mm, "end": v(8.1, 6.2) * mm});
            skLineSegment(sketch, "E2964", {"start": v(8.1, 6.2) * mm, "end": v(7.93, 6.2) * mm});
            skLineSegment(sketch, "E2965", {"start": v(7.93, 6.2) * mm, "end": v(7.76, 6.2) * mm});
            skLineSegment(sketch, "E2966", {"start": v(7.76, 6.2) * mm, "end": v(7.59, 6.2) * mm});
            skLineSegment(sketch, "E2967", {"start": v(7.59, 6.2) * mm, "end": v(7.41, 6.2) * mm});
            skLineSegment(sketch, "E2968", {"start": v(7.41, 6.2) * mm, "end": v(7.24, 6.2) * mm});
            skLineSegment(sketch, "E2969", {"start": v(7.24, 6.2) * mm, "end": v(7.24, 6.23) * mm});
            skLineSegment(sketch, "E2970", {"start": v(7.24, 6.23) * mm, "end": v(7.24, 6.25) * mm});
            skLineSegment(sketch, "E2971", {"start": v(7.24, 6.25) * mm, "end": v(7.24, 6.27) * mm});
            skLineSegment(sketch, "E2972", {"start": v(7.24, 6.27) * mm, "end": v(7.24, 6.3) * mm});
            skLineSegment(sketch, "E2973", {"start": v(7.24, 6.3) * mm, "end": v(7.24, 6.32) * mm});
            skLineSegment(sketch, "E2974", {"start": v(7.24, 6.32) * mm, "end": v(7.24, 6.34) * mm});
            skLineSegment(sketch, "E2975", {"start": v(7.24, 6.34) * mm, "end": v(7.24, 6.36) * mm});
            skLineSegment(sketch, "E2976", {"start": v(7.24, 6.36) * mm, "end": v(7.24, 6.39) * mm});
            skLineSegment(sketch, "E2977", {"start": v(7.24, 6.39) * mm, "end": v(7.41, 6.39) * mm});
            skLineSegment(sketch, "E2978", {"start": v(7.41, 6.39) * mm, "end": v(7.58, 6.39) * mm});
            skLineSegment(sketch, "E2979", {"start": v(7.58, 6.39) * mm, "end": v(7.76, 6.39) * mm});
            skLineSegment(sketch, "E2980", {"start": v(7.76, 6.39) * mm, "end": v(7.93, 6.39) * mm});
            skLineSegment(sketch, "E2981", {"start": v(7.93, 6.39) * mm, "end": v(8.1, 6.39) * mm});
            skLineSegment(sketch, "E2982", {"start": v(8.1, 6.39) * mm, "end": v(8.28, 6.39) * mm});
            skLineSegment(sketch, "E2983", {"start": v(8.28, 6.39) * mm, "end": v(8.45, 6.39) * mm});
            skLineSegment(sketch, "E2984", {"start": v(8.45, 6.39) * mm, "end": v(8.62, 6.39) * mm});
            skLineSegment(sketch, "E2985", {"start": v(8.62, 6.39) * mm, "end": v(8.68, 6.4) * mm});
            skLineSegment(sketch, "E2986", {"start": v(8.68, 6.4) * mm, "end": v(8.73, 6.4) * mm});
            skLineSegment(sketch, "E2987", {"start": v(8.73, 6.4) * mm, "end": v(8.77, 6.43) * mm});
            skLineSegment(sketch, "E2988", {"start": v(8.77, 6.43) * mm, "end": v(8.82, 6.47) * mm});
            skLineSegment(sketch, "E2989", {"start": v(8.82, 6.47) * mm, "end": v(8.85, 6.5) * mm});
            skLineSegment(sketch, "E2990", {"start": v(8.85, 6.5) * mm, "end": v(8.88, 6.56) * mm});
            skLineSegment(sketch, "E2991", {"start": v(8.88, 6.56) * mm, "end": v(8.9, 6.6) * mm});
            skLineSegment(sketch, "E2992", {"start": v(8.9, 6.6) * mm, "end": v(8.9, 6.66) * mm});
            skLineSegment(sketch, "E2993", {"start": v(8.9, 6.66) * mm, "end": v(8.9, 6.74) * mm});
            skLineSegment(sketch, "E2994", {"start": v(8.9, 6.74) * mm, "end": v(8.9, 6.81) * mm});
            skLineSegment(sketch, "E2995", {"start": v(8.9, 6.81) * mm, "end": v(8.9, 6.9) * mm});
            skLineSegment(sketch, "E2996", {"start": v(8.9, 6.9) * mm, "end": v(8.9, 6.97) * mm});
            skLineSegment(sketch, "E2997", {"start": v(8.9, 6.97) * mm, "end": v(8.9, 7.04) * mm});
            skLineSegment(sketch, "E2998", {"start": v(8.9, 7.04) * mm, "end": v(8.9, 7.12) * mm});
            skLineSegment(sketch, "E2999", {"start": v(8.9, 7.12) * mm, "end": v(8.9, 7.2) * mm});
            skLineSegment(sketch, "E3000", {"start": v(8.9, 7.2) * mm, "end": v(8.9, 7.27) * mm});
            skLineSegment(sketch, "E3001", {"start": v(8.9, 7.27) * mm, "end": v(8.9, 7.33) * mm});
            skLineSegment(sketch, "E3002", {"start": v(8.9, 7.33) * mm, "end": v(8.88, 7.38) * mm});
            skLineSegment(sketch, "E3003", {"start": v(8.88, 7.38) * mm, "end": v(8.85, 7.43) * mm});
            skLineSegment(sketch, "E3004", {"start": v(8.85, 7.43) * mm, "end": v(8.82, 7.47) * mm});
            skLineSegment(sketch, "E3005", {"start": v(8.82, 7.47) * mm, "end": v(8.77, 7.5) * mm});
            skLineSegment(sketch, "E3006", {"start": v(8.77, 7.5) * mm, "end": v(8.73, 7.53) * mm});
            skLineSegment(sketch, "E3007", {"start": v(8.73, 7.53) * mm, "end": v(8.68, 7.55) * mm});
            skLineSegment(sketch, "E3008", {"start": v(8.68, 7.55) * mm, "end": v(8.62, 7.55) * mm});
            skLineSegment(sketch, "E3009", {"start": v(8.62, 7.55) * mm, "end": v(8.51, 7.55) * mm});
            skLineSegment(sketch, "E3010", {"start": v(8.51, 7.55) * mm, "end": v(8.4, 7.55) * mm});
            skLineSegment(sketch, "E3011", {"start": v(8.4, 7.55) * mm, "end": v(8.3, 7.55) * mm});
            skLineSegment(sketch, "E3012", {"start": v(8.3, 7.55) * mm, "end": v(8.18, 7.55) * mm});
            skLineSegment(sketch, "E3013", {"start": v(8.18, 7.55) * mm, "end": v(8.07, 7.55) * mm});
            skLineSegment(sketch, "E3014", {"start": v(8.07, 7.55) * mm, "end": v(7.96, 7.55) * mm});
            skLineSegment(sketch, "E3015", {"start": v(7.96, 7.55) * mm, "end": v(7.85, 7.55) * mm});
            skLineSegment(sketch, "E3016", {"start": v(7.85, 7.55) * mm, "end": v(7.74, 7.55) * mm});
            skLineSegment(sketch, "E3017", {"start": v(-36.3, 6.83) * mm, "end": v(-33.14, 6.83) * mm});
            skLineSegment(sketch, "E3018", {"start": v(-33.14, 6.83) * mm, "end": v(-30, 6.83) * mm});
            skLineSegment(sketch, "E3019", {"start": v(-30, 6.83) * mm, "end": v(-26.85, 6.83) * mm});
            skLineSegment(sketch, "E3020", {"start": v(-26.85, 6.83) * mm, "end": v(-23.7, 6.83) * mm});
            skLineSegment(sketch, "E3021", {"start": v(-23.7, 6.83) * mm, "end": v(-20.55, 6.83) * mm});
            skLineSegment(sketch, "E3022", {"start": v(-20.55, 6.83) * mm, "end": v(-17.4, 6.83) * mm});
            skLineSegment(sketch, "E3023", {"start": v(-17.4, 6.83) * mm, "end": v(-14.25, 6.83) * mm});
            skLineSegment(sketch, "E3024", {"start": v(-14.25, 6.83) * mm, "end": v(-11.1, 6.83) * mm});
            skLineSegment(sketch, "E3025", {"start": v(-11.1, 6.83) * mm, "end": v(-11.1, 6.95) * mm});
            skLineSegment(sketch, "E3026", {"start": v(-11.1, 6.95) * mm, "end": v(-11.1, 7.08) * mm});
            skLineSegment(sketch, "E3027", {"start": v(-11.1, 7.08) * mm, "end": v(-11.1, 7.2) * mm});
            skLineSegment(sketch, "E3028", {"start": v(-11.1, 7.2) * mm, "end": v(-11.1, 7.33) * mm});
            skLineSegment(sketch, "E3029", {"start": v(-11.1, 7.33) * mm, "end": v(-11.1, 7.45) * mm});
            skLineSegment(sketch, "E3030", {"start": v(-11.1, 7.45) * mm, "end": v(-11.1, 7.57) * mm});
            skLineSegment(sketch, "E3031", {"start": v(-11.1, 7.57) * mm, "end": v(-11.1, 7.7) * mm});
            skLineSegment(sketch, "E3032", {"start": v(-11.1, 7.7) * mm, "end": v(-11.1, 7.82) * mm});
            skLineSegment(sketch, "E3033", {"start": v(-11.1, 7.82) * mm, "end": v(-14.25, 7.82) * mm});
            skLineSegment(sketch, "E3034", {"start": v(-14.25, 7.82) * mm, "end": v(-17.4, 7.82) * mm});
            skLineSegment(sketch, "E3035", {"start": v(-17.4, 7.82) * mm, "end": v(-20.55, 7.82) * mm});
            skLineSegment(sketch, "E3036", {"start": v(-20.55, 7.82) * mm, "end": v(-23.7, 7.82) * mm});
            skLineSegment(sketch, "E3037", {"start": v(-23.7, 7.82) * mm, "end": v(-26.85, 7.82) * mm});
            skLineSegment(sketch, "E3038", {"start": v(-26.85, 7.82) * mm, "end": v(-30, 7.82) * mm});
            skLineSegment(sketch, "E3039", {"start": v(-30, 7.82) * mm, "end": v(-33.14, 7.82) * mm});
            skLineSegment(sketch, "E3040", {"start": v(-33.14, 7.82) * mm, "end": v(-36.3, 7.82) * mm});
            skLineSegment(sketch, "E3041", {"start": v(-36.3, 7.82) * mm, "end": v(-36.3, 7.7) * mm});
            skLineSegment(sketch, "E3042", {"start": v(-36.3, 7.7) * mm, "end": v(-36.3, 7.57) * mm});
            skLineSegment(sketch, "E3043", {"start": v(-36.3, 7.57) * mm, "end": v(-36.3, 7.45) * mm});
            skLineSegment(sketch, "E3044", {"start": v(-36.3, 7.45) * mm, "end": v(-36.3, 7.33) * mm});
            skLineSegment(sketch, "E3045", {"start": v(-36.3, 7.33) * mm, "end": v(-36.3, 7.2) * mm});
            skLineSegment(sketch, "E3046", {"start": v(-36.3, 7.2) * mm, "end": v(-36.3, 7.08) * mm});
            skLineSegment(sketch, "E3047", {"start": v(-36.3, 7.08) * mm, "end": v(-36.3, 6.95) * mm});
            skLineSegment(sketch, "E3048", {"start": v(-36.3, 6.95) * mm, "end": v(-36.3, 6.83) * mm});
            skLineSegment(sketch, "E3049", {"start": v(11.12, 6.83) * mm, "end": v(14.27, 6.83) * mm});
            skLineSegment(sketch, "E3050", {"start": v(14.27, 6.83) * mm, "end": v(17.42, 6.83) * mm});
            skLineSegment(sketch, "E3051", {"start": v(17.42, 6.83) * mm, "end": v(20.57, 6.83) * mm});
            skLineSegment(sketch, "E3052", {"start": v(20.57, 6.83) * mm, "end": v(23.72, 6.83) * mm});
            skLineSegment(sketch, "E3053", {"start": v(23.72, 6.83) * mm, "end": v(26.86, 6.83) * mm});
            skLineSegment(sketch, "E3054", {"start": v(26.86, 6.83) * mm, "end": v(30.01, 6.83) * mm});
            skLineSegment(sketch, "E3055", {"start": v(30.01, 6.83) * mm, "end": v(33.16, 6.83) * mm});
            skLineSegment(sketch, "E3056", {"start": v(33.16, 6.83) * mm, "end": v(36.3, 6.83) * mm});
            skLineSegment(sketch, "E3057", {"start": v(36.3, 6.83) * mm, "end": v(36.3, 6.95) * mm});
            skLineSegment(sketch, "E3058", {"start": v(36.3, 6.95) * mm, "end": v(36.3, 7.08) * mm});
            skLineSegment(sketch, "E3059", {"start": v(36.3, 7.08) * mm, "end": v(36.3, 7.2) * mm});
            skLineSegment(sketch, "E3060", {"start": v(36.3, 7.2) * mm, "end": v(36.3, 7.33) * mm});
            skLineSegment(sketch, "E3061", {"start": v(36.3, 7.33) * mm, "end": v(36.3, 7.45) * mm});
            skLineSegment(sketch, "E3062", {"start": v(36.3, 7.45) * mm, "end": v(36.3, 7.57) * mm});
            skLineSegment(sketch, "E3063", {"start": v(36.3, 7.57) * mm, "end": v(36.3, 7.7) * mm});
            skLineSegment(sketch, "E3064", {"start": v(36.3, 7.7) * mm, "end": v(36.3, 7.82) * mm});
            skLineSegment(sketch, "E3065", {"start": v(36.3, 7.82) * mm, "end": v(33.16, 7.82) * mm});
            skLineSegment(sketch, "E3066", {"start": v(33.16, 7.82) * mm, "end": v(30.01, 7.82) * mm});
            skLineSegment(sketch, "E3067", {"start": v(30.01, 7.82) * mm, "end": v(26.86, 7.82) * mm});
            skLineSegment(sketch, "E3068", {"start": v(26.86, 7.82) * mm, "end": v(23.72, 7.82) * mm});
            skLineSegment(sketch, "E3069", {"start": v(23.72, 7.82) * mm, "end": v(20.57, 7.82) * mm});
            skLineSegment(sketch, "E3070", {"start": v(20.57, 7.82) * mm, "end": v(17.42, 7.82) * mm});
            skLineSegment(sketch, "E3071", {"start": v(17.42, 7.82) * mm, "end": v(14.27, 7.82) * mm});
            skLineSegment(sketch, "E3072", {"start": v(14.27, 7.82) * mm, "end": v(11.12, 7.82) * mm});
            skLineSegment(sketch, "E3073", {"start": v(11.12, 7.82) * mm, "end": v(11.12, 7.7) * mm});
            skLineSegment(sketch, "E3074", {"start": v(11.12, 7.7) * mm, "end": v(11.12, 7.57) * mm});
            skLineSegment(sketch, "E3075", {"start": v(11.12, 7.57) * mm, "end": v(11.12, 7.45) * mm});
            skLineSegment(sketch, "E3076", {"start": v(11.12, 7.45) * mm, "end": v(11.12, 7.33) * mm});
            skLineSegment(sketch, "E3077", {"start": v(11.12, 7.33) * mm, "end": v(11.12, 7.2) * mm});
            skLineSegment(sketch, "E3078", {"start": v(11.12, 7.2) * mm, "end": v(11.12, 7.08) * mm});
            skLineSegment(sketch, "E3079", {"start": v(11.12, 7.08) * mm, "end": v(11.12, 6.95) * mm});
            skLineSegment(sketch, "E3080", {"start": v(11.12, 6.95) * mm, "end": v(11.12, 6.83) * mm});
            skLineSegment(sketch, "E3081", {"start": v(37.7, 18.1) * mm, "end": v(28.28, 18.1) * mm});
            skLineSegment(sketch, "E3082", {"start": v(28.28, 18.1) * mm, "end": v(18.85, 18.1) * mm});
            skLineSegment(sketch, "E3083", {"start": v(18.85, 18.1) * mm, "end": v(9.43, 18.1) * mm});
            skLineSegment(sketch, "E3084", {"start": v(9.43, 18.1) * mm, "end": v(0, 18.1) * mm});
            skLineSegment(sketch, "E3085", {"start": v(0, 18.1) * mm, "end": v(-9.43, 18.1) * mm});
            skLineSegment(sketch, "E3086", {"start": v(-9.43, 18.1) * mm, "end": v(-18.85, 18.1) * mm});
            skLineSegment(sketch, "E3087", {"start": v(-18.85, 18.1) * mm, "end": v(-28.28, 18.1) * mm});
            skLineSegment(sketch, "E3088", {"start": v(-28.28, 18.1) * mm, "end": v(-37.7, 18.1) * mm});
            skLineSegment(sketch, "E3089", {"start": v(-37.7, 18.1) * mm, "end": v(-37.7, 13.58) * mm});
            skLineSegment(sketch, "E3090", {"start": v(-37.7, 13.58) * mm, "end": v(-37.7, 9.05) * mm});
            skLineSegment(sketch, "E3091", {"start": v(-37.7, 9.05) * mm, "end": v(-37.7, 4.53) * mm});
            skLineSegment(sketch, "E3092", {"start": v(-37.7, 4.53) * mm, "end": v(-37.7, 0) * mm});
            skLineSegment(sketch, "E3093", {"start": v(-37.7, 0) * mm, "end": v(-37.7, -4.53) * mm});
            skLineSegment(sketch, "E3094", {"start": v(-37.7, -4.53) * mm, "end": v(-37.7, -9.05) * mm});
            skLineSegment(sketch, "E3095", {"start": v(-37.7, -9.05) * mm, "end": v(-37.7, -13.58) * mm});
            skLineSegment(sketch, "E3096", {"start": v(-37.7, -13.58) * mm, "end": v(-37.7, -18.1) * mm});
            skLineSegment(sketch, "E3097", {"start": v(-37.7, -18.1) * mm, "end": v(-28.28, -18.1) * mm});
            skLineSegment(sketch, "E3098", {"start": v(-28.28, -18.1) * mm, "end": v(-18.85, -18.1) * mm});
            skLineSegment(sketch, "E3099", {"start": v(-18.85, -18.1) * mm, "end": v(-9.43, -18.1) * mm});
            skLineSegment(sketch, "E3100", {"start": v(-9.43, -18.1) * mm, "end": v(0, -18.1) * mm});
            skLineSegment(sketch, "E3101", {"start": v(0, -18.1) * mm, "end": v(9.43, -18.1) * mm});
            skLineSegment(sketch, "E3102", {"start": v(9.43, -18.1) * mm, "end": v(18.85, -18.1) * mm});
            skLineSegment(sketch, "E3103", {"start": v(18.85, -18.1) * mm, "end": v(28.28, -18.1) * mm});
            skLineSegment(sketch, "E3104", {"start": v(28.28, -18.1) * mm, "end": v(37.7, -18.1) * mm});
            skLineSegment(sketch, "E3105", {"start": v(37.7, -18.1) * mm, "end": v(37.7, -13.58) * mm});
            skLineSegment(sketch, "E3106", {"start": v(37.7, -13.58) * mm, "end": v(37.7, -9.05) * mm});
            skLineSegment(sketch, "E3107", {"start": v(37.7, -9.05) * mm, "end": v(37.7, -4.53) * mm});
            skLineSegment(sketch, "E3108", {"start": v(37.7, -4.53) * mm, "end": v(37.7, 0) * mm});
            skLineSegment(sketch, "E3109", {"start": v(37.7, 0) * mm, "end": v(37.7, 4.53) * mm});
            skLineSegment(sketch, "E3110", {"start": v(37.7, 4.53) * mm, "end": v(37.7, 9.05) * mm});
            skLineSegment(sketch, "E3111", {"start": v(37.7, 9.05) * mm, "end": v(37.7, 13.58) * mm});
            skLineSegment(sketch, "E3112", {"start": v(37.7, 13.58) * mm, "end": v(37.7, 18.1) * mm});
            skLineSegment(sketch, "E3113", {"start": v(-15.43, 16.3) * mm, "end": v(-15.34, 16.3) * mm});
            skLineSegment(sketch, "E3114", {"start": v(-15.34, 16.3) * mm, "end": v(-15.24, 16.3) * mm});
            skLineSegment(sketch, "E3115", {"start": v(-15.24, 16.3) * mm, "end": v(-15.14, 16.3) * mm});
            skLineSegment(sketch, "E3116", {"start": v(-15.14, 16.3) * mm, "end": v(-15.05, 16.3) * mm});
            skLineSegment(sketch, "E3117", {"start": v(-15.05, 16.3) * mm, "end": v(-14.95, 16.3) * mm});
            skLineSegment(sketch, "E3118", {"start": v(-14.95, 16.3) * mm, "end": v(-14.85, 16.3) * mm});
            skLineSegment(sketch, "E3119", {"start": v(-14.85, 16.3) * mm, "end": v(-14.76, 16.3) * mm});
            skLineSegment(sketch, "E3120", {"start": v(-14.76, 16.3) * mm, "end": v(-14.66, 16.3) * mm});
            skLineSegment(sketch, "E3121", {"start": v(-14.66, 16.3) * mm, "end": v(-14.56, 16.3) * mm});
            skLineSegment(sketch, "E3122", {"start": v(-14.56, 16.3) * mm, "end": v(-14.47, 16.3) * mm});
            skLineSegment(sketch, "E3123", {"start": v(-14.47, 16.3) * mm, "end": v(-14.37, 16.3) * mm});
            skLineSegment(sketch, "E3124", {"start": v(-14.37, 16.3) * mm, "end": v(-14.27, 16.3) * mm});
            skLineSegment(sketch, "E3125", {"start": v(-14.27, 16.3) * mm, "end": v(-14.18, 16.3) * mm});
            skLineSegment(sketch, "E3126", {"start": v(-14.18, 16.3) * mm, "end": v(-14.08, 16.3) * mm});
            skLineSegment(sketch, "E3127", {"start": v(-14.08, 16.3) * mm, "end": v(-13.98, 16.3) * mm});
            skLineSegment(sketch, "E3128", {"start": v(-13.98, 16.3) * mm, "end": v(-13.89, 16.3) * mm});
            skLineSegment(sketch, "E3129", {"start": v(-13.89, 16.3) * mm, "end": v(-13.89, 16.06) * mm});
            skLineSegment(sketch, "E3130", {"start": v(-13.89, 16.06) * mm, "end": v(-13.89, 15.8) * mm});
            skLineSegment(sketch, "E3131", {"start": v(-13.89, 15.8) * mm, "end": v(-13.89, 15.56) * mm});
            skLineSegment(sketch, "E3132", {"start": v(-13.89, 15.56) * mm, "end": v(-13.89, 15.3) * mm});
            skLineSegment(sketch, "E3133", {"start": v(-13.89, 15.3) * mm, "end": v(-13.89, 15.05) * mm});
            skLineSegment(sketch, "E3134", {"start": v(-13.89, 15.05) * mm, "end": v(-13.89, 14.8) * mm});
            skLineSegment(sketch, "E3135", {"start": v(-13.89, 14.8) * mm, "end": v(-13.89, 14.55) * mm});
            skLineSegment(sketch, "E3136", {"start": v(-13.89, 14.55) * mm, "end": v(-13.89, 14.3) * mm});
            skLineSegment(sketch, "E3137", {"start": v(-13.89, 14.3) * mm, "end": v(-13.89, 14.05) * mm});
            skLineSegment(sketch, "E3138", {"start": v(-13.89, 14.05) * mm, "end": v(-13.89, 13.8) * mm});
            skLineSegment(sketch, "E3139", {"start": v(-13.89, 13.8) * mm, "end": v(-13.89, 13.55) * mm});
            skLineSegment(sketch, "E3140", {"start": v(-13.89, 13.55) * mm, "end": v(-13.89, 13.3) * mm});
            skLineSegment(sketch, "E3141", {"start": v(-13.89, 13.3) * mm, "end": v(-13.89, 13.05) * mm});
            skLineSegment(sketch, "E3142", {"start": v(-13.89, 13.05) * mm, "end": v(-13.89, 12.8) * mm});
            skLineSegment(sketch, "E3143", {"start": v(-13.89, 12.8) * mm, "end": v(-13.89, 12.55) * mm});
            skLineSegment(sketch, "E3144", {"start": v(-13.89, 12.55) * mm, "end": v(-13.89, 12.3) * mm});
            skLineSegment(sketch, "E3145", {"start": v(-13.89, 12.3) * mm, "end": v(-13.72, 12.3) * mm});
            skLineSegment(sketch, "E3146", {"start": v(-13.72, 12.3) * mm, "end": v(-13.55, 12.3) * mm});
            skLineSegment(sketch, "E3147", {"start": v(-13.55, 12.3) * mm, "end": v(-13.38, 12.3) * mm});
            skLineSegment(sketch, "E3148", {"start": v(-13.38, 12.3) * mm, "end": v(-13.2, 12.3) * mm});
            skLineSegment(sketch, "E3149", {"start": v(-13.2, 12.3) * mm, "end": v(-13.04, 12.3) * mm});
            skLineSegment(sketch, "E3150", {"start": v(-13.04, 12.3) * mm, "end": v(-12.87, 12.3) * mm});
            skLineSegment(sketch, "E3151", {"start": v(-12.87, 12.3) * mm, "end": v(-12.7, 12.3) * mm});
            skLineSegment(sketch, "E3152", {"start": v(-12.7, 12.3) * mm, "end": v(-12.53, 12.3) * mm});
            skLineSegment(sketch, "E3153", {"start": v(-12.53, 12.3) * mm, "end": v(-12.36, 12.3) * mm});
            skLineSegment(sketch, "E3154", {"start": v(-12.36, 12.3) * mm, "end": v(-12.2, 12.3) * mm});
            skLineSegment(sketch, "E3155", {"start": v(-12.2, 12.3) * mm, "end": v(-12.03, 12.3) * mm});
            skLineSegment(sketch, "E3156", {"start": v(-12.03, 12.3) * mm, "end": v(-11.86, 12.3) * mm});
            skLineSegment(sketch, "E3157", {"start": v(-11.86, 12.3) * mm, "end": v(-11.69, 12.3) * mm});
            skLineSegment(sketch, "E3158", {"start": v(-11.69, 12.3) * mm, "end": v(-11.52, 12.3) * mm});
            skLineSegment(sketch, "E3159", {"start": v(-11.52, 12.3) * mm, "end": v(-11.35, 12.3) * mm});
            skLineSegment(sketch, "E3160", {"start": v(-11.35, 12.3) * mm, "end": v(-11.18, 12.3) * mm});
            skLineSegment(sketch, "E3161", {"start": v(-11.18, 12.3) * mm, "end": v(-11.18, 12.22) * mm});
            skLineSegment(sketch, "E3162", {"start": v(-11.18, 12.22) * mm, "end": v(-11.18, 12.14) * mm});
            skLineSegment(sketch, "E3163", {"start": v(-11.18, 12.14) * mm, "end": v(-11.18, 12.06) * mm});
            skLineSegment(sketch, "E3164", {"start": v(-11.18, 12.06) * mm, "end": v(-11.18, 11.98) * mm});
            skLineSegment(sketch, "E3165", {"start": v(-11.18, 11.98) * mm, "end": v(-11.18, 11.9) * mm});
            skLineSegment(sketch, "E3166", {"start": v(-11.18, 11.9) * mm, "end": v(-11.18, 11.82) * mm});
            skLineSegment(sketch, "E3167", {"start": v(-11.18, 11.82) * mm, "end": v(-11.18, 11.74) * mm});
            skLineSegment(sketch, "E3168", {"start": v(-11.18, 11.74) * mm, "end": v(-11.18, 11.66) * mm});
            skLineSegment(sketch, "E3169", {"start": v(-11.18, 11.66) * mm, "end": v(-11.18, 11.58) * mm});
            skLineSegment(sketch, "E3170", {"start": v(-11.18, 11.58) * mm, "end": v(-11.18, 11.5) * mm});
            skLineSegment(sketch, "E3171", {"start": v(-11.18, 11.5) * mm, "end": v(-11.18, 11.42) * mm});
            skLineSegment(sketch, "E3172", {"start": v(-11.18, 11.42) * mm, "end": v(-11.18, 11.34) * mm});
            skLineSegment(sketch, "E3173", {"start": v(-11.18, 11.34) * mm, "end": v(-11.18, 11.26) * mm});
            skLineSegment(sketch, "E3174", {"start": v(-11.18, 11.26) * mm, "end": v(-11.18, 11.18) * mm});
            skLineSegment(sketch, "E3175", {"start": v(-11.18, 11.18) * mm, "end": v(-11.18, 11.1) * mm});
            skLineSegment(sketch, "E3176", {"start": v(-11.18, 11.1) * mm, "end": v(-11.18, 11.02) * mm});
            skLineSegment(sketch, "E3177", {"start": v(-11.18, 11.02) * mm, "end": v(-11.45, 11.02) * mm});
            skLineSegment(sketch, "E3178", {"start": v(-11.45, 11.02) * mm, "end": v(-11.71, 11.02) * mm});
            skLineSegment(sketch, "E3179", {"start": v(-11.71, 11.02) * mm, "end": v(-11.98, 11.02) * mm});
            skLineSegment(sketch, "E3180", {"start": v(-11.98, 11.02) * mm, "end": v(-12.24, 11.02) * mm});
            skLineSegment(sketch, "E3181", {"start": v(-12.24, 11.02) * mm, "end": v(-12.5, 11.02) * mm});
            skLineSegment(sketch, "E3182", {"start": v(-12.5, 11.02) * mm, "end": v(-12.78, 11.02) * mm});
            skLineSegment(sketch, "E3183", {"start": v(-12.78, 11.02) * mm, "end": v(-13.04, 11.02) * mm});
            skLineSegment(sketch, "E3184", {"start": v(-13.04, 11.02) * mm, "end": v(-13.3, 11.02) * mm});
            skLineSegment(sketch, "E3185", {"start": v(-13.3, 11.02) * mm, "end": v(-13.57, 11.02) * mm});
            skLineSegment(sketch, "E3186", {"start": v(-13.57, 11.02) * mm, "end": v(-13.84, 11.02) * mm});
            skLineSegment(sketch, "E3187", {"start": v(-13.84, 11.02) * mm, "end": v(-14.1, 11.02) * mm});
            skLineSegment(sketch, "E3188", {"start": v(-14.1, 11.02) * mm, "end": v(-14.37, 11.02) * mm});
            skLineSegment(sketch, "E3189", {"start": v(-14.37, 11.02) * mm, "end": v(-14.64, 11.02) * mm});
            skLineSegment(sketch, "E3190", {"start": v(-14.64, 11.02) * mm, "end": v(-14.9, 11.02) * mm});
            skLineSegment(sketch, "E3191", {"start": v(-14.9, 11.02) * mm, "end": v(-15.17, 11.02) * mm});
            skLineSegment(sketch, "E3192", {"start": v(-15.17, 11.02) * mm, "end": v(-15.43, 11.02) * mm});
            skLineSegment(sketch, "E3193", {"start": v(-15.43, 11.02) * mm, "end": v(-15.43, 11.35) * mm});
            skLineSegment(sketch, "E3194", {"start": v(-15.43, 11.35) * mm, "end": v(-15.43, 11.68) * mm});
            skLineSegment(sketch, "E3195", {"start": v(-15.43, 11.68) * mm, "end": v(-15.43, 12) * mm});
            skLineSegment(sketch, "E3196", {"start": v(-15.43, 12) * mm, "end": v(-15.43, 12.34) * mm});
            skLineSegment(sketch, "E3197", {"start": v(-15.43, 12.34) * mm, "end": v(-15.43, 12.67) * mm});
            skLineSegment(sketch, "E3198", {"start": v(-15.43, 12.67) * mm, "end": v(-15.43, 13) * mm});
            skLineSegment(sketch, "E3199", {"start": v(-15.43, 13) * mm, "end": v(-15.43, 13.33) * mm});
            skLineSegment(sketch, "E3200", {"start": v(-15.43, 13.33) * mm, "end": v(-15.43, 13.66) * mm});
            skLineSegment(sketch, "E3201", {"start": v(-15.43, 13.66) * mm, "end": v(-15.43, 14) * mm});
            skLineSegment(sketch, "E3202", {"start": v(-15.43, 14) * mm, "end": v(-15.43, 14.32) * mm});
            skLineSegment(sketch, "E3203", {"start": v(-15.43, 14.32) * mm, "end": v(-15.43, 14.65) * mm});
            skLineSegment(sketch, "E3204", {"start": v(-15.43, 14.65) * mm, "end": v(-15.43, 14.98) * mm});
            skLineSegment(sketch, "E3205", {"start": v(-15.43, 14.98) * mm, "end": v(-15.43, 15.31) * mm});
            skLineSegment(sketch, "E3206", {"start": v(-15.43, 15.31) * mm, "end": v(-15.43, 15.65) * mm});
            skLineSegment(sketch, "E3207", {"start": v(-15.43, 15.65) * mm, "end": v(-15.43, 15.98) * mm});
            skLineSegment(sketch, "E3208", {"start": v(-15.43, 15.98) * mm, "end": v(-15.43, 16.3) * mm});
            skLineSegment(sketch, "E3209", {"start": v(-10.52, 16.3) * mm, "end": v(-10.24, 16.3) * mm});
            skLineSegment(sketch, "E3210", {"start": v(-10.24, 16.3) * mm, "end": v(-9.95, 16.3) * mm});
            skLineSegment(sketch, "E3211", {"start": v(-9.95, 16.3) * mm, "end": v(-9.67, 16.3) * mm});
            skLineSegment(sketch, "E3212", {"start": v(-9.67, 16.3) * mm, "end": v(-9.4, 16.3) * mm});
            skLineSegment(sketch, "E3213", {"start": v(-9.4, 16.3) * mm, "end": v(-9.11, 16.3) * mm});
            skLineSegment(sketch, "E3214", {"start": v(-9.11, 16.3) * mm, "end": v(-8.83, 16.3) * mm});
            skLineSegment(sketch, "E3215", {"start": v(-8.83, 16.3) * mm, "end": v(-8.55, 16.3) * mm});
            skLineSegment(sketch, "E3216", {"start": v(-8.55, 16.3) * mm, "end": v(-8.27, 16.3) * mm});
            skLineSegment(sketch, "E3217", {"start": v(-8.27, 16.3) * mm, "end": v(-7.99, 16.3) * mm});
            skLineSegment(sketch, "E3218", {"start": v(-7.99, 16.3) * mm, "end": v(-7.7, 16.3) * mm});
            skLineSegment(sketch, "E3219", {"start": v(-7.7, 16.3) * mm, "end": v(-7.43, 16.3) * mm});
            skLineSegment(sketch, "E3220", {"start": v(-7.43, 16.3) * mm, "end": v(-7.14, 16.3) * mm});
            skLineSegment(sketch, "E3221", {"start": v(-7.14, 16.3) * mm, "end": v(-6.86, 16.3) * mm});
            skLineSegment(sketch, "E3222", {"start": v(-6.86, 16.3) * mm, "end": v(-6.58, 16.3) * mm});
            skLineSegment(sketch, "E3223", {"start": v(-6.58, 16.3) * mm, "end": v(-6.3, 16.3) * mm});
            skLineSegment(sketch, "E3224", {"start": v(-6.3, 16.3) * mm, "end": v(-6.02, 16.3) * mm});
            skLineSegment(sketch, "E3225", {"start": v(-6.02, 16.3) * mm, "end": v(-6.02, 16.23) * mm});
            skLineSegment(sketch, "E3226", {"start": v(-6.02, 16.23) * mm, "end": v(-6.02, 16.15) * mm});
            skLineSegment(sketch, "E3227", {"start": v(-6.02, 16.15) * mm, "end": v(-6.02, 16.07) * mm});
            skLineSegment(sketch, "E3228", {"start": v(-6.02, 16.07) * mm, "end": v(-6.02, 16) * mm});
            skLineSegment(sketch, "E3229", {"start": v(-6.02, 16) * mm, "end": v(-6.02, 15.92) * mm});
            skLineSegment(sketch, "E3230", {"start": v(-6.02, 15.92) * mm, "end": v(-6.02, 15.84) * mm});
            skLineSegment(sketch, "E3231", {"start": v(-6.02, 15.84) * mm, "end": v(-6.02, 15.76) * mm});
            skLineSegment(sketch, "E3232", {"start": v(-6.02, 15.76) * mm, "end": v(-6.02, 15.68) * mm});
            skLineSegment(sketch, "E3233", {"start": v(-6.02, 15.68) * mm, "end": v(-6.02, 15.6) * mm});
            skLineSegment(sketch, "E3234", {"start": v(-6.02, 15.6) * mm, "end": v(-6.02, 15.53) * mm});
            skLineSegment(sketch, "E3235", {"start": v(-6.02, 15.53) * mm, "end": v(-6.02, 15.45) * mm});
            skLineSegment(sketch, "E3236", {"start": v(-6.02, 15.45) * mm, "end": v(-6.02, 15.37) * mm});
            skLineSegment(sketch, "E3237", {"start": v(-6.02, 15.37) * mm, "end": v(-6.02, 15.3) * mm});
            skLineSegment(sketch, "E3238", {"start": v(-6.02, 15.3) * mm, "end": v(-6.02, 15.22) * mm});
            skLineSegment(sketch, "E3239", {"start": v(-6.02, 15.22) * mm, "end": v(-6.02, 15.14) * mm});
            skLineSegment(sketch, "E3240", {"start": v(-6.02, 15.14) * mm, "end": v(-6.02, 15.06) * mm});
            skLineSegment(sketch, "E3241", {"start": v(-6.02, 15.06) * mm, "end": v(-6.2, 15.06) * mm});
            skLineSegment(sketch, "E3242", {"start": v(-6.2, 15.06) * mm, "end": v(-6.4, 15.06) * mm});
            skLineSegment(sketch, "E3243", {"start": v(-6.4, 15.06) * mm, "end": v(-6.58, 15.06) * mm});
            skLineSegment(sketch, "E3244", {"start": v(-6.58, 15.06) * mm, "end": v(-6.76, 15.06) * mm});
            skLineSegment(sketch, "E3245", {"start": v(-6.76, 15.06) * mm, "end": v(-6.95, 15.06) * mm});
            skLineSegment(sketch, "E3246", {"start": v(-6.95, 15.06) * mm, "end": v(-7.13, 15.06) * mm});
            skLineSegment(sketch, "E3247", {"start": v(-7.13, 15.06) * mm, "end": v(-7.32, 15.06) * mm});
            skLineSegment(sketch, "E3248", {"start": v(-7.32, 15.06) * mm, "end": v(-7.5, 15.06) * mm});
            skLineSegment(sketch, "E3249", {"start": v(-7.5, 15.06) * mm, "end": v(-7.69, 15.06) * mm});
            skLineSegment(sketch, "E3250", {"start": v(-7.69, 15.06) * mm, "end": v(-7.87, 15.06) * mm});
            skLineSegment(sketch, "E3251", {"start": v(-7.87, 15.06) * mm, "end": v(-8.06, 15.06) * mm});
            skLineSegment(sketch, "E3252", {"start": v(-8.06, 15.06) * mm, "end": v(-8.24, 15.06) * mm});
            skLineSegment(sketch, "E3253", {"start": v(-8.24, 15.06) * mm, "end": v(-8.43, 15.06) * mm});
            skLineSegment(sketch, "E3254", {"start": v(-8.43, 15.06) * mm, "end": v(-8.61, 15.06) * mm});
            skLineSegment(sketch, "E3255", {"start": v(-8.61, 15.06) * mm, "end": v(-8.8, 15.06) * mm});
            skLineSegment(sketch, "E3256", {"start": v(-8.8, 15.06) * mm, "end": v(-8.98, 15.06) * mm});
            skLineSegment(sketch, "E3257", {"start": v(-8.98, 15.06) * mm, "end": v(-8.98, 15) * mm});
            skLineSegment(sketch, "E3258", {"start": v(-8.98, 15) * mm, "end": v(-8.98, 14.96) * mm});
            skLineSegment(sketch, "E3259", {"start": v(-8.98, 14.96) * mm, "end": v(-8.98, 14.9) * mm});
            skLineSegment(sketch, "E3260", {"start": v(-8.98, 14.9) * mm, "end": v(-8.98, 14.86) * mm});
            skLineSegment(sketch, "E3261", {"start": v(-8.98, 14.86) * mm, "end": v(-8.98, 14.8) * mm});
            skLineSegment(sketch, "E3262", {"start": v(-8.98, 14.8) * mm, "end": v(-8.98, 14.76) * mm});
            skLineSegment(sketch, "E3263", {"start": v(-8.98, 14.76) * mm, "end": v(-8.98, 14.7) * mm});
            skLineSegment(sketch, "E3264", {"start": v(-8.98, 14.7) * mm, "end": v(-8.98, 14.66) * mm});
            skLineSegment(sketch, "E3265", {"start": v(-8.98, 14.66) * mm, "end": v(-8.98, 14.6) * mm});
            skLineSegment(sketch, "E3266", {"start": v(-8.98, 14.6) * mm, "end": v(-8.98, 14.56) * mm});
            skLineSegment(sketch, "E3267", {"start": v(-8.98, 14.56) * mm, "end": v(-8.98, 14.5) * mm});
            skLineSegment(sketch, "E3268", {"start": v(-8.98, 14.5) * mm, "end": v(-8.98, 14.46) * mm});
            skLineSegment(sketch, "E3269", {"start": v(-8.98, 14.46) * mm, "end": v(-8.98, 14.4) * mm});
            skLineSegment(sketch, "E3270", {"start": v(-8.98, 14.4) * mm, "end": v(-8.98, 14.36) * mm});
            skLineSegment(sketch, "E3271", {"start": v(-8.98, 14.36) * mm, "end": v(-8.98, 14.3) * mm});
            skLineSegment(sketch, "E3272", {"start": v(-8.98, 14.3) * mm, "end": v(-8.98, 14.26) * mm});
            skLineSegment(sketch, "E3273", {"start": v(-8.98, 14.26) * mm, "end": v(-8.82, 14.26) * mm});
            skLineSegment(sketch, "E3274", {"start": v(-8.82, 14.26) * mm, "end": v(-8.65, 14.26) * mm});
            skLineSegment(sketch, "E3275", {"start": v(-8.65, 14.26) * mm, "end": v(-8.48, 14.26) * mm});
            skLineSegment(sketch, "E3276", {"start": v(-8.48, 14.26) * mm, "end": v(-8.31, 14.26) * mm});
            skLineSegment(sketch, "E3277", {"start": v(-8.31, 14.26) * mm, "end": v(-8.14, 14.26) * mm});
            skLineSegment(sketch, "E3278", {"start": v(-8.14, 14.26) * mm, "end": v(-7.98, 14.26) * mm});
            skLineSegment(sketch, "E3279", {"start": v(-7.98, 14.26) * mm, "end": v(-7.8, 14.26) * mm});
            skLineSegment(sketch, "E3280", {"start": v(-7.8, 14.26) * mm, "end": v(-7.64, 14.26) * mm});
            skLineSegment(sketch, "E3281", {"start": v(-7.64, 14.26) * mm, "end": v(-7.47, 14.26) * mm});
            skLineSegment(sketch, "E3282", {"start": v(-7.47, 14.26) * mm, "end": v(-7.3, 14.26) * mm});
            skLineSegment(sketch, "E3283", {"start": v(-7.3, 14.26) * mm, "end": v(-7.14, 14.26) * mm});
            skLineSegment(sketch, "E3284", {"start": v(-7.14, 14.26) * mm, "end": v(-6.97, 14.26) * mm});
            skLineSegment(sketch, "E3285", {"start": v(-6.97, 14.26) * mm, "end": v(-6.8, 14.26) * mm});
            skLineSegment(sketch, "E3286", {"start": v(-6.8, 14.26) * mm, "end": v(-6.64, 14.26) * mm});
            skLineSegment(sketch, "E3287", {"start": v(-6.64, 14.26) * mm, "end": v(-6.47, 14.26) * mm});
            skLineSegment(sketch, "E3288", {"start": v(-6.47, 14.26) * mm, "end": v(-6.3, 14.26) * mm});
            skLineSegment(sketch, "E3289", {"start": v(-6.3, 14.26) * mm, "end": v(-6.3, 14.19) * mm});
            skLineSegment(sketch, "E3290", {"start": v(-6.3, 14.19) * mm, "end": v(-6.3, 14.11) * mm});
            skLineSegment(sketch, "E3291", {"start": v(-6.3, 14.11) * mm, "end": v(-6.3, 14.04) * mm});
            skLineSegment(sketch, "E3292", {"start": v(-6.3, 14.04) * mm, "end": v(-6.3, 13.97) * mm});
            skLineSegment(sketch, "E3293", {"start": v(-6.3, 13.97) * mm, "end": v(-6.3, 13.9) * mm});
            skLineSegment(sketch, "E3294", {"start": v(-6.3, 13.9) * mm, "end": v(-6.3, 13.82) * mm});
            skLineSegment(sketch, "E3295", {"start": v(-6.3, 13.82) * mm, "end": v(-6.3, 13.75) * mm});
            skLineSegment(sketch, "E3296", {"start": v(-6.3, 13.75) * mm, "end": v(-6.3, 13.68) * mm});
            skLineSegment(sketch, "E3297", {"start": v(-6.3, 13.68) * mm, "end": v(-6.3, 13.6) * mm});
            skLineSegment(sketch, "E3298", {"start": v(-6.3, 13.6) * mm, "end": v(-6.3, 13.54) * mm});
            skLineSegment(sketch, "E3299", {"start": v(-6.3, 13.54) * mm, "end": v(-6.3, 13.46) * mm});
            skLineSegment(sketch, "E3300", {"start": v(-6.3, 13.46) * mm, "end": v(-6.3, 13.4) * mm});
            skLineSegment(sketch, "E3301", {"start": v(-6.3, 13.4) * mm, "end": v(-6.3, 13.32) * mm});
            skLineSegment(sketch, "E3302", {"start": v(-6.3, 13.32) * mm, "end": v(-6.3, 13.25) * mm});
            skLineSegment(sketch, "E3303", {"start": v(-6.3, 13.25) * mm, "end": v(-6.3, 13.17) * mm});
            skLineSegment(sketch, "E3304", {"start": v(-6.3, 13.17) * mm, "end": v(-6.3, 13.1) * mm});
            skLineSegment(sketch, "E3305", {"start": v(-6.3, 13.1) * mm, "end": v(-6.47, 13.1) * mm});
            skLineSegment(sketch, "E3306", {"start": v(-6.47, 13.1) * mm, "end": v(-6.64, 13.1) * mm});
            skLineSegment(sketch, "E3307", {"start": v(-6.64, 13.1) * mm, "end": v(-6.8, 13.1) * mm});
            skLineSegment(sketch, "E3308", {"start": v(-6.8, 13.1) * mm, "end": v(-6.97, 13.1) * mm});
            skLineSegment(sketch, "E3309", {"start": v(-6.97, 13.1) * mm, "end": v(-7.14, 13.1) * mm});
            skLineSegment(sketch, "E3310", {"start": v(-7.14, 13.1) * mm, "end": v(-7.3, 13.1) * mm});
            skLineSegment(sketch, "E3311", {"start": v(-7.3, 13.1) * mm, "end": v(-7.47, 13.1) * mm});
            skLineSegment(sketch, "E3312", {"start": v(-7.47, 13.1) * mm, "end": v(-7.64, 13.1) * mm});
            skLineSegment(sketch, "E3313", {"start": v(-7.64, 13.1) * mm, "end": v(-7.8, 13.1) * mm});
            skLineSegment(sketch, "E3314", {"start": v(-7.8, 13.1) * mm, "end": v(-7.98, 13.1) * mm});
            skLineSegment(sketch, "E3315", {"start": v(-7.98, 13.1) * mm, "end": v(-8.14, 13.1) * mm});
            skLineSegment(sketch, "E3316", {"start": v(-8.14, 13.1) * mm, "end": v(-8.31, 13.1) * mm});
            skLineSegment(sketch, "E3317", {"start": v(-8.31, 13.1) * mm, "end": v(-8.48, 13.1) * mm});
            skLineSegment(sketch, "E3318", {"start": v(-8.48, 13.1) * mm, "end": v(-8.65, 13.1) * mm});
            skLineSegment(sketch, "E3319", {"start": v(-8.65, 13.1) * mm, "end": v(-8.82, 13.1) * mm});
            skLineSegment(sketch, "E3320", {"start": v(-8.82, 13.1) * mm, "end": v(-8.98, 13.1) * mm});
            skLineSegment(sketch, "E3321", {"start": v(-8.98, 13.1) * mm, "end": v(-8.98, 13.05) * mm});
            skLineSegment(sketch, "E3322", {"start": v(-8.98, 13.05) * mm, "end": v(-8.98, 13) * mm});
            skLineSegment(sketch, "E3323", {"start": v(-8.98, 13) * mm, "end": v(-8.98, 12.94) * mm});
            skLineSegment(sketch, "E3324", {"start": v(-8.98, 12.94) * mm, "end": v(-8.98, 12.9) * mm});
            skLineSegment(sketch, "E3325", {"start": v(-8.98, 12.9) * mm, "end": v(-8.98, 12.84) * mm});
            skLineSegment(sketch, "E3326", {"start": v(-8.98, 12.84) * mm, "end": v(-8.98, 12.79) * mm});
            skLineSegment(sketch, "E3327", {"start": v(-8.98, 12.79) * mm, "end": v(-8.98, 12.73) * mm});
            skLineSegment(sketch, "E3328", {"start": v(-8.98, 12.73) * mm, "end": v(-8.98, 12.68) * mm});
            skLineSegment(sketch, "E3329", {"start": v(-8.98, 12.68) * mm, "end": v(-8.98, 12.63) * mm});
            skLineSegment(sketch, "E3330", {"start": v(-8.98, 12.63) * mm, "end": v(-8.98, 12.58) * mm});
            skLineSegment(sketch, "E3331", {"start": v(-8.98, 12.58) * mm, "end": v(-8.98, 12.52) * mm});
            skLineSegment(sketch, "E3332", {"start": v(-8.98, 12.52) * mm, "end": v(-8.98, 12.47) * mm});
            skLineSegment(sketch, "E3333", {"start": v(-8.98, 12.47) * mm, "end": v(-8.98, 12.42) * mm});
            skLineSegment(sketch, "E3334", {"start": v(-8.98, 12.42) * mm, "end": v(-8.98, 12.37) * mm});
            skLineSegment(sketch, "E3335", {"start": v(-8.98, 12.37) * mm, "end": v(-8.98, 12.32) * mm});
            skLineSegment(sketch, "E3336", {"start": v(-8.98, 12.32) * mm, "end": v(-8.98, 12.26) * mm});
            skLineSegment(sketch, "E3337", {"start": v(-8.98, 12.26) * mm, "end": v(-8.8, 12.26) * mm});
            skLineSegment(sketch, "E3338", {"start": v(-8.8, 12.26) * mm, "end": v(-8.6, 12.26) * mm});
            skLineSegment(sketch, "E3339", {"start": v(-8.6, 12.26) * mm, "end": v(-8.42, 12.26) * mm});
            skLineSegment(sketch, "E3340", {"start": v(-8.42, 12.26) * mm, "end": v(-8.23, 12.26) * mm});
            skLineSegment(sketch, "E3341", {"start": v(-8.23, 12.26) * mm, "end": v(-8.05, 12.26) * mm});
            skLineSegment(sketch, "E3342", {"start": v(-8.05, 12.26) * mm, "end": v(-7.86, 12.26) * mm});
            skLineSegment(sketch, "E3343", {"start": v(-7.86, 12.26) * mm, "end": v(-7.67, 12.26) * mm});
            skLineSegment(sketch, "E3344", {"start": v(-7.67, 12.26) * mm, "end": v(-7.48, 12.26) * mm});
            skLineSegment(sketch, "E3345", {"start": v(-7.48, 12.26) * mm, "end": v(-7.3, 12.26) * mm});
            skLineSegment(sketch, "E3346", {"start": v(-7.3, 12.26) * mm, "end": v(-7.1, 12.26) * mm});
            skLineSegment(sketch, "E3347", {"start": v(-7.1, 12.26) * mm, "end": v(-6.92, 12.26) * mm});
            skLineSegment(sketch, "E3348", {"start": v(-6.92, 12.26) * mm, "end": v(-6.73, 12.26) * mm});
            skLineSegment(sketch, "E3349", {"start": v(-6.73, 12.26) * mm, "end": v(-6.54, 12.26) * mm});
            skLineSegment(sketch, "E3350", {"start": v(-6.54, 12.26) * mm, "end": v(-6.36, 12.26) * mm});
            skLineSegment(sketch, "E3351", {"start": v(-6.36, 12.26) * mm, "end": v(-6.17, 12.26) * mm});
            skLineSegment(sketch, "E3352", {"start": v(-6.17, 12.26) * mm, "end": v(-5.98, 12.26) * mm});
            skLineSegment(sketch, "E3353", {"start": v(-5.98, 12.26) * mm, "end": v(-5.98, 12.18) * mm});
            skLineSegment(sketch, "E3354", {"start": v(-5.98, 12.18) * mm, "end": v(-5.98, 12.1) * mm});
            skLineSegment(sketch, "E3355", {"start": v(-5.98, 12.1) * mm, "end": v(-5.98, 12.03) * mm});
            skLineSegment(sketch, "E3356", {"start": v(-5.98, 12.03) * mm, "end": v(-5.98, 11.95) * mm});
            skLineSegment(sketch, "E3357", {"start": v(-5.98, 11.95) * mm, "end": v(-5.98, 11.87) * mm});
            skLineSegment(sketch, "E3358", {"start": v(-5.98, 11.87) * mm, "end": v(-5.98, 11.8) * mm});
            skLineSegment(sketch, "E3359", {"start": v(-5.98, 11.8) * mm, "end": v(-5.98, 11.72) * mm});
            skLineSegment(sketch, "E3360", {"start": v(-5.98, 11.72) * mm, "end": v(-5.98, 11.64) * mm});
            skLineSegment(sketch, "E3361", {"start": v(-5.98, 11.64) * mm, "end": v(-5.98, 11.56) * mm});
            skLineSegment(sketch, "E3362", {"start": v(-5.98, 11.56) * mm, "end": v(-5.98, 11.48) * mm});
            skLineSegment(sketch, "E3363", {"start": v(-5.98, 11.48) * mm, "end": v(-5.98, 11.4) * mm});
            skLineSegment(sketch, "E3364", {"start": v(-5.98, 11.4) * mm, "end": v(-5.98, 11.33) * mm});
            skLineSegment(sketch, "E3365", {"start": v(-5.98, 11.33) * mm, "end": v(-5.98, 11.25) * mm});
            skLineSegment(sketch, "E3366", {"start": v(-5.98, 11.25) * mm, "end": v(-5.98, 11.17) * mm});
            skLineSegment(sketch, "E3367", {"start": v(-5.98, 11.17) * mm, "end": v(-5.98, 11.1) * mm});
            skLineSegment(sketch, "E3368", {"start": v(-5.98, 11.1) * mm, "end": v(-5.98, 11.02) * mm});
            skLineSegment(sketch, "E3369", {"start": v(-5.98, 11.02) * mm, "end": v(-6.26, 11.02) * mm});
            skLineSegment(sketch, "E3370", {"start": v(-6.26, 11.02) * mm, "end": v(-6.55, 11.02) * mm});
            skLineSegment(sketch, "E3371", {"start": v(-6.55, 11.02) * mm, "end": v(-6.83, 11.02) * mm});
            skLineSegment(sketch, "E3372", {"start": v(-6.83, 11.02) * mm, "end": v(-7.11, 11.02) * mm});
            skLineSegment(sketch, "E3373", {"start": v(-7.11, 11.02) * mm, "end": v(-7.4, 11.02) * mm});
            skLineSegment(sketch, "E3374", {"start": v(-7.4, 11.02) * mm, "end": v(-7.68, 11.02) * mm});
            skLineSegment(sketch, "E3375", {"start": v(-7.68, 11.02) * mm, "end": v(-7.97, 11.02) * mm});
            skLineSegment(sketch, "E3376", {"start": v(-7.97, 11.02) * mm, "end": v(-8.25, 11.02) * mm});
            skLineSegment(sketch, "E3377", {"start": v(-8.25, 11.02) * mm, "end": v(-8.53, 11.02) * mm});
            skLineSegment(sketch, "E3378", {"start": v(-8.53, 11.02) * mm, "end": v(-8.82, 11.02) * mm});
            skLineSegment(sketch, "E3379", {"start": v(-8.82, 11.02) * mm, "end": v(-9.1, 11.02) * mm});
            skLineSegment(sketch, "E3380", {"start": v(-9.1, 11.02) * mm, "end": v(-9.38, 11.02) * mm});
            skLineSegment(sketch, "E3381", {"start": v(-9.38, 11.02) * mm, "end": v(-9.67, 11.02) * mm});
            skLineSegment(sketch, "E3382", {"start": v(-9.67, 11.02) * mm, "end": v(-9.95, 11.02) * mm});
            skLineSegment(sketch, "E3383", {"start": v(-9.95, 11.02) * mm, "end": v(-10.23, 11.02) * mm});
            skLineSegment(sketch, "E3384", {"start": v(-10.23, 11.02) * mm, "end": v(-10.52, 11.02) * mm});
            skLineSegment(sketch, "E3385", {"start": v(-10.52, 11.02) * mm, "end": v(-10.52, 11.35) * mm});
            skLineSegment(sketch, "E3386", {"start": v(-10.52, 11.35) * mm, "end": v(-10.52, 11.68) * mm});
            skLineSegment(sketch, "E3387", {"start": v(-10.52, 11.68) * mm, "end": v(-10.52, 12) * mm});
            skLineSegment(sketch, "E3388", {"start": v(-10.52, 12) * mm, "end": v(-10.52, 12.34) * mm});
            skLineSegment(sketch, "E3389", {"start": v(-10.52, 12.34) * mm, "end": v(-10.52, 12.67) * mm});
            skLineSegment(sketch, "E3390", {"start": v(-10.52, 12.67) * mm, "end": v(-10.52, 13) * mm});
            skLineSegment(sketch, "E3391", {"start": v(-10.52, 13) * mm, "end": v(-10.52, 13.33) * mm});
            skLineSegment(sketch, "E3392", {"start": v(-10.52, 13.33) * mm, "end": v(-10.52, 13.66) * mm});
            skLineSegment(sketch, "E3393", {"start": v(-10.52, 13.66) * mm, "end": v(-10.52, 14) * mm});
            skLineSegment(sketch, "E3394", {"start": v(-10.52, 14) * mm, "end": v(-10.52, 14.32) * mm});
            skLineSegment(sketch, "E3395", {"start": v(-10.52, 14.32) * mm, "end": v(-10.52, 14.65) * mm});
            skLineSegment(sketch, "E3396", {"start": v(-10.52, 14.65) * mm, "end": v(-10.52, 14.98) * mm});
            skLineSegment(sketch, "E3397", {"start": v(-10.52, 14.98) * mm, "end": v(-10.52, 15.31) * mm});
            skLineSegment(sketch, "E3398", {"start": v(-10.52, 15.31) * mm, "end": v(-10.52, 15.65) * mm});
            skLineSegment(sketch, "E3399", {"start": v(-10.52, 15.65) * mm, "end": v(-10.52, 15.98) * mm});
            skLineSegment(sketch, "E3400", {"start": v(-10.52, 15.98) * mm, "end": v(-10.52, 16.3) * mm});
            skLineSegment(sketch, "E3401", {"start": v(7.77, 13.65) * mm, "end": v(7.77, 13.65) * mm});
            skLineSegment(sketch, "E3402", {"start": v(7.77, 13.65) * mm, "end": v(7.77, 13.66) * mm});
            skLineSegment(sketch, "E3403", {"start": v(7.77, 13.66) * mm, "end": v(7.77, 13.66) * mm});
            skLineSegment(sketch, "E3404", {"start": v(7.77, 13.66) * mm, "end": v(7.76, 13.8) * mm});
            skLineSegment(sketch, "E3405", {"start": v(7.76, 13.8) * mm, "end": v(7.74, 13.94) * mm});
            skLineSegment(sketch, "E3406", {"start": v(7.74, 13.94) * mm, "end": v(7.7, 14.08) * mm});
            skLineSegment(sketch, "E3407", {"start": v(7.7, 14.08) * mm, "end": v(7.66, 14.2) * mm});
            skLineSegment(sketch, "E3408", {"start": v(7.66, 14.2) * mm, "end": v(7.6, 14.33) * mm});
            skLineSegment(sketch, "E3409", {"start": v(7.6, 14.33) * mm, "end": v(7.54, 14.45) * mm});
            skLineSegment(sketch, "E3410", {"start": v(7.54, 14.45) * mm, "end": v(7.46, 14.56) * mm});
            skLineSegment(sketch, "E3411", {"start": v(7.46, 14.56) * mm, "end": v(7.37, 14.66) * mm});
            skLineSegment(sketch, "E3412", {"start": v(7.37, 14.66) * mm, "end": v(7.27, 14.76) * mm});
            skLineSegment(sketch, "E3413", {"start": v(7.27, 14.76) * mm, "end": v(7.16, 14.84) * mm});
            skLineSegment(sketch, "E3414", {"start": v(7.16, 14.84) * mm, "end": v(7.04, 14.91) * mm});
            skLineSegment(sketch, "E3415", {"start": v(7.04, 14.91) * mm, "end": v(6.92, 14.97) * mm});
            skLineSegment(sketch, "E3416", {"start": v(6.92, 14.97) * mm, "end": v(6.78, 15.02) * mm});
            skLineSegment(sketch, "E3417", {"start": v(6.78, 15.02) * mm, "end": v(6.64, 15.06) * mm});
            skLineSegment(sketch, "E3418", {"start": v(6.64, 15.06) * mm, "end": v(6.49, 15.08) * mm});
            skLineSegment(sketch, "E3419", {"start": v(6.49, 15.08) * mm, "end": v(6.33, 15.09) * mm});
            skLineSegment(sketch, "E3420", {"start": v(6.33, 15.09) * mm, "end": v(6.18, 15.08) * mm});
            skLineSegment(sketch, "E3421", {"start": v(6.18, 15.08) * mm, "end": v(6.03, 15.06) * mm});
            skLineSegment(sketch, "E3422", {"start": v(6.03, 15.06) * mm, "end": v(5.89, 15.02) * mm});
            skLineSegment(sketch, "E3423", {"start": v(5.89, 15.02) * mm, "end": v(5.75, 14.98) * mm});
            skLineSegment(sketch, "E3424", {"start": v(5.75, 14.98) * mm, "end": v(5.63, 14.92) * mm});
            skLineSegment(sketch, "E3425", {"start": v(5.63, 14.92) * mm, "end": v(5.51, 14.84) * mm});
            skLineSegment(sketch, "E3426", {"start": v(5.51, 14.84) * mm, "end": v(5.4, 14.76) * mm});
            skLineSegment(sketch, "E3427", {"start": v(5.4, 14.76) * mm, "end": v(5.3, 14.67) * mm});
            skLineSegment(sketch, "E3428", {"start": v(5.3, 14.67) * mm, "end": v(5.22, 14.57) * mm});
            skLineSegment(sketch, "E3429", {"start": v(5.22, 14.57) * mm, "end": v(5.14, 14.46) * mm});
            skLineSegment(sketch, "E3430", {"start": v(5.14, 14.46) * mm, "end": v(5.08, 14.34) * mm});
            skLineSegment(sketch, "E3431", {"start": v(5.08, 14.34) * mm, "end": v(5.02, 14.22) * mm});
            skLineSegment(sketch, "E3432", {"start": v(5.02, 14.22) * mm, "end": v(4.98, 14.1) * mm});
            skLineSegment(sketch, "E3433", {"start": v(4.98, 14.1) * mm, "end": v(4.94, 13.96) * mm});
            skLineSegment(sketch, "E3434", {"start": v(4.94, 13.96) * mm, "end": v(4.92, 13.82) * mm});
            skLineSegment(sketch, "E3435", {"start": v(4.92, 13.82) * mm, "end": v(4.92, 13.68) * mm});
            skLineSegment(sketch, "E3436", {"start": v(4.92, 13.68) * mm, "end": v(4.92, 13.68) * mm});
            skLineSegment(sketch, "E3437", {"start": v(4.92, 13.68) * mm, "end": v(4.92, 13.67) * mm});
            skLineSegment(sketch, "E3438", {"start": v(4.92, 13.67) * mm, "end": v(4.92, 13.67) * mm});
            skLineSegment(sketch, "E3439", {"start": v(4.92, 13.67) * mm, "end": v(4.92, 13.66) * mm});
            skLineSegment(sketch, "E3440", {"start": v(4.92, 13.66) * mm, "end": v(4.92, 13.66) * mm});
            skLineSegment(sketch, "E3441", {"start": v(4.92, 13.66) * mm, "end": v(4.92, 13.52) * mm});
            skLineSegment(sketch, "E3442", {"start": v(4.92, 13.52) * mm, "end": v(4.94, 13.38) * mm});
            skLineSegment(sketch, "E3443", {"start": v(4.94, 13.38) * mm, "end": v(4.98, 13.25) * mm});
            skLineSegment(sketch, "E3444", {"start": v(4.98, 13.25) * mm, "end": v(5.02, 13.12) * mm});
            skLineSegment(sketch, "E3445", {"start": v(5.02, 13.12) * mm, "end": v(5.08, 13) * mm});
            skLineSegment(sketch, "E3446", {"start": v(5.08, 13) * mm, "end": v(5.15, 12.87) * mm});
            skLineSegment(sketch, "E3447", {"start": v(5.15, 12.87) * mm, "end": v(5.23, 12.76) * mm});
            skLineSegment(sketch, "E3448", {"start": v(5.23, 12.76) * mm, "end": v(5.32, 12.66) * mm});
            skLineSegment(sketch, "E3449", {"start": v(5.32, 12.66) * mm, "end": v(5.41, 12.57) * mm});
            skLineSegment(sketch, "E3450", {"start": v(5.41, 12.57) * mm, "end": v(5.52, 12.48) * mm});
            skLineSegment(sketch, "E3451", {"start": v(5.52, 12.48) * mm, "end": v(5.64, 12.4) * mm});
            skLineSegment(sketch, "E3452", {"start": v(5.64, 12.4) * mm, "end": v(5.77, 12.35) * mm});
            skLineSegment(sketch, "E3453", {"start": v(5.77, 12.35) * mm, "end": v(5.9, 12.3) * mm});
            skLineSegment(sketch, "E3454", {"start": v(5.9, 12.3) * mm, "end": v(6.04, 12.26) * mm});
            skLineSegment(sketch, "E3455", {"start": v(6.04, 12.26) * mm, "end": v(6.2, 12.24) * mm});
            skLineSegment(sketch, "E3456", {"start": v(6.2, 12.24) * mm, "end": v(6.35, 12.23) * mm});
            skLineSegment(sketch, "E3457", {"start": v(6.35, 12.23) * mm, "end": v(6.5, 12.24) * mm});
            skLineSegment(sketch, "E3458", {"start": v(6.5, 12.24) * mm, "end": v(6.65, 12.26) * mm});
            skLineSegment(sketch, "E3459", {"start": v(6.65, 12.26) * mm, "end": v(6.8, 12.3) * mm});
            skLineSegment(sketch, "E3460", {"start": v(6.8, 12.3) * mm, "end": v(6.93, 12.35) * mm});
            skLineSegment(sketch, "E3461", {"start": v(6.93, 12.35) * mm, "end": v(7.06, 12.4) * mm});
            skLineSegment(sketch, "E3462", {"start": v(7.06, 12.4) * mm, "end": v(7.17, 12.48) * mm});
            skLineSegment(sketch, "E3463", {"start": v(7.17, 12.48) * mm, "end": v(7.28, 12.56) * mm});
            skLineSegment(sketch, "E3464", {"start": v(7.28, 12.56) * mm, "end": v(7.38, 12.65) * mm});
            skLineSegment(sketch, "E3465", {"start": v(7.38, 12.65) * mm, "end": v(7.47, 12.75) * mm});
            skLineSegment(sketch, "E3466", {"start": v(7.47, 12.75) * mm, "end": v(7.54, 12.86) * mm});
            skLineSegment(sketch, "E3467", {"start": v(7.54, 12.86) * mm, "end": v(7.61, 12.98) * mm});
            skLineSegment(sketch, "E3468", {"start": v(7.61, 12.98) * mm, "end": v(7.67, 13.1) * mm});
            skLineSegment(sketch, "E3469", {"start": v(7.67, 13.1) * mm, "end": v(7.71, 13.23) * mm});
            skLineSegment(sketch, "E3470", {"start": v(7.71, 13.23) * mm, "end": v(7.74, 13.37) * mm});
            skLineSegment(sketch, "E3471", {"start": v(7.74, 13.37) * mm, "end": v(7.76, 13.5) * mm});
            skLineSegment(sketch, "E3472", {"start": v(7.76, 13.5) * mm, "end": v(7.77, 13.65) * mm});
            skLineSegment(sketch, "E3473", {"start": v(3.33, 13.65) * mm, "end": v(3.33, 13.65) * mm});
            skLineSegment(sketch, "E3474", {"start": v(3.33, 13.65) * mm, "end": v(3.33, 13.66) * mm});
            skLineSegment(sketch, "E3475", {"start": v(3.33, 13.66) * mm, "end": v(3.33, 13.66) * mm});
            skLineSegment(sketch, "E3476", {"start": v(3.33, 13.66) * mm, "end": v(3.34, 13.94) * mm});
            skLineSegment(sketch, "E3477", {"start": v(3.34, 13.94) * mm, "end": v(3.39, 14.22) * mm});
            skLineSegment(sketch, "E3478", {"start": v(3.39, 14.22) * mm, "end": v(3.46, 14.48) * mm});
            skLineSegment(sketch, "E3479", {"start": v(3.46, 14.48) * mm, "end": v(3.56, 14.73) * mm});
            skLineSegment(sketch, "E3480", {"start": v(3.56, 14.73) * mm, "end": v(3.68, 14.97) * mm});
            skLineSegment(sketch, "E3481", {"start": v(3.68, 14.97) * mm, "end": v(3.83, 15.2) * mm});
            skLineSegment(sketch, "E3482", {"start": v(3.83, 15.2) * mm, "end": v(4, 15.41) * mm});
            skLineSegment(sketch, "E3483", {"start": v(4, 15.41) * mm, "end": v(4.2, 15.6) * mm});
            skLineSegment(sketch, "E3484", {"start": v(4.2, 15.6) * mm, "end": v(4.4, 15.78) * mm});
            skLineSegment(sketch, "E3485", {"start": v(4.4, 15.78) * mm, "end": v(4.63, 15.94) * mm});
            skLineSegment(sketch, "E3486", {"start": v(4.63, 15.94) * mm, "end": v(4.88, 16.08) * mm});
            skLineSegment(sketch, "E3487", {"start": v(4.88, 16.08) * mm, "end": v(5.15, 16.2) * mm});
            skLineSegment(sketch, "E3488", {"start": v(5.15, 16.2) * mm, "end": v(5.43, 16.29) * mm});
            skLineSegment(sketch, "E3489", {"start": v(5.43, 16.29) * mm, "end": v(5.72, 16.36) * mm});
            skLineSegment(sketch, "E3490", {"start": v(5.72, 16.36) * mm, "end": v(6.03, 16.4) * mm});
            skLineSegment(sketch, "E3491", {"start": v(6.03, 16.4) * mm, "end": v(6.35, 16.41) * mm});
            skLineSegment(sketch, "E3492", {"start": v(6.35, 16.41) * mm, "end": v(6.67, 16.4) * mm});
            skLineSegment(sketch, "E3493", {"start": v(6.67, 16.4) * mm, "end": v(6.97, 16.36) * mm});
            skLineSegment(sketch, "E3494", {"start": v(6.97, 16.36) * mm, "end": v(7.27, 16.3) * mm});
            skLineSegment(sketch, "E3495", {"start": v(7.27, 16.3) * mm, "end": v(7.54, 16.2) * mm});
            skLineSegment(sketch, "E3496", {"start": v(7.54, 16.2) * mm, "end": v(7.8, 16.08) * mm});
            skLineSegment(sketch, "E3497", {"start": v(7.8, 16.08) * mm, "end": v(8.06, 15.95) * mm});
            skLineSegment(sketch, "E3498", {"start": v(8.06, 15.95) * mm, "end": v(8.29, 15.8) * mm});
            skLineSegment(sketch, "E3499", {"start": v(8.29, 15.8) * mm, "end": v(8.5, 15.61) * mm});
            skLineSegment(sketch, "E3500", {"start": v(8.5, 15.61) * mm, "end": v(8.69, 15.42) * mm});
            skLineSegment(sketch, "E3501", {"start": v(8.69, 15.42) * mm, "end": v(8.85, 15.21) * mm});
            skLineSegment(sketch, "E3502", {"start": v(8.85, 15.21) * mm, "end": v(9, 14.98) * mm});
            skLineSegment(sketch, "E3503", {"start": v(9, 14.98) * mm, "end": v(9.12, 14.74) * mm});
            skLineSegment(sketch, "E3504", {"start": v(9.12, 14.74) * mm, "end": v(9.22, 14.5) * mm});
            skLineSegment(sketch, "E3505", {"start": v(9.22, 14.5) * mm, "end": v(9.3, 14.23) * mm});
            skLineSegment(sketch, "E3506", {"start": v(9.3, 14.23) * mm, "end": v(9.34, 13.96) * mm});
            skLineSegment(sketch, "E3507", {"start": v(9.34, 13.96) * mm, "end": v(9.35, 13.68) * mm});
            skLineSegment(sketch, "E3508", {"start": v(9.35, 13.68) * mm, "end": v(9.35, 13.68) * mm});
            skLineSegment(sketch, "E3509", {"start": v(9.35, 13.68) * mm, "end": v(9.35, 13.67) * mm});
            skLineSegment(sketch, "E3510", {"start": v(9.35, 13.67) * mm, "end": v(9.35, 13.67) * mm});
            skLineSegment(sketch, "E3511", {"start": v(9.35, 13.67) * mm, "end": v(9.35, 13.66) * mm});
            skLineSegment(sketch, "E3512", {"start": v(9.35, 13.66) * mm, "end": v(9.35, 13.66) * mm});
            skLineSegment(sketch, "E3513", {"start": v(9.35, 13.66) * mm, "end": v(9.34, 13.38) * mm});
            skLineSegment(sketch, "E3514", {"start": v(9.34, 13.38) * mm, "end": v(9.3, 13.1) * mm});
            skLineSegment(sketch, "E3515", {"start": v(9.3, 13.1) * mm, "end": v(9.22, 12.84) * mm});
            skLineSegment(sketch, "E3516", {"start": v(9.22, 12.84) * mm, "end": v(9.12, 12.59) * mm});
            skLineSegment(sketch, "E3517", {"start": v(9.12, 12.59) * mm, "end": v(9, 12.35) * mm});
            skLineSegment(sketch, "E3518", {"start": v(9, 12.35) * mm, "end": v(8.85, 12.12) * mm});
            skLineSegment(sketch, "E3519", {"start": v(8.85, 12.12) * mm, "end": v(8.68, 11.91) * mm});
            skLineSegment(sketch, "E3520", {"start": v(8.68, 11.91) * mm, "end": v(8.49, 11.72) * mm});
            skLineSegment(sketch, "E3521", {"start": v(8.49, 11.72) * mm, "end": v(8.28, 11.54) * mm});
            skLineSegment(sketch, "E3522", {"start": v(8.28, 11.54) * mm, "end": v(8.04, 11.38) * mm});
            skLineSegment(sketch, "E3523", {"start": v(8.04, 11.38) * mm, "end": v(7.8, 11.24) * mm});
            skLineSegment(sketch, "E3524", {"start": v(7.8, 11.24) * mm, "end": v(7.53, 11.13) * mm});
            skLineSegment(sketch, "E3525", {"start": v(7.53, 11.13) * mm, "end": v(7.25, 11.03) * mm});
            skLineSegment(sketch, "E3526", {"start": v(7.25, 11.03) * mm, "end": v(6.96, 10.97) * mm});
            skLineSegment(sketch, "E3527", {"start": v(6.96, 10.97) * mm, "end": v(6.65, 10.92) * mm});
            skLineSegment(sketch, "E3528", {"start": v(6.65, 10.92) * mm, "end": v(6.33, 10.9) * mm});
            skLineSegment(sketch, "E3529", {"start": v(6.33, 10.9) * mm, "end": v(6.01, 10.92) * mm});
            skLineSegment(sketch, "E3530", {"start": v(6.01, 10.92) * mm, "end": v(5.7, 10.96) * mm});
            skLineSegment(sketch, "E3531", {"start": v(5.7, 10.96) * mm, "end": v(5.41, 11.03) * mm});
            skLineSegment(sketch, "E3532", {"start": v(5.41, 11.03) * mm, "end": v(5.13, 11.12) * mm});
            skLineSegment(sketch, "E3533", {"start": v(5.13, 11.12) * mm, "end": v(4.87, 11.24) * mm});
            skLineSegment(sketch, "E3534", {"start": v(4.87, 11.24) * mm, "end": v(4.62, 11.37) * mm});
            skLineSegment(sketch, "E3535", {"start": v(4.62, 11.37) * mm, "end": v(4.4, 11.53) * mm});
            skLineSegment(sketch, "E3536", {"start": v(4.4, 11.53) * mm, "end": v(4.18, 11.7) * mm});
            skLineSegment(sketch, "E3537", {"start": v(4.18, 11.7) * mm, "end": v(4, 11.9) * mm});
            skLineSegment(sketch, "E3538", {"start": v(4, 11.9) * mm, "end": v(3.82, 12.11) * mm});
            skLineSegment(sketch, "E3539", {"start": v(3.82, 12.11) * mm, "end": v(3.68, 12.34) * mm});
            skLineSegment(sketch, "E3540", {"start": v(3.68, 12.34) * mm, "end": v(3.56, 12.58) * mm});
            skLineSegment(sketch, "E3541", {"start": v(3.56, 12.58) * mm, "end": v(3.46, 12.83) * mm});
            skLineSegment(sketch, "E3542", {"start": v(3.46, 12.83) * mm, "end": v(3.39, 13.1) * mm});
            skLineSegment(sketch, "E3543", {"start": v(3.39, 13.1) * mm, "end": v(3.34, 13.36) * mm});
            skLineSegment(sketch, "E3544", {"start": v(3.34, 13.36) * mm, "end": v(3.33, 13.65) * mm});
            skLineSegment(sketch, "E3545", {"start": v(10.16, 16.3) * mm, "end": v(10.25, 16.3) * mm});
            skLineSegment(sketch, "E3546", {"start": v(10.25, 16.3) * mm, "end": v(10.34, 16.3) * mm});
            skLineSegment(sketch, "E3547", {"start": v(10.34, 16.3) * mm, "end": v(10.43, 16.3) * mm});
            skLineSegment(sketch, "E3548", {"start": v(10.43, 16.3) * mm, "end": v(10.52, 16.3) * mm});
            skLineSegment(sketch, "E3549", {"start": v(10.52, 16.3) * mm, "end": v(10.6, 16.3) * mm});
            skLineSegment(sketch, "E3550", {"start": v(10.6, 16.3) * mm, "end": v(10.7, 16.3) * mm});
            skLineSegment(sketch, "E3551", {"start": v(10.7, 16.3) * mm, "end": v(10.79, 16.3) * mm});
            skLineSegment(sketch, "E3552", {"start": v(10.79, 16.3) * mm, "end": v(10.88, 16.3) * mm});
            skLineSegment(sketch, "E3553", {"start": v(10.88, 16.3) * mm, "end": v(10.97, 16.3) * mm});
            skLineSegment(sketch, "E3554", {"start": v(10.97, 16.3) * mm, "end": v(11.06, 16.3) * mm});
            skLineSegment(sketch, "E3555", {"start": v(11.06, 16.3) * mm, "end": v(11.15, 16.3) * mm});
            skLineSegment(sketch, "E3556", {"start": v(11.15, 16.3) * mm, "end": v(11.24, 16.3) * mm});
            skLineSegment(sketch, "E3557", {"start": v(11.24, 16.3) * mm, "end": v(11.33, 16.3) * mm});
            skLineSegment(sketch, "E3558", {"start": v(11.33, 16.3) * mm, "end": v(11.42, 16.3) * mm});
            skLineSegment(sketch, "E3559", {"start": v(11.42, 16.3) * mm, "end": v(11.51, 16.3) * mm});
            skLineSegment(sketch, "E3560", {"start": v(11.51, 16.3) * mm, "end": v(11.6, 16.3) * mm});
            skLineSegment(sketch, "E3561", {"start": v(11.6, 16.3) * mm, "end": v(11.75, 16.13) * mm});
            skLineSegment(sketch, "E3562", {"start": v(11.75, 16.13) * mm, "end": v(11.89, 15.96) * mm});
            skLineSegment(sketch, "E3563", {"start": v(11.89, 15.96) * mm, "end": v(12.03, 15.78) * mm});
            skLineSegment(sketch, "E3564", {"start": v(12.03, 15.78) * mm, "end": v(12.18, 15.6) * mm});
            skLineSegment(sketch, "E3565", {"start": v(12.18, 15.6) * mm, "end": v(12.32, 15.43) * mm});
            skLineSegment(sketch, "E3566", {"start": v(12.32, 15.43) * mm, "end": v(12.46, 15.26) * mm});
            skLineSegment(sketch, "E3567", {"start": v(12.46, 15.26) * mm, "end": v(12.6, 15.08) * mm});
            skLineSegment(sketch, "E3568", {"start": v(12.6, 15.08) * mm, "end": v(12.75, 14.9) * mm});
            skLineSegment(sketch, "E3569", {"start": v(12.75, 14.9) * mm, "end": v(12.9, 14.73) * mm});
            skLineSegment(sketch, "E3570", {"start": v(12.9, 14.73) * mm, "end": v(13.04, 14.56) * mm});
            skLineSegment(sketch, "E3571", {"start": v(13.04, 14.56) * mm, "end": v(13.18, 14.38) * mm});
            skLineSegment(sketch, "E3572", {"start": v(13.18, 14.38) * mm, "end": v(13.33, 14.2) * mm});
            skLineSegment(sketch, "E3573", {"start": v(13.33, 14.2) * mm, "end": v(13.47, 14.03) * mm});
            skLineSegment(sketch, "E3574", {"start": v(13.47, 14.03) * mm, "end": v(13.61, 13.86) * mm});
            skLineSegment(sketch, "E3575", {"start": v(13.61, 13.86) * mm, "end": v(13.76, 13.68) * mm});
            skLineSegment(sketch, "E3576", {"start": v(13.76, 13.68) * mm, "end": v(13.9, 13.51) * mm});
            skLineSegment(sketch, "E3577", {"start": v(13.9, 13.51) * mm, "end": v(13.9, 13.68) * mm});
            skLineSegment(sketch, "E3578", {"start": v(13.9, 13.68) * mm, "end": v(13.9, 13.86) * mm});
            skLineSegment(sketch, "E3579", {"start": v(13.9, 13.86) * mm, "end": v(13.9, 14.03) * mm});
            skLineSegment(sketch, "E3580", {"start": v(13.9, 14.03) * mm, "end": v(13.9, 14.2) * mm});
            skLineSegment(sketch, "E3581", {"start": v(13.9, 14.2) * mm, "end": v(13.9, 14.38) * mm});
            skLineSegment(sketch, "E3582", {"start": v(13.9, 14.38) * mm, "end": v(13.9, 14.56) * mm});
            skLineSegment(sketch, "E3583", {"start": v(13.9, 14.56) * mm, "end": v(13.9, 14.73) * mm});
            skLineSegment(sketch, "E3584", {"start": v(13.9, 14.73) * mm, "end": v(13.9, 14.9) * mm});
            skLineSegment(sketch, "E3585", {"start": v(13.9, 14.9) * mm, "end": v(13.9, 15.08) * mm});
            skLineSegment(sketch, "E3586", {"start": v(13.9, 15.08) * mm, "end": v(13.9, 15.26) * mm});
            skLineSegment(sketch, "E3587", {"start": v(13.9, 15.26) * mm, "end": v(13.9, 15.43) * mm});
            skLineSegment(sketch, "E3588", {"start": v(13.9, 15.43) * mm, "end": v(13.9, 15.6) * mm});
            skLineSegment(sketch, "E3589", {"start": v(13.9, 15.6) * mm, "end": v(13.9, 15.78) * mm});
            skLineSegment(sketch, "E3590", {"start": v(13.9, 15.78) * mm, "end": v(13.9, 15.96) * mm});
            skLineSegment(sketch, "E3591", {"start": v(13.9, 15.96) * mm, "end": v(13.9, 16.13) * mm});
            skLineSegment(sketch, "E3592", {"start": v(13.9, 16.13) * mm, "end": v(13.9, 16.3) * mm});
            skLineSegment(sketch, "E3593", {"start": v(13.9, 16.3) * mm, "end": v(14, 16.3) * mm});
            skLineSegment(sketch, "E3594", {"start": v(14, 16.3) * mm, "end": v(14.1, 16.3) * mm});
            skLineSegment(sketch, "E3595", {"start": v(14.1, 16.3) * mm, "end": v(14.19, 16.3) * mm});
            skLineSegment(sketch, "E3596", {"start": v(14.19, 16.3) * mm, "end": v(14.28, 16.3) * mm});
            skLineSegment(sketch, "E3597", {"start": v(14.28, 16.3) * mm, "end": v(14.38, 16.3) * mm});
            skLineSegment(sketch, "E3598", {"start": v(14.38, 16.3) * mm, "end": v(14.48, 16.3) * mm});
            skLineSegment(sketch, "E3599", {"start": v(14.48, 16.3) * mm, "end": v(14.57, 16.3) * mm});
            skLineSegment(sketch, "E3600", {"start": v(14.57, 16.3) * mm, "end": v(14.67, 16.3) * mm});
            skLineSegment(sketch, "E3601", {"start": v(14.67, 16.3) * mm, "end": v(14.76, 16.3) * mm});
            skLineSegment(sketch, "E3602", {"start": v(14.76, 16.3) * mm, "end": v(14.86, 16.3) * mm});
            skLineSegment(sketch, "E3603", {"start": v(14.86, 16.3) * mm, "end": v(14.96, 16.3) * mm});
            skLineSegment(sketch, "E3604", {"start": v(14.96, 16.3) * mm, "end": v(15.05, 16.3) * mm});
            skLineSegment(sketch, "E3605", {"start": v(15.05, 16.3) * mm, "end": v(15.15, 16.3) * mm});
            skLineSegment(sketch, "E3606", {"start": v(15.15, 16.3) * mm, "end": v(15.24, 16.3) * mm});
            skLineSegment(sketch, "E3607", {"start": v(15.24, 16.3) * mm, "end": v(15.34, 16.3) * mm});
            skLineSegment(sketch, "E3608", {"start": v(15.34, 16.3) * mm, "end": v(15.44, 16.3) * mm});
            skLineSegment(sketch, "E3609", {"start": v(15.44, 16.3) * mm, "end": v(15.44, 15.98) * mm});
            skLineSegment(sketch, "E3610", {"start": v(15.44, 15.98) * mm, "end": v(15.44, 15.65) * mm});
            skLineSegment(sketch, "E3611", {"start": v(15.44, 15.65) * mm, "end": v(15.44, 15.31) * mm});
            skLineSegment(sketch, "E3612", {"start": v(15.44, 15.31) * mm, "end": v(15.44, 14.98) * mm});
            skLineSegment(sketch, "E3613", {"start": v(15.44, 14.98) * mm, "end": v(15.44, 14.65) * mm});
            skLineSegment(sketch, "E3614", {"start": v(15.44, 14.65) * mm, "end": v(15.44, 14.32) * mm});
            skLineSegment(sketch, "E3615", {"start": v(15.44, 14.32) * mm, "end": v(15.44, 14) * mm});
            skLineSegment(sketch, "E3616", {"start": v(15.44, 14) * mm, "end": v(15.44, 13.66) * mm});
            skLineSegment(sketch, "E3617", {"start": v(15.44, 13.66) * mm, "end": v(15.44, 13.33) * mm});
            skLineSegment(sketch, "E3618", {"start": v(15.44, 13.33) * mm, "end": v(15.44, 13) * mm});
            skLineSegment(sketch, "E3619", {"start": v(15.44, 13) * mm, "end": v(15.44, 12.67) * mm});
            skLineSegment(sketch, "E3620", {"start": v(15.44, 12.67) * mm, "end": v(15.44, 12.34) * mm});
            skLineSegment(sketch, "E3621", {"start": v(15.44, 12.34) * mm, "end": v(15.44, 12) * mm});
            skLineSegment(sketch, "E3622", {"start": v(15.44, 12) * mm, "end": v(15.44, 11.68) * mm});
            skLineSegment(sketch, "E3623", {"start": v(15.44, 11.68) * mm, "end": v(15.44, 11.35) * mm});
            skLineSegment(sketch, "E3624", {"start": v(15.44, 11.35) * mm, "end": v(15.44, 11.02) * mm});
            skLineSegment(sketch, "E3625", {"start": v(15.44, 11.02) * mm, "end": v(15.35, 11.02) * mm});
            skLineSegment(sketch, "E3626", {"start": v(15.35, 11.02) * mm, "end": v(15.27, 11.02) * mm});
            skLineSegment(sketch, "E3627", {"start": v(15.27, 11.02) * mm, "end": v(15.18, 11.02) * mm});
            skLineSegment(sketch, "E3628", {"start": v(15.18, 11.02) * mm, "end": v(15.1, 11.02) * mm});
            skLineSegment(sketch, "E3629", {"start": v(15.1, 11.02) * mm, "end": v(15.01, 11.02) * mm});
            skLineSegment(sketch, "E3630", {"start": v(15.01, 11.02) * mm, "end": v(14.93, 11.02) * mm});
            skLineSegment(sketch, "E3631", {"start": v(14.93, 11.02) * mm, "end": v(14.84, 11.02) * mm});
            skLineSegment(sketch, "E3632", {"start": v(14.84, 11.02) * mm, "end": v(14.76, 11.02) * mm});
            skLineSegment(sketch, "E3633", {"start": v(14.76, 11.02) * mm, "end": v(14.67, 11.02) * mm});
            skLineSegment(sketch, "E3634", {"start": v(14.67, 11.02) * mm, "end": v(14.59, 11.02) * mm});
            skLineSegment(sketch, "E3635", {"start": v(14.59, 11.02) * mm, "end": v(14.5, 11.02) * mm});
            skLineSegment(sketch, "E3636", {"start": v(14.5, 11.02) * mm, "end": v(14.42, 11.02) * mm});
            skLineSegment(sketch, "E3637", {"start": v(14.42, 11.02) * mm, "end": v(14.33, 11.02) * mm});
            skLineSegment(sketch, "E3638", {"start": v(14.33, 11.02) * mm, "end": v(14.25, 11.02) * mm});
            skLineSegment(sketch, "E3639", {"start": v(14.25, 11.02) * mm, "end": v(14.16, 11.02) * mm});
            skLineSegment(sketch, "E3640", {"start": v(14.16, 11.02) * mm, "end": v(14.08, 11.02) * mm});
            skLineSegment(sketch, "E3641", {"start": v(14.08, 11.02) * mm, "end": v(13.93, 11.2) * mm});
            skLineSegment(sketch, "E3642", {"start": v(13.93, 11.2) * mm, "end": v(13.78, 11.38) * mm});
            skLineSegment(sketch, "E3643", {"start": v(13.78, 11.38) * mm, "end": v(13.63, 11.56) * mm});
            skLineSegment(sketch, "E3644", {"start": v(13.63, 11.56) * mm, "end": v(13.48, 11.74) * mm});
            skLineSegment(sketch, "E3645", {"start": v(13.48, 11.74) * mm, "end": v(13.33, 11.92) * mm});
            skLineSegment(sketch, "E3646", {"start": v(13.33, 11.92) * mm, "end": v(13.18, 12.1) * mm});
            skLineSegment(sketch, "E3647", {"start": v(13.18, 12.1) * mm, "end": v(13.03, 12.29) * mm});
            skLineSegment(sketch, "E3648", {"start": v(13.03, 12.29) * mm, "end": v(12.88, 12.47) * mm});
            skLineSegment(sketch, "E3649", {"start": v(12.88, 12.47) * mm, "end": v(12.73, 12.65) * mm});
            skLineSegment(sketch, "E3650", {"start": v(12.73, 12.65) * mm, "end": v(12.59, 12.83) * mm});
            skLineSegment(sketch, "E3651", {"start": v(12.59, 12.83) * mm, "end": v(12.44, 13.01) * mm});
            skLineSegment(sketch, "E3652", {"start": v(12.44, 13.01) * mm, "end": v(12.29, 13.2) * mm});
            skLineSegment(sketch, "E3653", {"start": v(12.29, 13.2) * mm, "end": v(12.14, 13.37) * mm});
            skLineSegment(sketch, "E3654", {"start": v(12.14, 13.37) * mm, "end": v(11.99, 13.56) * mm});
            skLineSegment(sketch, "E3655", {"start": v(11.99, 13.56) * mm, "end": v(11.84, 13.74) * mm});
            skLineSegment(sketch, "E3656", {"start": v(11.84, 13.74) * mm, "end": v(11.69, 13.92) * mm});
            skLineSegment(sketch, "E3657", {"start": v(11.69, 13.92) * mm, "end": v(11.69, 13.74) * mm});
            skLineSegment(sketch, "E3658", {"start": v(11.69, 13.74) * mm, "end": v(11.69, 13.56) * mm});
            skLineSegment(sketch, "E3659", {"start": v(11.69, 13.56) * mm, "end": v(11.69, 13.37) * mm});
            skLineSegment(sketch, "E3660", {"start": v(11.69, 13.37) * mm, "end": v(11.69, 13.2) * mm});
            skLineSegment(sketch, "E3661", {"start": v(11.69, 13.2) * mm, "end": v(11.69, 13.01) * mm});
            skLineSegment(sketch, "E3662", {"start": v(11.69, 13.01) * mm, "end": v(11.69, 12.83) * mm});
            skLineSegment(sketch, "E3663", {"start": v(11.69, 12.83) * mm, "end": v(11.69, 12.65) * mm});
            skLineSegment(sketch, "E3664", {"start": v(11.69, 12.65) * mm, "end": v(11.69, 12.47) * mm});
            skLineSegment(sketch, "E3665", {"start": v(11.69, 12.47) * mm, "end": v(11.69, 12.29) * mm});
            skLineSegment(sketch, "E3666", {"start": v(11.69, 12.29) * mm, "end": v(11.69, 12.1) * mm});
            skLineSegment(sketch, "E3667", {"start": v(11.69, 12.1) * mm, "end": v(11.69, 11.92) * mm});
            skLineSegment(sketch, "E3668", {"start": v(11.69, 11.92) * mm, "end": v(11.69, 11.74) * mm});
            skLineSegment(sketch, "E3669", {"start": v(11.69, 11.74) * mm, "end": v(11.69, 11.56) * mm});
            skLineSegment(sketch, "E3670", {"start": v(11.69, 11.56) * mm, "end": v(11.69, 11.38) * mm});
            skLineSegment(sketch, "E3671", {"start": v(11.69, 11.38) * mm, "end": v(11.69, 11.2) * mm});
            skLineSegment(sketch, "E3672", {"start": v(11.69, 11.2) * mm, "end": v(11.69, 11.02) * mm});
            skLineSegment(sketch, "E3673", {"start": v(11.69, 11.02) * mm, "end": v(11.6, 11.02) * mm});
            skLineSegment(sketch, "E3674", {"start": v(11.6, 11.02) * mm, "end": v(11.5, 11.02) * mm});
            skLineSegment(sketch, "E3675", {"start": v(11.5, 11.02) * mm, "end": v(11.4, 11.02) * mm});
            skLineSegment(sketch, "E3676", {"start": v(11.4, 11.02) * mm, "end": v(11.3, 11.02) * mm});
            skLineSegment(sketch, "E3677", {"start": v(11.3, 11.02) * mm, "end": v(11.21, 11.02) * mm});
            skLineSegment(sketch, "E3678", {"start": v(11.21, 11.02) * mm, "end": v(11.11, 11.02) * mm});
            skLineSegment(sketch, "E3679", {"start": v(11.11, 11.02) * mm, "end": v(11.02, 11.02) * mm});
            skLineSegment(sketch, "E3680", {"start": v(11.02, 11.02) * mm, "end": v(10.92, 11.02) * mm});
            skLineSegment(sketch, "E3681", {"start": v(10.92, 11.02) * mm, "end": v(10.83, 11.02) * mm});
            skLineSegment(sketch, "E3682", {"start": v(10.83, 11.02) * mm, "end": v(10.73, 11.02) * mm});
            skLineSegment(sketch, "E3683", {"start": v(10.73, 11.02) * mm, "end": v(10.64, 11.02) * mm});
            skLineSegment(sketch, "E3684", {"start": v(10.64, 11.02) * mm, "end": v(10.54, 11.02) * mm});
            skLineSegment(sketch, "E3685", {"start": v(10.54, 11.02) * mm, "end": v(10.44, 11.02) * mm});
            skLineSegment(sketch, "E3686", {"start": v(10.44, 11.02) * mm, "end": v(10.35, 11.02) * mm});
            skLineSegment(sketch, "E3687", {"start": v(10.35, 11.02) * mm, "end": v(10.25, 11.02) * mm});
            skLineSegment(sketch, "E3688", {"start": v(10.25, 11.02) * mm, "end": v(10.16, 11.02) * mm});
            skLineSegment(sketch, "E3689", {"start": v(10.16, 11.02) * mm, "end": v(10.16, 11.35) * mm});
            skLineSegment(sketch, "E3690", {"start": v(10.16, 11.35) * mm, "end": v(10.16, 11.68) * mm});
            skLineSegment(sketch, "E3691", {"start": v(10.16, 11.68) * mm, "end": v(10.16, 12) * mm});
            skLineSegment(sketch, "E3692", {"start": v(10.16, 12) * mm, "end": v(10.16, 12.34) * mm});
            skLineSegment(sketch, "E3693", {"start": v(10.16, 12.34) * mm, "end": v(10.16, 12.67) * mm});
            skLineSegment(sketch, "E3694", {"start": v(10.16, 12.67) * mm, "end": v(10.16, 13) * mm});
            skLineSegment(sketch, "E3695", {"start": v(10.16, 13) * mm, "end": v(10.16, 13.33) * mm});
            skLineSegment(sketch, "E3696", {"start": v(10.16, 13.33) * mm, "end": v(10.16, 13.66) * mm});
            skLineSegment(sketch, "E3697", {"start": v(10.16, 13.66) * mm, "end": v(10.16, 14) * mm});
            skLineSegment(sketch, "E3698", {"start": v(10.16, 14) * mm, "end": v(10.16, 14.32) * mm});
            skLineSegment(sketch, "E3699", {"start": v(10.16, 14.32) * mm, "end": v(10.16, 14.65) * mm});
            skLineSegment(sketch, "E3700", {"start": v(10.16, 14.65) * mm, "end": v(10.16, 14.98) * mm});
            skLineSegment(sketch, "E3701", {"start": v(10.16, 14.98) * mm, "end": v(10.16, 15.31) * mm});
            skLineSegment(sketch, "E3702", {"start": v(10.16, 15.31) * mm, "end": v(10.16, 15.65) * mm});
            skLineSegment(sketch, "E3703", {"start": v(10.16, 15.65) * mm, "end": v(10.16, 15.98) * mm});
            skLineSegment(sketch, "E3704", {"start": v(10.16, 15.98) * mm, "end": v(10.16, 16.3) * mm});
            skLineSegment(sketch, "E3705", {"start": v(-2.88, 13.03) * mm, "end": v(-2.78, 13.03) * mm});
            skLineSegment(sketch, "E3706", {"start": v(-2.78, 13.03) * mm, "end": v(-2.69, 13.03) * mm});
            skLineSegment(sketch, "E3707", {"start": v(-2.69, 13.03) * mm, "end": v(-2.6, 13.03) * mm});
            skLineSegment(sketch, "E3708", {"start": v(-2.6, 13.03) * mm, "end": v(-2.5, 13.03) * mm});
            skLineSegment(sketch, "E3709", {"start": v(-2.5, 13.03) * mm, "end": v(-2.4, 13.03) * mm});
            skLineSegment(sketch, "E3710", {"start": v(-2.4, 13.03) * mm, "end": v(-2.32, 13.03) * mm});
            skLineSegment(sketch, "E3711", {"start": v(-2.32, 13.03) * mm, "end": v(-2.22, 13.03) * mm});
            skLineSegment(sketch, "E3712", {"start": v(-2.22, 13.03) * mm, "end": v(-2.13, 13.03) * mm});
            skLineSegment(sketch, "E3713", {"start": v(-2.13, 13.03) * mm, "end": v(-2.03, 13.03) * mm});
            skLineSegment(sketch, "E3714", {"start": v(-2.03, 13.03) * mm, "end": v(-1.94, 13.03) * mm});
            skLineSegment(sketch, "E3715", {"start": v(-1.94, 13.03) * mm, "end": v(-1.85, 13.03) * mm});
            skLineSegment(sketch, "E3716", {"start": v(-1.85, 13.03) * mm, "end": v(-1.75, 13.03) * mm});
            skLineSegment(sketch, "E3717", {"start": v(-1.75, 13.03) * mm, "end": v(-1.66, 13.03) * mm});
            skLineSegment(sketch, "E3718", {"start": v(-1.66, 13.03) * mm, "end": v(-1.57, 13.03) * mm});
            skLineSegment(sketch, "E3719", {"start": v(-1.57, 13.03) * mm, "end": v(-1.47, 13.03) * mm});
            skLineSegment(sketch, "E3720", {"start": v(-1.47, 13.03) * mm, "end": v(-1.38, 13.03) * mm});
            skLineSegment(sketch, "E3721", {"start": v(-1.38, 13.03) * mm, "end": v(-1.38, 13) * mm});
            skLineSegment(sketch, "E3722", {"start": v(-1.38, 13) * mm, "end": v(-1.38, 12.95) * mm});
            skLineSegment(sketch, "E3723", {"start": v(-1.38, 12.95) * mm, "end": v(-1.38, 12.91) * mm});
            skLineSegment(sketch, "E3724", {"start": v(-1.38, 12.91) * mm, "end": v(-1.38, 12.87) * mm});
            skLineSegment(sketch, "E3725", {"start": v(-1.38, 12.87) * mm, "end": v(-1.38, 12.83) * mm});
            skLineSegment(sketch, "E3726", {"start": v(-1.38, 12.83) * mm, "end": v(-1.38, 12.8) * mm});
            skLineSegment(sketch, "E3727", {"start": v(-1.38, 12.8) * mm, "end": v(-1.38, 12.75) * mm});
            skLineSegment(sketch, "E3728", {"start": v(-1.38, 12.75) * mm, "end": v(-1.38, 12.71) * mm});
            skLineSegment(sketch, "E3729", {"start": v(-1.38, 12.71) * mm, "end": v(-1.38, 12.67) * mm});
            skLineSegment(sketch, "E3730", {"start": v(-1.38, 12.67) * mm, "end": v(-1.38, 12.63) * mm});
            skLineSegment(sketch, "E3731", {"start": v(-1.38, 12.63) * mm, "end": v(-1.38, 12.6) * mm});
            skLineSegment(sketch, "E3732", {"start": v(-1.38, 12.6) * mm, "end": v(-1.38, 12.55) * mm});
            skLineSegment(sketch, "E3733", {"start": v(-1.38, 12.55) * mm, "end": v(-1.38, 12.51) * mm});
            skLineSegment(sketch, "E3734", {"start": v(-1.38, 12.51) * mm, "end": v(-1.38, 12.47) * mm});
            skLineSegment(sketch, "E3735", {"start": v(-1.38, 12.47) * mm, "end": v(-1.38, 12.43) * mm});
            skLineSegment(sketch, "E3736", {"start": v(-1.38, 12.43) * mm, "end": v(-1.38, 12.4) * mm});
            skLineSegment(sketch, "E3737", {"start": v(-1.38, 12.4) * mm, "end": v(-1.42, 12.36) * mm});
            skLineSegment(sketch, "E3738", {"start": v(-1.42, 12.36) * mm, "end": v(-1.47, 12.34) * mm});
            skLineSegment(sketch, "E3739", {"start": v(-1.47, 12.34) * mm, "end": v(-1.52, 12.32) * mm});
            skLineSegment(sketch, "E3740", {"start": v(-1.52, 12.32) * mm, "end": v(-1.56, 12.3) * mm});
            skLineSegment(sketch, "E3741", {"start": v(-1.56, 12.3) * mm, "end": v(-1.61, 12.28) * mm});
            skLineSegment(sketch, "E3742", {"start": v(-1.61, 12.28) * mm, "end": v(-1.66, 12.26) * mm});
            skLineSegment(sketch, "E3743", {"start": v(-1.66, 12.26) * mm, "end": v(-1.72, 12.24) * mm});
            skLineSegment(sketch, "E3744", {"start": v(-1.72, 12.24) * mm, "end": v(-1.77, 12.23) * mm});
            skLineSegment(sketch, "E3745", {"start": v(-1.77, 12.23) * mm, "end": v(-1.83, 12.21) * mm});
            skLineSegment(sketch, "E3746", {"start": v(-1.83, 12.21) * mm, "end": v(-1.89, 12.2) * mm});
            skLineSegment(sketch, "E3747", {"start": v(-1.89, 12.2) * mm, "end": v(-1.95, 12.2) * mm});
            skLineSegment(sketch, "E3748", {"start": v(-1.95, 12.2) * mm, "end": v(-2, 12.19) * mm});
            skLineSegment(sketch, "E3749", {"start": v(-2, 12.19) * mm, "end": v(-2.07, 12.18) * mm});
            skLineSegment(sketch, "E3750", {"start": v(-2.07, 12.18) * mm, "end": v(-2.14, 12.18) * mm});
            skLineSegment(sketch, "E3751", {"start": v(-2.14, 12.18) * mm, "end": v(-2.2, 12.17) * mm});
            skLineSegment(sketch, "E3752", {"start": v(-2.2, 12.17) * mm, "end": v(-2.27, 12.17) * mm});
            skLineSegment(sketch, "E3753", {"start": v(-2.27, 12.17) * mm, "end": v(-2.44, 12.18) * mm});
            skLineSegment(sketch, "E3754", {"start": v(-2.44, 12.18) * mm, "end": v(-2.6, 12.2) * mm});
            skLineSegment(sketch, "E3755", {"start": v(-2.6, 12.2) * mm, "end": v(-2.74, 12.23) * mm});
            skLineSegment(sketch, "E3756", {"start": v(-2.74, 12.23) * mm, "end": v(-2.88, 12.28) * mm});
            skLineSegment(sketch, "E3757", {"start": v(-2.88, 12.28) * mm, "end": v(-3.02, 12.34) * mm});
            skLineSegment(sketch, "E3758", {"start": v(-3.02, 12.34) * mm, "end": v(-3.14, 12.41) * mm});
            skLineSegment(sketch, "E3759", {"start": v(-3.14, 12.41) * mm, "end": v(-3.26, 12.5) * mm});
            skLineSegment(sketch, "E3760", {"start": v(-3.26, 12.5) * mm, "end": v(-3.36, 12.58) * mm});
            skLineSegment(sketch, "E3761", {"start": v(-3.36, 12.58) * mm, "end": v(-3.46, 12.69) * mm});
            skLineSegment(sketch, "E3762", {"start": v(-3.46, 12.69) * mm, "end": v(-3.54, 12.8) * mm});
            skLineSegment(sketch, "E3763", {"start": v(-3.54, 12.8) * mm, "end": v(-3.62, 12.92) * mm});
            skLineSegment(sketch, "E3764", {"start": v(-3.62, 12.92) * mm, "end": v(-3.68, 13.05) * mm});
            skLineSegment(sketch, "E3765", {"start": v(-3.68, 13.05) * mm, "end": v(-3.73, 13.19) * mm});
            skLineSegment(sketch, "E3766", {"start": v(-3.73, 13.19) * mm, "end": v(-3.76, 13.33) * mm});
            skLineSegment(sketch, "E3767", {"start": v(-3.76, 13.33) * mm, "end": v(-3.78, 13.48) * mm});
            skLineSegment(sketch, "E3768", {"start": v(-3.78, 13.48) * mm, "end": v(-3.8, 13.64) * mm});
            skLineSegment(sketch, "E3769", {"start": v(-3.8, 13.64) * mm, "end": v(-3.8, 13.64) * mm});
            skLineSegment(sketch, "E3770", {"start": v(-3.8, 13.64) * mm, "end": v(-3.8, 13.65) * mm});
            skLineSegment(sketch, "E3771", {"start": v(-3.8, 13.65) * mm, "end": v(-3.8, 13.65) * mm});
            skLineSegment(sketch, "E3772", {"start": v(-3.8, 13.65) * mm, "end": v(-3.78, 13.8) * mm});
            skLineSegment(sketch, "E3773", {"start": v(-3.78, 13.8) * mm, "end": v(-3.76, 13.95) * mm});
            skLineSegment(sketch, "E3774", {"start": v(-3.76, 13.95) * mm, "end": v(-3.73, 14.09) * mm});
            skLineSegment(sketch, "E3775", {"start": v(-3.73, 14.09) * mm, "end": v(-3.68, 14.22) * mm});
            skLineSegment(sketch, "E3776", {"start": v(-3.68, 14.22) * mm, "end": v(-3.62, 14.35) * mm});
            skLineSegment(sketch, "E3777", {"start": v(-3.62, 14.35) * mm, "end": v(-3.55, 14.47) * mm});
            skLineSegment(sketch, "E3778", {"start": v(-3.55, 14.47) * mm, "end": v(-3.47, 14.58) * mm});
            skLineSegment(sketch, "E3779", {"start": v(-3.47, 14.58) * mm, "end": v(-3.38, 14.68) * mm});
            skLineSegment(sketch, "E3780", {"start": v(-3.38, 14.68) * mm, "end": v(-3.28, 14.78) * mm});
            skLineSegment(sketch, "E3781", {"start": v(-3.28, 14.78) * mm, "end": v(-3.17, 14.86) * mm});
            skLineSegment(sketch, "E3782", {"start": v(-3.17, 14.86) * mm, "end": v(-3.05, 14.93) * mm});
            skLineSegment(sketch, "E3783", {"start": v(-3.05, 14.93) * mm, "end": v(-2.92, 15) * mm});
            skLineSegment(sketch, "E3784", {"start": v(-2.92, 15) * mm, "end": v(-2.8, 15.04) * mm});
            skLineSegment(sketch, "E3785", {"start": v(-2.8, 15.04) * mm, "end": v(-2.65, 15.08) * mm});
            skLineSegment(sketch, "E3786", {"start": v(-2.65, 15.08) * mm, "end": v(-2.51, 15.1) * mm});
            skLineSegment(sketch, "E3787", {"start": v(-2.51, 15.1) * mm, "end": v(-2.36, 15.1) * mm});
            skLineSegment(sketch, "E3788", {"start": v(-2.36, 15.1) * mm, "end": v(-2.29, 15.1) * mm});
            skLineSegment(sketch, "E3789", {"start": v(-2.29, 15.1) * mm, "end": v(-2.22, 15.1) * mm});
            skLineSegment(sketch, "E3790", {"start": v(-2.22, 15.1) * mm, "end": v(-2.15, 15.1) * mm});
            skLineSegment(sketch, "E3791", {"start": v(-2.15, 15.1) * mm, "end": v(-2.08, 15.09) * mm});
            skLineSegment(sketch, "E3792", {"start": v(-2.08, 15.09) * mm, "end": v(-2.02, 15.08) * mm});
            skLineSegment(sketch, "E3793", {"start": v(-2.02, 15.08) * mm, "end": v(-1.95, 15.07) * mm});
            skLineSegment(sketch, "E3794", {"start": v(-1.95, 15.07) * mm, "end": v(-1.89, 15.05) * mm});
            skLineSegment(sketch, "E3795", {"start": v(-1.89, 15.05) * mm, "end": v(-1.82, 15.04) * mm});
            skLineSegment(sketch, "E3796", {"start": v(-1.82, 15.04) * mm, "end": v(-1.76, 15.02) * mm});
            skLineSegment(sketch, "E3797", {"start": v(-1.76, 15.02) * mm, "end": v(-1.7, 15) * mm});
            skLineSegment(sketch, "E3798", {"start": v(-1.7, 15) * mm, "end": v(-1.64, 14.98) * mm});
            skLineSegment(sketch, "E3799", {"start": v(-1.64, 14.98) * mm, "end": v(-1.59, 14.96) * mm});
            skLineSegment(sketch, "E3800", {"start": v(-1.59, 14.96) * mm, "end": v(-1.53, 14.93) * mm});
            skLineSegment(sketch, "E3801", {"start": v(-1.53, 14.93) * mm, "end": v(-1.47, 14.9) * mm});
            skLineSegment(sketch, "E3802", {"start": v(-1.47, 14.9) * mm, "end": v(-1.42, 14.88) * mm});
            skLineSegment(sketch, "E3803", {"start": v(-1.42, 14.88) * mm, "end": v(-1.36, 14.84) * mm});
            skLineSegment(sketch, "E3804", {"start": v(-1.36, 14.84) * mm, "end": v(-1.3, 14.9) * mm});
            skLineSegment(sketch, "E3805", {"start": v(-1.3, 14.9) * mm, "end": v(-1.23, 14.96) * mm});
            skLineSegment(sketch, "E3806", {"start": v(-1.23, 14.96) * mm, "end": v(-1.16, 15.02) * mm});
            skLineSegment(sketch, "E3807", {"start": v(-1.16, 15.02) * mm, "end": v(-1.09, 15.08) * mm});
            skLineSegment(sketch, "E3808", {"start": v(-1.09, 15.08) * mm, "end": v(-1.02, 15.13) * mm});
            skLineSegment(sketch, "E3809", {"start": v(-1.02, 15.13) * mm, "end": v(-0.95, 15.2) * mm});
            skLineSegment(sketch, "E3810", {"start": v(-0.95, 15.2) * mm, "end": v(-0.88, 15.25) * mm});
            skLineSegment(sketch, "E3811", {"start": v(-0.88, 15.25) * mm, "end": v(-0.81, 15.3) * mm});
            skLineSegment(sketch, "E3812", {"start": v(-0.81, 15.3) * mm, "end": v(-0.75, 15.36) * mm});
            skLineSegment(sketch, "E3813", {"start": v(-0.75, 15.36) * mm, "end": v(-0.68, 15.42) * mm});
            skLineSegment(sketch, "E3814", {"start": v(-0.68, 15.42) * mm, "end": v(-0.6, 15.48) * mm});
            skLineSegment(sketch, "E3815", {"start": v(-0.6, 15.48) * mm, "end": v(-0.54, 15.54) * mm});
            skLineSegment(sketch, "E3816", {"start": v(-0.54, 15.54) * mm, "end": v(-0.47, 15.6) * mm});
            skLineSegment(sketch, "E3817", {"start": v(-0.47, 15.6) * mm, "end": v(-0.4, 15.65) * mm});
            skLineSegment(sketch, "E3818", {"start": v(-0.4, 15.65) * mm, "end": v(-0.34, 15.7) * mm});
            skLineSegment(sketch, "E3819", {"start": v(-0.34, 15.7) * mm, "end": v(-0.27, 15.77) * mm});
            skLineSegment(sketch, "E3820", {"start": v(-0.27, 15.77) * mm, "end": v(-0.37, 15.84) * mm});
            skLineSegment(sketch, "E3821", {"start": v(-0.37, 15.84) * mm, "end": v(-0.48, 15.91) * mm});
            skLineSegment(sketch, "E3822", {"start": v(-0.48, 15.91) * mm, "end": v(-0.6, 15.98) * mm});
            skLineSegment(sketch, "E3823", {"start": v(-0.6, 15.98) * mm, "end": v(-0.7, 16.04) * mm});
            skLineSegment(sketch, "E3824", {"start": v(-0.7, 16.04) * mm, "end": v(-0.82, 16.1) * mm});
            skLineSegment(sketch, "E3825", {"start": v(-0.82, 16.1) * mm, "end": v(-0.94, 16.15) * mm});
            skLineSegment(sketch, "E3826", {"start": v(-0.94, 16.15) * mm, "end": v(-1.06, 16.2) * mm});
            skLineSegment(sketch, "E3827", {"start": v(-1.06, 16.2) * mm, "end": v(-1.2, 16.24) * mm});
            skLineSegment(sketch, "E3828", {"start": v(-1.2, 16.24) * mm, "end": v(-1.32, 16.28) * mm});
            skLineSegment(sketch, "E3829", {"start": v(-1.32, 16.28) * mm, "end": v(-1.46, 16.32) * mm});
            skLineSegment(sketch, "E3830", {"start": v(-1.46, 16.32) * mm, "end": v(-1.6, 16.35) * mm});
            skLineSegment(sketch, "E3831", {"start": v(-1.6, 16.35) * mm, "end": v(-1.74, 16.37) * mm});
            skLineSegment(sketch, "E3832", {"start": v(-1.74, 16.37) * mm, "end": v(-1.9, 16.39) * mm});
            skLineSegment(sketch, "E3833", {"start": v(-1.9, 16.39) * mm, "end": v(-2.05, 16.4) * mm});
            skLineSegment(sketch, "E3834", {"start": v(-2.05, 16.4) * mm, "end": v(-2.2, 16.41) * mm});
            skLineSegment(sketch, "E3835", {"start": v(-2.2, 16.41) * mm, "end": v(-2.37, 16.41) * mm});
            skLineSegment(sketch, "E3836", {"start": v(-2.37, 16.41) * mm, "end": v(-2.69, 16.4) * mm});
            skLineSegment(sketch, "E3837", {"start": v(-2.69, 16.4) * mm, "end": v(-3, 16.36) * mm});
            skLineSegment(sketch, "E3838", {"start": v(-3, 16.36) * mm, "end": v(-3.3, 16.3) * mm});
            skLineSegment(sketch, "E3839", {"start": v(-3.3, 16.3) * mm, "end": v(-3.57, 16.2) * mm});
            skLineSegment(sketch, "E3840", {"start": v(-3.57, 16.2) * mm, "end": v(-3.84, 16.09) * mm});
            skLineSegment(sketch, "E3841", {"start": v(-3.84, 16.09) * mm, "end": v(-4.08, 15.95) * mm});
            skLineSegment(sketch, "E3842", {"start": v(-4.08, 15.95) * mm, "end": v(-4.31, 15.8) * mm});
            skLineSegment(sketch, "E3843", {"start": v(-4.31, 15.8) * mm, "end": v(-4.52, 15.62) * mm});
            skLineSegment(sketch, "E3844", {"start": v(-4.52, 15.62) * mm, "end": v(-4.71, 15.42) * mm});
            skLineSegment(sketch, "E3845", {"start": v(-4.71, 15.42) * mm, "end": v(-4.88, 15.2) * mm});
            skLineSegment(sketch, "E3846", {"start": v(-4.88, 15.2) * mm, "end": v(-5.03, 14.98) * mm});
            skLineSegment(sketch, "E3847", {"start": v(-5.03, 14.98) * mm, "end": v(-5.15, 14.74) * mm});
            skLineSegment(sketch, "E3848", {"start": v(-5.15, 14.74) * mm, "end": v(-5.25, 14.49) * mm});
            skLineSegment(sketch, "E3849", {"start": v(-5.25, 14.49) * mm, "end": v(-5.32, 14.22) * mm});
            skLineSegment(sketch, "E3850", {"start": v(-5.32, 14.22) * mm, "end": v(-5.36, 13.95) * mm});
            skLineSegment(sketch, "E3851", {"start": v(-5.36, 13.95) * mm, "end": v(-5.38, 13.66) * mm});
            skLineSegment(sketch, "E3852", {"start": v(-5.38, 13.66) * mm, "end": v(-5.38, 13.66) * mm});
            skLineSegment(sketch, "E3853", {"start": v(-5.38, 13.66) * mm, "end": v(-5.38, 13.65) * mm});
            skLineSegment(sketch, "E3854", {"start": v(-5.38, 13.65) * mm, "end": v(-5.38, 13.65) * mm});
            skLineSegment(sketch, "E3855", {"start": v(-5.38, 13.65) * mm, "end": v(-5.36, 13.35) * mm});
            skLineSegment(sketch, "E3856", {"start": v(-5.36, 13.35) * mm, "end": v(-5.32, 13.07) * mm});
            skLineSegment(sketch, "E3857", {"start": v(-5.32, 13.07) * mm, "end": v(-5.25, 12.8) * mm});
            skLineSegment(sketch, "E3858", {"start": v(-5.25, 12.8) * mm, "end": v(-5.15, 12.54) * mm});
            skLineSegment(sketch, "E3859", {"start": v(-5.15, 12.54) * mm, "end": v(-5.02, 12.3) * mm});
            skLineSegment(sketch, "E3860", {"start": v(-5.02, 12.3) * mm, "end": v(-4.88, 12.08) * mm});
            skLineSegment(sketch, "E3861", {"start": v(-4.88, 12.08) * mm, "end": v(-4.7, 11.87) * mm});
            skLineSegment(sketch, "E3862", {"start": v(-4.7, 11.87) * mm, "end": v(-4.51, 11.68) * mm});
            skLineSegment(sketch, "E3863", {"start": v(-4.51, 11.68) * mm, "end": v(-4.3, 11.5) * mm});
            skLineSegment(sketch, "E3864", {"start": v(-4.3, 11.5) * mm, "end": v(-4.06, 11.35) * mm});
            skLineSegment(sketch, "E3865", {"start": v(-4.06, 11.35) * mm, "end": v(-3.81, 11.22) * mm});
            skLineSegment(sketch, "E3866", {"start": v(-3.81, 11.22) * mm, "end": v(-3.55, 11.11) * mm});
            skLineSegment(sketch, "E3867", {"start": v(-3.55, 11.11) * mm, "end": v(-3.26, 11.02) * mm});
            skLineSegment(sketch, "E3868", {"start": v(-3.26, 11.02) * mm, "end": v(-2.97, 10.96) * mm});
            skLineSegment(sketch, "E3869", {"start": v(-2.97, 10.96) * mm, "end": v(-2.66, 10.92) * mm});
            skLineSegment(sketch, "E3870", {"start": v(-2.66, 10.92) * mm, "end": v(-2.34, 10.9) * mm});
            skLineSegment(sketch, "E3871", {"start": v(-2.34, 10.9) * mm, "end": v(-2.15, 10.91) * mm});
            skLineSegment(sketch, "E3872", {"start": v(-2.15, 10.91) * mm, "end": v(-1.97, 10.93) * mm});
            skLineSegment(sketch, "E3873", {"start": v(-1.97, 10.93) * mm, "end": v(-1.79, 10.94) * mm});
            skLineSegment(sketch, "E3874", {"start": v(-1.79, 10.94) * mm, "end": v(-1.61, 10.97) * mm});
            skLineSegment(sketch, "E3875", {"start": v(-1.61, 10.97) * mm, "end": v(-1.44, 11) * mm});
            skLineSegment(sketch, "E3876", {"start": v(-1.44, 11) * mm, "end": v(-1.28, 11.05) * mm});
            skLineSegment(sketch, "E3877", {"start": v(-1.28, 11.05) * mm, "end": v(-1.12, 11.1) * mm});
            skLineSegment(sketch, "E3878", {"start": v(-1.12, 11.1) * mm, "end": v(-0.96, 11.14) * mm});
            skLineSegment(sketch, "E3879", {"start": v(-0.96, 11.14) * mm, "end": v(-0.82, 11.2) * mm});
            skLineSegment(sketch, "E3880", {"start": v(-0.82, 11.2) * mm, "end": v(-0.67, 11.26) * mm});
            skLineSegment(sketch, "E3881", {"start": v(-0.67, 11.26) * mm, "end": v(-0.53, 11.33) * mm});
            skLineSegment(sketch, "E3882", {"start": v(-0.53, 11.33) * mm, "end": v(-0.4, 11.4) * mm});
            skLineSegment(sketch, "E3883", {"start": v(-0.4, 11.4) * mm, "end": v(-0.27, 11.48) * mm});
            skLineSegment(sketch, "E3884", {"start": v(-0.27, 11.48) * mm, "end": v(-0.14, 11.56) * mm});
            skLineSegment(sketch, "E3885", {"start": v(-0.14, 11.56) * mm, "end": v(-0.02, 11.64) * mm});
            skLineSegment(sketch, "E3886", {"start": v(-0.02, 11.64) * mm, "end": v(0.1, 11.73) * mm});
            skLineSegment(sketch, "E3887", {"start": v(0.1, 11.73) * mm, "end": v(0.1, 11.87) * mm});
            skLineSegment(sketch, "E3888", {"start": v(0.1, 11.87) * mm, "end": v(0.1, 12.02) * mm});
            skLineSegment(sketch, "E3889", {"start": v(0.1, 12.02) * mm, "end": v(0.1, 12.17) * mm});
            skLineSegment(sketch, "E3890", {"start": v(0.1, 12.17) * mm, "end": v(0.1, 12.32) * mm});
            skLineSegment(sketch, "E3891", {"start": v(0.1, 12.32) * mm, "end": v(0.1, 12.47) * mm});
            skLineSegment(sketch, "E3892", {"start": v(0.1, 12.47) * mm, "end": v(0.1, 12.62) * mm});
            skLineSegment(sketch, "E3893", {"start": v(0.1, 12.62) * mm, "end": v(0.1, 12.77) * mm});
            skLineSegment(sketch, "E3894", {"start": v(0.1, 12.77) * mm, "end": v(0.1, 12.92) * mm});
            skLineSegment(sketch, "E3895", {"start": v(0.1, 12.92) * mm, "end": v(0.1, 13.07) * mm});
            skLineSegment(sketch, "E3896", {"start": v(0.1, 13.07) * mm, "end": v(0.1, 13.21) * mm});
            skLineSegment(sketch, "E3897", {"start": v(0.1, 13.21) * mm, "end": v(0.1, 13.36) * mm});
            skLineSegment(sketch, "E3898", {"start": v(0.1, 13.36) * mm, "end": v(0.1, 13.51) * mm});
            skLineSegment(sketch, "E3899", {"start": v(0.1, 13.51) * mm, "end": v(0.1, 13.66) * mm});
            skLineSegment(sketch, "E3900", {"start": v(0.1, 13.66) * mm, "end": v(0.1, 13.8) * mm});
            skLineSegment(sketch, "E3901", {"start": v(0.1, 13.8) * mm, "end": v(0.1, 13.96) * mm});
            skLineSegment(sketch, "E3902", {"start": v(0.1, 13.96) * mm, "end": v(0.1, 14.1) * mm});
            skLineSegment(sketch, "E3903", {"start": v(0.1, 14.1) * mm, "end": v(-0.02, 14.1) * mm});
            skLineSegment(sketch, "E3904", {"start": v(-0.02, 14.1) * mm, "end": v(-0.12, 14.1) * mm});
            skLineSegment(sketch, "E3905", {"start": v(-0.12, 14.1) * mm, "end": v(-0.23, 14.1) * mm});
            skLineSegment(sketch, "E3906", {"start": v(-0.23, 14.1) * mm, "end": v(-0.33, 14.1) * mm});
            skLineSegment(sketch, "E3907", {"start": v(-0.33, 14.1) * mm, "end": v(-0.44, 14.1) * mm});
            skLineSegment(sketch, "E3908", {"start": v(-0.44, 14.1) * mm, "end": v(-0.55, 14.1) * mm});
            skLineSegment(sketch, "E3909", {"start": v(-0.55, 14.1) * mm, "end": v(-0.65, 14.1) * mm});
            skLineSegment(sketch, "E3910", {"start": v(-0.65, 14.1) * mm, "end": v(-0.76, 14.1) * mm});
            skLineSegment(sketch, "E3911", {"start": v(-0.76, 14.1) * mm, "end": v(-0.86, 14.1) * mm});
            skLineSegment(sketch, "E3912", {"start": v(-0.86, 14.1) * mm, "end": v(-0.97, 14.1) * mm});
            skLineSegment(sketch, "E3913", {"start": v(-0.97, 14.1) * mm, "end": v(-1.08, 14.1) * mm});
            skLineSegment(sketch, "E3914", {"start": v(-1.08, 14.1) * mm, "end": v(-1.18, 14.1) * mm});
            skLineSegment(sketch, "E3915", {"start": v(-1.18, 14.1) * mm, "end": v(-1.29, 14.1) * mm});
            skLineSegment(sketch, "E3916", {"start": v(-1.29, 14.1) * mm, "end": v(-1.4, 14.1) * mm});
            skLineSegment(sketch, "E3917", {"start": v(-1.4, 14.1) * mm, "end": v(-1.5, 14.1) * mm});
            skLineSegment(sketch, "E3918", {"start": v(-1.5, 14.1) * mm, "end": v(-1.6, 14.1) * mm});
            skLineSegment(sketch, "E3919", {"start": v(-1.6, 14.1) * mm, "end": v(-1.69, 14.04) * mm});
            skLineSegment(sketch, "E3920", {"start": v(-1.69, 14.04) * mm, "end": v(-1.77, 13.97) * mm});
            skLineSegment(sketch, "E3921", {"start": v(-1.77, 13.97) * mm, "end": v(-1.85, 13.9) * mm});
            skLineSegment(sketch, "E3922", {"start": v(-1.85, 13.9) * mm, "end": v(-1.93, 13.84) * mm});
            skLineSegment(sketch, "E3923", {"start": v(-1.93, 13.84) * mm, "end": v(-2, 13.77) * mm});
            skLineSegment(sketch, "E3924", {"start": v(-2, 13.77) * mm, "end": v(-2.08, 13.7) * mm});
            skLineSegment(sketch, "E3925", {"start": v(-2.08, 13.7) * mm, "end": v(-2.16, 13.64) * mm});
            skLineSegment(sketch, "E3926", {"start": v(-2.16, 13.64) * mm, "end": v(-2.24, 13.57) * mm});
            skLineSegment(sketch, "E3927", {"start": v(-2.24, 13.57) * mm, "end": v(-2.32, 13.5) * mm});
            skLineSegment(sketch, "E3928", {"start": v(-2.32, 13.5) * mm, "end": v(-2.4, 13.44) * mm});
            skLineSegment(sketch, "E3929", {"start": v(-2.4, 13.44) * mm, "end": v(-2.48, 13.37) * mm});
            skLineSegment(sketch, "E3930", {"start": v(-2.48, 13.37) * mm, "end": v(-2.56, 13.3) * mm});
            skLineSegment(sketch, "E3931", {"start": v(-2.56, 13.3) * mm, "end": v(-2.64, 13.24) * mm});
            skLineSegment(sketch, "E3932", {"start": v(-2.64, 13.24) * mm, "end": v(-2.72, 13.17) * mm});
            skLineSegment(sketch, "E3933", {"start": v(-2.72, 13.17) * mm, "end": v(-2.8, 13.1) * mm});
            skLineSegment(sketch, "E3934", {"start": v(-2.8, 13.1) * mm, "end": v(-2.88, 13.03) * mm});
            skLineSegment(sketch, "E3935", {"start": v(2.5, 16.3) * mm, "end": v(2.4, 16.22) * mm});
            skLineSegment(sketch, "E3936", {"start": v(2.4, 16.22) * mm, "end": v(2.3, 16.14) * mm});
            skLineSegment(sketch, "E3937", {"start": v(2.3, 16.14) * mm, "end": v(2.2, 16.06) * mm});
            skLineSegment(sketch, "E3938", {"start": v(2.2, 16.06) * mm, "end": v(2.1, 15.97) * mm});
            skLineSegment(sketch, "E3939", {"start": v(2.1, 15.97) * mm, "end": v(2.01, 15.9) * mm});
            skLineSegment(sketch, "E3940", {"start": v(2.01, 15.9) * mm, "end": v(1.92, 15.8) * mm});
            skLineSegment(sketch, "E3941", {"start": v(1.92, 15.8) * mm, "end": v(1.82, 15.73) * mm});
            skLineSegment(sketch, "E3942", {"start": v(1.82, 15.73) * mm, "end": v(1.72, 15.65) * mm});
            skLineSegment(sketch, "E3943", {"start": v(1.72, 15.65) * mm, "end": v(1.62, 15.56) * mm});
            skLineSegment(sketch, "E3944", {"start": v(1.62, 15.56) * mm, "end": v(1.53, 15.48) * mm});
            skLineSegment(sketch, "E3945", {"start": v(1.53, 15.48) * mm, "end": v(1.43, 15.4) * mm});
            skLineSegment(sketch, "E3946", {"start": v(1.43, 15.4) * mm, "end": v(1.33, 15.32) * mm});
            skLineSegment(sketch, "E3947", {"start": v(1.33, 15.32) * mm, "end": v(1.23, 15.23) * mm});
            skLineSegment(sketch, "E3948", {"start": v(1.23, 15.23) * mm, "end": v(1.14, 15.15) * mm});
            skLineSegment(sketch, "E3949", {"start": v(1.14, 15.15) * mm, "end": v(1.04, 15.07) * mm});
            skLineSegment(sketch, "E3950", {"start": v(1.04, 15.07) * mm, "end": v(0.94, 14.99) * mm});
            skLineSegment(sketch, "E3951", {"start": v(0.94, 14.99) * mm, "end": v(0.94, 14.74) * mm});
            skLineSegment(sketch, "E3952", {"start": v(0.94, 14.74) * mm, "end": v(0.94, 14.5) * mm});
            skLineSegment(sketch, "E3953", {"start": v(0.94, 14.5) * mm, "end": v(0.94, 14.24) * mm});
            skLineSegment(sketch, "E3954", {"start": v(0.94, 14.24) * mm, "end": v(0.94, 14) * mm});
            skLineSegment(sketch, "E3955", {"start": v(0.94, 14) * mm, "end": v(0.94, 13.75) * mm});
            skLineSegment(sketch, "E3956", {"start": v(0.94, 13.75) * mm, "end": v(0.94, 13.5) * mm});
            skLineSegment(sketch, "E3957", {"start": v(0.94, 13.5) * mm, "end": v(0.94, 13.25) * mm});
            skLineSegment(sketch, "E3958", {"start": v(0.94, 13.25) * mm, "end": v(0.94, 13) * mm});
            skLineSegment(sketch, "E3959", {"start": v(0.94, 13) * mm, "end": v(0.94, 12.75) * mm});
            skLineSegment(sketch, "E3960", {"start": v(0.94, 12.75) * mm, "end": v(0.94, 12.5) * mm});
            skLineSegment(sketch, "E3961", {"start": v(0.94, 12.5) * mm, "end": v(0.94, 12.26) * mm});
            skLineSegment(sketch, "E3962", {"start": v(0.94, 12.26) * mm, "end": v(0.94, 12) * mm});
            skLineSegment(sketch, "E3963", {"start": v(0.94, 12) * mm, "end": v(0.94, 11.76) * mm});
            skLineSegment(sketch, "E3964", {"start": v(0.94, 11.76) * mm, "end": v(0.94, 11.51) * mm});
            skLineSegment(sketch, "E3965", {"start": v(0.94, 11.51) * mm, "end": v(0.94, 11.26) * mm});
            skLineSegment(sketch, "E3966", {"start": v(0.94, 11.26) * mm, "end": v(0.94, 11.02) * mm});
            skLineSegment(sketch, "E3967", {"start": v(0.94, 11.02) * mm, "end": v(1.04, 11.02) * mm});
            skLineSegment(sketch, "E3968", {"start": v(1.04, 11.02) * mm, "end": v(1.14, 11.02) * mm});
            skLineSegment(sketch, "E3969", {"start": v(1.14, 11.02) * mm, "end": v(1.23, 11.02) * mm});
            skLineSegment(sketch, "E3970", {"start": v(1.23, 11.02) * mm, "end": v(1.33, 11.02) * mm});
            skLineSegment(sketch, "E3971", {"start": v(1.33, 11.02) * mm, "end": v(1.43, 11.02) * mm});
            skLineSegment(sketch, "E3972", {"start": v(1.43, 11.02) * mm, "end": v(1.53, 11.02) * mm});
            skLineSegment(sketch, "E3973", {"start": v(1.53, 11.02) * mm, "end": v(1.62, 11.02) * mm});
            skLineSegment(sketch, "E3974", {"start": v(1.62, 11.02) * mm, "end": v(1.72, 11.02) * mm});
            skLineSegment(sketch, "E3975", {"start": v(1.72, 11.02) * mm, "end": v(1.82, 11.02) * mm});
            skLineSegment(sketch, "E3976", {"start": v(1.82, 11.02) * mm, "end": v(1.92, 11.02) * mm});
            skLineSegment(sketch, "E3977", {"start": v(1.92, 11.02) * mm, "end": v(2.01, 11.02) * mm});
            skLineSegment(sketch, "E3978", {"start": v(2.01, 11.02) * mm, "end": v(2.1, 11.02) * mm});
            skLineSegment(sketch, "E3979", {"start": v(2.1, 11.02) * mm, "end": v(2.2, 11.02) * mm});
            skLineSegment(sketch, "E3980", {"start": v(2.2, 11.02) * mm, "end": v(2.3, 11.02) * mm});
            skLineSegment(sketch, "E3981", {"start": v(2.3, 11.02) * mm, "end": v(2.4, 11.02) * mm});
            skLineSegment(sketch, "E3982", {"start": v(2.4, 11.02) * mm, "end": v(2.5, 11.02) * mm});
            skLineSegment(sketch, "E3983", {"start": v(2.5, 11.02) * mm, "end": v(2.5, 11.35) * mm});
            skLineSegment(sketch, "E3984", {"start": v(2.5, 11.35) * mm, "end": v(2.5, 11.68) * mm});
            skLineSegment(sketch, "E3985", {"start": v(2.5, 11.68) * mm, "end": v(2.5, 12) * mm});
            skLineSegment(sketch, "E3986", {"start": v(2.5, 12) * mm, "end": v(2.5, 12.34) * mm});
            skLineSegment(sketch, "E3987", {"start": v(2.5, 12.34) * mm, "end": v(2.5, 12.67) * mm});
            skLineSegment(sketch, "E3988", {"start": v(2.5, 12.67) * mm, "end": v(2.5, 13) * mm});
            skLineSegment(sketch, "E3989", {"start": v(2.5, 13) * mm, "end": v(2.5, 13.33) * mm});
            skLineSegment(sketch, "E3990", {"start": v(2.5, 13.33) * mm, "end": v(2.5, 13.66) * mm});
            skLineSegment(sketch, "E3991", {"start": v(2.5, 13.66) * mm, "end": v(2.5, 13.99) * mm});
            skLineSegment(sketch, "E3992", {"start": v(2.5, 13.99) * mm, "end": v(2.5, 14.32) * mm});
            skLineSegment(sketch, "E3993", {"start": v(2.5, 14.32) * mm, "end": v(2.5, 14.65) * mm});
            skLineSegment(sketch, "E3994", {"start": v(2.5, 14.65) * mm, "end": v(2.5, 14.98) * mm});
            skLineSegment(sketch, "E3995", {"start": v(2.5, 14.98) * mm, "end": v(2.5, 15.31) * mm});
            skLineSegment(sketch, "E3996", {"start": v(2.5, 15.31) * mm, "end": v(2.5, 15.64) * mm});
            skLineSegment(sketch, "E3997", {"start": v(2.5, 15.64) * mm, "end": v(2.5, 15.97) * mm});
            skLineSegment(sketch, "E3998", {"start": v(2.5, 15.97) * mm, "end": v(2.5, 16.3) * mm});
            skSolve(sketch);
        }
        {
            var Q0;
            Q0=makeQuery(id+"F3.imprint","IMPRINT",FACE,{"disambiguationData":[TD([[makeQuery(id+"F3.imprint","IMPRINT",EDGE,{"derivedFrom":sQuery(id+"F3.wireOp",EDGE,"E3017")}),1.0]])]});
            var Q1;
            Q1=makeQuery(id+"F3.imprint","IMPRINT",FACE,{"disambiguationData":[TD([[makeQuery(id+"F3.imprint","IMPRINT",EDGE,{"derivedFrom":sQuery(id+"F3.wireOp",EDGE,"E2105")}),-1.0]])]});
            var Q2;
            Q2=makeQuery(id+"F3.imprint","IMPRINT",FACE,{"disambiguationData":[TD([[makeQuery(id+"F3.imprint","IMPRINT",EDGE,{"derivedFrom":sQuery(id+"F3.wireOp",EDGE,"E2217")}),-1.0]])]});
            var Q3;
            Q3=makeQuery(id+"F3.imprint","IMPRINT",FACE,{"disambiguationData":[TD([[makeQuery(id+"F3.imprint","IMPRINT",EDGE,{"derivedFrom":sQuery(id+"F3.wireOp",EDGE,"E2361")}),-1.0]])]});
            var Q4;
            Q4=makeQuery(id+"F3.imprint","IMPRINT",FACE,{"disambiguationData":[TD([[makeQuery(id+"F3.imprint","IMPRINT",EDGE,{"derivedFrom":sQuery(id+"F3.wireOp",EDGE,"E2457")}),-1.0]])]});
            var Q5;
            Q5=makeQuery(id+"F3.imprint","IMPRINT",FACE,{"disambiguationData":[TD([[makeQuery(id+"F3.imprint","IMPRINT",EDGE,{"derivedFrom":sQuery(id+"F3.wireOp",EDGE,"E2617")}),-1.0]])]});
            var Q6;
            Q6=makeQuery(id+"F3.imprint","IMPRINT",FACE,{"disambiguationData":[TD([[makeQuery(id+"F3.imprint","IMPRINT",EDGE,{"derivedFrom":sQuery(id+"F3.wireOp",EDGE,"E2713")}),-1.0]])]});
            var Q7;
            Q7=makeQuery(id+"F3.imprint","IMPRINT",FACE,{"disambiguationData":[TD([[makeQuery(id+"F3.imprint","IMPRINT",EDGE,{"derivedFrom":sQuery(id+"F3.wireOp",EDGE,"E2793")}),-1.0]])]});
            var Q8;
            Q8=makeQuery(id+"F3.imprint","IMPRINT",FACE,{"disambiguationData":[TD([[makeQuery(id+"F3.imprint","IMPRINT",EDGE,{"derivedFrom":sQuery(id+"F3.wireOp",EDGE,"E2857")}),-1.0]])]});
            var Q9;
            Q9=makeQuery(id+"F3.imprint","IMPRINT",FACE,{"disambiguationData":[TD([[makeQuery(id+"F3.imprint","IMPRINT",EDGE,{"derivedFrom":sQuery(id+"F3.wireOp",EDGE,"E3049")}),1.0]])]});
            extrude(context, id + "F4", {"entities" : qUnion([Q0, Q1, Q2, Q3, Q4, Q5, Q6, Q7, Q8, Q9]), "operationType" : NewBodyOperationType.ADD, "depth" : 2 * mm, "offsetDistance" : 25 * mm, "hasSecondDirection" : true, "secondDirectionOppositeDirection" : true, "secondDirectionDepth" : 0.39 * mm});
        }
        {
            var Q0;
            Q0=makeQuery(id+"F3.imprint","IMPRINT",FACE,{"disambiguationData":[TD([[makeQuery(id+"F3.imprint","IMPRINT",EDGE,{"derivedFrom":sQuery(id+"F3.wireOp",EDGE,"E3113")}),-1.0]])]});
            var Q1;
            Q1=makeQuery(id+"F3.imprint","IMPRINT",FACE,{"disambiguationData":[TD([[makeQuery(id+"F3.imprint","IMPRINT",EDGE,{"derivedFrom":sQuery(id+"F3.wireOp",EDGE,"E3209")}),-1.0]])]});
            var Q2;
            Q2=makeQuery(id+"F3.imprint","IMPRINT",FACE,{"disambiguationData":[TD([[makeQuery(id+"F3.imprint","IMPRINT",EDGE,{"derivedFrom":sQuery(id+"F3.wireOp",EDGE,"E3705")}),1.0]])]});
            var Q3;
            Q3=makeQuery(id+"F3.imprint","IMPRINT",FACE,{"disambiguationData":[TD([[makeQuery(id+"F3.imprint","IMPRINT",EDGE,{"derivedFrom":sQuery(id+"F3.wireOp",EDGE,"E3935")}),1.0]])]});
            var Q4;
            Q4=makeQuery(id+"F3.imprint","IMPRINT",FACE,{"disambiguationData":[TD([[makeQuery(id+"F3.imprint","IMPRINT",EDGE,{"derivedFrom":sQuery(id+"F3.wireOp",EDGE,"E3401")}),-1.0]])]});
            var Q5;
            Q5=makeQuery(id+"F3.imprint","IMPRINT",FACE,{"disambiguationData":[TD([[makeQuery(id+"F3.imprint","IMPRINT",EDGE,{"derivedFrom":sQuery(id+"F3.wireOp",EDGE,"E3545")}),-1.0]])]});
            var Q6;
            Q6=makeQuery(id+"F3.imprint","IMPRINT",FACE,{"disambiguationData":[TD([[makeQuery(id+"F3.imprint","IMPRINT",EDGE,{"derivedFrom":sQuery(id+"F3.wireOp",EDGE,"E129")}),-1.0]])]});
            var Q7;
            Q7=makeQuery(id+"F3.imprint","IMPRINT",FACE,{"disambiguationData":[TD([[makeQuery(id+"F3.imprint","IMPRINT",EDGE,{"derivedFrom":sQuery(id+"F3.wireOp",EDGE,"E305")}),-1.0]])]});
            var Q8;
            Q8=makeQuery(id+"F3.imprint","IMPRINT",FACE,{"disambiguationData":[TD([[makeQuery(id+"F3.imprint","IMPRINT",EDGE,{"derivedFrom":sQuery(id+"F3.wireOp",EDGE,"E401")}),-1.0]])]});
            var Q9;
            Q9=makeQuery(id+"F3.imprint","IMPRINT",FACE,{"disambiguationData":[TD([[makeQuery(id+"F3.imprint","IMPRINT",EDGE,{"derivedFrom":sQuery(id+"F3.wireOp",EDGE,"E481")}),-1.0]])]});
            var Q10;
            Q10=makeQuery(id+"F3.imprint","IMPRINT",FACE,{"disambiguationData":[TD([[makeQuery(id+"F3.imprint","IMPRINT",EDGE,{"derivedFrom":sQuery(id+"F3.wireOp",EDGE,"E609")}),-1.0]])]});
            var Q11;
            Q11=makeQuery(id+"F3.imprint","IMPRINT",FACE,{"disambiguationData":[TD([[makeQuery(id+"F3.imprint","IMPRINT",EDGE,{"derivedFrom":sQuery(id+"F3.wireOp",EDGE,"E753")}),-1.0]])]});
            var Q12;
            Q12=makeQuery(id+"F3.imprint","IMPRINT",FACE,{"disambiguationData":[TD([[makeQuery(id+"F3.imprint","IMPRINT",EDGE,{"derivedFrom":sQuery(id+"F3.wireOp",EDGE,"E849")}),-1.0]])]});
            var Q13;
            Q13=makeQuery(id+"F3.imprint","IMPRINT",FACE,{"disambiguationData":[TD([[makeQuery(id+"F3.imprint","IMPRINT",EDGE,{"derivedFrom":sQuery(id+"F3.wireOp",EDGE,"E977")}),-1.0]])]});
            var Q14;
            Q14=makeQuery(id+"F3.imprint","IMPRINT",FACE,{"disambiguationData":[TD([[makeQuery(id+"F3.imprint","IMPRINT",EDGE,{"derivedFrom":sQuery(id+"F3.wireOp",EDGE,"E1153")}),-1.0]])]});
            var Q15;
            Q15=makeQuery(id+"F3.imprint","IMPRINT",FACE,{"disambiguationData":[TD([[makeQuery(id+"F3.imprint","IMPRINT",EDGE,{"derivedFrom":sQuery(id+"F3.wireOp",EDGE,"E1217")}),-1.0]])]});
            var Q16;
            Q16=makeQuery(id+"F3.imprint","IMPRINT",FACE,{"disambiguationData":[TD([[makeQuery(id+"F3.imprint","IMPRINT",EDGE,{"derivedFrom":sQuery(id+"F3.wireOp",EDGE,"E2009")}),-1.0]])]});
            var Q17;
            Q17=makeQuery(id+"F3.imprint","IMPRINT",FACE,{"disambiguationData":[TD([[makeQuery(id+"F3.imprint","IMPRINT",EDGE,{"derivedFrom":sQuery(id+"F3.wireOp",EDGE,"E1865")}),-1.0]])]});
            var Q18;
            Q18=makeQuery(id+"F3.imprint","IMPRINT",FACE,{"disambiguationData":[TD([[makeQuery(id+"F3.imprint","IMPRINT",EDGE,{"derivedFrom":sQuery(id+"F3.wireOp",EDGE,"E1785")}),-1.0]])]});
            var Q19;
            Q19=makeQuery(id+"F3.imprint","IMPRINT",FACE,{"disambiguationData":[TD([[makeQuery(id+"F3.imprint","IMPRINT",EDGE,{"derivedFrom":sQuery(id+"F3.wireOp",EDGE,"E1689")}),-1.0]])]});
            var Q20;
            Q20=makeQuery(id+"F3.imprint","IMPRINT",FACE,{"disambiguationData":[TD([[makeQuery(id+"F3.imprint","IMPRINT",EDGE,{"derivedFrom":sQuery(id+"F3.wireOp",EDGE,"E1641")}),-1.0]])]});
            var Q21;
            Q21=makeQuery(id+"F3.imprint","IMPRINT",FACE,{"disambiguationData":[TD([[makeQuery(id+"F3.imprint","IMPRINT",EDGE,{"derivedFrom":sQuery(id+"F3.wireOp",EDGE,"E1593")}),-1.0]])]});
            var Q22;
            Q22=makeQuery(id+"F3.imprint","IMPRINT",FACE,{"disambiguationData":[TD([[makeQuery(id+"F3.imprint","IMPRINT",EDGE,{"derivedFrom":sQuery(id+"F3.wireOp",EDGE,"E1505")}),-1.0]])]});
            var Q23;
            Q23=makeQuery(id+"F3.imprint","IMPRINT",FACE,{"disambiguationData":[TD([[makeQuery(id+"F3.imprint","IMPRINT",EDGE,{"derivedFrom":sQuery(id+"F3.wireOp",EDGE,"E1409")}),-1.0]])]});
            var Q24;
            Q24=makeQuery(id+"F3.imprint","IMPRINT",FACE,{"disambiguationData":[TD([[makeQuery(id+"F3.imprint","IMPRINT",EDGE,{"derivedFrom":sQuery(id+"F3.wireOp",EDGE,"E1313")}),-1.0]])]});
            extrude(context, id + "F5", {"entities" : qUnion([Q0, Q1, Q2, Q3, Q4, Q5, Q6, Q7, Q8, Q9, Q10, Q11, Q12, Q13, Q14, Q15, Q16, Q17, Q18, Q19, Q20, Q21, Q22, Q23, Q24]), "operationType" : NewBodyOperationType.ADD, "depth" : 2.5 * mm, "offsetDistance" : 25 * mm, "hasSecondDirection" : true, "secondDirectionOppositeDirection" : true, "secondDirectionDepth" : 0.4 * mm});
        }
    });
